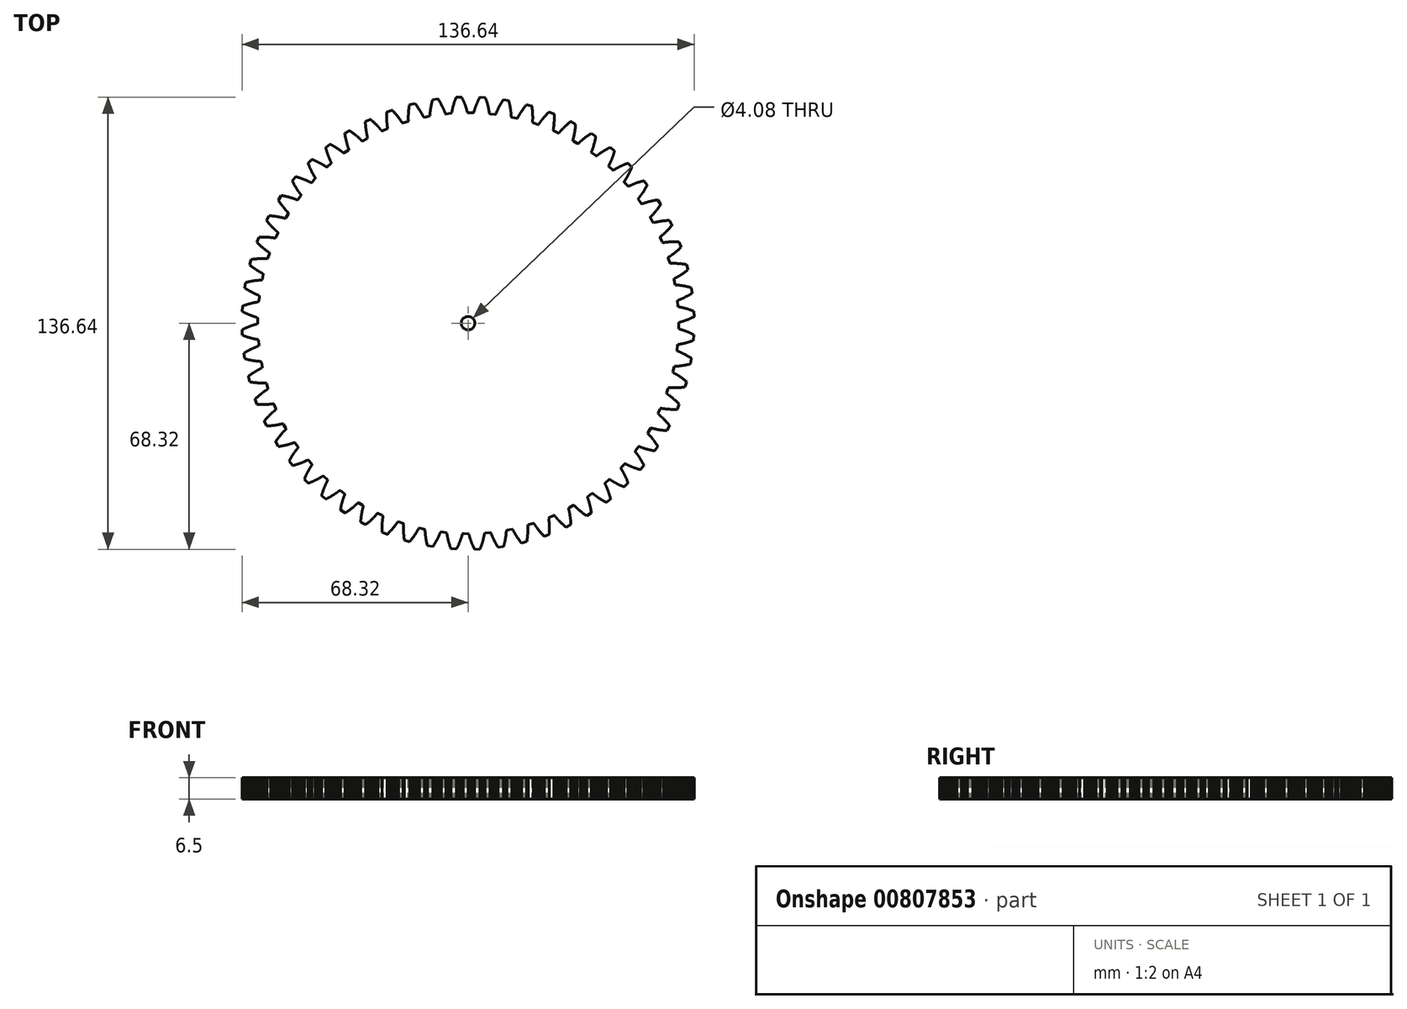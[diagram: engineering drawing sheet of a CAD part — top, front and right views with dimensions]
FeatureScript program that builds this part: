
annotation { "Feature Type Name" : "Feature", "Feature Type Description" : "" }
export const myFeature = defineFeature(function(context is Context, id is Id, definition is map)
    precondition{}
    {
        {
            var Q0;
            Q0=qCreatedBy(makeId("Top.planeOp"),FACE);
            var sketch = newSketch(context, id + "F0", { "sketchPlane" : qUnion([Q0])});
            skLineSegment(sketch, "E0", {"start": v(63.61, 0) * mm, "end": v(63.74, 0.24) * mm});
            skLineSegment(sketch, "E1", {"start": v(63.74, 0.24) * mm, "end": v(63.82, 0.26) * mm});
            skLineSegment(sketch, "E2", {"start": v(63.82, 0.26) * mm, "end": v(63.9, 0.28) * mm});
            skLineSegment(sketch, "E3", {"start": v(63.9, 0.28) * mm, "end": v(63.98, 0.3) * mm});
            skLineSegment(sketch, "E4", {"start": v(63.98, 0.3) * mm, "end": v(64.07, 0.32) * mm});
            skLineSegment(sketch, "E5", {"start": v(64.07, 0.32) * mm, "end": v(64.16, 0.35) * mm});
            skLineSegment(sketch, "E6", {"start": v(64.16, 0.35) * mm, "end": v(64.25, 0.37) * mm});
            skLineSegment(sketch, "E7", {"start": v(64.25, 0.37) * mm, "end": v(64.34, 0.4) * mm});
            skLineSegment(sketch, "E8", {"start": v(64.34, 0.4) * mm, "end": v(64.44, 0.42) * mm});
            skLineSegment(sketch, "E9", {"start": v(64.44, 0.42) * mm, "end": v(64.53, 0.45) * mm});
            skLineSegment(sketch, "E10", {"start": v(64.53, 0.45) * mm, "end": v(64.63, 0.48) * mm});
            skLineSegment(sketch, "E11", {"start": v(64.63, 0.48) * mm, "end": v(64.73, 0.5) * mm});
            skLineSegment(sketch, "E12", {"start": v(64.73, 0.5) * mm, "end": v(64.83, 0.54) * mm});
            skLineSegment(sketch, "E13", {"start": v(64.83, 0.54) * mm, "end": v(64.94, 0.57) * mm});
            skLineSegment(sketch, "E14", {"start": v(64.94, 0.57) * mm, "end": v(65.15, 0.64) * mm});
            skLineSegment(sketch, "E15", {"start": v(65.15, 0.64) * mm, "end": v(65.37, 0.7) * mm});
            skLineSegment(sketch, "E16", {"start": v(65.37, 0.7) * mm, "end": v(65.48, 0.75) * mm});
            skLineSegment(sketch, "E17", {"start": v(65.48, 0.75) * mm, "end": v(65.6, 0.79) * mm});
            skLineSegment(sketch, "E18", {"start": v(65.6, 0.79) * mm, "end": v(65.71, 0.83) * mm});
            skLineSegment(sketch, "E19", {"start": v(65.71, 0.83) * mm, "end": v(65.83, 0.87) * mm});
            skLineSegment(sketch, "E20", {"start": v(65.83, 0.87) * mm, "end": v(65.95, 0.91) * mm});
            skLineSegment(sketch, "E21", {"start": v(65.95, 0.91) * mm, "end": v(66.07, 0.96) * mm});
            skLineSegment(sketch, "E22", {"start": v(66.07, 0.96) * mm, "end": v(66.2, 1) * mm});
            skLineSegment(sketch, "E23", {"start": v(66.2, 1) * mm, "end": v(66.32, 1.05) * mm});
            skLineSegment(sketch, "E24", {"start": v(66.32, 1.05) * mm, "end": v(66.44, 1.1) * mm});
            skLineSegment(sketch, "E25", {"start": v(66.44, 1.1) * mm, "end": v(66.57, 1.16) * mm});
            skLineSegment(sketch, "E26", {"start": v(66.57, 1.16) * mm, "end": v(66.7, 1.2) * mm});
            skLineSegment(sketch, "E27", {"start": v(66.7, 1.2) * mm, "end": v(66.83, 1.26) * mm});
            skLineSegment(sketch, "E28", {"start": v(66.83, 1.26) * mm, "end": v(66.96, 1.32) * mm});
            skLineSegment(sketch, "E29", {"start": v(66.96, 1.32) * mm, "end": v(67.1, 1.38) * mm});
            skLineSegment(sketch, "E30", {"start": v(67.1, 1.38) * mm, "end": v(67.24, 1.44) * mm});
            skLineSegment(sketch, "E31", {"start": v(67.24, 1.44) * mm, "end": v(67.37, 1.5) * mm});
            skLineSegment(sketch, "E32", {"start": v(67.37, 1.5) * mm, "end": v(67.51, 1.56) * mm});
            skLineSegment(sketch, "E33", {"start": v(67.51, 1.56) * mm, "end": v(67.8, 1.69) * mm});
            skLineSegment(sketch, "E34", {"start": v(67.8, 1.69) * mm, "end": v(67.94, 1.76) * mm});
            skLineSegment(sketch, "E35", {"start": v(67.94, 1.76) * mm, "end": v(68.08, 1.83) * mm});
            skLineSegment(sketch, "E36", {"start": v(68.08, 1.83) * mm, "end": v(68.23, 1.9) * mm});
            skLineSegment(sketch, "E37", {"start": v(68.23, 1.9) * mm, "end": v(68.32, 1.97) * mm});
            skLineSegment(sketch, "E38", {"start": v(68.32, 1.97) * mm, "end": v(68.26, 3.6) * mm});
            skLineSegment(sketch, "E39", {"start": v(68.26, 3.6) * mm, "end": v(68.16, 3.66) * mm});
            skLineSegment(sketch, "E40", {"start": v(68.16, 3.66) * mm, "end": v(67.86, 3.77) * mm});
            skLineSegment(sketch, "E41", {"start": v(67.86, 3.77) * mm, "end": v(67.7, 3.83) * mm});
            skLineSegment(sketch, "E42", {"start": v(67.7, 3.83) * mm, "end": v(67.56, 3.88) * mm});
            skLineSegment(sketch, "E43", {"start": v(67.56, 3.88) * mm, "end": v(67.42, 3.94) * mm});
            skLineSegment(sketch, "E44", {"start": v(67.42, 3.94) * mm, "end": v(67.27, 3.99) * mm});
            skLineSegment(sketch, "E45", {"start": v(67.27, 3.99) * mm, "end": v(67.13, 4.04) * mm});
            skLineSegment(sketch, "E46", {"start": v(67.13, 4.04) * mm, "end": v(66.99, 4.08) * mm});
            skLineSegment(sketch, "E47", {"start": v(66.99, 4.08) * mm, "end": v(66.85, 4.13) * mm});
            skLineSegment(sketch, "E48", {"start": v(66.85, 4.13) * mm, "end": v(66.71, 4.18) * mm});
            skLineSegment(sketch, "E49", {"start": v(66.71, 4.18) * mm, "end": v(66.58, 4.22) * mm});
            skLineSegment(sketch, "E50", {"start": v(66.58, 4.22) * mm, "end": v(66.44, 4.26) * mm});
            skLineSegment(sketch, "E51", {"start": v(66.44, 4.26) * mm, "end": v(66.31, 4.3) * mm});
            skLineSegment(sketch, "E52", {"start": v(66.31, 4.3) * mm, "end": v(66.18, 4.34) * mm});
            skLineSegment(sketch, "E53", {"start": v(66.18, 4.34) * mm, "end": v(66.05, 4.38) * mm});
            skLineSegment(sketch, "E54", {"start": v(66.05, 4.38) * mm, "end": v(65.93, 4.42) * mm});
            skLineSegment(sketch, "E55", {"start": v(65.93, 4.42) * mm, "end": v(65.8, 4.45) * mm});
            skLineSegment(sketch, "E56", {"start": v(65.8, 4.45) * mm, "end": v(65.68, 4.49) * mm});
            skLineSegment(sketch, "E57", {"start": v(65.68, 4.49) * mm, "end": v(65.56, 4.52) * mm});
            skLineSegment(sketch, "E58", {"start": v(65.56, 4.52) * mm, "end": v(65.44, 4.55) * mm});
            skLineSegment(sketch, "E59", {"start": v(65.44, 4.55) * mm, "end": v(65.32, 4.58) * mm});
            skLineSegment(sketch, "E60", {"start": v(65.32, 4.58) * mm, "end": v(65.21, 4.6) * mm});
            skLineSegment(sketch, "E61", {"start": v(65.21, 4.6) * mm, "end": v(65.1, 4.64) * mm});
            skLineSegment(sketch, "E62", {"start": v(65.1, 4.64) * mm, "end": v(64.98, 4.66) * mm});
            skLineSegment(sketch, "E63", {"start": v(64.98, 4.66) * mm, "end": v(64.88, 4.69) * mm});
            skLineSegment(sketch, "E64", {"start": v(64.88, 4.69) * mm, "end": v(64.77, 4.71) * mm});
            skLineSegment(sketch, "E65", {"start": v(64.77, 4.71) * mm, "end": v(64.66, 4.74) * mm});
            skLineSegment(sketch, "E66", {"start": v(64.66, 4.74) * mm, "end": v(64.56, 4.76) * mm});
            skLineSegment(sketch, "E67", {"start": v(64.56, 4.76) * mm, "end": v(64.46, 4.78) * mm});
            skLineSegment(sketch, "E68", {"start": v(64.46, 4.78) * mm, "end": v(64.36, 4.8) * mm});
            skLineSegment(sketch, "E69", {"start": v(64.36, 4.8) * mm, "end": v(64.26, 4.82) * mm});
            skLineSegment(sketch, "E70", {"start": v(64.26, 4.82) * mm, "end": v(64.16, 4.84) * mm});
            skLineSegment(sketch, "E71", {"start": v(64.16, 4.84) * mm, "end": v(64.07, 4.86) * mm});
            skLineSegment(sketch, "E72", {"start": v(64.07, 4.86) * mm, "end": v(63.98, 4.87) * mm});
            skLineSegment(sketch, "E73", {"start": v(63.98, 4.87) * mm, "end": v(63.89, 4.89) * mm});
            skLineSegment(sketch, "E74", {"start": v(63.89, 4.89) * mm, "end": v(63.8, 4.9) * mm});
            skLineSegment(sketch, "E75", {"start": v(63.8, 4.9) * mm, "end": v(63.71, 4.92) * mm});
            skLineSegment(sketch, "E76", {"start": v(63.71, 4.92) * mm, "end": v(63.63, 4.93) * mm});
            skLineSegment(sketch, "E77", {"start": v(63.63, 4.93) * mm, "end": v(63.54, 4.94) * mm});
            skLineSegment(sketch, "E78", {"start": v(63.54, 4.94) * mm, "end": v(63.4, 5.17) * mm});
            skLineSegment(sketch, "E79", {"start": v(63.4, 5.17) * mm, "end": v(63.26, 6.65) * mm});
            skLineSegment(sketch, "E80", {"start": v(63.26, 6.65) * mm, "end": v(63.36, 6.9) * mm});
            skLineSegment(sketch, "E81", {"start": v(63.36, 6.9) * mm, "end": v(63.44, 6.93) * mm});
            skLineSegment(sketch, "E82", {"start": v(63.44, 6.93) * mm, "end": v(63.52, 6.96) * mm});
            skLineSegment(sketch, "E83", {"start": v(63.52, 6.96) * mm, "end": v(63.6, 6.99) * mm});
            skLineSegment(sketch, "E84", {"start": v(63.6, 6.99) * mm, "end": v(63.69, 7.02) * mm});
            skLineSegment(sketch, "E85", {"start": v(63.69, 7.02) * mm, "end": v(63.77, 7.05) * mm});
            skLineSegment(sketch, "E86", {"start": v(63.77, 7.05) * mm, "end": v(63.86, 7.08) * mm});
            skLineSegment(sketch, "E87", {"start": v(63.86, 7.08) * mm, "end": v(63.95, 7.12) * mm});
            skLineSegment(sketch, "E88", {"start": v(63.95, 7.12) * mm, "end": v(64.04, 7.15) * mm});
            skLineSegment(sketch, "E89", {"start": v(64.04, 7.15) * mm, "end": v(64.13, 7.2) * mm});
            skLineSegment(sketch, "E90", {"start": v(64.13, 7.2) * mm, "end": v(64.23, 7.23) * mm});
            skLineSegment(sketch, "E91", {"start": v(64.23, 7.23) * mm, "end": v(64.32, 7.27) * mm});
            skLineSegment(sketch, "E92", {"start": v(64.32, 7.27) * mm, "end": v(64.42, 7.31) * mm});
            skLineSegment(sketch, "E93", {"start": v(64.42, 7.31) * mm, "end": v(64.52, 7.35) * mm});
            skLineSegment(sketch, "E94", {"start": v(64.52, 7.35) * mm, "end": v(64.62, 7.4) * mm});
            skLineSegment(sketch, "E95", {"start": v(64.62, 7.4) * mm, "end": v(64.73, 7.44) * mm});
            skLineSegment(sketch, "E96", {"start": v(64.73, 7.44) * mm, "end": v(64.83, 7.49) * mm});
            skLineSegment(sketch, "E97", {"start": v(64.83, 7.49) * mm, "end": v(64.94, 7.54) * mm});
            skLineSegment(sketch, "E98", {"start": v(64.94, 7.54) * mm, "end": v(65.04, 7.59) * mm});
            skLineSegment(sketch, "E99", {"start": v(65.04, 7.59) * mm, "end": v(65.15, 7.64) * mm});
            skLineSegment(sketch, "E100", {"start": v(65.15, 7.64) * mm, "end": v(65.27, 7.7) * mm});
            skLineSegment(sketch, "E101", {"start": v(65.27, 7.7) * mm, "end": v(65.38, 7.75) * mm});
            skLineSegment(sketch, "E102", {"start": v(65.38, 7.75) * mm, "end": v(65.5, 7.8) * mm});
            skLineSegment(sketch, "E103", {"start": v(65.5, 7.8) * mm, "end": v(65.6, 7.86) * mm});
            skLineSegment(sketch, "E104", {"start": v(65.6, 7.86) * mm, "end": v(65.72, 7.92) * mm});
            skLineSegment(sketch, "E105", {"start": v(65.72, 7.92) * mm, "end": v(65.96, 8.04) * mm});
            skLineSegment(sketch, "E106", {"start": v(65.96, 8.04) * mm, "end": v(66.09, 8.1) * mm});
            skLineSegment(sketch, "E107", {"start": v(66.09, 8.1) * mm, "end": v(66.2, 8.17) * mm});
            skLineSegment(sketch, "E108", {"start": v(66.2, 8.17) * mm, "end": v(66.33, 8.24) * mm});
            skLineSegment(sketch, "E109", {"start": v(66.33, 8.24) * mm, "end": v(66.46, 8.31) * mm});
            skLineSegment(sketch, "E110", {"start": v(66.46, 8.31) * mm, "end": v(66.59, 8.38) * mm});
            skLineSegment(sketch, "E111", {"start": v(66.59, 8.38) * mm, "end": v(66.72, 8.46) * mm});
            skLineSegment(sketch, "E112", {"start": v(66.72, 8.46) * mm, "end": v(66.85, 8.53) * mm});
            skLineSegment(sketch, "E113", {"start": v(66.85, 8.53) * mm, "end": v(66.98, 8.6) * mm});
            skLineSegment(sketch, "E114", {"start": v(66.98, 8.6) * mm, "end": v(67.11, 8.69) * mm});
            skLineSegment(sketch, "E115", {"start": v(67.11, 8.69) * mm, "end": v(67.25, 8.77) * mm});
            skLineSegment(sketch, "E116", {"start": v(67.25, 8.77) * mm, "end": v(67.38, 8.85) * mm});
            skLineSegment(sketch, "E117", {"start": v(67.38, 8.85) * mm, "end": v(67.52, 8.93) * mm});
            skLineSegment(sketch, "E118", {"start": v(67.52, 8.93) * mm, "end": v(67.66, 9.02) * mm});
            skLineSegment(sketch, "E119", {"start": v(67.66, 9.02) * mm, "end": v(67.74, 9.1) * mm});
            skLineSegment(sketch, "E120", {"start": v(67.74, 9.1) * mm, "end": v(67.5, 10.7) * mm});
            skLineSegment(sketch, "E121", {"start": v(67.5, 10.7) * mm, "end": v(67.4, 10.76) * mm});
            skLineSegment(sketch, "E122", {"start": v(67.4, 10.76) * mm, "end": v(67.25, 10.8) * mm});
            skLineSegment(sketch, "E123", {"start": v(67.25, 10.8) * mm, "end": v(67.09, 10.85) * mm});
            skLineSegment(sketch, "E124", {"start": v(67.09, 10.85) * mm, "end": v(66.94, 10.89) * mm});
            skLineSegment(sketch, "E125", {"start": v(66.94, 10.89) * mm, "end": v(66.78, 10.93) * mm});
            skLineSegment(sketch, "E126", {"start": v(66.78, 10.93) * mm, "end": v(66.64, 10.96) * mm});
            skLineSegment(sketch, "E127", {"start": v(66.64, 10.96) * mm, "end": v(66.49, 11) * mm});
            skLineSegment(sketch, "E128", {"start": v(66.49, 11) * mm, "end": v(66.34, 11.03) * mm});
            skLineSegment(sketch, "E129", {"start": v(66.34, 11.03) * mm, "end": v(66.2, 11.06) * mm});
            skLineSegment(sketch, "E130", {"start": v(66.2, 11.06) * mm, "end": v(66.05, 11.1) * mm});
            skLineSegment(sketch, "E131", {"start": v(66.05, 11.1) * mm, "end": v(65.91, 11.13) * mm});
            skLineSegment(sketch, "E132", {"start": v(65.91, 11.13) * mm, "end": v(65.77, 11.16) * mm});
            skLineSegment(sketch, "E133", {"start": v(65.77, 11.16) * mm, "end": v(65.64, 11.18) * mm});
            skLineSegment(sketch, "E134", {"start": v(65.64, 11.18) * mm, "end": v(65.5, 11.21) * mm});
            skLineSegment(sketch, "E135", {"start": v(65.5, 11.21) * mm, "end": v(65.37, 11.24) * mm});
            skLineSegment(sketch, "E136", {"start": v(65.37, 11.24) * mm, "end": v(65.23, 11.26) * mm});
            skLineSegment(sketch, "E137", {"start": v(65.23, 11.26) * mm, "end": v(65.1, 11.28) * mm});
            skLineSegment(sketch, "E138", {"start": v(65.1, 11.28) * mm, "end": v(64.98, 11.3) * mm});
            skLineSegment(sketch, "E139", {"start": v(64.98, 11.3) * mm, "end": v(64.85, 11.33) * mm});
            skLineSegment(sketch, "E140", {"start": v(64.85, 11.33) * mm, "end": v(64.73, 11.35) * mm});
            skLineSegment(sketch, "E141", {"start": v(64.73, 11.35) * mm, "end": v(64.6, 11.37) * mm});
            skLineSegment(sketch, "E142", {"start": v(64.6, 11.37) * mm, "end": v(64.49, 11.38) * mm});
            skLineSegment(sketch, "E143", {"start": v(64.49, 11.38) * mm, "end": v(64.37, 11.4) * mm});
            skLineSegment(sketch, "E144", {"start": v(64.37, 11.4) * mm, "end": v(64.26, 11.42) * mm});
            skLineSegment(sketch, "E145", {"start": v(64.26, 11.42) * mm, "end": v(64.14, 11.43) * mm});
            skLineSegment(sketch, "E146", {"start": v(64.14, 11.43) * mm, "end": v(64.03, 11.44) * mm});
            skLineSegment(sketch, "E147", {"start": v(64.03, 11.44) * mm, "end": v(63.92, 11.46) * mm});
            skLineSegment(sketch, "E148", {"start": v(63.92, 11.46) * mm, "end": v(63.81, 11.47) * mm});
            skLineSegment(sketch, "E149", {"start": v(63.81, 11.47) * mm, "end": v(63.7, 11.48) * mm});
            skLineSegment(sketch, "E150", {"start": v(63.7, 11.48) * mm, "end": v(63.6, 11.5) * mm});
            skLineSegment(sketch, "E151", {"start": v(63.6, 11.5) * mm, "end": v(63.5, 11.5) * mm});
            skLineSegment(sketch, "E152", {"start": v(63.5, 11.5) * mm, "end": v(63.4, 11.51) * mm});
            skLineSegment(sketch, "E153", {"start": v(63.4, 11.51) * mm, "end": v(63.3, 11.52) * mm});
            skLineSegment(sketch, "E154", {"start": v(63.3, 11.52) * mm, "end": v(63.2, 11.53) * mm});
            skLineSegment(sketch, "E155", {"start": v(63.2, 11.53) * mm, "end": v(63.12, 11.53) * mm});
            skLineSegment(sketch, "E156", {"start": v(63.12, 11.53) * mm, "end": v(63.02, 11.54) * mm});
            skLineSegment(sketch, "E157", {"start": v(63.02, 11.54) * mm, "end": v(62.93, 11.55) * mm});
            skLineSegment(sketch, "E158", {"start": v(62.93, 11.55) * mm, "end": v(62.85, 11.55) * mm});
            skLineSegment(sketch, "E159", {"start": v(62.85, 11.55) * mm, "end": v(62.76, 11.55) * mm});
            skLineSegment(sketch, "E160", {"start": v(62.76, 11.55) * mm, "end": v(62.68, 11.56) * mm});
            skLineSegment(sketch, "E161", {"start": v(62.68, 11.56) * mm, "end": v(62.51, 11.77) * mm});
            skLineSegment(sketch, "E162", {"start": v(62.51, 11.77) * mm, "end": v(62.22, 13.22) * mm});
            skLineSegment(sketch, "E163", {"start": v(62.22, 13.22) * mm, "end": v(62.3, 13.49) * mm});
            skLineSegment(sketch, "E164", {"start": v(62.3, 13.49) * mm, "end": v(62.37, 13.52) * mm});
            skLineSegment(sketch, "E165", {"start": v(62.37, 13.52) * mm, "end": v(62.45, 13.56) * mm});
            skLineSegment(sketch, "E166", {"start": v(62.45, 13.56) * mm, "end": v(62.52, 13.6) * mm});
            skLineSegment(sketch, "E167", {"start": v(62.52, 13.6) * mm, "end": v(62.6, 13.64) * mm});
            skLineSegment(sketch, "E168", {"start": v(62.6, 13.64) * mm, "end": v(62.69, 13.68) * mm});
            skLineSegment(sketch, "E169", {"start": v(62.69, 13.68) * mm, "end": v(62.77, 13.72) * mm});
            skLineSegment(sketch, "E170", {"start": v(62.77, 13.72) * mm, "end": v(62.86, 13.76) * mm});
            skLineSegment(sketch, "E171", {"start": v(62.86, 13.76) * mm, "end": v(62.94, 13.8) * mm});
            skLineSegment(sketch, "E172", {"start": v(62.94, 13.8) * mm, "end": v(63.03, 13.85) * mm});
            skLineSegment(sketch, "E173", {"start": v(63.03, 13.85) * mm, "end": v(63.12, 13.9) * mm});
            skLineSegment(sketch, "E174", {"start": v(63.12, 13.9) * mm, "end": v(63.21, 13.95) * mm});
            skLineSegment(sketch, "E175", {"start": v(63.21, 13.95) * mm, "end": v(63.3, 14) * mm});
            skLineSegment(sketch, "E176", {"start": v(63.3, 14) * mm, "end": v(63.4, 14.06) * mm});
            skLineSegment(sketch, "E177", {"start": v(63.4, 14.06) * mm, "end": v(63.5, 14.11) * mm});
            skLineSegment(sketch, "E178", {"start": v(63.5, 14.11) * mm, "end": v(63.6, 14.17) * mm});
            skLineSegment(sketch, "E179", {"start": v(63.6, 14.17) * mm, "end": v(63.7, 14.23) * mm});
            skLineSegment(sketch, "E180", {"start": v(63.7, 14.23) * mm, "end": v(63.8, 14.28) * mm});
            skLineSegment(sketch, "E181", {"start": v(63.8, 14.28) * mm, "end": v(63.9, 14.35) * mm});
            skLineSegment(sketch, "E182", {"start": v(63.9, 14.35) * mm, "end": v(64, 14.4) * mm});
            skLineSegment(sketch, "E183", {"start": v(64, 14.4) * mm, "end": v(64.1, 14.47) * mm});
            skLineSegment(sketch, "E184", {"start": v(64.1, 14.47) * mm, "end": v(64.2, 14.54) * mm});
            skLineSegment(sketch, "E185", {"start": v(64.2, 14.54) * mm, "end": v(64.32, 14.6) * mm});
            skLineSegment(sketch, "E186", {"start": v(64.32, 14.6) * mm, "end": v(64.43, 14.67) * mm});
            skLineSegment(sketch, "E187", {"start": v(64.43, 14.67) * mm, "end": v(64.54, 14.75) * mm});
            skLineSegment(sketch, "E188", {"start": v(64.54, 14.75) * mm, "end": v(64.65, 14.82) * mm});
            skLineSegment(sketch, "E189", {"start": v(64.65, 14.82) * mm, "end": v(64.76, 14.9) * mm});
            skLineSegment(sketch, "E190", {"start": v(64.76, 14.9) * mm, "end": v(64.88, 14.97) * mm});
            skLineSegment(sketch, "E191", {"start": v(64.88, 14.97) * mm, "end": v(65, 15.05) * mm});
            skLineSegment(sketch, "E192", {"start": v(65, 15.05) * mm, "end": v(65.23, 15.21) * mm});
            skLineSegment(sketch, "E193", {"start": v(65.23, 15.21) * mm, "end": v(65.35, 15.3) * mm});
            skLineSegment(sketch, "E194", {"start": v(65.35, 15.3) * mm, "end": v(65.47, 15.38) * mm});
            skLineSegment(sketch, "E195", {"start": v(65.47, 15.38) * mm, "end": v(65.59, 15.47) * mm});
            skLineSegment(sketch, "E196", {"start": v(65.59, 15.47) * mm, "end": v(65.71, 15.56) * mm});
            skLineSegment(sketch, "E197", {"start": v(65.71, 15.56) * mm, "end": v(65.84, 15.65) * mm});
            skLineSegment(sketch, "E198", {"start": v(65.84, 15.65) * mm, "end": v(65.96, 15.75) * mm});
            skLineSegment(sketch, "E199", {"start": v(65.96, 15.75) * mm, "end": v(66.09, 15.84) * mm});
            skLineSegment(sketch, "E200", {"start": v(66.09, 15.84) * mm, "end": v(66.22, 15.94) * mm});
            skLineSegment(sketch, "E201", {"start": v(66.22, 15.94) * mm, "end": v(66.35, 16.04) * mm});
            skLineSegment(sketch, "E202", {"start": v(66.35, 16.04) * mm, "end": v(66.42, 16.13) * mm});
            skLineSegment(sketch, "E203", {"start": v(66.42, 16.13) * mm, "end": v(66.02, 17.7) * mm});
            skLineSegment(sketch, "E204", {"start": v(66.02, 17.7) * mm, "end": v(65.9, 17.75) * mm});
            skLineSegment(sketch, "E205", {"start": v(65.9, 17.75) * mm, "end": v(65.75, 17.78) * mm});
            skLineSegment(sketch, "E206", {"start": v(65.75, 17.78) * mm, "end": v(65.59, 17.8) * mm});
            skLineSegment(sketch, "E207", {"start": v(65.59, 17.8) * mm, "end": v(65.43, 17.82) * mm});
            skLineSegment(sketch, "E208", {"start": v(65.43, 17.82) * mm, "end": v(65.28, 17.85) * mm});
            skLineSegment(sketch, "E209", {"start": v(65.28, 17.85) * mm, "end": v(65.12, 17.87) * mm});
            skLineSegment(sketch, "E210", {"start": v(65.12, 17.87) * mm, "end": v(64.97, 17.89) * mm});
            skLineSegment(sketch, "E211", {"start": v(64.97, 17.89) * mm, "end": v(64.82, 17.9) * mm});
            skLineSegment(sketch, "E212", {"start": v(64.82, 17.9) * mm, "end": v(64.68, 17.92) * mm});
            skLineSegment(sketch, "E213", {"start": v(64.68, 17.92) * mm, "end": v(64.53, 17.94) * mm});
            skLineSegment(sketch, "E214", {"start": v(64.53, 17.94) * mm, "end": v(64.39, 17.96) * mm});
            skLineSegment(sketch, "E215", {"start": v(64.39, 17.96) * mm, "end": v(64.25, 17.97) * mm});
            skLineSegment(sketch, "E216", {"start": v(64.25, 17.97) * mm, "end": v(64.1, 17.98) * mm});
            skLineSegment(sketch, "E217", {"start": v(64.1, 17.98) * mm, "end": v(63.97, 18) * mm});
            skLineSegment(sketch, "E218", {"start": v(63.97, 18) * mm, "end": v(63.83, 18) * mm});
            skLineSegment(sketch, "E219", {"start": v(63.83, 18) * mm, "end": v(63.7, 18.02) * mm});
            skLineSegment(sketch, "E220", {"start": v(63.7, 18.02) * mm, "end": v(63.57, 18.03) * mm});
            skLineSegment(sketch, "E221", {"start": v(63.57, 18.03) * mm, "end": v(63.44, 18.04) * mm});
            skLineSegment(sketch, "E222", {"start": v(63.44, 18.04) * mm, "end": v(63.31, 18.04) * mm});
            skLineSegment(sketch, "E223", {"start": v(63.31, 18.04) * mm, "end": v(63.19, 18.05) * mm});
            skLineSegment(sketch, "E224", {"start": v(63.19, 18.05) * mm, "end": v(63.07, 18.06) * mm});
            skLineSegment(sketch, "E225", {"start": v(63.07, 18.06) * mm, "end": v(62.94, 18.06) * mm});
            skLineSegment(sketch, "E226", {"start": v(62.94, 18.06) * mm, "end": v(62.83, 18.07) * mm});
            skLineSegment(sketch, "E227", {"start": v(62.83, 18.07) * mm, "end": v(62.7, 18.07) * mm});
            skLineSegment(sketch, "E228", {"start": v(62.7, 18.07) * mm, "end": v(62.6, 18.07) * mm});
            skLineSegment(sketch, "E229", {"start": v(62.6, 18.07) * mm, "end": v(62.48, 18.08) * mm});
            skLineSegment(sketch, "E230", {"start": v(62.48, 18.08) * mm, "end": v(62.37, 18.08) * mm});
            skLineSegment(sketch, "E231", {"start": v(62.37, 18.08) * mm, "end": v(62.26, 18.08) * mm});
            skLineSegment(sketch, "E232", {"start": v(62.26, 18.08) * mm, "end": v(62.05, 18.08) * mm});
            skLineSegment(sketch, "E233", {"start": v(62.05, 18.08) * mm, "end": v(61.95, 18.08) * mm});
            skLineSegment(sketch, "E234", {"start": v(61.95, 18.08) * mm, "end": v(61.85, 18.08) * mm});
            skLineSegment(sketch, "E235", {"start": v(61.85, 18.08) * mm, "end": v(61.75, 18.07) * mm});
            skLineSegment(sketch, "E236", {"start": v(61.75, 18.07) * mm, "end": v(61.66, 18.07) * mm});
            skLineSegment(sketch, "E237", {"start": v(61.66, 18.07) * mm, "end": v(61.56, 18.07) * mm});
            skLineSegment(sketch, "E238", {"start": v(61.56, 18.07) * mm, "end": v(61.47, 18.06) * mm});
            skLineSegment(sketch, "E239", {"start": v(61.47, 18.06) * mm, "end": v(61.38, 18.06) * mm});
            skLineSegment(sketch, "E240", {"start": v(61.38, 18.06) * mm, "end": v(61.3, 18.06) * mm});
            skLineSegment(sketch, "E241", {"start": v(61.3, 18.06) * mm, "end": v(61.21, 18.05) * mm});
            skLineSegment(sketch, "E242", {"start": v(61.21, 18.05) * mm, "end": v(61.13, 18.05) * mm});
            skLineSegment(sketch, "E243", {"start": v(61.13, 18.05) * mm, "end": v(60.94, 18.24) * mm});
            skLineSegment(sketch, "E244", {"start": v(60.94, 18.24) * mm, "end": v(60.5, 19.66) * mm});
            skLineSegment(sketch, "E245", {"start": v(60.5, 19.66) * mm, "end": v(60.54, 19.92) * mm});
            skLineSegment(sketch, "E246", {"start": v(60.54, 19.92) * mm, "end": v(60.61, 19.97) * mm});
            skLineSegment(sketch, "E247", {"start": v(60.61, 19.97) * mm, "end": v(60.69, 20.01) * mm});
            skLineSegment(sketch, "E248", {"start": v(60.69, 20.01) * mm, "end": v(60.76, 20.06) * mm});
            skLineSegment(sketch, "E249", {"start": v(60.76, 20.06) * mm, "end": v(60.84, 20.1) * mm});
            skLineSegment(sketch, "E250", {"start": v(60.84, 20.1) * mm, "end": v(60.91, 20.16) * mm});
            skLineSegment(sketch, "E251", {"start": v(60.91, 20.16) * mm, "end": v(61, 20.2) * mm});
            skLineSegment(sketch, "E252", {"start": v(61, 20.2) * mm, "end": v(61.07, 20.26) * mm});
            skLineSegment(sketch, "E253", {"start": v(61.07, 20.26) * mm, "end": v(61.15, 20.31) * mm});
            skLineSegment(sketch, "E254", {"start": v(61.15, 20.31) * mm, "end": v(61.24, 20.37) * mm});
            skLineSegment(sketch, "E255", {"start": v(61.24, 20.37) * mm, "end": v(61.32, 20.43) * mm});
            skLineSegment(sketch, "E256", {"start": v(61.32, 20.43) * mm, "end": v(61.4, 20.48) * mm});
            skLineSegment(sketch, "E257", {"start": v(61.4, 20.48) * mm, "end": v(61.5, 20.55) * mm});
            skLineSegment(sketch, "E258", {"start": v(61.5, 20.55) * mm, "end": v(61.58, 20.6) * mm});
            skLineSegment(sketch, "E259", {"start": v(61.58, 20.6) * mm, "end": v(61.67, 20.67) * mm});
            skLineSegment(sketch, "E260", {"start": v(61.67, 20.67) * mm, "end": v(61.76, 20.74) * mm});
            skLineSegment(sketch, "E261", {"start": v(61.76, 20.74) * mm, "end": v(61.86, 20.8) * mm});
            skLineSegment(sketch, "E262", {"start": v(61.86, 20.8) * mm, "end": v(61.95, 20.87) * mm});
            skLineSegment(sketch, "E263", {"start": v(61.95, 20.87) * mm, "end": v(62.04, 20.94) * mm});
            skLineSegment(sketch, "E264", {"start": v(62.04, 20.94) * mm, "end": v(62.14, 21.02) * mm});
            skLineSegment(sketch, "E265", {"start": v(62.14, 21.02) * mm, "end": v(62.24, 21.1) * mm});
            skLineSegment(sketch, "E266", {"start": v(62.24, 21.1) * mm, "end": v(62.34, 21.17) * mm});
            skLineSegment(sketch, "E267", {"start": v(62.34, 21.17) * mm, "end": v(62.44, 21.25) * mm});
            skLineSegment(sketch, "E268", {"start": v(62.44, 21.25) * mm, "end": v(62.54, 21.33) * mm});
            skLineSegment(sketch, "E269", {"start": v(62.54, 21.33) * mm, "end": v(62.64, 21.41) * mm});
            skLineSegment(sketch, "E270", {"start": v(62.64, 21.41) * mm, "end": v(62.74, 21.5) * mm});
            skLineSegment(sketch, "E271", {"start": v(62.74, 21.5) * mm, "end": v(62.85, 21.58) * mm});
            skLineSegment(sketch, "E272", {"start": v(62.85, 21.58) * mm, "end": v(62.96, 21.67) * mm});
            skLineSegment(sketch, "E273", {"start": v(62.96, 21.67) * mm, "end": v(63.06, 21.76) * mm});
            skLineSegment(sketch, "E274", {"start": v(63.06, 21.76) * mm, "end": v(63.17, 21.85) * mm});
            skLineSegment(sketch, "E275", {"start": v(63.17, 21.85) * mm, "end": v(63.28, 21.95) * mm});
            skLineSegment(sketch, "E276", {"start": v(63.28, 21.95) * mm, "end": v(63.39, 22.04) * mm});
            skLineSegment(sketch, "E277", {"start": v(63.39, 22.04) * mm, "end": v(63.5, 22.14) * mm});
            skLineSegment(sketch, "E278", {"start": v(63.5, 22.14) * mm, "end": v(63.61, 22.24) * mm});
            skLineSegment(sketch, "E279", {"start": v(63.61, 22.24) * mm, "end": v(63.73, 22.34) * mm});
            skLineSegment(sketch, "E280", {"start": v(63.73, 22.34) * mm, "end": v(63.84, 22.45) * mm});
            skLineSegment(sketch, "E281", {"start": v(63.84, 22.45) * mm, "end": v(63.95, 22.56) * mm});
            skLineSegment(sketch, "E282", {"start": v(63.95, 22.56) * mm, "end": v(64.07, 22.66) * mm});
            skLineSegment(sketch, "E283", {"start": v(64.07, 22.66) * mm, "end": v(64.19, 22.77) * mm});
            skLineSegment(sketch, "E284", {"start": v(64.19, 22.77) * mm, "end": v(64.3, 22.89) * mm});
            skLineSegment(sketch, "E285", {"start": v(64.3, 22.89) * mm, "end": v(64.37, 22.98) * mm});
            skLineSegment(sketch, "E286", {"start": v(64.37, 22.98) * mm, "end": v(63.8, 24.51) * mm});
            skLineSegment(sketch, "E287", {"start": v(63.8, 24.51) * mm, "end": v(63.7, 24.54) * mm});
            skLineSegment(sketch, "E288", {"start": v(63.7, 24.54) * mm, "end": v(63.53, 24.55) * mm});
            skLineSegment(sketch, "E289", {"start": v(63.53, 24.55) * mm, "end": v(63.37, 24.56) * mm});
            skLineSegment(sketch, "E290", {"start": v(63.37, 24.56) * mm, "end": v(63.21, 24.56) * mm});
            skLineSegment(sketch, "E291", {"start": v(63.21, 24.56) * mm, "end": v(63.05, 24.57) * mm});
            skLineSegment(sketch, "E292", {"start": v(63.05, 24.57) * mm, "end": v(62.9, 24.58) * mm});
            skLineSegment(sketch, "E293", {"start": v(62.9, 24.58) * mm, "end": v(62.75, 24.58) * mm});
            skLineSegment(sketch, "E294", {"start": v(62.75, 24.58) * mm, "end": v(62.6, 24.58) * mm});
            skLineSegment(sketch, "E295", {"start": v(62.6, 24.58) * mm, "end": v(62.45, 24.59) * mm});
            skLineSegment(sketch, "E296", {"start": v(62.45, 24.59) * mm, "end": v(62.3, 24.59) * mm});
            skLineSegment(sketch, "E297", {"start": v(62.3, 24.59) * mm, "end": v(62.02, 24.59) * mm});
            skLineSegment(sketch, "E298", {"start": v(62.02, 24.59) * mm, "end": v(61.88, 24.59) * mm});
            skLineSegment(sketch, "E299", {"start": v(61.88, 24.59) * mm, "end": v(61.74, 24.58) * mm});
            skLineSegment(sketch, "E300", {"start": v(61.74, 24.58) * mm, "end": v(61.6, 24.58) * mm});
            skLineSegment(sketch, "E301", {"start": v(61.6, 24.58) * mm, "end": v(61.47, 24.58) * mm});
            skLineSegment(sketch, "E302", {"start": v(61.47, 24.58) * mm, "end": v(61.34, 24.57) * mm});
            skLineSegment(sketch, "E303", {"start": v(61.34, 24.57) * mm, "end": v(61.2, 24.57) * mm});
            skLineSegment(sketch, "E304", {"start": v(61.2, 24.57) * mm, "end": v(61.08, 24.56) * mm});
            skLineSegment(sketch, "E305", {"start": v(61.08, 24.56) * mm, "end": v(60.96, 24.56) * mm});
            skLineSegment(sketch, "E306", {"start": v(60.96, 24.56) * mm, "end": v(60.83, 24.55) * mm});
            skLineSegment(sketch, "E307", {"start": v(60.83, 24.55) * mm, "end": v(60.71, 24.54) * mm});
            skLineSegment(sketch, "E308", {"start": v(60.71, 24.54) * mm, "end": v(60.6, 24.53) * mm});
            skLineSegment(sketch, "E309", {"start": v(60.6, 24.53) * mm, "end": v(60.48, 24.53) * mm});
            skLineSegment(sketch, "E310", {"start": v(60.48, 24.53) * mm, "end": v(60.25, 24.5) * mm});
            skLineSegment(sketch, "E311", {"start": v(60.25, 24.5) * mm, "end": v(60.14, 24.5) * mm});
            skLineSegment(sketch, "E312", {"start": v(60.14, 24.5) * mm, "end": v(60.03, 24.49) * mm});
            skLineSegment(sketch, "E313", {"start": v(60.03, 24.49) * mm, "end": v(59.93, 24.48) * mm});
            skLineSegment(sketch, "E314", {"start": v(59.93, 24.48) * mm, "end": v(59.82, 24.47) * mm});
            skLineSegment(sketch, "E315", {"start": v(59.82, 24.47) * mm, "end": v(59.72, 24.45) * mm});
            skLineSegment(sketch, "E316", {"start": v(59.72, 24.45) * mm, "end": v(59.62, 24.44) * mm});
            skLineSegment(sketch, "E317", {"start": v(59.62, 24.44) * mm, "end": v(59.53, 24.43) * mm});
            skLineSegment(sketch, "E318", {"start": v(59.53, 24.43) * mm, "end": v(59.43, 24.42) * mm});
            skLineSegment(sketch, "E319", {"start": v(59.43, 24.42) * mm, "end": v(59.34, 24.4) * mm});
            skLineSegment(sketch, "E320", {"start": v(59.34, 24.4) * mm, "end": v(59.25, 24.4) * mm});
            skLineSegment(sketch, "E321", {"start": v(59.25, 24.4) * mm, "end": v(59.16, 24.38) * mm});
            skLineSegment(sketch, "E322", {"start": v(59.16, 24.38) * mm, "end": v(59.07, 24.37) * mm});
            skLineSegment(sketch, "E323", {"start": v(59.07, 24.37) * mm, "end": v(58.99, 24.35) * mm});
            skLineSegment(sketch, "E324", {"start": v(58.99, 24.35) * mm, "end": v(58.9, 24.34) * mm});
            skLineSegment(sketch, "E325", {"start": v(58.9, 24.34) * mm, "end": v(58.7, 24.51) * mm});
            skLineSegment(sketch, "E326", {"start": v(58.7, 24.51) * mm, "end": v(58.11, 25.87) * mm});
            skLineSegment(sketch, "E327", {"start": v(58.11, 25.87) * mm, "end": v(58.13, 26.14) * mm});
            skLineSegment(sketch, "E328", {"start": v(58.13, 26.14) * mm, "end": v(58.2, 26.2) * mm});
            skLineSegment(sketch, "E329", {"start": v(58.2, 26.2) * mm, "end": v(58.26, 26.25) * mm});
            skLineSegment(sketch, "E330", {"start": v(58.26, 26.25) * mm, "end": v(58.33, 26.3) * mm});
            skLineSegment(sketch, "E331", {"start": v(58.33, 26.3) * mm, "end": v(58.4, 26.35) * mm});
            skLineSegment(sketch, "E332", {"start": v(58.4, 26.35) * mm, "end": v(58.47, 26.41) * mm});
            skLineSegment(sketch, "E333", {"start": v(58.47, 26.41) * mm, "end": v(58.55, 26.47) * mm});
            skLineSegment(sketch, "E334", {"start": v(58.55, 26.47) * mm, "end": v(58.62, 26.53) * mm});
            skLineSegment(sketch, "E335", {"start": v(58.62, 26.53) * mm, "end": v(58.7, 26.6) * mm});
            skLineSegment(sketch, "E336", {"start": v(58.7, 26.6) * mm, "end": v(58.77, 26.66) * mm});
            skLineSegment(sketch, "E337", {"start": v(58.77, 26.66) * mm, "end": v(58.85, 26.72) * mm});
            skLineSegment(sketch, "E338", {"start": v(58.85, 26.72) * mm, "end": v(58.93, 26.8) * mm});
            skLineSegment(sketch, "E339", {"start": v(58.93, 26.8) * mm, "end": v(59, 26.86) * mm});
            skLineSegment(sketch, "E340", {"start": v(59, 26.86) * mm, "end": v(59.1, 26.93) * mm});
            skLineSegment(sketch, "E341", {"start": v(59.1, 26.93) * mm, "end": v(59.17, 27) * mm});
            skLineSegment(sketch, "E342", {"start": v(59.17, 27) * mm, "end": v(59.26, 27.08) * mm});
            skLineSegment(sketch, "E343", {"start": v(59.26, 27.08) * mm, "end": v(59.34, 27.16) * mm});
            skLineSegment(sketch, "E344", {"start": v(59.34, 27.16) * mm, "end": v(59.43, 27.24) * mm});
            skLineSegment(sketch, "E345", {"start": v(59.43, 27.24) * mm, "end": v(59.52, 27.32) * mm});
            skLineSegment(sketch, "E346", {"start": v(59.52, 27.32) * mm, "end": v(59.6, 27.4) * mm});
            skLineSegment(sketch, "E347", {"start": v(59.6, 27.4) * mm, "end": v(59.7, 27.48) * mm});
            skLineSegment(sketch, "E348", {"start": v(59.7, 27.48) * mm, "end": v(59.78, 27.57) * mm});
            skLineSegment(sketch, "E349", {"start": v(59.78, 27.57) * mm, "end": v(59.87, 27.66) * mm});
            skLineSegment(sketch, "E350", {"start": v(59.87, 27.66) * mm, "end": v(59.97, 27.75) * mm});
            skLineSegment(sketch, "E351", {"start": v(59.97, 27.75) * mm, "end": v(60.06, 27.84) * mm});
            skLineSegment(sketch, "E352", {"start": v(60.06, 27.84) * mm, "end": v(60.15, 27.94) * mm});
            skLineSegment(sketch, "E353", {"start": v(60.15, 27.94) * mm, "end": v(60.25, 28.03) * mm});
            skLineSegment(sketch, "E354", {"start": v(60.25, 28.03) * mm, "end": v(60.35, 28.13) * mm});
            skLineSegment(sketch, "E355", {"start": v(60.35, 28.13) * mm, "end": v(60.44, 28.23) * mm});
            skLineSegment(sketch, "E356", {"start": v(60.44, 28.23) * mm, "end": v(60.54, 28.34) * mm});
            skLineSegment(sketch, "E357", {"start": v(60.54, 28.34) * mm, "end": v(60.64, 28.44) * mm});
            skLineSegment(sketch, "E358", {"start": v(60.64, 28.44) * mm, "end": v(60.74, 28.55) * mm});
            skLineSegment(sketch, "E359", {"start": v(60.74, 28.55) * mm, "end": v(60.94, 28.77) * mm});
            skLineSegment(sketch, "E360", {"start": v(60.94, 28.77) * mm, "end": v(61.04, 28.88) * mm});
            skLineSegment(sketch, "E361", {"start": v(61.04, 28.88) * mm, "end": v(61.14, 29) * mm});
            skLineSegment(sketch, "E362", {"start": v(61.14, 29) * mm, "end": v(61.25, 29.12) * mm});
            skLineSegment(sketch, "E363", {"start": v(61.25, 29.12) * mm, "end": v(61.35, 29.24) * mm});
            skLineSegment(sketch, "E364", {"start": v(61.35, 29.24) * mm, "end": v(61.45, 29.36) * mm});
            skLineSegment(sketch, "E365", {"start": v(61.45, 29.36) * mm, "end": v(61.56, 29.48) * mm});
            skLineSegment(sketch, "E366", {"start": v(61.56, 29.48) * mm, "end": v(61.61, 29.59) * mm});
            skLineSegment(sketch, "E367", {"start": v(61.61, 29.59) * mm, "end": v(60.9, 31.05) * mm});
            skLineSegment(sketch, "E368", {"start": v(60.9, 31.05) * mm, "end": v(60.78, 31.07) * mm});
            skLineSegment(sketch, "E369", {"start": v(60.78, 31.07) * mm, "end": v(60.62, 31.06) * mm});
            skLineSegment(sketch, "E370", {"start": v(60.62, 31.06) * mm, "end": v(60.45, 31.05) * mm});
            skLineSegment(sketch, "E371", {"start": v(60.45, 31.05) * mm, "end": v(60.3, 31.04) * mm});
            skLineSegment(sketch, "E372", {"start": v(60.3, 31.04) * mm, "end": v(60.14, 31.03) * mm});
            skLineSegment(sketch, "E373", {"start": v(60.14, 31.03) * mm, "end": v(59.99, 31.02) * mm});
            skLineSegment(sketch, "E374", {"start": v(59.99, 31.02) * mm, "end": v(59.83, 31) * mm});
            skLineSegment(sketch, "E375", {"start": v(59.83, 31) * mm, "end": v(59.68, 31) * mm});
            skLineSegment(sketch, "E376", {"start": v(59.68, 31) * mm, "end": v(59.54, 30.98) * mm});
            skLineSegment(sketch, "E377", {"start": v(59.54, 30.98) * mm, "end": v(59.4, 30.96) * mm});
            skLineSegment(sketch, "E378", {"start": v(59.4, 30.96) * mm, "end": v(59.25, 30.95) * mm});
            skLineSegment(sketch, "E379", {"start": v(59.25, 30.95) * mm, "end": v(59.1, 30.93) * mm});
            skLineSegment(sketch, "E380", {"start": v(59.1, 30.93) * mm, "end": v(58.97, 30.92) * mm});
            skLineSegment(sketch, "E381", {"start": v(58.97, 30.92) * mm, "end": v(58.83, 30.9) * mm});
            skLineSegment(sketch, "E382", {"start": v(58.83, 30.9) * mm, "end": v(58.7, 30.89) * mm});
            skLineSegment(sketch, "E383", {"start": v(58.7, 30.89) * mm, "end": v(58.56, 30.87) * mm});
            skLineSegment(sketch, "E384", {"start": v(58.56, 30.87) * mm, "end": v(58.43, 30.85) * mm});
            skLineSegment(sketch, "E385", {"start": v(58.43, 30.85) * mm, "end": v(58.3, 30.83) * mm});
            skLineSegment(sketch, "E386", {"start": v(58.3, 30.83) * mm, "end": v(58.18, 30.81) * mm});
            skLineSegment(sketch, "E387", {"start": v(58.18, 30.81) * mm, "end": v(58.06, 30.8) * mm});
            skLineSegment(sketch, "E388", {"start": v(58.06, 30.8) * mm, "end": v(57.93, 30.77) * mm});
            skLineSegment(sketch, "E389", {"start": v(57.93, 30.77) * mm, "end": v(57.81, 30.75) * mm});
            skLineSegment(sketch, "E390", {"start": v(57.81, 30.75) * mm, "end": v(57.7, 30.73) * mm});
            skLineSegment(sketch, "E391", {"start": v(57.7, 30.73) * mm, "end": v(57.58, 30.71) * mm});
            skLineSegment(sketch, "E392", {"start": v(57.58, 30.71) * mm, "end": v(57.47, 30.7) * mm});
            skLineSegment(sketch, "E393", {"start": v(57.47, 30.7) * mm, "end": v(57.36, 30.67) * mm});
            skLineSegment(sketch, "E394", {"start": v(57.36, 30.67) * mm, "end": v(57.25, 30.65) * mm});
            skLineSegment(sketch, "E395", {"start": v(57.25, 30.65) * mm, "end": v(57.14, 30.63) * mm});
            skLineSegment(sketch, "E396", {"start": v(57.14, 30.63) * mm, "end": v(57.04, 30.6) * mm});
            skLineSegment(sketch, "E397", {"start": v(57.04, 30.6) * mm, "end": v(56.94, 30.58) * mm});
            skLineSegment(sketch, "E398", {"start": v(56.94, 30.58) * mm, "end": v(56.84, 30.56) * mm});
            skLineSegment(sketch, "E399", {"start": v(56.84, 30.56) * mm, "end": v(56.74, 30.54) * mm});
            skLineSegment(sketch, "E400", {"start": v(56.74, 30.54) * mm, "end": v(56.65, 30.52) * mm});
            skLineSegment(sketch, "E401", {"start": v(56.65, 30.52) * mm, "end": v(56.55, 30.5) * mm});
            skLineSegment(sketch, "E402", {"start": v(56.55, 30.5) * mm, "end": v(56.46, 30.47) * mm});
            skLineSegment(sketch, "E403", {"start": v(56.46, 30.47) * mm, "end": v(56.37, 30.45) * mm});
            skLineSegment(sketch, "E404", {"start": v(56.37, 30.45) * mm, "end": v(56.29, 30.43) * mm});
            skLineSegment(sketch, "E405", {"start": v(56.29, 30.43) * mm, "end": v(56.2, 30.4) * mm});
            skLineSegment(sketch, "E406", {"start": v(56.2, 30.4) * mm, "end": v(56.12, 30.38) * mm});
            skLineSegment(sketch, "E407", {"start": v(56.12, 30.38) * mm, "end": v(56.04, 30.36) * mm});
            skLineSegment(sketch, "E408", {"start": v(56.04, 30.36) * mm, "end": v(55.81, 30.51) * mm});
            skLineSegment(sketch, "E409", {"start": v(55.81, 30.51) * mm, "end": v(55.09, 31.8) * mm});
            skLineSegment(sketch, "E410", {"start": v(55.09, 31.8) * mm, "end": v(55.08, 32.08) * mm});
            skLineSegment(sketch, "E411", {"start": v(55.08, 32.08) * mm, "end": v(55.14, 32.13) * mm});
            skLineSegment(sketch, "E412", {"start": v(55.14, 32.13) * mm, "end": v(55.2, 32.2) * mm});
            skLineSegment(sketch, "E413", {"start": v(55.2, 32.2) * mm, "end": v(55.26, 32.25) * mm});
            skLineSegment(sketch, "E414", {"start": v(55.26, 32.25) * mm, "end": v(55.33, 32.32) * mm});
            skLineSegment(sketch, "E415", {"start": v(55.33, 32.32) * mm, "end": v(55.4, 32.38) * mm});
            skLineSegment(sketch, "E416", {"start": v(55.4, 32.38) * mm, "end": v(55.46, 32.44) * mm});
            skLineSegment(sketch, "E417", {"start": v(55.46, 32.44) * mm, "end": v(55.53, 32.51) * mm});
            skLineSegment(sketch, "E418", {"start": v(55.53, 32.51) * mm, "end": v(55.6, 32.58) * mm});
            skLineSegment(sketch, "E419", {"start": v(55.6, 32.58) * mm, "end": v(55.66, 32.65) * mm});
            skLineSegment(sketch, "E420", {"start": v(55.66, 32.65) * mm, "end": v(55.8, 32.8) * mm});
            skLineSegment(sketch, "E421", {"start": v(55.8, 32.8) * mm, "end": v(55.88, 32.88) * mm});
            skLineSegment(sketch, "E422", {"start": v(55.88, 32.88) * mm, "end": v(55.95, 32.96) * mm});
            skLineSegment(sketch, "E423", {"start": v(55.95, 32.96) * mm, "end": v(56.03, 33.04) * mm});
            skLineSegment(sketch, "E424", {"start": v(56.03, 33.04) * mm, "end": v(56.1, 33.13) * mm});
            skLineSegment(sketch, "E425", {"start": v(56.1, 33.13) * mm, "end": v(56.18, 33.21) * mm});
            skLineSegment(sketch, "E426", {"start": v(56.18, 33.21) * mm, "end": v(56.26, 33.3) * mm});
            skLineSegment(sketch, "E427", {"start": v(56.26, 33.3) * mm, "end": v(56.33, 33.39) * mm});
            skLineSegment(sketch, "E428", {"start": v(56.33, 33.39) * mm, "end": v(56.41, 33.48) * mm});
            skLineSegment(sketch, "E429", {"start": v(56.41, 33.48) * mm, "end": v(56.5, 33.57) * mm});
            skLineSegment(sketch, "E430", {"start": v(56.5, 33.57) * mm, "end": v(56.57, 33.67) * mm});
            skLineSegment(sketch, "E431", {"start": v(56.57, 33.67) * mm, "end": v(56.66, 33.77) * mm});
            skLineSegment(sketch, "E432", {"start": v(56.66, 33.77) * mm, "end": v(56.82, 33.97) * mm});
            skLineSegment(sketch, "E433", {"start": v(56.82, 33.97) * mm, "end": v(56.9, 34.07) * mm});
            skLineSegment(sketch, "E434", {"start": v(56.9, 34.07) * mm, "end": v(56.99, 34.18) * mm});
            skLineSegment(sketch, "E435", {"start": v(56.99, 34.18) * mm, "end": v(57.07, 34.29) * mm});
            skLineSegment(sketch, "E436", {"start": v(57.07, 34.29) * mm, "end": v(57.16, 34.4) * mm});
            skLineSegment(sketch, "E437", {"start": v(57.16, 34.4) * mm, "end": v(57.25, 34.51) * mm});
            skLineSegment(sketch, "E438", {"start": v(57.25, 34.51) * mm, "end": v(57.33, 34.62) * mm});
            skLineSegment(sketch, "E439", {"start": v(57.33, 34.62) * mm, "end": v(57.42, 34.74) * mm});
            skLineSegment(sketch, "E440", {"start": v(57.42, 34.74) * mm, "end": v(57.5, 34.86) * mm});
            skLineSegment(sketch, "E441", {"start": v(57.5, 34.86) * mm, "end": v(57.6, 34.98) * mm});
            skLineSegment(sketch, "E442", {"start": v(57.6, 34.98) * mm, "end": v(57.69, 35.1) * mm});
            skLineSegment(sketch, "E443", {"start": v(57.69, 35.1) * mm, "end": v(57.78, 35.23) * mm});
            skLineSegment(sketch, "E444", {"start": v(57.78, 35.23) * mm, "end": v(57.87, 35.36) * mm});
            skLineSegment(sketch, "E445", {"start": v(57.87, 35.36) * mm, "end": v(57.96, 35.5) * mm});
            skLineSegment(sketch, "E446", {"start": v(57.96, 35.5) * mm, "end": v(58.05, 35.62) * mm});
            skLineSegment(sketch, "E447", {"start": v(58.05, 35.62) * mm, "end": v(58.14, 35.76) * mm});
            skLineSegment(sketch, "E448", {"start": v(58.14, 35.76) * mm, "end": v(58.19, 35.86) * mm});
            skLineSegment(sketch, "E449", {"start": v(58.19, 35.86) * mm, "end": v(57.31, 37.24) * mm});
            skLineSegment(sketch, "E450", {"start": v(57.31, 37.24) * mm, "end": v(57.2, 37.25) * mm});
            skLineSegment(sketch, "E451", {"start": v(57.2, 37.25) * mm, "end": v(57.04, 37.22) * mm});
            skLineSegment(sketch, "E452", {"start": v(57.04, 37.22) * mm, "end": v(56.88, 37.2) * mm});
            skLineSegment(sketch, "E453", {"start": v(56.88, 37.2) * mm, "end": v(56.72, 37.17) * mm});
            skLineSegment(sketch, "E454", {"start": v(56.72, 37.17) * mm, "end": v(56.57, 37.14) * mm});
            skLineSegment(sketch, "E455", {"start": v(56.57, 37.14) * mm, "end": v(56.42, 37.12) * mm});
            skLineSegment(sketch, "E456", {"start": v(56.42, 37.12) * mm, "end": v(56.27, 37.09) * mm});
            skLineSegment(sketch, "E457", {"start": v(56.27, 37.09) * mm, "end": v(56.12, 37.06) * mm});
            skLineSegment(sketch, "E458", {"start": v(56.12, 37.06) * mm, "end": v(55.97, 37.03) * mm});
            skLineSegment(sketch, "E459", {"start": v(55.97, 37.03) * mm, "end": v(55.83, 37) * mm});
            skLineSegment(sketch, "E460", {"start": v(55.83, 37) * mm, "end": v(55.69, 36.97) * mm});
            skLineSegment(sketch, "E461", {"start": v(55.69, 36.97) * mm, "end": v(55.55, 36.94) * mm});
            skLineSegment(sketch, "E462", {"start": v(55.55, 36.94) * mm, "end": v(55.41, 36.91) * mm});
            skLineSegment(sketch, "E463", {"start": v(55.41, 36.91) * mm, "end": v(55.28, 36.88) * mm});
            skLineSegment(sketch, "E464", {"start": v(55.28, 36.88) * mm, "end": v(55.14, 36.85) * mm});
            skLineSegment(sketch, "E465", {"start": v(55.14, 36.85) * mm, "end": v(55.02, 36.82) * mm});
            skLineSegment(sketch, "E466", {"start": v(55.02, 36.82) * mm, "end": v(54.89, 36.79) * mm});
            skLineSegment(sketch, "E467", {"start": v(54.89, 36.79) * mm, "end": v(54.76, 36.76) * mm});
            skLineSegment(sketch, "E468", {"start": v(54.76, 36.76) * mm, "end": v(54.64, 36.73) * mm});
            skLineSegment(sketch, "E469", {"start": v(54.64, 36.73) * mm, "end": v(54.52, 36.7) * mm});
            skLineSegment(sketch, "E470", {"start": v(54.52, 36.7) * mm, "end": v(54.4, 36.66) * mm});
            skLineSegment(sketch, "E471", {"start": v(54.4, 36.66) * mm, "end": v(54.28, 36.63) * mm});
            skLineSegment(sketch, "E472", {"start": v(54.28, 36.63) * mm, "end": v(54.17, 36.6) * mm});
            skLineSegment(sketch, "E473", {"start": v(54.17, 36.6) * mm, "end": v(54.06, 36.56) * mm});
            skLineSegment(sketch, "E474", {"start": v(54.06, 36.56) * mm, "end": v(53.95, 36.53) * mm});
            skLineSegment(sketch, "E475", {"start": v(53.95, 36.53) * mm, "end": v(53.84, 36.5) * mm});
            skLineSegment(sketch, "E476", {"start": v(53.84, 36.5) * mm, "end": v(53.73, 36.47) * mm});
            skLineSegment(sketch, "E477", {"start": v(53.73, 36.47) * mm, "end": v(53.63, 36.43) * mm});
            skLineSegment(sketch, "E478", {"start": v(53.63, 36.43) * mm, "end": v(53.53, 36.4) * mm});
            skLineSegment(sketch, "E479", {"start": v(53.53, 36.4) * mm, "end": v(53.43, 36.37) * mm});
            skLineSegment(sketch, "E480", {"start": v(53.43, 36.37) * mm, "end": v(53.33, 36.34) * mm});
            skLineSegment(sketch, "E481", {"start": v(53.33, 36.34) * mm, "end": v(53.24, 36.3) * mm});
            skLineSegment(sketch, "E482", {"start": v(53.24, 36.3) * mm, "end": v(53.15, 36.27) * mm});
            skLineSegment(sketch, "E483", {"start": v(53.15, 36.27) * mm, "end": v(53.06, 36.24) * mm});
            skLineSegment(sketch, "E484", {"start": v(53.06, 36.24) * mm, "end": v(52.97, 36.2) * mm});
            skLineSegment(sketch, "E485", {"start": v(52.97, 36.2) * mm, "end": v(52.88, 36.18) * mm});
            skLineSegment(sketch, "E486", {"start": v(52.88, 36.18) * mm, "end": v(52.8, 36.15) * mm});
            skLineSegment(sketch, "E487", {"start": v(52.8, 36.15) * mm, "end": v(52.72, 36.11) * mm});
            skLineSegment(sketch, "E488", {"start": v(52.72, 36.11) * mm, "end": v(52.64, 36.08) * mm});
            skLineSegment(sketch, "E489", {"start": v(52.64, 36.08) * mm, "end": v(52.56, 36.05) * mm});
            skLineSegment(sketch, "E490", {"start": v(52.56, 36.05) * mm, "end": v(52.32, 36.18) * mm});
            skLineSegment(sketch, "E491", {"start": v(52.32, 36.18) * mm, "end": v(51.46, 37.39) * mm});
            skLineSegment(sketch, "E492", {"start": v(51.46, 37.39) * mm, "end": v(51.42, 37.66) * mm});
            skLineSegment(sketch, "E493", {"start": v(51.42, 37.66) * mm, "end": v(51.48, 37.72) * mm});
            skLineSegment(sketch, "E494", {"start": v(51.48, 37.72) * mm, "end": v(51.53, 37.79) * mm});
            skLineSegment(sketch, "E495", {"start": v(51.53, 37.79) * mm, "end": v(51.59, 37.85) * mm});
            skLineSegment(sketch, "E496", {"start": v(51.59, 37.85) * mm, "end": v(51.64, 37.92) * mm});
            skLineSegment(sketch, "E497", {"start": v(51.64, 37.92) * mm, "end": v(51.7, 38) * mm});
            skLineSegment(sketch, "E498", {"start": v(51.7, 38) * mm, "end": v(51.76, 38.06) * mm});
            skLineSegment(sketch, "E499", {"start": v(51.76, 38.06) * mm, "end": v(51.82, 38.14) * mm});
            skLineSegment(sketch, "E500", {"start": v(51.82, 38.14) * mm, "end": v(51.88, 38.22) * mm});
            skLineSegment(sketch, "E501", {"start": v(51.88, 38.22) * mm, "end": v(51.95, 38.3) * mm});
            skLineSegment(sketch, "E502", {"start": v(51.95, 38.3) * mm, "end": v(52, 38.37) * mm});
            skLineSegment(sketch, "E503", {"start": v(52, 38.37) * mm, "end": v(52.07, 38.46) * mm});
            skLineSegment(sketch, "E504", {"start": v(52.07, 38.46) * mm, "end": v(52.14, 38.54) * mm});
            skLineSegment(sketch, "E505", {"start": v(52.14, 38.54) * mm, "end": v(52.2, 38.63) * mm});
            skLineSegment(sketch, "E506", {"start": v(52.2, 38.63) * mm, "end": v(52.27, 38.72) * mm});
            skLineSegment(sketch, "E507", {"start": v(52.27, 38.72) * mm, "end": v(52.33, 38.8) * mm});
            skLineSegment(sketch, "E508", {"start": v(52.33, 38.8) * mm, "end": v(52.4, 38.9) * mm});
            skLineSegment(sketch, "E509", {"start": v(52.4, 38.9) * mm, "end": v(52.47, 39) * mm});
            skLineSegment(sketch, "E510", {"start": v(52.47, 39) * mm, "end": v(52.54, 39.1) * mm});
            skLineSegment(sketch, "E511", {"start": v(52.54, 39.1) * mm, "end": v(52.6, 39.2) * mm});
            skLineSegment(sketch, "E512", {"start": v(52.6, 39.2) * mm, "end": v(52.67, 39.3) * mm});
            skLineSegment(sketch, "E513", {"start": v(52.67, 39.3) * mm, "end": v(52.74, 39.4) * mm});
            skLineSegment(sketch, "E514", {"start": v(52.74, 39.4) * mm, "end": v(52.82, 39.5) * mm});
            skLineSegment(sketch, "E515", {"start": v(52.82, 39.5) * mm, "end": v(52.96, 39.72) * mm});
            skLineSegment(sketch, "E516", {"start": v(52.96, 39.72) * mm, "end": v(53.03, 39.83) * mm});
            skLineSegment(sketch, "E517", {"start": v(53.03, 39.83) * mm, "end": v(53.1, 39.95) * mm});
            skLineSegment(sketch, "E518", {"start": v(53.1, 39.95) * mm, "end": v(53.18, 40.07) * mm});
            skLineSegment(sketch, "E519", {"start": v(53.18, 40.07) * mm, "end": v(53.25, 40.18) * mm});
            skLineSegment(sketch, "E520", {"start": v(53.25, 40.18) * mm, "end": v(53.33, 40.3) * mm});
            skLineSegment(sketch, "E521", {"start": v(53.33, 40.3) * mm, "end": v(53.4, 40.43) * mm});
            skLineSegment(sketch, "E522", {"start": v(53.4, 40.43) * mm, "end": v(53.48, 40.55) * mm});
            skLineSegment(sketch, "E523", {"start": v(53.48, 40.55) * mm, "end": v(53.55, 40.68) * mm});
            skLineSegment(sketch, "E524", {"start": v(53.55, 40.68) * mm, "end": v(53.63, 40.81) * mm});
            skLineSegment(sketch, "E525", {"start": v(53.63, 40.81) * mm, "end": v(53.7, 40.94) * mm});
            skLineSegment(sketch, "E526", {"start": v(53.7, 40.94) * mm, "end": v(53.78, 41.08) * mm});
            skLineSegment(sketch, "E527", {"start": v(53.78, 41.08) * mm, "end": v(53.85, 41.21) * mm});
            skLineSegment(sketch, "E528", {"start": v(53.85, 41.21) * mm, "end": v(53.93, 41.35) * mm});
            skLineSegment(sketch, "E529", {"start": v(53.93, 41.35) * mm, "end": v(54, 41.5) * mm});
            skLineSegment(sketch, "E530", {"start": v(54, 41.5) * mm, "end": v(54.09, 41.64) * mm});
            skLineSegment(sketch, "E531", {"start": v(54.09, 41.64) * mm, "end": v(54.12, 41.75) * mm});
            skLineSegment(sketch, "E532", {"start": v(54.12, 41.75) * mm, "end": v(53.1, 43.03) * mm});
            skLineSegment(sketch, "E533", {"start": v(53.1, 43.03) * mm, "end": v(53, 43.02) * mm});
            skLineSegment(sketch, "E534", {"start": v(53, 43.02) * mm, "end": v(52.83, 42.98) * mm});
            skLineSegment(sketch, "E535", {"start": v(52.83, 42.98) * mm, "end": v(52.68, 42.94) * mm});
            skLineSegment(sketch, "E536", {"start": v(52.68, 42.94) * mm, "end": v(52.53, 42.9) * mm});
            skLineSegment(sketch, "E537", {"start": v(52.53, 42.9) * mm, "end": v(52.38, 42.85) * mm});
            skLineSegment(sketch, "E538", {"start": v(52.38, 42.85) * mm, "end": v(52.23, 42.81) * mm});
            skLineSegment(sketch, "E539", {"start": v(52.23, 42.81) * mm, "end": v(52.08, 42.77) * mm});
            skLineSegment(sketch, "E540", {"start": v(52.08, 42.77) * mm, "end": v(51.94, 42.72) * mm});
            skLineSegment(sketch, "E541", {"start": v(51.94, 42.72) * mm, "end": v(51.8, 42.68) * mm});
            skLineSegment(sketch, "E542", {"start": v(51.8, 42.68) * mm, "end": v(51.65, 42.64) * mm});
            skLineSegment(sketch, "E543", {"start": v(51.65, 42.64) * mm, "end": v(51.52, 42.6) * mm});
            skLineSegment(sketch, "E544", {"start": v(51.52, 42.6) * mm, "end": v(51.38, 42.55) * mm});
            skLineSegment(sketch, "E545", {"start": v(51.38, 42.55) * mm, "end": v(51.25, 42.5) * mm});
            skLineSegment(sketch, "E546", {"start": v(51.25, 42.5) * mm, "end": v(51.12, 42.46) * mm});
            skLineSegment(sketch, "E547", {"start": v(51.12, 42.46) * mm, "end": v(51, 42.41) * mm});
            skLineSegment(sketch, "E548", {"start": v(51, 42.41) * mm, "end": v(50.87, 42.37) * mm});
            skLineSegment(sketch, "E549", {"start": v(50.87, 42.37) * mm, "end": v(50.74, 42.33) * mm});
            skLineSegment(sketch, "E550", {"start": v(50.74, 42.33) * mm, "end": v(50.62, 42.28) * mm});
            skLineSegment(sketch, "E551", {"start": v(50.62, 42.28) * mm, "end": v(50.5, 42.24) * mm});
            skLineSegment(sketch, "E552", {"start": v(50.5, 42.24) * mm, "end": v(50.38, 42.2) * mm});
            skLineSegment(sketch, "E553", {"start": v(50.38, 42.2) * mm, "end": v(50.27, 42.15) * mm});
            skLineSegment(sketch, "E554", {"start": v(50.27, 42.15) * mm, "end": v(50.16, 42.1) * mm});
            skLineSegment(sketch, "E555", {"start": v(50.16, 42.1) * mm, "end": v(50.05, 42.06) * mm});
            skLineSegment(sketch, "E556", {"start": v(50.05, 42.06) * mm, "end": v(49.94, 42.01) * mm});
            skLineSegment(sketch, "E557", {"start": v(49.94, 42.01) * mm, "end": v(49.83, 41.97) * mm});
            skLineSegment(sketch, "E558", {"start": v(49.83, 41.97) * mm, "end": v(49.73, 41.93) * mm});
            skLineSegment(sketch, "E559", {"start": v(49.73, 41.93) * mm, "end": v(49.63, 41.88) * mm});
            skLineSegment(sketch, "E560", {"start": v(49.63, 41.88) * mm, "end": v(49.53, 41.84) * mm});
            skLineSegment(sketch, "E561", {"start": v(49.53, 41.84) * mm, "end": v(49.43, 41.8) * mm});
            skLineSegment(sketch, "E562", {"start": v(49.43, 41.8) * mm, "end": v(49.34, 41.75) * mm});
            skLineSegment(sketch, "E563", {"start": v(49.34, 41.75) * mm, "end": v(49.24, 41.71) * mm});
            skLineSegment(sketch, "E564", {"start": v(49.24, 41.71) * mm, "end": v(49.15, 41.67) * mm});
            skLineSegment(sketch, "E565", {"start": v(49.15, 41.67) * mm, "end": v(49.06, 41.63) * mm});
            skLineSegment(sketch, "E566", {"start": v(49.06, 41.63) * mm, "end": v(48.98, 41.59) * mm});
            skLineSegment(sketch, "E567", {"start": v(48.98, 41.59) * mm, "end": v(48.9, 41.55) * mm});
            skLineSegment(sketch, "E568", {"start": v(48.9, 41.55) * mm, "end": v(48.8, 41.5) * mm});
            skLineSegment(sketch, "E569", {"start": v(48.8, 41.5) * mm, "end": v(48.73, 41.47) * mm});
            skLineSegment(sketch, "E570", {"start": v(48.73, 41.47) * mm, "end": v(48.65, 41.43) * mm});
            skLineSegment(sketch, "E571", {"start": v(48.65, 41.43) * mm, "end": v(48.58, 41.39) * mm});
            skLineSegment(sketch, "E572", {"start": v(48.58, 41.39) * mm, "end": v(48.5, 41.35) * mm});
            skLineSegment(sketch, "E573", {"start": v(48.5, 41.35) * mm, "end": v(48.25, 41.45) * mm});
            skLineSegment(sketch, "E574", {"start": v(48.25, 41.45) * mm, "end": v(47.27, 42.56) * mm});
            skLineSegment(sketch, "E575", {"start": v(47.27, 42.56) * mm, "end": v(47.2, 42.83) * mm});
            skLineSegment(sketch, "E576", {"start": v(47.2, 42.83) * mm, "end": v(47.25, 42.9) * mm});
            skLineSegment(sketch, "E577", {"start": v(47.25, 42.9) * mm, "end": v(47.3, 42.96) * mm});
            skLineSegment(sketch, "E578", {"start": v(47.3, 42.96) * mm, "end": v(47.35, 43.04) * mm});
            skLineSegment(sketch, "E579", {"start": v(47.35, 43.04) * mm, "end": v(47.4, 43.11) * mm});
            skLineSegment(sketch, "E580", {"start": v(47.4, 43.11) * mm, "end": v(47.45, 43.19) * mm});
            skLineSegment(sketch, "E581", {"start": v(47.45, 43.19) * mm, "end": v(47.5, 43.27) * mm});
            skLineSegment(sketch, "E582", {"start": v(47.5, 43.27) * mm, "end": v(47.55, 43.35) * mm});
            skLineSegment(sketch, "E583", {"start": v(47.55, 43.35) * mm, "end": v(47.6, 43.43) * mm});
            skLineSegment(sketch, "E584", {"start": v(47.6, 43.43) * mm, "end": v(47.66, 43.51) * mm});
            skLineSegment(sketch, "E585", {"start": v(47.66, 43.51) * mm, "end": v(47.71, 43.6) * mm});
            skLineSegment(sketch, "E586", {"start": v(47.71, 43.6) * mm, "end": v(47.77, 43.69) * mm});
            skLineSegment(sketch, "E587", {"start": v(47.77, 43.69) * mm, "end": v(47.82, 43.78) * mm});
            skLineSegment(sketch, "E588", {"start": v(47.82, 43.78) * mm, "end": v(47.88, 43.87) * mm});
            skLineSegment(sketch, "E589", {"start": v(47.88, 43.87) * mm, "end": v(47.93, 43.97) * mm});
            skLineSegment(sketch, "E590", {"start": v(47.93, 43.97) * mm, "end": v(47.99, 44.07) * mm});
            skLineSegment(sketch, "E591", {"start": v(47.99, 44.07) * mm, "end": v(48.05, 44.16) * mm});
            skLineSegment(sketch, "E592", {"start": v(48.05, 44.16) * mm, "end": v(48.1, 44.27) * mm});
            skLineSegment(sketch, "E593", {"start": v(48.1, 44.27) * mm, "end": v(48.16, 44.37) * mm});
            skLineSegment(sketch, "E594", {"start": v(48.16, 44.37) * mm, "end": v(48.22, 44.48) * mm});
            skLineSegment(sketch, "E595", {"start": v(48.22, 44.48) * mm, "end": v(48.28, 44.59) * mm});
            skLineSegment(sketch, "E596", {"start": v(48.28, 44.59) * mm, "end": v(48.34, 44.7) * mm});
            skLineSegment(sketch, "E597", {"start": v(48.34, 44.7) * mm, "end": v(48.4, 44.8) * mm});
            skLineSegment(sketch, "E598", {"start": v(48.4, 44.8) * mm, "end": v(48.46, 44.92) * mm});
            skLineSegment(sketch, "E599", {"start": v(48.46, 44.92) * mm, "end": v(48.52, 45.04) * mm});
            skLineSegment(sketch, "E600", {"start": v(48.52, 45.04) * mm, "end": v(48.58, 45.16) * mm});
            skLineSegment(sketch, "E601", {"start": v(48.58, 45.16) * mm, "end": v(48.64, 45.28) * mm});
            skLineSegment(sketch, "E602", {"start": v(48.64, 45.28) * mm, "end": v(48.7, 45.4) * mm});
            skLineSegment(sketch, "E603", {"start": v(48.7, 45.4) * mm, "end": v(48.76, 45.53) * mm});
            skLineSegment(sketch, "E604", {"start": v(48.76, 45.53) * mm, "end": v(48.82, 45.66) * mm});
            skLineSegment(sketch, "E605", {"start": v(48.82, 45.66) * mm, "end": v(48.88, 45.79) * mm});
            skLineSegment(sketch, "E606", {"start": v(48.88, 45.79) * mm, "end": v(48.94, 45.92) * mm});
            skLineSegment(sketch, "E607", {"start": v(48.94, 45.92) * mm, "end": v(49, 46.06) * mm});
            skLineSegment(sketch, "E608", {"start": v(49, 46.06) * mm, "end": v(49.07, 46.2) * mm});
            skLineSegment(sketch, "E609", {"start": v(49.07, 46.2) * mm, "end": v(49.13, 46.33) * mm});
            skLineSegment(sketch, "E610", {"start": v(49.13, 46.33) * mm, "end": v(49.2, 46.47) * mm});
            skLineSegment(sketch, "E611", {"start": v(49.2, 46.47) * mm, "end": v(49.25, 46.62) * mm});
            skLineSegment(sketch, "E612", {"start": v(49.25, 46.62) * mm, "end": v(49.31, 46.77) * mm});
            skLineSegment(sketch, "E613", {"start": v(49.31, 46.77) * mm, "end": v(49.38, 46.91) * mm});
            skLineSegment(sketch, "E614", {"start": v(49.38, 46.91) * mm, "end": v(49.44, 47.06) * mm});
            skLineSegment(sketch, "E615", {"start": v(49.44, 47.06) * mm, "end": v(49.46, 47.18) * mm});
            skLineSegment(sketch, "E616", {"start": v(49.46, 47.18) * mm, "end": v(48.32, 48.34) * mm});
            skLineSegment(sketch, "E617", {"start": v(48.32, 48.34) * mm, "end": v(48.2, 48.33) * mm});
            skLineSegment(sketch, "E618", {"start": v(48.2, 48.33) * mm, "end": v(48.05, 48.27) * mm});
            skLineSegment(sketch, "E619", {"start": v(48.05, 48.27) * mm, "end": v(47.9, 48.2) * mm});
            skLineSegment(sketch, "E620", {"start": v(47.9, 48.2) * mm, "end": v(47.75, 48.15) * mm});
            skLineSegment(sketch, "E621", {"start": v(47.75, 48.15) * mm, "end": v(47.6, 48.1) * mm});
            skLineSegment(sketch, "E622", {"start": v(47.6, 48.1) * mm, "end": v(47.47, 48.04) * mm});
            skLineSegment(sketch, "E623", {"start": v(47.47, 48.04) * mm, "end": v(47.32, 47.98) * mm});
            skLineSegment(sketch, "E624", {"start": v(47.32, 47.98) * mm, "end": v(47.19, 47.92) * mm});
            skLineSegment(sketch, "E625", {"start": v(47.19, 47.92) * mm, "end": v(47.05, 47.86) * mm});
            skLineSegment(sketch, "E626", {"start": v(47.05, 47.86) * mm, "end": v(46.92, 47.8) * mm});
            skLineSegment(sketch, "E627", {"start": v(46.92, 47.8) * mm, "end": v(46.78, 47.74) * mm});
            skLineSegment(sketch, "E628", {"start": v(46.78, 47.74) * mm, "end": v(46.65, 47.69) * mm});
            skLineSegment(sketch, "E629", {"start": v(46.65, 47.69) * mm, "end": v(46.53, 47.63) * mm});
            skLineSegment(sketch, "E630", {"start": v(46.53, 47.63) * mm, "end": v(46.4, 47.57) * mm});
            skLineSegment(sketch, "E631", {"start": v(46.4, 47.57) * mm, "end": v(46.28, 47.51) * mm});
            skLineSegment(sketch, "E632", {"start": v(46.28, 47.51) * mm, "end": v(46.16, 47.45) * mm});
            skLineSegment(sketch, "E633", {"start": v(46.16, 47.45) * mm, "end": v(46.04, 47.4) * mm});
            skLineSegment(sketch, "E634", {"start": v(46.04, 47.4) * mm, "end": v(45.92, 47.34) * mm});
            skLineSegment(sketch, "E635", {"start": v(45.92, 47.34) * mm, "end": v(45.8, 47.28) * mm});
            skLineSegment(sketch, "E636", {"start": v(45.8, 47.28) * mm, "end": v(45.7, 47.23) * mm});
            skLineSegment(sketch, "E637", {"start": v(45.7, 47.23) * mm, "end": v(45.59, 47.17) * mm});
            skLineSegment(sketch, "E638", {"start": v(45.59, 47.17) * mm, "end": v(45.48, 47.12) * mm});
            skLineSegment(sketch, "E639", {"start": v(45.48, 47.12) * mm, "end": v(45.38, 47.06) * mm});
            skLineSegment(sketch, "E640", {"start": v(45.38, 47.06) * mm, "end": v(45.27, 47) * mm});
            skLineSegment(sketch, "E641", {"start": v(45.27, 47) * mm, "end": v(45.17, 46.95) * mm});
            skLineSegment(sketch, "E642", {"start": v(45.17, 46.95) * mm, "end": v(45.07, 46.9) * mm});
            skLineSegment(sketch, "E643", {"start": v(45.07, 46.9) * mm, "end": v(44.98, 46.84) * mm});
            skLineSegment(sketch, "E644", {"start": v(44.98, 46.84) * mm, "end": v(44.88, 46.79) * mm});
            skLineSegment(sketch, "E645", {"start": v(44.88, 46.79) * mm, "end": v(44.8, 46.73) * mm});
            skLineSegment(sketch, "E646", {"start": v(44.8, 46.73) * mm, "end": v(44.7, 46.68) * mm});
            skLineSegment(sketch, "E647", {"start": v(44.7, 46.68) * mm, "end": v(44.61, 46.63) * mm});
            skLineSegment(sketch, "E648", {"start": v(44.61, 46.63) * mm, "end": v(44.53, 46.58) * mm});
            skLineSegment(sketch, "E649", {"start": v(44.53, 46.58) * mm, "end": v(44.44, 46.53) * mm});
            skLineSegment(sketch, "E650", {"start": v(44.44, 46.53) * mm, "end": v(44.36, 46.48) * mm});
            skLineSegment(sketch, "E651", {"start": v(44.36, 46.48) * mm, "end": v(44.28, 46.43) * mm});
            skLineSegment(sketch, "E652", {"start": v(44.28, 46.43) * mm, "end": v(44.2, 46.38) * mm});
            skLineSegment(sketch, "E653", {"start": v(44.2, 46.38) * mm, "end": v(44.13, 46.33) * mm});
            skLineSegment(sketch, "E654", {"start": v(44.13, 46.33) * mm, "end": v(44.06, 46.29) * mm});
            skLineSegment(sketch, "E655", {"start": v(44.06, 46.29) * mm, "end": v(43.98, 46.24) * mm});
            skLineSegment(sketch, "E656", {"start": v(43.98, 46.24) * mm, "end": v(43.92, 46.2) * mm});
            skLineSegment(sketch, "E657", {"start": v(43.92, 46.2) * mm, "end": v(43.65, 46.27) * mm});
            skLineSegment(sketch, "E658", {"start": v(43.65, 46.27) * mm, "end": v(42.56, 47.27) * mm});
            skLineSegment(sketch, "E659", {"start": v(42.56, 47.27) * mm, "end": v(42.47, 47.53) * mm});
            skLineSegment(sketch, "E660", {"start": v(42.47, 47.53) * mm, "end": v(42.5, 47.6) * mm});
            skLineSegment(sketch, "E661", {"start": v(42.5, 47.6) * mm, "end": v(42.6, 47.75) * mm});
            skLineSegment(sketch, "E662", {"start": v(42.6, 47.75) * mm, "end": v(42.63, 47.83) * mm});
            skLineSegment(sketch, "E663", {"start": v(42.63, 47.83) * mm, "end": v(42.68, 47.91) * mm});
            skLineSegment(sketch, "E664", {"start": v(42.68, 47.91) * mm, "end": v(42.72, 48) * mm});
            skLineSegment(sketch, "E665", {"start": v(42.72, 48) * mm, "end": v(42.8, 48.17) * mm});
            skLineSegment(sketch, "E666", {"start": v(42.8, 48.17) * mm, "end": v(42.85, 48.26) * mm});
            skLineSegment(sketch, "E667", {"start": v(42.85, 48.26) * mm, "end": v(42.9, 48.35) * mm});
            skLineSegment(sketch, "E668", {"start": v(42.9, 48.35) * mm, "end": v(42.94, 48.44) * mm});
            skLineSegment(sketch, "E669", {"start": v(42.94, 48.44) * mm, "end": v(42.98, 48.54) * mm});
            skLineSegment(sketch, "E670", {"start": v(42.98, 48.54) * mm, "end": v(43.03, 48.64) * mm});
            skLineSegment(sketch, "E671", {"start": v(43.03, 48.64) * mm, "end": v(43.07, 48.74) * mm});
            skLineSegment(sketch, "E672", {"start": v(43.07, 48.74) * mm, "end": v(43.12, 48.84) * mm});
            skLineSegment(sketch, "E673", {"start": v(43.12, 48.84) * mm, "end": v(43.17, 48.95) * mm});
            skLineSegment(sketch, "E674", {"start": v(43.17, 48.95) * mm, "end": v(43.21, 49.05) * mm});
            skLineSegment(sketch, "E675", {"start": v(43.21, 49.05) * mm, "end": v(43.26, 49.16) * mm});
            skLineSegment(sketch, "E676", {"start": v(43.26, 49.16) * mm, "end": v(43.3, 49.27) * mm});
            skLineSegment(sketch, "E677", {"start": v(43.3, 49.27) * mm, "end": v(43.35, 49.39) * mm});
            skLineSegment(sketch, "E678", {"start": v(43.35, 49.39) * mm, "end": v(43.4, 49.5) * mm});
            skLineSegment(sketch, "E679", {"start": v(43.4, 49.5) * mm, "end": v(43.45, 49.62) * mm});
            skLineSegment(sketch, "E680", {"start": v(43.45, 49.62) * mm, "end": v(43.5, 49.74) * mm});
            skLineSegment(sketch, "E681", {"start": v(43.5, 49.74) * mm, "end": v(43.54, 49.86) * mm});
            skLineSegment(sketch, "E682", {"start": v(43.54, 49.86) * mm, "end": v(43.6, 49.99) * mm});
            skLineSegment(sketch, "E683", {"start": v(43.6, 49.99) * mm, "end": v(43.64, 50.12) * mm});
            skLineSegment(sketch, "E684", {"start": v(43.64, 50.12) * mm, "end": v(43.69, 50.25) * mm});
            skLineSegment(sketch, "E685", {"start": v(43.69, 50.25) * mm, "end": v(43.73, 50.38) * mm});
            skLineSegment(sketch, "E686", {"start": v(43.73, 50.38) * mm, "end": v(43.78, 50.51) * mm});
            skLineSegment(sketch, "E687", {"start": v(43.78, 50.51) * mm, "end": v(43.83, 50.65) * mm});
            skLineSegment(sketch, "E688", {"start": v(43.83, 50.65) * mm, "end": v(43.88, 50.78) * mm});
            skLineSegment(sketch, "E689", {"start": v(43.88, 50.78) * mm, "end": v(43.92, 50.93) * mm});
            skLineSegment(sketch, "E690", {"start": v(43.92, 50.93) * mm, "end": v(43.97, 51.07) * mm});
            skLineSegment(sketch, "E691", {"start": v(43.97, 51.07) * mm, "end": v(44.02, 51.21) * mm});
            skLineSegment(sketch, "E692", {"start": v(44.02, 51.21) * mm, "end": v(44.06, 51.36) * mm});
            skLineSegment(sketch, "E693", {"start": v(44.06, 51.36) * mm, "end": v(44.1, 51.51) * mm});
            skLineSegment(sketch, "E694", {"start": v(44.1, 51.51) * mm, "end": v(44.16, 51.66) * mm});
            skLineSegment(sketch, "E695", {"start": v(44.16, 51.66) * mm, "end": v(44.2, 51.82) * mm});
            skLineSegment(sketch, "E696", {"start": v(44.2, 51.82) * mm, "end": v(44.25, 51.97) * mm});
            skLineSegment(sketch, "E697", {"start": v(44.25, 51.97) * mm, "end": v(44.25, 52.09) * mm});
            skLineSegment(sketch, "E698", {"start": v(44.25, 52.09) * mm, "end": v(43, 53.13) * mm});
            skLineSegment(sketch, "E699", {"start": v(43, 53.13) * mm, "end": v(42.89, 53.1) * mm});
            skLineSegment(sketch, "E700", {"start": v(42.89, 53.1) * mm, "end": v(42.74, 53.03) * mm});
            skLineSegment(sketch, "E701", {"start": v(42.74, 53.03) * mm, "end": v(42.6, 52.95) * mm});
            skLineSegment(sketch, "E702", {"start": v(42.6, 52.95) * mm, "end": v(42.46, 52.88) * mm});
            skLineSegment(sketch, "E703", {"start": v(42.46, 52.88) * mm, "end": v(42.32, 52.8) * mm});
            skLineSegment(sketch, "E704", {"start": v(42.32, 52.8) * mm, "end": v(42.18, 52.73) * mm});
            skLineSegment(sketch, "E705", {"start": v(42.18, 52.73) * mm, "end": v(42.05, 52.66) * mm});
            skLineSegment(sketch, "E706", {"start": v(42.05, 52.66) * mm, "end": v(41.92, 52.59) * mm});
            skLineSegment(sketch, "E707", {"start": v(41.92, 52.59) * mm, "end": v(41.79, 52.52) * mm});
            skLineSegment(sketch, "E708", {"start": v(41.79, 52.52) * mm, "end": v(41.66, 52.44) * mm});
            skLineSegment(sketch, "E709", {"start": v(41.66, 52.44) * mm, "end": v(41.54, 52.37) * mm});
            skLineSegment(sketch, "E710", {"start": v(41.54, 52.37) * mm, "end": v(41.41, 52.3) * mm});
            skLineSegment(sketch, "E711", {"start": v(41.41, 52.3) * mm, "end": v(41.3, 52.23) * mm});
            skLineSegment(sketch, "E712", {"start": v(41.3, 52.23) * mm, "end": v(41.17, 52.16) * mm});
            skLineSegment(sketch, "E713", {"start": v(41.17, 52.16) * mm, "end": v(41.06, 52.09) * mm});
            skLineSegment(sketch, "E714", {"start": v(41.06, 52.09) * mm, "end": v(40.94, 52.02) * mm});
            skLineSegment(sketch, "E715", {"start": v(40.94, 52.02) * mm, "end": v(40.83, 51.95) * mm});
            skLineSegment(sketch, "E716", {"start": v(40.83, 51.95) * mm, "end": v(40.72, 51.88) * mm});
            skLineSegment(sketch, "E717", {"start": v(40.72, 51.88) * mm, "end": v(40.62, 51.81) * mm});
            skLineSegment(sketch, "E718", {"start": v(40.62, 51.81) * mm, "end": v(40.51, 51.74) * mm});
            skLineSegment(sketch, "E719", {"start": v(40.51, 51.74) * mm, "end": v(40.4, 51.68) * mm});
            skLineSegment(sketch, "E720", {"start": v(40.4, 51.68) * mm, "end": v(40.3, 51.61) * mm});
            skLineSegment(sketch, "E721", {"start": v(40.3, 51.61) * mm, "end": v(40.2, 51.54) * mm});
            skLineSegment(sketch, "E722", {"start": v(40.2, 51.54) * mm, "end": v(40.11, 51.48) * mm});
            skLineSegment(sketch, "E723", {"start": v(40.11, 51.48) * mm, "end": v(40.02, 51.41) * mm});
            skLineSegment(sketch, "E724", {"start": v(40.02, 51.41) * mm, "end": v(39.92, 51.35) * mm});
            skLineSegment(sketch, "E725", {"start": v(39.92, 51.35) * mm, "end": v(39.83, 51.29) * mm});
            skLineSegment(sketch, "E726", {"start": v(39.83, 51.29) * mm, "end": v(39.75, 51.22) * mm});
            skLineSegment(sketch, "E727", {"start": v(39.75, 51.22) * mm, "end": v(39.66, 51.16) * mm});
            skLineSegment(sketch, "E728", {"start": v(39.66, 51.16) * mm, "end": v(39.58, 51.1) * mm});
            skLineSegment(sketch, "E729", {"start": v(39.58, 51.1) * mm, "end": v(39.5, 51.04) * mm});
            skLineSegment(sketch, "E730", {"start": v(39.5, 51.04) * mm, "end": v(39.41, 50.98) * mm});
            skLineSegment(sketch, "E731", {"start": v(39.41, 50.98) * mm, "end": v(39.34, 50.92) * mm});
            skLineSegment(sketch, "E732", {"start": v(39.34, 50.92) * mm, "end": v(39.26, 50.86) * mm});
            skLineSegment(sketch, "E733", {"start": v(39.26, 50.86) * mm, "end": v(39.19, 50.8) * mm});
            skLineSegment(sketch, "E734", {"start": v(39.19, 50.8) * mm, "end": v(39.11, 50.75) * mm});
            skLineSegment(sketch, "E735", {"start": v(39.11, 50.75) * mm, "end": v(39.04, 50.7) * mm});
            skLineSegment(sketch, "E736", {"start": v(39.04, 50.7) * mm, "end": v(38.98, 50.64) * mm});
            skLineSegment(sketch, "E737", {"start": v(38.98, 50.64) * mm, "end": v(38.91, 50.58) * mm});
            skLineSegment(sketch, "E738", {"start": v(38.91, 50.58) * mm, "end": v(38.85, 50.53) * mm});
            skLineSegment(sketch, "E739", {"start": v(38.85, 50.53) * mm, "end": v(38.58, 50.58) * mm});
            skLineSegment(sketch, "E740", {"start": v(38.58, 50.58) * mm, "end": v(37.39, 51.46) * mm});
            skLineSegment(sketch, "E741", {"start": v(37.39, 51.46) * mm, "end": v(37.27, 51.7) * mm});
            skLineSegment(sketch, "E742", {"start": v(37.27, 51.7) * mm, "end": v(37.3, 51.78) * mm});
            skLineSegment(sketch, "E743", {"start": v(37.3, 51.78) * mm, "end": v(37.33, 51.86) * mm});
            skLineSegment(sketch, "E744", {"start": v(37.33, 51.86) * mm, "end": v(37.37, 51.94) * mm});
            skLineSegment(sketch, "E745", {"start": v(37.37, 51.94) * mm, "end": v(37.4, 52.02) * mm});
            skLineSegment(sketch, "E746", {"start": v(37.4, 52.02) * mm, "end": v(37.43, 52.1) * mm});
            skLineSegment(sketch, "E747", {"start": v(37.43, 52.1) * mm, "end": v(37.47, 52.2) * mm});
            skLineSegment(sketch, "E748", {"start": v(37.47, 52.2) * mm, "end": v(37.5, 52.29) * mm});
            skLineSegment(sketch, "E749", {"start": v(37.5, 52.29) * mm, "end": v(37.53, 52.38) * mm});
            skLineSegment(sketch, "E750", {"start": v(37.53, 52.38) * mm, "end": v(37.57, 52.47) * mm});
            skLineSegment(sketch, "E751", {"start": v(37.57, 52.47) * mm, "end": v(37.6, 52.57) * mm});
            skLineSegment(sketch, "E752", {"start": v(37.6, 52.57) * mm, "end": v(37.64, 52.67) * mm});
            skLineSegment(sketch, "E753", {"start": v(37.64, 52.67) * mm, "end": v(37.67, 52.77) * mm});
            skLineSegment(sketch, "E754", {"start": v(37.67, 52.77) * mm, "end": v(37.7, 52.87) * mm});
            skLineSegment(sketch, "E755", {"start": v(37.7, 52.87) * mm, "end": v(37.74, 52.97) * mm});
            skLineSegment(sketch, "E756", {"start": v(37.74, 52.97) * mm, "end": v(37.78, 53.08) * mm});
            skLineSegment(sketch, "E757", {"start": v(37.78, 53.08) * mm, "end": v(37.81, 53.19) * mm});
            skLineSegment(sketch, "E758", {"start": v(37.81, 53.19) * mm, "end": v(37.85, 53.3) * mm});
            skLineSegment(sketch, "E759", {"start": v(37.85, 53.3) * mm, "end": v(37.88, 53.41) * mm});
            skLineSegment(sketch, "E760", {"start": v(37.88, 53.41) * mm, "end": v(37.92, 53.53) * mm});
            skLineSegment(sketch, "E761", {"start": v(37.92, 53.53) * mm, "end": v(37.95, 53.65) * mm});
            skLineSegment(sketch, "E762", {"start": v(37.95, 53.65) * mm, "end": v(37.99, 53.77) * mm});
            skLineSegment(sketch, "E763", {"start": v(37.99, 53.77) * mm, "end": v(38.02, 53.9) * mm});
            skLineSegment(sketch, "E764", {"start": v(38.02, 53.9) * mm, "end": v(38.06, 54.01) * mm});
            skLineSegment(sketch, "E765", {"start": v(38.06, 54.01) * mm, "end": v(38.13, 54.27) * mm});
            skLineSegment(sketch, "E766", {"start": v(38.13, 54.27) * mm, "end": v(38.16, 54.4) * mm});
            skLineSegment(sketch, "E767", {"start": v(38.16, 54.4) * mm, "end": v(38.2, 54.54) * mm});
            skLineSegment(sketch, "E768", {"start": v(38.2, 54.54) * mm, "end": v(38.23, 54.67) * mm});
            skLineSegment(sketch, "E769", {"start": v(38.23, 54.67) * mm, "end": v(38.26, 54.8) * mm});
            skLineSegment(sketch, "E770", {"start": v(38.26, 54.8) * mm, "end": v(38.3, 54.95) * mm});
            skLineSegment(sketch, "E771", {"start": v(38.3, 54.95) * mm, "end": v(38.33, 55.1) * mm});
            skLineSegment(sketch, "E772", {"start": v(38.33, 55.1) * mm, "end": v(38.36, 55.24) * mm});
            skLineSegment(sketch, "E773", {"start": v(38.36, 55.24) * mm, "end": v(38.4, 55.38) * mm});
            skLineSegment(sketch, "E774", {"start": v(38.4, 55.38) * mm, "end": v(38.42, 55.53) * mm});
            skLineSegment(sketch, "E775", {"start": v(38.42, 55.53) * mm, "end": v(38.45, 55.69) * mm});
            skLineSegment(sketch, "E776", {"start": v(38.45, 55.69) * mm, "end": v(38.48, 55.84) * mm});
            skLineSegment(sketch, "E777", {"start": v(38.48, 55.84) * mm, "end": v(38.51, 56) * mm});
            skLineSegment(sketch, "E778", {"start": v(38.51, 56) * mm, "end": v(38.54, 56.15) * mm});
            skLineSegment(sketch, "E779", {"start": v(38.54, 56.15) * mm, "end": v(38.57, 56.31) * mm});
            skLineSegment(sketch, "E780", {"start": v(38.57, 56.31) * mm, "end": v(38.57, 56.43) * mm});
            skLineSegment(sketch, "E781", {"start": v(38.57, 56.43) * mm, "end": v(37.21, 57.33) * mm});
            skLineSegment(sketch, "E782", {"start": v(37.21, 57.33) * mm, "end": v(37.1, 57.3) * mm});
            skLineSegment(sketch, "E783", {"start": v(37.1, 57.3) * mm, "end": v(36.97, 57.2) * mm});
            skLineSegment(sketch, "E784", {"start": v(36.97, 57.2) * mm, "end": v(36.83, 57.12) * mm});
            skLineSegment(sketch, "E785", {"start": v(36.83, 57.12) * mm, "end": v(36.7, 57.03) * mm});
            skLineSegment(sketch, "E786", {"start": v(36.7, 57.03) * mm, "end": v(36.57, 56.94) * mm});
            skLineSegment(sketch, "E787", {"start": v(36.57, 56.94) * mm, "end": v(36.44, 56.85) * mm});
            skLineSegment(sketch, "E788", {"start": v(36.44, 56.85) * mm, "end": v(36.32, 56.77) * mm});
            skLineSegment(sketch, "E789", {"start": v(36.32, 56.77) * mm, "end": v(36.2, 56.68) * mm});
            skLineSegment(sketch, "E790", {"start": v(36.2, 56.68) * mm, "end": v(36.07, 56.6) * mm});
            skLineSegment(sketch, "E791", {"start": v(36.07, 56.6) * mm, "end": v(35.95, 56.51) * mm});
            skLineSegment(sketch, "E792", {"start": v(35.95, 56.51) * mm, "end": v(35.83, 56.43) * mm});
            skLineSegment(sketch, "E793", {"start": v(35.83, 56.43) * mm, "end": v(35.72, 56.34) * mm});
            skLineSegment(sketch, "E794", {"start": v(35.72, 56.34) * mm, "end": v(35.6, 56.26) * mm});
            skLineSegment(sketch, "E795", {"start": v(35.6, 56.26) * mm, "end": v(35.5, 56.18) * mm});
            skLineSegment(sketch, "E796", {"start": v(35.5, 56.18) * mm, "end": v(35.39, 56.1) * mm});
            skLineSegment(sketch, "E797", {"start": v(35.39, 56.1) * mm, "end": v(35.28, 56.01) * mm});
            skLineSegment(sketch, "E798", {"start": v(35.28, 56.01) * mm, "end": v(35.18, 55.93) * mm});
            skLineSegment(sketch, "E799", {"start": v(35.18, 55.93) * mm, "end": v(35.08, 55.85) * mm});
            skLineSegment(sketch, "E800", {"start": v(35.08, 55.85) * mm, "end": v(34.98, 55.77) * mm});
            skLineSegment(sketch, "E801", {"start": v(34.98, 55.77) * mm, "end": v(34.78, 55.62) * mm});
            skLineSegment(sketch, "E802", {"start": v(34.78, 55.62) * mm, "end": v(34.7, 55.54) * mm});
            skLineSegment(sketch, "E803", {"start": v(34.7, 55.54) * mm, "end": v(34.6, 55.46) * mm});
            skLineSegment(sketch, "E804", {"start": v(34.6, 55.46) * mm, "end": v(34.51, 55.4) * mm});
            skLineSegment(sketch, "E805", {"start": v(34.51, 55.4) * mm, "end": v(34.42, 55.31) * mm});
            skLineSegment(sketch, "E806", {"start": v(34.42, 55.31) * mm, "end": v(34.26, 55.17) * mm});
            skLineSegment(sketch, "E807", {"start": v(34.26, 55.17) * mm, "end": v(34.17, 55.1) * mm});
            skLineSegment(sketch, "E808", {"start": v(34.17, 55.1) * mm, "end": v(34.1, 55.03) * mm});
            skLineSegment(sketch, "E809", {"start": v(34.1, 55.03) * mm, "end": v(34.02, 54.96) * mm});
            skLineSegment(sketch, "E810", {"start": v(34.02, 54.96) * mm, "end": v(33.94, 54.89) * mm});
            skLineSegment(sketch, "E811", {"start": v(33.94, 54.89) * mm, "end": v(33.87, 54.82) * mm});
            skLineSegment(sketch, "E812", {"start": v(33.87, 54.82) * mm, "end": v(33.8, 54.75) * mm});
            skLineSegment(sketch, "E813", {"start": v(33.8, 54.75) * mm, "end": v(33.73, 54.69) * mm});
            skLineSegment(sketch, "E814", {"start": v(33.73, 54.69) * mm, "end": v(33.66, 54.62) * mm});
            skLineSegment(sketch, "E815", {"start": v(33.66, 54.62) * mm, "end": v(33.6, 54.56) * mm});
            skLineSegment(sketch, "E816", {"start": v(33.6, 54.56) * mm, "end": v(33.53, 54.5) * mm});
            skLineSegment(sketch, "E817", {"start": v(33.53, 54.5) * mm, "end": v(33.4, 54.37) * mm});
            skLineSegment(sketch, "E818", {"start": v(33.4, 54.37) * mm, "end": v(33.35, 54.31) * mm});
            skLineSegment(sketch, "E819", {"start": v(33.35, 54.31) * mm, "end": v(33.08, 54.33) * mm});
            skLineSegment(sketch, "E820", {"start": v(33.08, 54.33) * mm, "end": v(31.8, 55.09) * mm});
            skLineSegment(sketch, "E821", {"start": v(31.8, 55.09) * mm, "end": v(31.66, 55.32) * mm});
            skLineSegment(sketch, "E822", {"start": v(31.66, 55.32) * mm, "end": v(31.68, 55.4) * mm});
            skLineSegment(sketch, "E823", {"start": v(31.68, 55.4) * mm, "end": v(31.7, 55.48) * mm});
            skLineSegment(sketch, "E824", {"start": v(31.7, 55.48) * mm, "end": v(31.73, 55.56) * mm});
            skLineSegment(sketch, "E825", {"start": v(31.73, 55.56) * mm, "end": v(31.76, 55.65) * mm});
            skLineSegment(sketch, "E826", {"start": v(31.76, 55.65) * mm, "end": v(31.78, 55.74) * mm});
            skLineSegment(sketch, "E827", {"start": v(31.78, 55.74) * mm, "end": v(31.8, 55.83) * mm});
            skLineSegment(sketch, "E828", {"start": v(31.8, 55.83) * mm, "end": v(31.83, 55.92) * mm});
            skLineSegment(sketch, "E829", {"start": v(31.83, 55.92) * mm, "end": v(31.85, 56.01) * mm});
            skLineSegment(sketch, "E830", {"start": v(31.85, 56.01) * mm, "end": v(31.88, 56.11) * mm});
            skLineSegment(sketch, "E831", {"start": v(31.88, 56.11) * mm, "end": v(31.9, 56.21) * mm});
            skLineSegment(sketch, "E832", {"start": v(31.9, 56.21) * mm, "end": v(31.93, 56.31) * mm});
            skLineSegment(sketch, "E833", {"start": v(31.93, 56.31) * mm, "end": v(31.95, 56.42) * mm});
            skLineSegment(sketch, "E834", {"start": v(31.95, 56.42) * mm, "end": v(31.98, 56.52) * mm});
            skLineSegment(sketch, "E835", {"start": v(31.98, 56.52) * mm, "end": v(32.02, 56.74) * mm});
            skLineSegment(sketch, "E836", {"start": v(32.02, 56.74) * mm, "end": v(32.05, 56.85) * mm});
            skLineSegment(sketch, "E837", {"start": v(32.05, 56.85) * mm, "end": v(32.07, 56.97) * mm});
            skLineSegment(sketch, "E838", {"start": v(32.07, 56.97) * mm, "end": v(32.1, 57.08) * mm});
            skLineSegment(sketch, "E839", {"start": v(32.1, 57.08) * mm, "end": v(32.12, 57.2) * mm});
            skLineSegment(sketch, "E840", {"start": v(32.12, 57.2) * mm, "end": v(32.14, 57.32) * mm});
            skLineSegment(sketch, "E841", {"start": v(32.14, 57.32) * mm, "end": v(32.16, 57.44) * mm});
            skLineSegment(sketch, "E842", {"start": v(32.16, 57.44) * mm, "end": v(32.18, 57.57) * mm});
            skLineSegment(sketch, "E843", {"start": v(32.18, 57.57) * mm, "end": v(32.2, 57.7) * mm});
            skLineSegment(sketch, "E844", {"start": v(32.2, 57.7) * mm, "end": v(32.22, 57.83) * mm});
            skLineSegment(sketch, "E845", {"start": v(32.22, 57.83) * mm, "end": v(32.24, 57.96) * mm});
            skLineSegment(sketch, "E846", {"start": v(32.24, 57.96) * mm, "end": v(32.27, 58.1) * mm});
            skLineSegment(sketch, "E847", {"start": v(32.27, 58.1) * mm, "end": v(32.28, 58.23) * mm});
            skLineSegment(sketch, "E848", {"start": v(32.28, 58.23) * mm, "end": v(32.3, 58.37) * mm});
            skLineSegment(sketch, "E849", {"start": v(32.3, 58.37) * mm, "end": v(32.32, 58.5) * mm});
            skLineSegment(sketch, "E850", {"start": v(32.32, 58.5) * mm, "end": v(32.34, 58.65) * mm});
            skLineSegment(sketch, "E851", {"start": v(32.34, 58.65) * mm, "end": v(32.36, 58.8) * mm});
            skLineSegment(sketch, "E852", {"start": v(32.36, 58.8) * mm, "end": v(32.37, 58.95) * mm});
            skLineSegment(sketch, "E853", {"start": v(32.37, 58.95) * mm, "end": v(32.4, 59.1) * mm});
            skLineSegment(sketch, "E854", {"start": v(32.4, 59.1) * mm, "end": v(32.4, 59.25) * mm});
            skLineSegment(sketch, "E855", {"start": v(32.4, 59.25) * mm, "end": v(32.42, 59.4) * mm});
            skLineSegment(sketch, "E856", {"start": v(32.42, 59.4) * mm, "end": v(32.43, 59.56) * mm});
            skLineSegment(sketch, "E857", {"start": v(32.43, 59.56) * mm, "end": v(32.45, 59.71) * mm});
            skLineSegment(sketch, "E858", {"start": v(32.45, 59.71) * mm, "end": v(32.46, 59.88) * mm});
            skLineSegment(sketch, "E859", {"start": v(32.46, 59.88) * mm, "end": v(32.47, 60.04) * mm});
            skLineSegment(sketch, "E860", {"start": v(32.47, 60.04) * mm, "end": v(32.46, 60.15) * mm});
            skLineSegment(sketch, "E861", {"start": v(32.46, 60.15) * mm, "end": v(31.02, 60.9) * mm});
            skLineSegment(sketch, "E862", {"start": v(31.02, 60.9) * mm, "end": v(30.91, 60.86) * mm});
            skLineSegment(sketch, "E863", {"start": v(30.91, 60.86) * mm, "end": v(30.78, 60.76) * mm});
            skLineSegment(sketch, "E864", {"start": v(30.78, 60.76) * mm, "end": v(30.66, 60.65) * mm});
            skLineSegment(sketch, "E865", {"start": v(30.66, 60.65) * mm, "end": v(30.54, 60.55) * mm});
            skLineSegment(sketch, "E866", {"start": v(30.54, 60.55) * mm, "end": v(30.42, 60.45) * mm});
            skLineSegment(sketch, "E867", {"start": v(30.42, 60.45) * mm, "end": v(30.3, 60.35) * mm});
            skLineSegment(sketch, "E868", {"start": v(30.3, 60.35) * mm, "end": v(30.18, 60.25) * mm});
            skLineSegment(sketch, "E869", {"start": v(30.18, 60.25) * mm, "end": v(30.07, 60.15) * mm});
            skLineSegment(sketch, "E870", {"start": v(30.07, 60.15) * mm, "end": v(29.96, 60.06) * mm});
            skLineSegment(sketch, "E871", {"start": v(29.96, 60.06) * mm, "end": v(29.85, 59.96) * mm});
            skLineSegment(sketch, "E872", {"start": v(29.85, 59.96) * mm, "end": v(29.74, 59.86) * mm});
            skLineSegment(sketch, "E873", {"start": v(29.74, 59.86) * mm, "end": v(29.63, 59.77) * mm});
            skLineSegment(sketch, "E874", {"start": v(29.63, 59.77) * mm, "end": v(29.53, 59.67) * mm});
            skLineSegment(sketch, "E875", {"start": v(29.53, 59.67) * mm, "end": v(29.43, 59.58) * mm});
            skLineSegment(sketch, "E876", {"start": v(29.43, 59.58) * mm, "end": v(29.33, 59.49) * mm});
            skLineSegment(sketch, "E877", {"start": v(29.33, 59.49) * mm, "end": v(29.23, 59.4) * mm});
            skLineSegment(sketch, "E878", {"start": v(29.23, 59.4) * mm, "end": v(29.14, 59.3) * mm});
            skLineSegment(sketch, "E879", {"start": v(29.14, 59.3) * mm, "end": v(29.05, 59.21) * mm});
            skLineSegment(sketch, "E880", {"start": v(29.05, 59.21) * mm, "end": v(28.96, 59.12) * mm});
            skLineSegment(sketch, "E881", {"start": v(28.96, 59.12) * mm, "end": v(28.87, 59.04) * mm});
            skLineSegment(sketch, "E882", {"start": v(28.87, 59.04) * mm, "end": v(28.78, 58.95) * mm});
            skLineSegment(sketch, "E883", {"start": v(28.78, 58.95) * mm, "end": v(28.7, 58.86) * mm});
            skLineSegment(sketch, "E884", {"start": v(28.7, 58.86) * mm, "end": v(28.61, 58.78) * mm});
            skLineSegment(sketch, "E885", {"start": v(28.61, 58.78) * mm, "end": v(28.53, 58.7) * mm});
            skLineSegment(sketch, "E886", {"start": v(28.53, 58.7) * mm, "end": v(28.45, 58.61) * mm});
            skLineSegment(sketch, "E887", {"start": v(28.45, 58.61) * mm, "end": v(28.38, 58.53) * mm});
            skLineSegment(sketch, "E888", {"start": v(28.38, 58.53) * mm, "end": v(28.3, 58.45) * mm});
            skLineSegment(sketch, "E889", {"start": v(28.3, 58.45) * mm, "end": v(28.23, 58.37) * mm});
            skLineSegment(sketch, "E890", {"start": v(28.23, 58.37) * mm, "end": v(28.16, 58.29) * mm});
            skLineSegment(sketch, "E891", {"start": v(28.16, 58.29) * mm, "end": v(28.09, 58.21) * mm});
            skLineSegment(sketch, "E892", {"start": v(28.09, 58.21) * mm, "end": v(28.02, 58.14) * mm});
            skLineSegment(sketch, "E893", {"start": v(28.02, 58.14) * mm, "end": v(27.95, 58.06) * mm});
            skLineSegment(sketch, "E894", {"start": v(27.95, 58.06) * mm, "end": v(27.9, 57.98) * mm});
            skLineSegment(sketch, "E895", {"start": v(27.9, 57.98) * mm, "end": v(27.83, 57.91) * mm});
            skLineSegment(sketch, "E896", {"start": v(27.83, 57.91) * mm, "end": v(27.77, 57.84) * mm});
            skLineSegment(sketch, "E897", {"start": v(27.77, 57.84) * mm, "end": v(27.7, 57.77) * mm});
            skLineSegment(sketch, "E898", {"start": v(27.7, 57.77) * mm, "end": v(27.65, 57.7) * mm});
            skLineSegment(sketch, "E899", {"start": v(27.65, 57.7) * mm, "end": v(27.6, 57.63) * mm});
            skLineSegment(sketch, "E900", {"start": v(27.6, 57.63) * mm, "end": v(27.54, 57.57) * mm});
            skLineSegment(sketch, "E901", {"start": v(27.54, 57.57) * mm, "end": v(27.5, 57.5) * mm});
            skLineSegment(sketch, "E902", {"start": v(27.5, 57.5) * mm, "end": v(27.22, 57.5) * mm});
            skLineSegment(sketch, "E903", {"start": v(27.22, 57.5) * mm, "end": v(25.87, 58.11) * mm});
            skLineSegment(sketch, "E904", {"start": v(25.87, 58.11) * mm, "end": v(25.7, 58.32) * mm});
            skLineSegment(sketch, "E905", {"start": v(25.7, 58.32) * mm, "end": v(25.72, 58.4) * mm});
            skLineSegment(sketch, "E906", {"start": v(25.72, 58.4) * mm, "end": v(25.73, 58.49) * mm});
            skLineSegment(sketch, "E907", {"start": v(25.73, 58.49) * mm, "end": v(25.75, 58.57) * mm});
            skLineSegment(sketch, "E908", {"start": v(25.75, 58.57) * mm, "end": v(25.77, 58.66) * mm});
            skLineSegment(sketch, "E909", {"start": v(25.77, 58.66) * mm, "end": v(25.78, 58.75) * mm});
            skLineSegment(sketch, "E910", {"start": v(25.78, 58.75) * mm, "end": v(25.8, 58.85) * mm});
            skLineSegment(sketch, "E911", {"start": v(25.8, 58.85) * mm, "end": v(25.81, 58.94) * mm});
            skLineSegment(sketch, "E912", {"start": v(25.81, 58.94) * mm, "end": v(25.82, 59.04) * mm});
            skLineSegment(sketch, "E913", {"start": v(25.82, 59.04) * mm, "end": v(25.84, 59.14) * mm});
            skLineSegment(sketch, "E914", {"start": v(25.84, 59.14) * mm, "end": v(25.85, 59.24) * mm});
            skLineSegment(sketch, "E915", {"start": v(25.85, 59.24) * mm, "end": v(25.87, 59.34) * mm});
            skLineSegment(sketch, "E916", {"start": v(25.87, 59.34) * mm, "end": v(25.88, 59.45) * mm});
            skLineSegment(sketch, "E917", {"start": v(25.88, 59.45) * mm, "end": v(25.9, 59.55) * mm});
            skLineSegment(sketch, "E918", {"start": v(25.9, 59.55) * mm, "end": v(25.9, 59.66) * mm});
            skLineSegment(sketch, "E919", {"start": v(25.9, 59.66) * mm, "end": v(25.92, 59.77) * mm});
            skLineSegment(sketch, "E920", {"start": v(25.92, 59.77) * mm, "end": v(25.93, 59.89) * mm});
            skLineSegment(sketch, "E921", {"start": v(25.93, 59.89) * mm, "end": v(25.94, 60) * mm});
            skLineSegment(sketch, "E922", {"start": v(25.94, 60) * mm, "end": v(25.95, 60.12) * mm});
            skLineSegment(sketch, "E923", {"start": v(25.95, 60.12) * mm, "end": v(25.96, 60.24) * mm});
            skLineSegment(sketch, "E924", {"start": v(25.96, 60.24) * mm, "end": v(25.97, 60.37) * mm});
            skLineSegment(sketch, "E925", {"start": v(25.97, 60.37) * mm, "end": v(25.98, 60.5) * mm});
            skLineSegment(sketch, "E926", {"start": v(25.98, 60.5) * mm, "end": v(25.99, 60.62) * mm});
            skLineSegment(sketch, "E927", {"start": v(25.99, 60.62) * mm, "end": v(26, 60.75) * mm});
            skLineSegment(sketch, "E928", {"start": v(26, 60.75) * mm, "end": v(26, 60.88) * mm});
            skLineSegment(sketch, "E929", {"start": v(26, 60.88) * mm, "end": v(26.01, 61.01) * mm});
            skLineSegment(sketch, "E930", {"start": v(26.01, 61.01) * mm, "end": v(26.02, 61.15) * mm});
            skLineSegment(sketch, "E931", {"start": v(26.02, 61.15) * mm, "end": v(26.02, 61.29) * mm});
            skLineSegment(sketch, "E932", {"start": v(26.02, 61.29) * mm, "end": v(26.03, 61.43) * mm});
            skLineSegment(sketch, "E933", {"start": v(26.03, 61.43) * mm, "end": v(26.03, 61.57) * mm});
            skLineSegment(sketch, "E934", {"start": v(26.03, 61.57) * mm, "end": v(26.03, 61.71) * mm});
            skLineSegment(sketch, "E935", {"start": v(26.03, 61.71) * mm, "end": v(26.03, 61.86) * mm});
            skLineSegment(sketch, "E936", {"start": v(26.03, 61.86) * mm, "end": v(26.04, 62) * mm});
            skLineSegment(sketch, "E937", {"start": v(26.04, 62) * mm, "end": v(26.04, 62.16) * mm});
            skLineSegment(sketch, "E938", {"start": v(26.04, 62.16) * mm, "end": v(26.04, 62.3) * mm});
            skLineSegment(sketch, "E939", {"start": v(26.04, 62.3) * mm, "end": v(26.03, 62.46) * mm});
            skLineSegment(sketch, "E940", {"start": v(26.03, 62.46) * mm, "end": v(26.03, 62.62) * mm});
            skLineSegment(sketch, "E941", {"start": v(26.03, 62.62) * mm, "end": v(26.03, 62.78) * mm});
            skLineSegment(sketch, "E942", {"start": v(26.03, 62.78) * mm, "end": v(26.02, 62.94) * mm});
            skLineSegment(sketch, "E943", {"start": v(26.02, 62.94) * mm, "end": v(26.02, 63.1) * mm});
            skLineSegment(sketch, "E944", {"start": v(26.02, 63.1) * mm, "end": v(26, 63.22) * mm});
            skLineSegment(sketch, "E945", {"start": v(26, 63.22) * mm, "end": v(24.48, 63.82) * mm});
            skLineSegment(sketch, "E946", {"start": v(24.48, 63.82) * mm, "end": v(24.38, 63.76) * mm});
            skLineSegment(sketch, "E947", {"start": v(24.38, 63.76) * mm, "end": v(24.26, 63.64) * mm});
            skLineSegment(sketch, "E948", {"start": v(24.26, 63.64) * mm, "end": v(24.15, 63.52) * mm});
            skLineSegment(sketch, "E949", {"start": v(24.15, 63.52) * mm, "end": v(24.04, 63.41) * mm});
            skLineSegment(sketch, "E950", {"start": v(24.04, 63.41) * mm, "end": v(23.93, 63.3) * mm});
            skLineSegment(sketch, "E951", {"start": v(23.93, 63.3) * mm, "end": v(23.82, 63.19) * mm});
            skLineSegment(sketch, "E952", {"start": v(23.82, 63.19) * mm, "end": v(23.72, 63.08) * mm});
            skLineSegment(sketch, "E953", {"start": v(23.72, 63.08) * mm, "end": v(23.62, 62.97) * mm});
            skLineSegment(sketch, "E954", {"start": v(23.62, 62.97) * mm, "end": v(23.51, 62.86) * mm});
            skLineSegment(sketch, "E955", {"start": v(23.51, 62.86) * mm, "end": v(23.32, 62.64) * mm});
            skLineSegment(sketch, "E956", {"start": v(23.32, 62.64) * mm, "end": v(23.23, 62.54) * mm});
            skLineSegment(sketch, "E957", {"start": v(23.23, 62.54) * mm, "end": v(23.13, 62.43) * mm});
            skLineSegment(sketch, "E958", {"start": v(23.13, 62.43) * mm, "end": v(22.95, 62.23) * mm});
            skLineSegment(sketch, "E959", {"start": v(22.95, 62.23) * mm, "end": v(22.87, 62.13) * mm});
            skLineSegment(sketch, "E960", {"start": v(22.87, 62.13) * mm, "end": v(22.78, 62.03) * mm});
            skLineSegment(sketch, "E961", {"start": v(22.78, 62.03) * mm, "end": v(22.7, 61.93) * mm});
            skLineSegment(sketch, "E962", {"start": v(22.7, 61.93) * mm, "end": v(22.62, 61.83) * mm});
            skLineSegment(sketch, "E963", {"start": v(22.62, 61.83) * mm, "end": v(22.54, 61.73) * mm});
            skLineSegment(sketch, "E964", {"start": v(22.54, 61.73) * mm, "end": v(22.46, 61.63) * mm});
            skLineSegment(sketch, "E965", {"start": v(22.46, 61.63) * mm, "end": v(22.31, 61.45) * mm});
            skLineSegment(sketch, "E966", {"start": v(22.31, 61.45) * mm, "end": v(22.24, 61.35) * mm});
            skLineSegment(sketch, "E967", {"start": v(22.24, 61.35) * mm, "end": v(22.17, 61.26) * mm});
            skLineSegment(sketch, "E968", {"start": v(22.17, 61.26) * mm, "end": v(22.1, 61.17) * mm});
            skLineSegment(sketch, "E969", {"start": v(22.1, 61.17) * mm, "end": v(22.04, 61.09) * mm});
            skLineSegment(sketch, "E970", {"start": v(22.04, 61.09) * mm, "end": v(21.9, 60.91) * mm});
            skLineSegment(sketch, "E971", {"start": v(21.9, 60.91) * mm, "end": v(21.85, 60.83) * mm});
            skLineSegment(sketch, "E972", {"start": v(21.85, 60.83) * mm, "end": v(21.79, 60.75) * mm});
            skLineSegment(sketch, "E973", {"start": v(21.79, 60.75) * mm, "end": v(21.73, 60.66) * mm});
            skLineSegment(sketch, "E974", {"start": v(21.73, 60.66) * mm, "end": v(21.68, 60.58) * mm});
            skLineSegment(sketch, "E975", {"start": v(21.68, 60.58) * mm, "end": v(21.62, 60.5) * mm});
            skLineSegment(sketch, "E976", {"start": v(21.62, 60.5) * mm, "end": v(21.57, 60.43) * mm});
            skLineSegment(sketch, "E977", {"start": v(21.57, 60.43) * mm, "end": v(21.52, 60.35) * mm});
            skLineSegment(sketch, "E978", {"start": v(21.52, 60.35) * mm, "end": v(21.47, 60.28) * mm});
            skLineSegment(sketch, "E979", {"start": v(21.47, 60.28) * mm, "end": v(21.42, 60.2) * mm});
            skLineSegment(sketch, "E980", {"start": v(21.42, 60.2) * mm, "end": v(21.37, 60.13) * mm});
            skLineSegment(sketch, "E981", {"start": v(21.37, 60.13) * mm, "end": v(21.33, 60.06) * mm});
            skLineSegment(sketch, "E982", {"start": v(21.33, 60.06) * mm, "end": v(21.06, 60.02) * mm});
            skLineSegment(sketch, "E983", {"start": v(21.06, 60.02) * mm, "end": v(19.66, 60.5) * mm});
            skLineSegment(sketch, "E984", {"start": v(19.66, 60.5) * mm, "end": v(19.47, 60.7) * mm});
            skLineSegment(sketch, "E985", {"start": v(19.47, 60.7) * mm, "end": v(19.47, 60.77) * mm});
            skLineSegment(sketch, "E986", {"start": v(19.47, 60.77) * mm, "end": v(19.48, 60.86) * mm});
            skLineSegment(sketch, "E987", {"start": v(19.48, 60.86) * mm, "end": v(19.49, 60.95) * mm});
            skLineSegment(sketch, "E988", {"start": v(19.49, 60.95) * mm, "end": v(19.5, 61.03) * mm});
            skLineSegment(sketch, "E989", {"start": v(19.5, 61.03) * mm, "end": v(19.5, 61.22) * mm});
            skLineSegment(sketch, "E990", {"start": v(19.5, 61.22) * mm, "end": v(19.5, 61.32) * mm});
            skLineSegment(sketch, "E991", {"start": v(19.5, 61.32) * mm, "end": v(19.51, 61.41) * mm});
            skLineSegment(sketch, "E992", {"start": v(19.51, 61.41) * mm, "end": v(19.52, 61.51) * mm});
            skLineSegment(sketch, "E993", {"start": v(19.52, 61.51) * mm, "end": v(19.52, 61.61) * mm});
            skLineSegment(sketch, "E994", {"start": v(19.52, 61.61) * mm, "end": v(19.52, 61.72) * mm});
            skLineSegment(sketch, "E995", {"start": v(19.52, 61.72) * mm, "end": v(19.52, 61.83) * mm});
            skLineSegment(sketch, "E996", {"start": v(19.52, 61.83) * mm, "end": v(19.53, 61.93) * mm});
            skLineSegment(sketch, "E997", {"start": v(19.53, 61.93) * mm, "end": v(19.53, 62.04) * mm});
            skLineSegment(sketch, "E998", {"start": v(19.53, 62.04) * mm, "end": v(19.53, 62.27) * mm});
            skLineSegment(sketch, "E999", {"start": v(19.53, 62.27) * mm, "end": v(19.53, 62.39) * mm});
            skLineSegment(sketch, "E1000", {"start": v(19.53, 62.39) * mm, "end": v(19.52, 62.5) * mm});
            skLineSegment(sketch, "E1001", {"start": v(19.52, 62.5) * mm, "end": v(19.52, 62.63) * mm});
            skLineSegment(sketch, "E1002", {"start": v(19.52, 62.63) * mm, "end": v(19.52, 62.75) * mm});
            skLineSegment(sketch, "E1003", {"start": v(19.52, 62.75) * mm, "end": v(19.51, 62.88) * mm});
            skLineSegment(sketch, "E1004", {"start": v(19.51, 62.88) * mm, "end": v(19.5, 63.13) * mm});
            skLineSegment(sketch, "E1005", {"start": v(19.5, 63.13) * mm, "end": v(19.5, 63.26) * mm});
            skLineSegment(sketch, "E1006", {"start": v(19.5, 63.26) * mm, "end": v(19.49, 63.4) * mm});
            skLineSegment(sketch, "E1007", {"start": v(19.49, 63.4) * mm, "end": v(19.47, 63.67) * mm});
            skLineSegment(sketch, "E1008", {"start": v(19.47, 63.67) * mm, "end": v(19.45, 63.95) * mm});
            skLineSegment(sketch, "E1009", {"start": v(19.45, 63.95) * mm, "end": v(19.43, 64.24) * mm});
            skLineSegment(sketch, "E1010", {"start": v(19.43, 64.24) * mm, "end": v(19.41, 64.39) * mm});
            skLineSegment(sketch, "E1011", {"start": v(19.41, 64.39) * mm, "end": v(19.4, 64.54) * mm});
            skLineSegment(sketch, "E1012", {"start": v(19.4, 64.54) * mm, "end": v(19.38, 64.69) * mm});
            skLineSegment(sketch, "E1013", {"start": v(19.38, 64.69) * mm, "end": v(19.36, 64.84) * mm});
            skLineSegment(sketch, "E1014", {"start": v(19.36, 64.84) * mm, "end": v(19.34, 65) * mm});
            skLineSegment(sketch, "E1015", {"start": v(19.34, 65) * mm, "end": v(19.32, 65.16) * mm});
            skLineSegment(sketch, "E1016", {"start": v(19.32, 65.16) * mm, "end": v(19.3, 65.32) * mm});
            skLineSegment(sketch, "E1017", {"start": v(19.3, 65.32) * mm, "end": v(19.28, 65.48) * mm});
            skLineSegment(sketch, "E1018", {"start": v(19.28, 65.48) * mm, "end": v(19.24, 65.59) * mm});
            skLineSegment(sketch, "E1019", {"start": v(19.24, 65.59) * mm, "end": v(17.67, 66.03) * mm});
            skLineSegment(sketch, "E1020", {"start": v(17.67, 66.03) * mm, "end": v(17.58, 65.95) * mm});
            skLineSegment(sketch, "E1021", {"start": v(17.58, 65.95) * mm, "end": v(17.38, 65.7) * mm});
            skLineSegment(sketch, "E1022", {"start": v(17.38, 65.7) * mm, "end": v(17.18, 65.45) * mm});
            skLineSegment(sketch, "E1023", {"start": v(17.18, 65.45) * mm, "end": v(17, 65.21) * mm});
            skLineSegment(sketch, "E1024", {"start": v(17, 65.21) * mm, "end": v(16.9, 65.1) * mm});
            skLineSegment(sketch, "E1025", {"start": v(16.9, 65.1) * mm, "end": v(16.82, 64.97) * mm});
            skLineSegment(sketch, "E1026", {"start": v(16.82, 64.97) * mm, "end": v(16.73, 64.85) * mm});
            skLineSegment(sketch, "E1027", {"start": v(16.73, 64.85) * mm, "end": v(16.64, 64.74) * mm});
            skLineSegment(sketch, "E1028", {"start": v(16.64, 64.74) * mm, "end": v(16.56, 64.62) * mm});
            skLineSegment(sketch, "E1029", {"start": v(16.56, 64.62) * mm, "end": v(16.48, 64.5) * mm});
            skLineSegment(sketch, "E1030", {"start": v(16.48, 64.5) * mm, "end": v(16.4, 64.4) * mm});
            skLineSegment(sketch, "E1031", {"start": v(16.4, 64.4) * mm, "end": v(16.32, 64.29) * mm});
            skLineSegment(sketch, "E1032", {"start": v(16.32, 64.29) * mm, "end": v(16.25, 64.18) * mm});
            skLineSegment(sketch, "E1033", {"start": v(16.25, 64.18) * mm, "end": v(16.17, 64.07) * mm});
            skLineSegment(sketch, "E1034", {"start": v(16.17, 64.07) * mm, "end": v(16.1, 63.96) * mm});
            skLineSegment(sketch, "E1035", {"start": v(16.1, 63.96) * mm, "end": v(16.03, 63.85) * mm});
            skLineSegment(sketch, "E1036", {"start": v(16.03, 63.85) * mm, "end": v(15.96, 63.75) * mm});
            skLineSegment(sketch, "E1037", {"start": v(15.96, 63.75) * mm, "end": v(15.9, 63.64) * mm});
            skLineSegment(sketch, "E1038", {"start": v(15.9, 63.64) * mm, "end": v(15.83, 63.54) * mm});
            skLineSegment(sketch, "E1039", {"start": v(15.83, 63.54) * mm, "end": v(15.77, 63.44) * mm});
            skLineSegment(sketch, "E1040", {"start": v(15.77, 63.44) * mm, "end": v(15.7, 63.34) * mm});
            skLineSegment(sketch, "E1041", {"start": v(15.7, 63.34) * mm, "end": v(15.65, 63.25) * mm});
            skLineSegment(sketch, "E1042", {"start": v(15.65, 63.25) * mm, "end": v(15.59, 63.15) * mm});
            skLineSegment(sketch, "E1043", {"start": v(15.59, 63.15) * mm, "end": v(15.53, 63.05) * mm});
            skLineSegment(sketch, "E1044", {"start": v(15.53, 63.05) * mm, "end": v(15.48, 62.96) * mm});
            skLineSegment(sketch, "E1045", {"start": v(15.48, 62.96) * mm, "end": v(15.42, 62.87) * mm});
            skLineSegment(sketch, "E1046", {"start": v(15.42, 62.87) * mm, "end": v(15.37, 62.78) * mm});
            skLineSegment(sketch, "E1047", {"start": v(15.37, 62.78) * mm, "end": v(15.32, 62.69) * mm});
            skLineSegment(sketch, "E1048", {"start": v(15.32, 62.69) * mm, "end": v(15.27, 62.6) * mm});
            skLineSegment(sketch, "E1049", {"start": v(15.27, 62.6) * mm, "end": v(15.22, 62.52) * mm});
            skLineSegment(sketch, "E1050", {"start": v(15.22, 62.52) * mm, "end": v(15.18, 62.43) * mm});
            skLineSegment(sketch, "E1051", {"start": v(15.18, 62.43) * mm, "end": v(15.13, 62.35) * mm});
            skLineSegment(sketch, "E1052", {"start": v(15.13, 62.35) * mm, "end": v(15.1, 62.27) * mm});
            skLineSegment(sketch, "E1053", {"start": v(15.1, 62.27) * mm, "end": v(15.05, 62.19) * mm});
            skLineSegment(sketch, "E1054", {"start": v(15.05, 62.19) * mm, "end": v(15.01, 62.11) * mm});
            skLineSegment(sketch, "E1055", {"start": v(15.01, 62.11) * mm, "end": v(14.97, 62.04) * mm});
            skLineSegment(sketch, "E1056", {"start": v(14.97, 62.04) * mm, "end": v(14.94, 61.96) * mm});
            skLineSegment(sketch, "E1057", {"start": v(14.94, 61.96) * mm, "end": v(14.67, 61.9) * mm});
            skLineSegment(sketch, "E1058", {"start": v(14.67, 61.9) * mm, "end": v(13.22, 62.22) * mm});
            skLineSegment(sketch, "E1059", {"start": v(13.22, 62.22) * mm, "end": v(13.02, 62.4) * mm});
            skLineSegment(sketch, "E1060", {"start": v(13.02, 62.4) * mm, "end": v(13.01, 62.48) * mm});
            skLineSegment(sketch, "E1061", {"start": v(13.01, 62.48) * mm, "end": v(13.01, 62.56) * mm});
            skLineSegment(sketch, "E1062", {"start": v(13.01, 62.56) * mm, "end": v(13, 62.65) * mm});
            skLineSegment(sketch, "E1063", {"start": v(13, 62.65) * mm, "end": v(13, 62.74) * mm});
            skLineSegment(sketch, "E1064", {"start": v(13, 62.74) * mm, "end": v(13, 62.92) * mm});
            skLineSegment(sketch, "E1065", {"start": v(13, 62.92) * mm, "end": v(13, 63.02) * mm});
            skLineSegment(sketch, "E1066", {"start": v(13, 63.02) * mm, "end": v(12.99, 63.12) * mm});
            skLineSegment(sketch, "E1067", {"start": v(12.99, 63.12) * mm, "end": v(12.98, 63.22) * mm});
            skLineSegment(sketch, "E1068", {"start": v(12.98, 63.22) * mm, "end": v(12.97, 63.32) * mm});
            skLineSegment(sketch, "E1069", {"start": v(12.97, 63.32) * mm, "end": v(12.96, 63.42) * mm});
            skLineSegment(sketch, "E1070", {"start": v(12.96, 63.42) * mm, "end": v(12.96, 63.53) * mm});
            skLineSegment(sketch, "E1071", {"start": v(12.96, 63.53) * mm, "end": v(12.95, 63.64) * mm});
            skLineSegment(sketch, "E1072", {"start": v(12.95, 63.64) * mm, "end": v(12.93, 63.75) * mm});
            skLineSegment(sketch, "E1073", {"start": v(12.93, 63.75) * mm, "end": v(12.92, 63.86) * mm});
            skLineSegment(sketch, "E1074", {"start": v(12.92, 63.86) * mm, "end": v(12.91, 63.97) * mm});
            skLineSegment(sketch, "E1075", {"start": v(12.91, 63.97) * mm, "end": v(12.9, 64.09) * mm});
            skLineSegment(sketch, "E1076", {"start": v(12.9, 64.09) * mm, "end": v(12.88, 64.2) * mm});
            skLineSegment(sketch, "E1077", {"start": v(12.88, 64.2) * mm, "end": v(12.87, 64.33) * mm});
            skLineSegment(sketch, "E1078", {"start": v(12.87, 64.33) * mm, "end": v(12.85, 64.45) * mm});
            skLineSegment(sketch, "E1079", {"start": v(12.85, 64.45) * mm, "end": v(12.84, 64.57) * mm});
            skLineSegment(sketch, "E1080", {"start": v(12.84, 64.57) * mm, "end": v(12.82, 64.7) * mm});
            skLineSegment(sketch, "E1081", {"start": v(12.82, 64.7) * mm, "end": v(12.8, 64.83) * mm});
            skLineSegment(sketch, "E1082", {"start": v(12.8, 64.83) * mm, "end": v(12.78, 64.96) * mm});
            skLineSegment(sketch, "E1083", {"start": v(12.78, 64.96) * mm, "end": v(12.76, 65.09) * mm});
            skLineSegment(sketch, "E1084", {"start": v(12.76, 65.09) * mm, "end": v(12.73, 65.22) * mm});
            skLineSegment(sketch, "E1085", {"start": v(12.73, 65.22) * mm, "end": v(12.71, 65.36) * mm});
            skLineSegment(sketch, "E1086", {"start": v(12.71, 65.36) * mm, "end": v(12.69, 65.5) * mm});
            skLineSegment(sketch, "E1087", {"start": v(12.69, 65.5) * mm, "end": v(12.66, 65.63) * mm});
            skLineSegment(sketch, "E1088", {"start": v(12.66, 65.63) * mm, "end": v(12.63, 65.78) * mm});
            skLineSegment(sketch, "E1089", {"start": v(12.63, 65.78) * mm, "end": v(12.6, 65.92) * mm});
            skLineSegment(sketch, "E1090", {"start": v(12.6, 65.92) * mm, "end": v(12.57, 66.06) * mm});
            skLineSegment(sketch, "E1091", {"start": v(12.57, 66.06) * mm, "end": v(12.54, 66.21) * mm});
            skLineSegment(sketch, "E1092", {"start": v(12.54, 66.21) * mm, "end": v(12.51, 66.36) * mm});
            skLineSegment(sketch, "E1093", {"start": v(12.51, 66.36) * mm, "end": v(12.44, 66.66) * mm});
            skLineSegment(sketch, "E1094", {"start": v(12.44, 66.66) * mm, "end": v(12.4, 66.82) * mm});
            skLineSegment(sketch, "E1095", {"start": v(12.4, 66.82) * mm, "end": v(12.37, 66.98) * mm});
            skLineSegment(sketch, "E1096", {"start": v(12.37, 66.98) * mm, "end": v(12.33, 67.13) * mm});
            skLineSegment(sketch, "E1097", {"start": v(12.33, 67.13) * mm, "end": v(12.28, 67.24) * mm});
            skLineSegment(sketch, "E1098", {"start": v(12.28, 67.24) * mm, "end": v(10.68, 67.51) * mm});
            skLineSegment(sketch, "E1099", {"start": v(10.68, 67.51) * mm, "end": v(10.6, 67.43) * mm});
            skLineSegment(sketch, "E1100", {"start": v(10.6, 67.43) * mm, "end": v(10.5, 67.3) * mm});
            skLineSegment(sketch, "E1101", {"start": v(10.5, 67.3) * mm, "end": v(10.42, 67.16) * mm});
            skLineSegment(sketch, "E1102", {"start": v(10.42, 67.16) * mm, "end": v(10.33, 67.02) * mm});
            skLineSegment(sketch, "E1103", {"start": v(10.33, 67.02) * mm, "end": v(10.25, 66.9) * mm});
            skLineSegment(sketch, "E1104", {"start": v(10.25, 66.9) * mm, "end": v(10.17, 66.76) * mm});
            skLineSegment(sketch, "E1105", {"start": v(10.17, 66.76) * mm, "end": v(10.09, 66.63) * mm});
            skLineSegment(sketch, "E1106", {"start": v(10.09, 66.63) * mm, "end": v(10, 66.5) * mm});
            skLineSegment(sketch, "E1107", {"start": v(10, 66.5) * mm, "end": v(9.93, 66.37) * mm});
            skLineSegment(sketch, "E1108", {"start": v(9.93, 66.37) * mm, "end": v(9.86, 66.25) * mm});
            skLineSegment(sketch, "E1109", {"start": v(9.86, 66.25) * mm, "end": v(9.79, 66.12) * mm});
            skLineSegment(sketch, "E1110", {"start": v(9.79, 66.12) * mm, "end": v(9.72, 66) * mm});
            skLineSegment(sketch, "E1111", {"start": v(9.72, 66) * mm, "end": v(9.65, 65.88) * mm});
            skLineSegment(sketch, "E1112", {"start": v(9.65, 65.88) * mm, "end": v(9.58, 65.76) * mm});
            skLineSegment(sketch, "E1113", {"start": v(9.58, 65.76) * mm, "end": v(9.45, 65.52) * mm});
            skLineSegment(sketch, "E1114", {"start": v(9.45, 65.52) * mm, "end": v(9.39, 65.4) * mm});
            skLineSegment(sketch, "E1115", {"start": v(9.39, 65.4) * mm, "end": v(9.33, 65.3) * mm});
            skLineSegment(sketch, "E1116", {"start": v(9.33, 65.3) * mm, "end": v(9.27, 65.18) * mm});
            skLineSegment(sketch, "E1117", {"start": v(9.27, 65.18) * mm, "end": v(9.21, 65.07) * mm});
            skLineSegment(sketch, "E1118", {"start": v(9.21, 65.07) * mm, "end": v(9.16, 64.96) * mm});
            skLineSegment(sketch, "E1119", {"start": v(9.16, 64.96) * mm, "end": v(9.1, 64.85) * mm});
            skLineSegment(sketch, "E1120", {"start": v(9.1, 64.85) * mm, "end": v(9.05, 64.74) * mm});
            skLineSegment(sketch, "E1121", {"start": v(9.05, 64.74) * mm, "end": v(9, 64.64) * mm});
            skLineSegment(sketch, "E1122", {"start": v(9, 64.64) * mm, "end": v(8.95, 64.54) * mm});
            skLineSegment(sketch, "E1123", {"start": v(8.95, 64.54) * mm, "end": v(8.9, 64.43) * mm});
            skLineSegment(sketch, "E1124", {"start": v(8.9, 64.43) * mm, "end": v(8.86, 64.33) * mm});
            skLineSegment(sketch, "E1125", {"start": v(8.86, 64.33) * mm, "end": v(8.8, 64.23) * mm});
            skLineSegment(sketch, "E1126", {"start": v(8.8, 64.23) * mm, "end": v(8.77, 64.14) * mm});
            skLineSegment(sketch, "E1127", {"start": v(8.77, 64.14) * mm, "end": v(8.72, 64.04) * mm});
            skLineSegment(sketch, "E1128", {"start": v(8.72, 64.04) * mm, "end": v(8.68, 63.95) * mm});
            skLineSegment(sketch, "E1129", {"start": v(8.68, 63.95) * mm, "end": v(8.64, 63.86) * mm});
            skLineSegment(sketch, "E1130", {"start": v(8.64, 63.86) * mm, "end": v(8.6, 63.77) * mm});
            skLineSegment(sketch, "E1131", {"start": v(8.6, 63.77) * mm, "end": v(8.57, 63.68) * mm});
            skLineSegment(sketch, "E1132", {"start": v(8.57, 63.68) * mm, "end": v(8.53, 63.6) * mm});
            skLineSegment(sketch, "E1133", {"start": v(8.53, 63.6) * mm, "end": v(8.5, 63.5) * mm});
            skLineSegment(sketch, "E1134", {"start": v(8.5, 63.5) * mm, "end": v(8.47, 63.42) * mm});
            skLineSegment(sketch, "E1135", {"start": v(8.47, 63.42) * mm, "end": v(8.44, 63.34) * mm});
            skLineSegment(sketch, "E1136", {"start": v(8.44, 63.34) * mm, "end": v(8.4, 63.26) * mm});
            skLineSegment(sketch, "E1137", {"start": v(8.4, 63.26) * mm, "end": v(8.38, 63.18) * mm});
            skLineSegment(sketch, "E1138", {"start": v(8.38, 63.18) * mm, "end": v(8.12, 63.09) * mm});
            skLineSegment(sketch, "E1139", {"start": v(8.12, 63.09) * mm, "end": v(6.65, 63.26) * mm});
            skLineSegment(sketch, "E1140", {"start": v(6.65, 63.26) * mm, "end": v(6.42, 63.41) * mm});
            skLineSegment(sketch, "E1141", {"start": v(6.42, 63.41) * mm, "end": v(6.41, 63.5) * mm});
            skLineSegment(sketch, "E1142", {"start": v(6.41, 63.5) * mm, "end": v(6.4, 63.58) * mm});
            skLineSegment(sketch, "E1143", {"start": v(6.4, 63.58) * mm, "end": v(6.39, 63.67) * mm});
            skLineSegment(sketch, "E1144", {"start": v(6.39, 63.67) * mm, "end": v(6.38, 63.75) * mm});
            skLineSegment(sketch, "E1145", {"start": v(6.38, 63.75) * mm, "end": v(6.36, 63.84) * mm});
            skLineSegment(sketch, "E1146", {"start": v(6.36, 63.84) * mm, "end": v(6.35, 63.94) * mm});
            skLineSegment(sketch, "E1147", {"start": v(6.35, 63.94) * mm, "end": v(6.33, 64.03) * mm});
            skLineSegment(sketch, "E1148", {"start": v(6.33, 64.03) * mm, "end": v(6.32, 64.13) * mm});
            skLineSegment(sketch, "E1149", {"start": v(6.32, 64.13) * mm, "end": v(6.3, 64.23) * mm});
            skLineSegment(sketch, "E1150", {"start": v(6.3, 64.23) * mm, "end": v(6.28, 64.33) * mm});
            skLineSegment(sketch, "E1151", {"start": v(6.28, 64.33) * mm, "end": v(6.26, 64.43) * mm});
            skLineSegment(sketch, "E1152", {"start": v(6.26, 64.43) * mm, "end": v(6.24, 64.53) * mm});
            skLineSegment(sketch, "E1153", {"start": v(6.24, 64.53) * mm, "end": v(6.22, 64.64) * mm});
            skLineSegment(sketch, "E1154", {"start": v(6.22, 64.64) * mm, "end": v(6.2, 64.75) * mm});
            skLineSegment(sketch, "E1155", {"start": v(6.2, 64.75) * mm, "end": v(6.18, 64.86) * mm});
            skLineSegment(sketch, "E1156", {"start": v(6.18, 64.86) * mm, "end": v(6.15, 64.97) * mm});
            skLineSegment(sketch, "E1157", {"start": v(6.15, 64.97) * mm, "end": v(6.13, 65.08) * mm});
            skLineSegment(sketch, "E1158", {"start": v(6.13, 65.08) * mm, "end": v(6.1, 65.2) * mm});
            skLineSegment(sketch, "E1159", {"start": v(6.1, 65.2) * mm, "end": v(6.07, 65.32) * mm});
            skLineSegment(sketch, "E1160", {"start": v(6.07, 65.32) * mm, "end": v(6.05, 65.44) * mm});
            skLineSegment(sketch, "E1161", {"start": v(6.05, 65.44) * mm, "end": v(6.02, 65.56) * mm});
            skLineSegment(sketch, "E1162", {"start": v(6.02, 65.56) * mm, "end": v(5.98, 65.68) * mm});
            skLineSegment(sketch, "E1163", {"start": v(5.98, 65.68) * mm, "end": v(5.95, 65.8) * mm});
            skLineSegment(sketch, "E1164", {"start": v(5.95, 65.8) * mm, "end": v(5.92, 65.93) * mm});
            skLineSegment(sketch, "E1165", {"start": v(5.92, 65.93) * mm, "end": v(5.88, 66.06) * mm});
            skLineSegment(sketch, "E1166", {"start": v(5.88, 66.06) * mm, "end": v(5.85, 66.2) * mm});
            skLineSegment(sketch, "E1167", {"start": v(5.85, 66.2) * mm, "end": v(5.8, 66.33) * mm});
            skLineSegment(sketch, "E1168", {"start": v(5.8, 66.33) * mm, "end": v(5.77, 66.46) * mm});
            skLineSegment(sketch, "E1169", {"start": v(5.77, 66.46) * mm, "end": v(5.73, 66.6) * mm});
            skLineSegment(sketch, "E1170", {"start": v(5.73, 66.6) * mm, "end": v(5.69, 66.74) * mm});
            skLineSegment(sketch, "E1171", {"start": v(5.69, 66.74) * mm, "end": v(5.6, 67.02) * mm});
            skLineSegment(sketch, "E1172", {"start": v(5.6, 67.02) * mm, "end": v(5.55, 67.16) * mm});
            skLineSegment(sketch, "E1173", {"start": v(5.55, 67.16) * mm, "end": v(5.5, 67.3) * mm});
            skLineSegment(sketch, "E1174", {"start": v(5.5, 67.3) * mm, "end": v(5.46, 67.45) * mm});
            skLineSegment(sketch, "E1175", {"start": v(5.46, 67.45) * mm, "end": v(5.4, 67.6) * mm});
            skLineSegment(sketch, "E1176", {"start": v(5.4, 67.6) * mm, "end": v(5.36, 67.75) * mm});
            skLineSegment(sketch, "E1177", {"start": v(5.36, 67.75) * mm, "end": v(5.3, 67.9) * mm});
            skLineSegment(sketch, "E1178", {"start": v(5.3, 67.9) * mm, "end": v(5.25, 68.06) * mm});
            skLineSegment(sketch, "E1179", {"start": v(5.25, 68.06) * mm, "end": v(5.18, 68.15) * mm});
            skLineSegment(sketch, "E1180", {"start": v(5.18, 68.15) * mm, "end": v(3.56, 68.26) * mm});
            skLineSegment(sketch, "E1181", {"start": v(3.56, 68.26) * mm, "end": v(3.49, 68.17) * mm});
            skLineSegment(sketch, "E1182", {"start": v(3.49, 68.17) * mm, "end": v(3.41, 68.02) * mm});
            skLineSegment(sketch, "E1183", {"start": v(3.41, 68.02) * mm, "end": v(3.34, 67.88) * mm});
            skLineSegment(sketch, "E1184", {"start": v(3.34, 67.88) * mm, "end": v(3.27, 67.74) * mm});
            skLineSegment(sketch, "E1185", {"start": v(3.27, 67.74) * mm, "end": v(3.2, 67.6) * mm});
            skLineSegment(sketch, "E1186", {"start": v(3.2, 67.6) * mm, "end": v(3.13, 67.46) * mm});
            skLineSegment(sketch, "E1187", {"start": v(3.13, 67.46) * mm, "end": v(3.07, 67.32) * mm});
            skLineSegment(sketch, "E1188", {"start": v(3.07, 67.32) * mm, "end": v(3, 67.18) * mm});
            skLineSegment(sketch, "E1189", {"start": v(3, 67.18) * mm, "end": v(2.94, 67.05) * mm});
            skLineSegment(sketch, "E1190", {"start": v(2.94, 67.05) * mm, "end": v(2.88, 66.92) * mm});
            skLineSegment(sketch, "E1191", {"start": v(2.88, 66.92) * mm, "end": v(2.82, 66.78) * mm});
            skLineSegment(sketch, "E1192", {"start": v(2.82, 66.78) * mm, "end": v(2.76, 66.65) * mm});
            skLineSegment(sketch, "E1193", {"start": v(2.76, 66.65) * mm, "end": v(2.7, 66.53) * mm});
            skLineSegment(sketch, "E1194", {"start": v(2.7, 66.53) * mm, "end": v(2.65, 66.4) * mm});
            skLineSegment(sketch, "E1195", {"start": v(2.65, 66.4) * mm, "end": v(2.6, 66.27) * mm});
            skLineSegment(sketch, "E1196", {"start": v(2.6, 66.27) * mm, "end": v(2.55, 66.15) * mm});
            skLineSegment(sketch, "E1197", {"start": v(2.55, 66.15) * mm, "end": v(2.5, 66.03) * mm});
            skLineSegment(sketch, "E1198", {"start": v(2.5, 66.03) * mm, "end": v(2.45, 65.9) * mm});
            skLineSegment(sketch, "E1199", {"start": v(2.45, 65.9) * mm, "end": v(2.4, 65.8) * mm});
            skLineSegment(sketch, "E1200", {"start": v(2.4, 65.8) * mm, "end": v(2.36, 65.67) * mm});
            skLineSegment(sketch, "E1201", {"start": v(2.36, 65.67) * mm, "end": v(2.32, 65.56) * mm});
            skLineSegment(sketch, "E1202", {"start": v(2.32, 65.56) * mm, "end": v(2.27, 65.45) * mm});
            skLineSegment(sketch, "E1203", {"start": v(2.27, 65.45) * mm, "end": v(2.23, 65.33) * mm});
            skLineSegment(sketch, "E1204", {"start": v(2.23, 65.33) * mm, "end": v(2.2, 65.22) * mm});
            skLineSegment(sketch, "E1205", {"start": v(2.2, 65.22) * mm, "end": v(2.15, 65.12) * mm});
            skLineSegment(sketch, "E1206", {"start": v(2.15, 65.12) * mm, "end": v(2.12, 65.01) * mm});
            skLineSegment(sketch, "E1207", {"start": v(2.12, 65.01) * mm, "end": v(2.08, 64.9) * mm});
            skLineSegment(sketch, "E1208", {"start": v(2.08, 64.9) * mm, "end": v(2.05, 64.8) * mm});
            skLineSegment(sketch, "E1209", {"start": v(2.05, 64.8) * mm, "end": v(2.01, 64.7) * mm});
            skLineSegment(sketch, "E1210", {"start": v(2.01, 64.7) * mm, "end": v(1.98, 64.6) * mm});
            skLineSegment(sketch, "E1211", {"start": v(1.98, 64.6) * mm, "end": v(1.95, 64.5) * mm});
            skLineSegment(sketch, "E1212", {"start": v(1.95, 64.5) * mm, "end": v(1.92, 64.4) * mm});
            skLineSegment(sketch, "E1213", {"start": v(1.92, 64.4) * mm, "end": v(1.9, 64.32) * mm});
            skLineSegment(sketch, "E1214", {"start": v(1.9, 64.32) * mm, "end": v(1.84, 64.13) * mm});
            skLineSegment(sketch, "E1215", {"start": v(1.84, 64.13) * mm, "end": v(1.8, 63.96) * mm});
            skLineSegment(sketch, "E1216", {"start": v(1.8, 63.96) * mm, "end": v(1.77, 63.88) * mm});
            skLineSegment(sketch, "E1217", {"start": v(1.77, 63.88) * mm, "end": v(1.75, 63.8) * mm});
            skLineSegment(sketch, "E1218", {"start": v(1.75, 63.8) * mm, "end": v(1.73, 63.71) * mm});
            skLineSegment(sketch, "E1219", {"start": v(1.73, 63.71) * mm, "end": v(1.48, 63.6) * mm});
            skLineSegment(sketch, "E1220", {"start": v(1.48, 63.6) * mm, "end": v(0, 63.61) * mm});
            skLineSegment(sketch, "E1221", {"start": v(0, 63.61) * mm, "end": v(-0.24, 63.74) * mm});
            skLineSegment(sketch, "E1222", {"start": v(-0.24, 63.74) * mm, "end": v(-0.26, 63.82) * mm});
            skLineSegment(sketch, "E1223", {"start": v(-0.26, 63.82) * mm, "end": v(-0.28, 63.9) * mm});
            skLineSegment(sketch, "E1224", {"start": v(-0.28, 63.9) * mm, "end": v(-0.3, 63.98) * mm});
            skLineSegment(sketch, "E1225", {"start": v(-0.3, 63.98) * mm, "end": v(-0.32, 64.07) * mm});
            skLineSegment(sketch, "E1226", {"start": v(-0.32, 64.07) * mm, "end": v(-0.35, 64.16) * mm});
            skLineSegment(sketch, "E1227", {"start": v(-0.35, 64.16) * mm, "end": v(-0.37, 64.25) * mm});
            skLineSegment(sketch, "E1228", {"start": v(-0.37, 64.25) * mm, "end": v(-0.4, 64.34) * mm});
            skLineSegment(sketch, "E1229", {"start": v(-0.4, 64.34) * mm, "end": v(-0.42, 64.44) * mm});
            skLineSegment(sketch, "E1230", {"start": v(-0.42, 64.44) * mm, "end": v(-0.45, 64.53) * mm});
            skLineSegment(sketch, "E1231", {"start": v(-0.45, 64.53) * mm, "end": v(-0.48, 64.63) * mm});
            skLineSegment(sketch, "E1232", {"start": v(-0.48, 64.63) * mm, "end": v(-0.5, 64.73) * mm});
            skLineSegment(sketch, "E1233", {"start": v(-0.5, 64.73) * mm, "end": v(-0.54, 64.83) * mm});
            skLineSegment(sketch, "E1234", {"start": v(-0.54, 64.83) * mm, "end": v(-0.57, 64.94) * mm});
            skLineSegment(sketch, "E1235", {"start": v(-0.57, 64.94) * mm, "end": v(-0.64, 65.15) * mm});
            skLineSegment(sketch, "E1236", {"start": v(-0.64, 65.15) * mm, "end": v(-0.7, 65.37) * mm});
            skLineSegment(sketch, "E1237", {"start": v(-0.7, 65.37) * mm, "end": v(-0.75, 65.48) * mm});
            skLineSegment(sketch, "E1238", {"start": v(-0.75, 65.48) * mm, "end": v(-0.79, 65.6) * mm});
            skLineSegment(sketch, "E1239", {"start": v(-0.79, 65.6) * mm, "end": v(-0.83, 65.71) * mm});
            skLineSegment(sketch, "E1240", {"start": v(-0.83, 65.71) * mm, "end": v(-0.87, 65.83) * mm});
            skLineSegment(sketch, "E1241", {"start": v(-0.87, 65.83) * mm, "end": v(-0.92, 65.95) * mm});
            skLineSegment(sketch, "E1242", {"start": v(-0.92, 65.95) * mm, "end": v(-0.96, 66.07) * mm});
            skLineSegment(sketch, "E1243", {"start": v(-0.96, 66.07) * mm, "end": v(-1, 66.2) * mm});
            skLineSegment(sketch, "E1244", {"start": v(-1, 66.2) * mm, "end": v(-1.05, 66.32) * mm});
            skLineSegment(sketch, "E1245", {"start": v(-1.05, 66.32) * mm, "end": v(-1.1, 66.44) * mm});
            skLineSegment(sketch, "E1246", {"start": v(-1.1, 66.44) * mm, "end": v(-1.16, 66.57) * mm});
            skLineSegment(sketch, "E1247", {"start": v(-1.16, 66.57) * mm, "end": v(-1.2, 66.7) * mm});
            skLineSegment(sketch, "E1248", {"start": v(-1.2, 66.7) * mm, "end": v(-1.26, 66.83) * mm});
            skLineSegment(sketch, "E1249", {"start": v(-1.26, 66.83) * mm, "end": v(-1.32, 66.96) * mm});
            skLineSegment(sketch, "E1250", {"start": v(-1.32, 66.96) * mm, "end": v(-1.38, 67.1) * mm});
            skLineSegment(sketch, "E1251", {"start": v(-1.38, 67.1) * mm, "end": v(-1.44, 67.24) * mm});
            skLineSegment(sketch, "E1252", {"start": v(-1.44, 67.24) * mm, "end": v(-1.5, 67.37) * mm});
            skLineSegment(sketch, "E1253", {"start": v(-1.5, 67.37) * mm, "end": v(-1.56, 67.51) * mm});
            skLineSegment(sketch, "E1254", {"start": v(-1.56, 67.51) * mm, "end": v(-1.69, 67.8) * mm});
            skLineSegment(sketch, "E1255", {"start": v(-1.69, 67.8) * mm, "end": v(-1.76, 67.94) * mm});
            skLineSegment(sketch, "E1256", {"start": v(-1.76, 67.94) * mm, "end": v(-1.83, 68.08) * mm});
            skLineSegment(sketch, "E1257", {"start": v(-1.83, 68.08) * mm, "end": v(-1.9, 68.23) * mm});
            skLineSegment(sketch, "E1258", {"start": v(-1.9, 68.23) * mm, "end": v(-1.97, 68.32) * mm});
            skLineSegment(sketch, "E1259", {"start": v(-1.97, 68.32) * mm, "end": v(-3.6, 68.26) * mm});
            skLineSegment(sketch, "E1260", {"start": v(-3.6, 68.26) * mm, "end": v(-3.66, 68.16) * mm});
            skLineSegment(sketch, "E1261", {"start": v(-3.66, 68.16) * mm, "end": v(-3.77, 67.86) * mm});
            skLineSegment(sketch, "E1262", {"start": v(-3.77, 67.86) * mm, "end": v(-3.83, 67.7) * mm});
            skLineSegment(sketch, "E1263", {"start": v(-3.83, 67.7) * mm, "end": v(-3.88, 67.56) * mm});
            skLineSegment(sketch, "E1264", {"start": v(-3.88, 67.56) * mm, "end": v(-3.94, 67.42) * mm});
            skLineSegment(sketch, "E1265", {"start": v(-3.94, 67.42) * mm, "end": v(-3.99, 67.27) * mm});
            skLineSegment(sketch, "E1266", {"start": v(-3.99, 67.27) * mm, "end": v(-4.04, 67.13) * mm});
            skLineSegment(sketch, "E1267", {"start": v(-4.04, 67.13) * mm, "end": v(-4.08, 66.99) * mm});
            skLineSegment(sketch, "E1268", {"start": v(-4.08, 66.99) * mm, "end": v(-4.13, 66.85) * mm});
            skLineSegment(sketch, "E1269", {"start": v(-4.13, 66.85) * mm, "end": v(-4.18, 66.71) * mm});
            skLineSegment(sketch, "E1270", {"start": v(-4.18, 66.71) * mm, "end": v(-4.22, 66.58) * mm});
            skLineSegment(sketch, "E1271", {"start": v(-4.22, 66.58) * mm, "end": v(-4.26, 66.44) * mm});
            skLineSegment(sketch, "E1272", {"start": v(-4.26, 66.44) * mm, "end": v(-4.3, 66.31) * mm});
            skLineSegment(sketch, "E1273", {"start": v(-4.3, 66.31) * mm, "end": v(-4.34, 66.18) * mm});
            skLineSegment(sketch, "E1274", {"start": v(-4.34, 66.18) * mm, "end": v(-4.38, 66.05) * mm});
            skLineSegment(sketch, "E1275", {"start": v(-4.38, 66.05) * mm, "end": v(-4.42, 65.93) * mm});
            skLineSegment(sketch, "E1276", {"start": v(-4.42, 65.93) * mm, "end": v(-4.45, 65.8) * mm});
            skLineSegment(sketch, "E1277", {"start": v(-4.45, 65.8) * mm, "end": v(-4.49, 65.68) * mm});
            skLineSegment(sketch, "E1278", {"start": v(-4.49, 65.68) * mm, "end": v(-4.52, 65.56) * mm});
            skLineSegment(sketch, "E1279", {"start": v(-4.52, 65.56) * mm, "end": v(-4.55, 65.44) * mm});
            skLineSegment(sketch, "E1280", {"start": v(-4.55, 65.44) * mm, "end": v(-4.58, 65.32) * mm});
            skLineSegment(sketch, "E1281", {"start": v(-4.58, 65.32) * mm, "end": v(-4.6, 65.21) * mm});
            skLineSegment(sketch, "E1282", {"start": v(-4.6, 65.21) * mm, "end": v(-4.64, 65.1) * mm});
            skLineSegment(sketch, "E1283", {"start": v(-4.64, 65.1) * mm, "end": v(-4.66, 64.98) * mm});
            skLineSegment(sketch, "E1284", {"start": v(-4.66, 64.98) * mm, "end": v(-4.69, 64.88) * mm});
            skLineSegment(sketch, "E1285", {"start": v(-4.69, 64.88) * mm, "end": v(-4.71, 64.77) * mm});
            skLineSegment(sketch, "E1286", {"start": v(-4.71, 64.77) * mm, "end": v(-4.74, 64.66) * mm});
            skLineSegment(sketch, "E1287", {"start": v(-4.74, 64.66) * mm, "end": v(-4.76, 64.56) * mm});
            skLineSegment(sketch, "E1288", {"start": v(-4.76, 64.56) * mm, "end": v(-4.78, 64.46) * mm});
            skLineSegment(sketch, "E1289", {"start": v(-4.78, 64.46) * mm, "end": v(-4.8, 64.36) * mm});
            skLineSegment(sketch, "E1290", {"start": v(-4.8, 64.36) * mm, "end": v(-4.82, 64.26) * mm});
            skLineSegment(sketch, "E1291", {"start": v(-4.82, 64.26) * mm, "end": v(-4.84, 64.16) * mm});
            skLineSegment(sketch, "E1292", {"start": v(-4.84, 64.16) * mm, "end": v(-4.86, 64.07) * mm});
            skLineSegment(sketch, "E1293", {"start": v(-4.86, 64.07) * mm, "end": v(-4.87, 63.98) * mm});
            skLineSegment(sketch, "E1294", {"start": v(-4.87, 63.98) * mm, "end": v(-4.89, 63.89) * mm});
            skLineSegment(sketch, "E1295", {"start": v(-4.89, 63.89) * mm, "end": v(-4.9, 63.8) * mm});
            skLineSegment(sketch, "E1296", {"start": v(-4.9, 63.8) * mm, "end": v(-4.92, 63.71) * mm});
            skLineSegment(sketch, "E1297", {"start": v(-4.92, 63.71) * mm, "end": v(-4.93, 63.63) * mm});
            skLineSegment(sketch, "E1298", {"start": v(-4.93, 63.63) * mm, "end": v(-4.94, 63.54) * mm});
            skLineSegment(sketch, "E1299", {"start": v(-4.94, 63.54) * mm, "end": v(-5.17, 63.4) * mm});
            skLineSegment(sketch, "E1300", {"start": v(-5.17, 63.4) * mm, "end": v(-6.65, 63.26) * mm});
            skLineSegment(sketch, "E1301", {"start": v(-6.65, 63.26) * mm, "end": v(-6.9, 63.36) * mm});
            skLineSegment(sketch, "E1302", {"start": v(-6.9, 63.36) * mm, "end": v(-6.93, 63.44) * mm});
            skLineSegment(sketch, "E1303", {"start": v(-6.93, 63.44) * mm, "end": v(-6.96, 63.52) * mm});
            skLineSegment(sketch, "E1304", {"start": v(-6.96, 63.52) * mm, "end": v(-6.99, 63.6) * mm});
            skLineSegment(sketch, "E1305", {"start": v(-6.99, 63.6) * mm, "end": v(-7.02, 63.69) * mm});
            skLineSegment(sketch, "E1306", {"start": v(-7.02, 63.69) * mm, "end": v(-7.05, 63.77) * mm});
            skLineSegment(sketch, "E1307", {"start": v(-7.05, 63.77) * mm, "end": v(-7.08, 63.86) * mm});
            skLineSegment(sketch, "E1308", {"start": v(-7.08, 63.86) * mm, "end": v(-7.12, 63.95) * mm});
            skLineSegment(sketch, "E1309", {"start": v(-7.12, 63.95) * mm, "end": v(-7.15, 64.04) * mm});
            skLineSegment(sketch, "E1310", {"start": v(-7.15, 64.04) * mm, "end": v(-7.2, 64.13) * mm});
            skLineSegment(sketch, "E1311", {"start": v(-7.2, 64.13) * mm, "end": v(-7.23, 64.23) * mm});
            skLineSegment(sketch, "E1312", {"start": v(-7.23, 64.23) * mm, "end": v(-7.27, 64.32) * mm});
            skLineSegment(sketch, "E1313", {"start": v(-7.27, 64.32) * mm, "end": v(-7.31, 64.42) * mm});
            skLineSegment(sketch, "E1314", {"start": v(-7.31, 64.42) * mm, "end": v(-7.35, 64.52) * mm});
            skLineSegment(sketch, "E1315", {"start": v(-7.35, 64.52) * mm, "end": v(-7.4, 64.62) * mm});
            skLineSegment(sketch, "E1316", {"start": v(-7.4, 64.62) * mm, "end": v(-7.44, 64.73) * mm});
            skLineSegment(sketch, "E1317", {"start": v(-7.44, 64.73) * mm, "end": v(-7.49, 64.83) * mm});
            skLineSegment(sketch, "E1318", {"start": v(-7.49, 64.83) * mm, "end": v(-7.54, 64.94) * mm});
            skLineSegment(sketch, "E1319", {"start": v(-7.54, 64.94) * mm, "end": v(-7.59, 65.04) * mm});
            skLineSegment(sketch, "E1320", {"start": v(-7.59, 65.04) * mm, "end": v(-7.64, 65.15) * mm});
            skLineSegment(sketch, "E1321", {"start": v(-7.64, 65.15) * mm, "end": v(-7.7, 65.27) * mm});
            skLineSegment(sketch, "E1322", {"start": v(-7.7, 65.27) * mm, "end": v(-7.75, 65.38) * mm});
            skLineSegment(sketch, "E1323", {"start": v(-7.75, 65.38) * mm, "end": v(-7.8, 65.5) * mm});
            skLineSegment(sketch, "E1324", {"start": v(-7.8, 65.5) * mm, "end": v(-7.86, 65.6) * mm});
            skLineSegment(sketch, "E1325", {"start": v(-7.86, 65.6) * mm, "end": v(-7.92, 65.72) * mm});
            skLineSegment(sketch, "E1326", {"start": v(-7.92, 65.72) * mm, "end": v(-8.04, 65.96) * mm});
            skLineSegment(sketch, "E1327", {"start": v(-8.04, 65.96) * mm, "end": v(-8.1, 66.09) * mm});
            skLineSegment(sketch, "E1328", {"start": v(-8.1, 66.09) * mm, "end": v(-8.17, 66.2) * mm});
            skLineSegment(sketch, "E1329", {"start": v(-8.17, 66.2) * mm, "end": v(-8.24, 66.33) * mm});
            skLineSegment(sketch, "E1330", {"start": v(-8.24, 66.33) * mm, "end": v(-8.31, 66.46) * mm});
            skLineSegment(sketch, "E1331", {"start": v(-8.31, 66.46) * mm, "end": v(-8.38, 66.59) * mm});
            skLineSegment(sketch, "E1332", {"start": v(-8.38, 66.59) * mm, "end": v(-8.46, 66.72) * mm});
            skLineSegment(sketch, "E1333", {"start": v(-8.46, 66.72) * mm, "end": v(-8.53, 66.85) * mm});
            skLineSegment(sketch, "E1334", {"start": v(-8.53, 66.85) * mm, "end": v(-8.6, 66.98) * mm});
            skLineSegment(sketch, "E1335", {"start": v(-8.6, 66.98) * mm, "end": v(-8.69, 67.11) * mm});
            skLineSegment(sketch, "E1336", {"start": v(-8.69, 67.11) * mm, "end": v(-8.77, 67.25) * mm});
            skLineSegment(sketch, "E1337", {"start": v(-8.77, 67.25) * mm, "end": v(-8.85, 67.38) * mm});
            skLineSegment(sketch, "E1338", {"start": v(-8.85, 67.38) * mm, "end": v(-8.93, 67.52) * mm});
            skLineSegment(sketch, "E1339", {"start": v(-8.93, 67.52) * mm, "end": v(-9.02, 67.66) * mm});
            skLineSegment(sketch, "E1340", {"start": v(-9.02, 67.66) * mm, "end": v(-9.1, 67.74) * mm});
            skLineSegment(sketch, "E1341", {"start": v(-9.1, 67.74) * mm, "end": v(-10.71, 67.5) * mm});
            skLineSegment(sketch, "E1342", {"start": v(-10.71, 67.5) * mm, "end": v(-10.76, 67.4) * mm});
            skLineSegment(sketch, "E1343", {"start": v(-10.76, 67.4) * mm, "end": v(-10.8, 67.25) * mm});
            skLineSegment(sketch, "E1344", {"start": v(-10.8, 67.25) * mm, "end": v(-10.85, 67.09) * mm});
            skLineSegment(sketch, "E1345", {"start": v(-10.85, 67.09) * mm, "end": v(-10.89, 66.94) * mm});
            skLineSegment(sketch, "E1346", {"start": v(-10.89, 66.94) * mm, "end": v(-10.93, 66.78) * mm});
            skLineSegment(sketch, "E1347", {"start": v(-10.93, 66.78) * mm, "end": v(-10.96, 66.64) * mm});
            skLineSegment(sketch, "E1348", {"start": v(-10.96, 66.64) * mm, "end": v(-11, 66.49) * mm});
            skLineSegment(sketch, "E1349", {"start": v(-11, 66.49) * mm, "end": v(-11.03, 66.34) * mm});
            skLineSegment(sketch, "E1350", {"start": v(-11.03, 66.34) * mm, "end": v(-11.06, 66.2) * mm});
            skLineSegment(sketch, "E1351", {"start": v(-11.06, 66.2) * mm, "end": v(-11.1, 66.05) * mm});
            skLineSegment(sketch, "E1352", {"start": v(-11.1, 66.05) * mm, "end": v(-11.13, 65.91) * mm});
            skLineSegment(sketch, "E1353", {"start": v(-11.13, 65.91) * mm, "end": v(-11.16, 65.77) * mm});
            skLineSegment(sketch, "E1354", {"start": v(-11.16, 65.77) * mm, "end": v(-11.18, 65.64) * mm});
            skLineSegment(sketch, "E1355", {"start": v(-11.18, 65.64) * mm, "end": v(-11.21, 65.5) * mm});
            skLineSegment(sketch, "E1356", {"start": v(-11.21, 65.5) * mm, "end": v(-11.24, 65.37) * mm});
            skLineSegment(sketch, "E1357", {"start": v(-11.24, 65.37) * mm, "end": v(-11.26, 65.23) * mm});
            skLineSegment(sketch, "E1358", {"start": v(-11.26, 65.23) * mm, "end": v(-11.28, 65.1) * mm});
            skLineSegment(sketch, "E1359", {"start": v(-11.28, 65.1) * mm, "end": v(-11.3, 64.98) * mm});
            skLineSegment(sketch, "E1360", {"start": v(-11.3, 64.98) * mm, "end": v(-11.33, 64.85) * mm});
            skLineSegment(sketch, "E1361", {"start": v(-11.33, 64.85) * mm, "end": v(-11.35, 64.73) * mm});
            skLineSegment(sketch, "E1362", {"start": v(-11.35, 64.73) * mm, "end": v(-11.37, 64.6) * mm});
            skLineSegment(sketch, "E1363", {"start": v(-11.37, 64.6) * mm, "end": v(-11.38, 64.49) * mm});
            skLineSegment(sketch, "E1364", {"start": v(-11.38, 64.49) * mm, "end": v(-11.4, 64.37) * mm});
            skLineSegment(sketch, "E1365", {"start": v(-11.4, 64.37) * mm, "end": v(-11.42, 64.26) * mm});
            skLineSegment(sketch, "E1366", {"start": v(-11.42, 64.26) * mm, "end": v(-11.43, 64.14) * mm});
            skLineSegment(sketch, "E1367", {"start": v(-11.43, 64.14) * mm, "end": v(-11.44, 64.03) * mm});
            skLineSegment(sketch, "E1368", {"start": v(-11.44, 64.03) * mm, "end": v(-11.46, 63.92) * mm});
            skLineSegment(sketch, "E1369", {"start": v(-11.46, 63.92) * mm, "end": v(-11.47, 63.81) * mm});
            skLineSegment(sketch, "E1370", {"start": v(-11.47, 63.81) * mm, "end": v(-11.48, 63.7) * mm});
            skLineSegment(sketch, "E1371", {"start": v(-11.48, 63.7) * mm, "end": v(-11.5, 63.6) * mm});
            skLineSegment(sketch, "E1372", {"start": v(-11.5, 63.6) * mm, "end": v(-11.5, 63.5) * mm});
            skLineSegment(sketch, "E1373", {"start": v(-11.5, 63.5) * mm, "end": v(-11.51, 63.4) * mm});
            skLineSegment(sketch, "E1374", {"start": v(-11.51, 63.4) * mm, "end": v(-11.52, 63.3) * mm});
            skLineSegment(sketch, "E1375", {"start": v(-11.52, 63.3) * mm, "end": v(-11.53, 63.2) * mm});
            skLineSegment(sketch, "E1376", {"start": v(-11.53, 63.2) * mm, "end": v(-11.53, 63.12) * mm});
            skLineSegment(sketch, "E1377", {"start": v(-11.53, 63.12) * mm, "end": v(-11.54, 63.02) * mm});
            skLineSegment(sketch, "E1378", {"start": v(-11.54, 63.02) * mm, "end": v(-11.55, 62.93) * mm});
            skLineSegment(sketch, "E1379", {"start": v(-11.55, 62.93) * mm, "end": v(-11.55, 62.85) * mm});
            skLineSegment(sketch, "E1380", {"start": v(-11.55, 62.85) * mm, "end": v(-11.55, 62.76) * mm});
            skLineSegment(sketch, "E1381", {"start": v(-11.55, 62.76) * mm, "end": v(-11.56, 62.68) * mm});
            skLineSegment(sketch, "E1382", {"start": v(-11.56, 62.68) * mm, "end": v(-11.77, 62.51) * mm});
            skLineSegment(sketch, "E1383", {"start": v(-11.77, 62.51) * mm, "end": v(-13.22, 62.22) * mm});
            skLineSegment(sketch, "E1384", {"start": v(-13.22, 62.22) * mm, "end": v(-13.49, 62.3) * mm});
            skLineSegment(sketch, "E1385", {"start": v(-13.49, 62.3) * mm, "end": v(-13.52, 62.37) * mm});
            skLineSegment(sketch, "E1386", {"start": v(-13.52, 62.37) * mm, "end": v(-13.56, 62.45) * mm});
            skLineSegment(sketch, "E1387", {"start": v(-13.56, 62.45) * mm, "end": v(-13.6, 62.52) * mm});
            skLineSegment(sketch, "E1388", {"start": v(-13.6, 62.52) * mm, "end": v(-13.64, 62.6) * mm});
            skLineSegment(sketch, "E1389", {"start": v(-13.64, 62.6) * mm, "end": v(-13.68, 62.69) * mm});
            skLineSegment(sketch, "E1390", {"start": v(-13.68, 62.69) * mm, "end": v(-13.72, 62.77) * mm});
            skLineSegment(sketch, "E1391", {"start": v(-13.72, 62.77) * mm, "end": v(-13.76, 62.86) * mm});
            skLineSegment(sketch, "E1392", {"start": v(-13.76, 62.86) * mm, "end": v(-13.8, 62.94) * mm});
            skLineSegment(sketch, "E1393", {"start": v(-13.8, 62.94) * mm, "end": v(-13.85, 63.03) * mm});
            skLineSegment(sketch, "E1394", {"start": v(-13.85, 63.03) * mm, "end": v(-13.9, 63.12) * mm});
            skLineSegment(sketch, "E1395", {"start": v(-13.9, 63.12) * mm, "end": v(-13.95, 63.21) * mm});
            skLineSegment(sketch, "E1396", {"start": v(-13.95, 63.21) * mm, "end": v(-14, 63.3) * mm});
            skLineSegment(sketch, "E1397", {"start": v(-14, 63.3) * mm, "end": v(-14.06, 63.4) * mm});
            skLineSegment(sketch, "E1398", {"start": v(-14.06, 63.4) * mm, "end": v(-14.11, 63.5) * mm});
            skLineSegment(sketch, "E1399", {"start": v(-14.11, 63.5) * mm, "end": v(-14.17, 63.6) * mm});
            skLineSegment(sketch, "E1400", {"start": v(-14.17, 63.6) * mm, "end": v(-14.23, 63.7) * mm});
            skLineSegment(sketch, "E1401", {"start": v(-14.23, 63.7) * mm, "end": v(-14.28, 63.8) * mm});
            skLineSegment(sketch, "E1402", {"start": v(-14.28, 63.8) * mm, "end": v(-14.35, 63.9) * mm});
            skLineSegment(sketch, "E1403", {"start": v(-14.35, 63.9) * mm, "end": v(-14.4, 64) * mm});
            skLineSegment(sketch, "E1404", {"start": v(-14.4, 64) * mm, "end": v(-14.47, 64.1) * mm});
            skLineSegment(sketch, "E1405", {"start": v(-14.47, 64.1) * mm, "end": v(-14.54, 64.2) * mm});
            skLineSegment(sketch, "E1406", {"start": v(-14.54, 64.2) * mm, "end": v(-14.6, 64.32) * mm});
            skLineSegment(sketch, "E1407", {"start": v(-14.6, 64.32) * mm, "end": v(-14.67, 64.43) * mm});
            skLineSegment(sketch, "E1408", {"start": v(-14.67, 64.43) * mm, "end": v(-14.75, 64.54) * mm});
            skLineSegment(sketch, "E1409", {"start": v(-14.75, 64.54) * mm, "end": v(-14.82, 64.65) * mm});
            skLineSegment(sketch, "E1410", {"start": v(-14.82, 64.65) * mm, "end": v(-14.9, 64.76) * mm});
            skLineSegment(sketch, "E1411", {"start": v(-14.9, 64.76) * mm, "end": v(-14.97, 64.88) * mm});
            skLineSegment(sketch, "E1412", {"start": v(-14.97, 64.88) * mm, "end": v(-15.05, 65) * mm});
            skLineSegment(sketch, "E1413", {"start": v(-15.05, 65) * mm, "end": v(-15.21, 65.23) * mm});
            skLineSegment(sketch, "E1414", {"start": v(-15.21, 65.23) * mm, "end": v(-15.3, 65.35) * mm});
            skLineSegment(sketch, "E1415", {"start": v(-15.3, 65.35) * mm, "end": v(-15.38, 65.47) * mm});
            skLineSegment(sketch, "E1416", {"start": v(-15.38, 65.47) * mm, "end": v(-15.47, 65.59) * mm});
            skLineSegment(sketch, "E1417", {"start": v(-15.47, 65.59) * mm, "end": v(-15.56, 65.71) * mm});
            skLineSegment(sketch, "E1418", {"start": v(-15.56, 65.71) * mm, "end": v(-15.65, 65.84) * mm});
            skLineSegment(sketch, "E1419", {"start": v(-15.65, 65.84) * mm, "end": v(-15.75, 65.96) * mm});
            skLineSegment(sketch, "E1420", {"start": v(-15.75, 65.96) * mm, "end": v(-15.84, 66.09) * mm});
            skLineSegment(sketch, "E1421", {"start": v(-15.84, 66.09) * mm, "end": v(-15.94, 66.22) * mm});
            skLineSegment(sketch, "E1422", {"start": v(-15.94, 66.22) * mm, "end": v(-16.04, 66.35) * mm});
            skLineSegment(sketch, "E1423", {"start": v(-16.04, 66.35) * mm, "end": v(-16.13, 66.42) * mm});
            skLineSegment(sketch, "E1424", {"start": v(-16.13, 66.42) * mm, "end": v(-17.7, 66.02) * mm});
            skLineSegment(sketch, "E1425", {"start": v(-17.7, 66.02) * mm, "end": v(-17.75, 65.9) * mm});
            skLineSegment(sketch, "E1426", {"start": v(-17.75, 65.9) * mm, "end": v(-17.78, 65.75) * mm});
            skLineSegment(sketch, "E1427", {"start": v(-17.78, 65.75) * mm, "end": v(-17.8, 65.59) * mm});
            skLineSegment(sketch, "E1428", {"start": v(-17.8, 65.59) * mm, "end": v(-17.82, 65.43) * mm});
            skLineSegment(sketch, "E1429", {"start": v(-17.82, 65.43) * mm, "end": v(-17.85, 65.28) * mm});
            skLineSegment(sketch, "E1430", {"start": v(-17.85, 65.28) * mm, "end": v(-17.87, 65.12) * mm});
            skLineSegment(sketch, "E1431", {"start": v(-17.87, 65.12) * mm, "end": v(-17.89, 64.97) * mm});
            skLineSegment(sketch, "E1432", {"start": v(-17.89, 64.97) * mm, "end": v(-17.9, 64.82) * mm});
            skLineSegment(sketch, "E1433", {"start": v(-17.9, 64.82) * mm, "end": v(-17.92, 64.68) * mm});
            skLineSegment(sketch, "E1434", {"start": v(-17.92, 64.68) * mm, "end": v(-17.94, 64.53) * mm});
            skLineSegment(sketch, "E1435", {"start": v(-17.94, 64.53) * mm, "end": v(-17.96, 64.39) * mm});
            skLineSegment(sketch, "E1436", {"start": v(-17.96, 64.39) * mm, "end": v(-17.97, 64.25) * mm});
            skLineSegment(sketch, "E1437", {"start": v(-17.97, 64.25) * mm, "end": v(-17.98, 64.1) * mm});
            skLineSegment(sketch, "E1438", {"start": v(-17.98, 64.1) * mm, "end": v(-18, 63.97) * mm});
            skLineSegment(sketch, "E1439", {"start": v(-18, 63.97) * mm, "end": v(-18, 63.83) * mm});
            skLineSegment(sketch, "E1440", {"start": v(-18, 63.83) * mm, "end": v(-18.02, 63.7) * mm});
            skLineSegment(sketch, "E1441", {"start": v(-18.02, 63.7) * mm, "end": v(-18.03, 63.57) * mm});
            skLineSegment(sketch, "E1442", {"start": v(-18.03, 63.57) * mm, "end": v(-18.04, 63.44) * mm});
            skLineSegment(sketch, "E1443", {"start": v(-18.04, 63.44) * mm, "end": v(-18.04, 63.31) * mm});
            skLineSegment(sketch, "E1444", {"start": v(-18.04, 63.31) * mm, "end": v(-18.05, 63.19) * mm});
            skLineSegment(sketch, "E1445", {"start": v(-18.05, 63.19) * mm, "end": v(-18.06, 63.07) * mm});
            skLineSegment(sketch, "E1446", {"start": v(-18.06, 63.07) * mm, "end": v(-18.06, 62.94) * mm});
            skLineSegment(sketch, "E1447", {"start": v(-18.06, 62.94) * mm, "end": v(-18.07, 62.83) * mm});
            skLineSegment(sketch, "E1448", {"start": v(-18.07, 62.83) * mm, "end": v(-18.07, 62.7) * mm});
            skLineSegment(sketch, "E1449", {"start": v(-18.07, 62.7) * mm, "end": v(-18.07, 62.6) * mm});
            skLineSegment(sketch, "E1450", {"start": v(-18.07, 62.6) * mm, "end": v(-18.08, 62.48) * mm});
            skLineSegment(sketch, "E1451", {"start": v(-18.08, 62.48) * mm, "end": v(-18.08, 62.37) * mm});
            skLineSegment(sketch, "E1452", {"start": v(-18.08, 62.37) * mm, "end": v(-18.08, 62.26) * mm});
            skLineSegment(sketch, "E1453", {"start": v(-18.08, 62.26) * mm, "end": v(-18.08, 62.05) * mm});
            skLineSegment(sketch, "E1454", {"start": v(-18.08, 62.05) * mm, "end": v(-18.08, 61.95) * mm});
            skLineSegment(sketch, "E1455", {"start": v(-18.08, 61.95) * mm, "end": v(-18.08, 61.85) * mm});
            skLineSegment(sketch, "E1456", {"start": v(-18.08, 61.85) * mm, "end": v(-18.07, 61.75) * mm});
            skLineSegment(sketch, "E1457", {"start": v(-18.07, 61.75) * mm, "end": v(-18.07, 61.66) * mm});
            skLineSegment(sketch, "E1458", {"start": v(-18.07, 61.66) * mm, "end": v(-18.07, 61.56) * mm});
            skLineSegment(sketch, "E1459", {"start": v(-18.07, 61.56) * mm, "end": v(-18.06, 61.47) * mm});
            skLineSegment(sketch, "E1460", {"start": v(-18.06, 61.47) * mm, "end": v(-18.06, 61.38) * mm});
            skLineSegment(sketch, "E1461", {"start": v(-18.06, 61.38) * mm, "end": v(-18.06, 61.3) * mm});
            skLineSegment(sketch, "E1462", {"start": v(-18.06, 61.3) * mm, "end": v(-18.05, 61.21) * mm});
            skLineSegment(sketch, "E1463", {"start": v(-18.05, 61.21) * mm, "end": v(-18.05, 61.13) * mm});
            skLineSegment(sketch, "E1464", {"start": v(-18.05, 61.13) * mm, "end": v(-18.24, 60.94) * mm});
            skLineSegment(sketch, "E1465", {"start": v(-18.24, 60.94) * mm, "end": v(-19.66, 60.5) * mm});
            skLineSegment(sketch, "E1466", {"start": v(-19.66, 60.5) * mm, "end": v(-19.92, 60.54) * mm});
            skLineSegment(sketch, "E1467", {"start": v(-19.92, 60.54) * mm, "end": v(-19.97, 60.61) * mm});
            skLineSegment(sketch, "E1468", {"start": v(-19.97, 60.61) * mm, "end": v(-20.01, 60.69) * mm});
            skLineSegment(sketch, "E1469", {"start": v(-20.01, 60.69) * mm, "end": v(-20.06, 60.76) * mm});
            skLineSegment(sketch, "E1470", {"start": v(-20.06, 60.76) * mm, "end": v(-20.1, 60.84) * mm});
            skLineSegment(sketch, "E1471", {"start": v(-20.1, 60.84) * mm, "end": v(-20.16, 60.91) * mm});
            skLineSegment(sketch, "E1472", {"start": v(-20.16, 60.91) * mm, "end": v(-20.2, 61) * mm});
            skLineSegment(sketch, "E1473", {"start": v(-20.2, 61) * mm, "end": v(-20.26, 61.07) * mm});
            skLineSegment(sketch, "E1474", {"start": v(-20.26, 61.07) * mm, "end": v(-20.31, 61.15) * mm});
            skLineSegment(sketch, "E1475", {"start": v(-20.31, 61.15) * mm, "end": v(-20.37, 61.24) * mm});
            skLineSegment(sketch, "E1476", {"start": v(-20.37, 61.24) * mm, "end": v(-20.43, 61.32) * mm});
            skLineSegment(sketch, "E1477", {"start": v(-20.43, 61.32) * mm, "end": v(-20.48, 61.4) * mm});
            skLineSegment(sketch, "E1478", {"start": v(-20.48, 61.4) * mm, "end": v(-20.54, 61.5) * mm});
            skLineSegment(sketch, "E1479", {"start": v(-20.54, 61.5) * mm, "end": v(-20.6, 61.58) * mm});
            skLineSegment(sketch, "E1480", {"start": v(-20.6, 61.58) * mm, "end": v(-20.67, 61.67) * mm});
            skLineSegment(sketch, "E1481", {"start": v(-20.67, 61.67) * mm, "end": v(-20.74, 61.76) * mm});
            skLineSegment(sketch, "E1482", {"start": v(-20.74, 61.76) * mm, "end": v(-20.8, 61.86) * mm});
            skLineSegment(sketch, "E1483", {"start": v(-20.8, 61.86) * mm, "end": v(-20.87, 61.95) * mm});
            skLineSegment(sketch, "E1484", {"start": v(-20.87, 61.95) * mm, "end": v(-20.94, 62.04) * mm});
            skLineSegment(sketch, "E1485", {"start": v(-20.94, 62.04) * mm, "end": v(-21.02, 62.14) * mm});
            skLineSegment(sketch, "E1486", {"start": v(-21.02, 62.14) * mm, "end": v(-21.1, 62.24) * mm});
            skLineSegment(sketch, "E1487", {"start": v(-21.1, 62.24) * mm, "end": v(-21.17, 62.34) * mm});
            skLineSegment(sketch, "E1488", {"start": v(-21.17, 62.34) * mm, "end": v(-21.25, 62.44) * mm});
            skLineSegment(sketch, "E1489", {"start": v(-21.25, 62.44) * mm, "end": v(-21.33, 62.54) * mm});
            skLineSegment(sketch, "E1490", {"start": v(-21.33, 62.54) * mm, "end": v(-21.41, 62.64) * mm});
            skLineSegment(sketch, "E1491", {"start": v(-21.41, 62.64) * mm, "end": v(-21.5, 62.74) * mm});
            skLineSegment(sketch, "E1492", {"start": v(-21.5, 62.74) * mm, "end": v(-21.58, 62.85) * mm});
            skLineSegment(sketch, "E1493", {"start": v(-21.58, 62.85) * mm, "end": v(-21.67, 62.96) * mm});
            skLineSegment(sketch, "E1494", {"start": v(-21.67, 62.96) * mm, "end": v(-21.76, 63.06) * mm});
            skLineSegment(sketch, "E1495", {"start": v(-21.76, 63.06) * mm, "end": v(-21.85, 63.17) * mm});
            skLineSegment(sketch, "E1496", {"start": v(-21.85, 63.17) * mm, "end": v(-21.95, 63.28) * mm});
            skLineSegment(sketch, "E1497", {"start": v(-21.95, 63.28) * mm, "end": v(-22.04, 63.39) * mm});
            skLineSegment(sketch, "E1498", {"start": v(-22.04, 63.39) * mm, "end": v(-22.14, 63.5) * mm});
            skLineSegment(sketch, "E1499", {"start": v(-22.14, 63.5) * mm, "end": v(-22.24, 63.61) * mm});
            skLineSegment(sketch, "E1500", {"start": v(-22.24, 63.61) * mm, "end": v(-22.35, 63.73) * mm});
            skLineSegment(sketch, "E1501", {"start": v(-22.35, 63.73) * mm, "end": v(-22.45, 63.84) * mm});
            skLineSegment(sketch, "E1502", {"start": v(-22.45, 63.84) * mm, "end": v(-22.56, 63.95) * mm});
            skLineSegment(sketch, "E1503", {"start": v(-22.56, 63.95) * mm, "end": v(-22.66, 64.07) * mm});
            skLineSegment(sketch, "E1504", {"start": v(-22.66, 64.07) * mm, "end": v(-22.78, 64.19) * mm});
            skLineSegment(sketch, "E1505", {"start": v(-22.78, 64.19) * mm, "end": v(-22.89, 64.3) * mm});
            skLineSegment(sketch, "E1506", {"start": v(-22.89, 64.3) * mm, "end": v(-22.98, 64.37) * mm});
            skLineSegment(sketch, "E1507", {"start": v(-22.98, 64.37) * mm, "end": v(-24.51, 63.8) * mm});
            skLineSegment(sketch, "E1508", {"start": v(-24.51, 63.8) * mm, "end": v(-24.54, 63.7) * mm});
            skLineSegment(sketch, "E1509", {"start": v(-24.54, 63.7) * mm, "end": v(-24.55, 63.53) * mm});
            skLineSegment(sketch, "E1510", {"start": v(-24.55, 63.53) * mm, "end": v(-24.56, 63.37) * mm});
            skLineSegment(sketch, "E1511", {"start": v(-24.56, 63.37) * mm, "end": v(-24.57, 63.21) * mm});
            skLineSegment(sketch, "E1512", {"start": v(-24.57, 63.21) * mm, "end": v(-24.57, 63.05) * mm});
            skLineSegment(sketch, "E1513", {"start": v(-24.57, 63.05) * mm, "end": v(-24.58, 62.9) * mm});
            skLineSegment(sketch, "E1514", {"start": v(-24.58, 62.9) * mm, "end": v(-24.58, 62.75) * mm});
            skLineSegment(sketch, "E1515", {"start": v(-24.58, 62.75) * mm, "end": v(-24.58, 62.6) * mm});
            skLineSegment(sketch, "E1516", {"start": v(-24.58, 62.6) * mm, "end": v(-24.59, 62.45) * mm});
            skLineSegment(sketch, "E1517", {"start": v(-24.59, 62.45) * mm, "end": v(-24.59, 62.3) * mm});
            skLineSegment(sketch, "E1518", {"start": v(-24.59, 62.3) * mm, "end": v(-24.59, 62.02) * mm});
            skLineSegment(sketch, "E1519", {"start": v(-24.59, 62.02) * mm, "end": v(-24.59, 61.88) * mm});
            skLineSegment(sketch, "E1520", {"start": v(-24.59, 61.88) * mm, "end": v(-24.58, 61.74) * mm});
            skLineSegment(sketch, "E1521", {"start": v(-24.58, 61.74) * mm, "end": v(-24.58, 61.6) * mm});
            skLineSegment(sketch, "E1522", {"start": v(-24.58, 61.6) * mm, "end": v(-24.58, 61.47) * mm});
            skLineSegment(sketch, "E1523", {"start": v(-24.58, 61.47) * mm, "end": v(-24.57, 61.34) * mm});
            skLineSegment(sketch, "E1524", {"start": v(-24.57, 61.34) * mm, "end": v(-24.57, 61.2) * mm});
            skLineSegment(sketch, "E1525", {"start": v(-24.57, 61.2) * mm, "end": v(-24.56, 61.08) * mm});
            skLineSegment(sketch, "E1526", {"start": v(-24.56, 61.08) * mm, "end": v(-24.56, 60.96) * mm});
            skLineSegment(sketch, "E1527", {"start": v(-24.56, 60.96) * mm, "end": v(-24.55, 60.83) * mm});
            skLineSegment(sketch, "E1528", {"start": v(-24.55, 60.83) * mm, "end": v(-24.54, 60.71) * mm});
            skLineSegment(sketch, "E1529", {"start": v(-24.54, 60.71) * mm, "end": v(-24.53, 60.6) * mm});
            skLineSegment(sketch, "E1530", {"start": v(-24.53, 60.6) * mm, "end": v(-24.53, 60.48) * mm});
            skLineSegment(sketch, "E1531", {"start": v(-24.53, 60.48) * mm, "end": v(-24.5, 60.25) * mm});
            skLineSegment(sketch, "E1532", {"start": v(-24.5, 60.25) * mm, "end": v(-24.5, 60.14) * mm});
            skLineSegment(sketch, "E1533", {"start": v(-24.5, 60.14) * mm, "end": v(-24.49, 60.03) * mm});
            skLineSegment(sketch, "E1534", {"start": v(-24.49, 60.03) * mm, "end": v(-24.48, 59.93) * mm});
            skLineSegment(sketch, "E1535", {"start": v(-24.48, 59.93) * mm, "end": v(-24.47, 59.82) * mm});
            skLineSegment(sketch, "E1536", {"start": v(-24.47, 59.82) * mm, "end": v(-24.45, 59.72) * mm});
            skLineSegment(sketch, "E1537", {"start": v(-24.45, 59.72) * mm, "end": v(-24.44, 59.62) * mm});
            skLineSegment(sketch, "E1538", {"start": v(-24.44, 59.62) * mm, "end": v(-24.43, 59.53) * mm});
            skLineSegment(sketch, "E1539", {"start": v(-24.43, 59.53) * mm, "end": v(-24.42, 59.43) * mm});
            skLineSegment(sketch, "E1540", {"start": v(-24.42, 59.43) * mm, "end": v(-24.4, 59.34) * mm});
            skLineSegment(sketch, "E1541", {"start": v(-24.4, 59.34) * mm, "end": v(-24.4, 59.25) * mm});
            skLineSegment(sketch, "E1542", {"start": v(-24.4, 59.25) * mm, "end": v(-24.38, 59.16) * mm});
            skLineSegment(sketch, "E1543", {"start": v(-24.38, 59.16) * mm, "end": v(-24.36, 59.07) * mm});
            skLineSegment(sketch, "E1544", {"start": v(-24.36, 59.07) * mm, "end": v(-24.35, 58.99) * mm});
            skLineSegment(sketch, "E1545", {"start": v(-24.35, 58.99) * mm, "end": v(-24.34, 58.9) * mm});
            skLineSegment(sketch, "E1546", {"start": v(-24.34, 58.9) * mm, "end": v(-24.51, 58.7) * mm});
            skLineSegment(sketch, "E1547", {"start": v(-24.51, 58.7) * mm, "end": v(-25.87, 58.11) * mm});
            skLineSegment(sketch, "E1548", {"start": v(-25.87, 58.11) * mm, "end": v(-26.14, 58.13) * mm});
            skLineSegment(sketch, "E1549", {"start": v(-26.14, 58.13) * mm, "end": v(-26.2, 58.2) * mm});
            skLineSegment(sketch, "E1550", {"start": v(-26.2, 58.2) * mm, "end": v(-26.25, 58.26) * mm});
            skLineSegment(sketch, "E1551", {"start": v(-26.25, 58.26) * mm, "end": v(-26.3, 58.33) * mm});
            skLineSegment(sketch, "E1552", {"start": v(-26.3, 58.33) * mm, "end": v(-26.35, 58.4) * mm});
            skLineSegment(sketch, "E1553", {"start": v(-26.35, 58.4) * mm, "end": v(-26.41, 58.47) * mm});
            skLineSegment(sketch, "E1554", {"start": v(-26.41, 58.47) * mm, "end": v(-26.47, 58.55) * mm});
            skLineSegment(sketch, "E1555", {"start": v(-26.47, 58.55) * mm, "end": v(-26.53, 58.62) * mm});
            skLineSegment(sketch, "E1556", {"start": v(-26.53, 58.62) * mm, "end": v(-26.6, 58.7) * mm});
            skLineSegment(sketch, "E1557", {"start": v(-26.6, 58.7) * mm, "end": v(-26.66, 58.77) * mm});
            skLineSegment(sketch, "E1558", {"start": v(-26.66, 58.77) * mm, "end": v(-26.72, 58.85) * mm});
            skLineSegment(sketch, "E1559", {"start": v(-26.72, 58.85) * mm, "end": v(-26.8, 58.93) * mm});
            skLineSegment(sketch, "E1560", {"start": v(-26.8, 58.93) * mm, "end": v(-26.86, 59) * mm});
            skLineSegment(sketch, "E1561", {"start": v(-26.86, 59) * mm, "end": v(-26.93, 59.1) * mm});
            skLineSegment(sketch, "E1562", {"start": v(-26.93, 59.1) * mm, "end": v(-27, 59.17) * mm});
            skLineSegment(sketch, "E1563", {"start": v(-27, 59.17) * mm, "end": v(-27.08, 59.26) * mm});
            skLineSegment(sketch, "E1564", {"start": v(-27.08, 59.26) * mm, "end": v(-27.16, 59.34) * mm});
            skLineSegment(sketch, "E1565", {"start": v(-27.16, 59.34) * mm, "end": v(-27.24, 59.43) * mm});
            skLineSegment(sketch, "E1566", {"start": v(-27.24, 59.43) * mm, "end": v(-27.32, 59.52) * mm});
            skLineSegment(sketch, "E1567", {"start": v(-27.32, 59.52) * mm, "end": v(-27.4, 59.6) * mm});
            skLineSegment(sketch, "E1568", {"start": v(-27.4, 59.6) * mm, "end": v(-27.48, 59.7) * mm});
            skLineSegment(sketch, "E1569", {"start": v(-27.48, 59.7) * mm, "end": v(-27.57, 59.78) * mm});
            skLineSegment(sketch, "E1570", {"start": v(-27.57, 59.78) * mm, "end": v(-27.66, 59.87) * mm});
            skLineSegment(sketch, "E1571", {"start": v(-27.66, 59.87) * mm, "end": v(-27.75, 59.97) * mm});
            skLineSegment(sketch, "E1572", {"start": v(-27.75, 59.97) * mm, "end": v(-27.84, 60.06) * mm});
            skLineSegment(sketch, "E1573", {"start": v(-27.84, 60.06) * mm, "end": v(-27.94, 60.15) * mm});
            skLineSegment(sketch, "E1574", {"start": v(-27.94, 60.15) * mm, "end": v(-28.03, 60.25) * mm});
            skLineSegment(sketch, "E1575", {"start": v(-28.03, 60.25) * mm, "end": v(-28.13, 60.35) * mm});
            skLineSegment(sketch, "E1576", {"start": v(-28.13, 60.35) * mm, "end": v(-28.23, 60.44) * mm});
            skLineSegment(sketch, "E1577", {"start": v(-28.23, 60.44) * mm, "end": v(-28.34, 60.54) * mm});
            skLineSegment(sketch, "E1578", {"start": v(-28.34, 60.54) * mm, "end": v(-28.44, 60.64) * mm});
            skLineSegment(sketch, "E1579", {"start": v(-28.44, 60.64) * mm, "end": v(-28.55, 60.74) * mm});
            skLineSegment(sketch, "E1580", {"start": v(-28.55, 60.74) * mm, "end": v(-28.77, 60.94) * mm});
            skLineSegment(sketch, "E1581", {"start": v(-28.77, 60.94) * mm, "end": v(-28.88, 61.04) * mm});
            skLineSegment(sketch, "E1582", {"start": v(-28.88, 61.04) * mm, "end": v(-29, 61.14) * mm});
            skLineSegment(sketch, "E1583", {"start": v(-29, 61.14) * mm, "end": v(-29.12, 61.25) * mm});
            skLineSegment(sketch, "E1584", {"start": v(-29.12, 61.25) * mm, "end": v(-29.24, 61.35) * mm});
            skLineSegment(sketch, "E1585", {"start": v(-29.24, 61.35) * mm, "end": v(-29.36, 61.45) * mm});
            skLineSegment(sketch, "E1586", {"start": v(-29.36, 61.45) * mm, "end": v(-29.48, 61.56) * mm});
            skLineSegment(sketch, "E1587", {"start": v(-29.48, 61.56) * mm, "end": v(-29.59, 61.61) * mm});
            skLineSegment(sketch, "E1588", {"start": v(-29.59, 61.61) * mm, "end": v(-31.05, 60.9) * mm});
            skLineSegment(sketch, "E1589", {"start": v(-31.05, 60.9) * mm, "end": v(-31.07, 60.78) * mm});
            skLineSegment(sketch, "E1590", {"start": v(-31.07, 60.78) * mm, "end": v(-31.06, 60.62) * mm});
            skLineSegment(sketch, "E1591", {"start": v(-31.06, 60.62) * mm, "end": v(-31.05, 60.45) * mm});
            skLineSegment(sketch, "E1592", {"start": v(-31.05, 60.45) * mm, "end": v(-31.04, 60.3) * mm});
            skLineSegment(sketch, "E1593", {"start": v(-31.04, 60.3) * mm, "end": v(-31.03, 60.14) * mm});
            skLineSegment(sketch, "E1594", {"start": v(-31.03, 60.14) * mm, "end": v(-31.02, 59.99) * mm});
            skLineSegment(sketch, "E1595", {"start": v(-31.02, 59.99) * mm, "end": v(-31, 59.83) * mm});
            skLineSegment(sketch, "E1596", {"start": v(-31, 59.83) * mm, "end": v(-31, 59.68) * mm});
            skLineSegment(sketch, "E1597", {"start": v(-31, 59.68) * mm, "end": v(-30.98, 59.54) * mm});
            skLineSegment(sketch, "E1598", {"start": v(-30.98, 59.54) * mm, "end": v(-30.96, 59.4) * mm});
            skLineSegment(sketch, "E1599", {"start": v(-30.96, 59.4) * mm, "end": v(-30.95, 59.25) * mm});
            skLineSegment(sketch, "E1600", {"start": v(-30.95, 59.25) * mm, "end": v(-30.93, 59.1) * mm});
            skLineSegment(sketch, "E1601", {"start": v(-30.93, 59.1) * mm, "end": v(-30.92, 58.97) * mm});
            skLineSegment(sketch, "E1602", {"start": v(-30.92, 58.97) * mm, "end": v(-30.9, 58.83) * mm});
            skLineSegment(sketch, "E1603", {"start": v(-30.9, 58.83) * mm, "end": v(-30.89, 58.7) * mm});
            skLineSegment(sketch, "E1604", {"start": v(-30.89, 58.7) * mm, "end": v(-30.87, 58.56) * mm});
            skLineSegment(sketch, "E1605", {"start": v(-30.87, 58.56) * mm, "end": v(-30.85, 58.43) * mm});
            skLineSegment(sketch, "E1606", {"start": v(-30.85, 58.43) * mm, "end": v(-30.83, 58.3) * mm});
            skLineSegment(sketch, "E1607", {"start": v(-30.83, 58.3) * mm, "end": v(-30.81, 58.18) * mm});
            skLineSegment(sketch, "E1608", {"start": v(-30.81, 58.18) * mm, "end": v(-30.8, 58.06) * mm});
            skLineSegment(sketch, "E1609", {"start": v(-30.8, 58.06) * mm, "end": v(-30.77, 57.93) * mm});
            skLineSegment(sketch, "E1610", {"start": v(-30.77, 57.93) * mm, "end": v(-30.75, 57.81) * mm});
            skLineSegment(sketch, "E1611", {"start": v(-30.75, 57.81) * mm, "end": v(-30.73, 57.7) * mm});
            skLineSegment(sketch, "E1612", {"start": v(-30.73, 57.7) * mm, "end": v(-30.71, 57.58) * mm});
            skLineSegment(sketch, "E1613", {"start": v(-30.71, 57.58) * mm, "end": v(-30.7, 57.47) * mm});
            skLineSegment(sketch, "E1614", {"start": v(-30.7, 57.47) * mm, "end": v(-30.67, 57.36) * mm});
            skLineSegment(sketch, "E1615", {"start": v(-30.67, 57.36) * mm, "end": v(-30.65, 57.25) * mm});
            skLineSegment(sketch, "E1616", {"start": v(-30.65, 57.25) * mm, "end": v(-30.63, 57.14) * mm});
            skLineSegment(sketch, "E1617", {"start": v(-30.63, 57.14) * mm, "end": v(-30.6, 57.04) * mm});
            skLineSegment(sketch, "E1618", {"start": v(-30.6, 57.04) * mm, "end": v(-30.58, 56.94) * mm});
            skLineSegment(sketch, "E1619", {"start": v(-30.58, 56.94) * mm, "end": v(-30.56, 56.84) * mm});
            skLineSegment(sketch, "E1620", {"start": v(-30.56, 56.84) * mm, "end": v(-30.54, 56.74) * mm});
            skLineSegment(sketch, "E1621", {"start": v(-30.54, 56.74) * mm, "end": v(-30.52, 56.65) * mm});
            skLineSegment(sketch, "E1622", {"start": v(-30.52, 56.65) * mm, "end": v(-30.5, 56.55) * mm});
            skLineSegment(sketch, "E1623", {"start": v(-30.5, 56.55) * mm, "end": v(-30.47, 56.46) * mm});
            skLineSegment(sketch, "E1624", {"start": v(-30.47, 56.46) * mm, "end": v(-30.45, 56.37) * mm});
            skLineSegment(sketch, "E1625", {"start": v(-30.45, 56.37) * mm, "end": v(-30.43, 56.29) * mm});
            skLineSegment(sketch, "E1626", {"start": v(-30.43, 56.29) * mm, "end": v(-30.4, 56.2) * mm});
            skLineSegment(sketch, "E1627", {"start": v(-30.4, 56.2) * mm, "end": v(-30.38, 56.12) * mm});
            skLineSegment(sketch, "E1628", {"start": v(-30.38, 56.12) * mm, "end": v(-30.36, 56.04) * mm});
            skLineSegment(sketch, "E1629", {"start": v(-30.36, 56.04) * mm, "end": v(-30.51, 55.81) * mm});
            skLineSegment(sketch, "E1630", {"start": v(-30.51, 55.81) * mm, "end": v(-31.8, 55.09) * mm});
            skLineSegment(sketch, "E1631", {"start": v(-31.8, 55.09) * mm, "end": v(-32.08, 55.08) * mm});
            skLineSegment(sketch, "E1632", {"start": v(-32.08, 55.08) * mm, "end": v(-32.13, 55.14) * mm});
            skLineSegment(sketch, "E1633", {"start": v(-32.13, 55.14) * mm, "end": v(-32.2, 55.2) * mm});
            skLineSegment(sketch, "E1634", {"start": v(-32.2, 55.2) * mm, "end": v(-32.25, 55.26) * mm});
            skLineSegment(sketch, "E1635", {"start": v(-32.25, 55.26) * mm, "end": v(-32.32, 55.33) * mm});
            skLineSegment(sketch, "E1636", {"start": v(-32.32, 55.33) * mm, "end": v(-32.38, 55.4) * mm});
            skLineSegment(sketch, "E1637", {"start": v(-32.38, 55.4) * mm, "end": v(-32.44, 55.46) * mm});
            skLineSegment(sketch, "E1638", {"start": v(-32.44, 55.46) * mm, "end": v(-32.51, 55.53) * mm});
            skLineSegment(sketch, "E1639", {"start": v(-32.51, 55.53) * mm, "end": v(-32.58, 55.6) * mm});
            skLineSegment(sketch, "E1640", {"start": v(-32.58, 55.6) * mm, "end": v(-32.65, 55.66) * mm});
            skLineSegment(sketch, "E1641", {"start": v(-32.65, 55.66) * mm, "end": v(-32.8, 55.8) * mm});
            skLineSegment(sketch, "E1642", {"start": v(-32.8, 55.8) * mm, "end": v(-32.88, 55.88) * mm});
            skLineSegment(sketch, "E1643", {"start": v(-32.88, 55.88) * mm, "end": v(-32.96, 55.95) * mm});
            skLineSegment(sketch, "E1644", {"start": v(-32.96, 55.95) * mm, "end": v(-33.04, 56.03) * mm});
            skLineSegment(sketch, "E1645", {"start": v(-33.04, 56.03) * mm, "end": v(-33.13, 56.1) * mm});
            skLineSegment(sketch, "E1646", {"start": v(-33.13, 56.1) * mm, "end": v(-33.21, 56.18) * mm});
            skLineSegment(sketch, "E1647", {"start": v(-33.21, 56.18) * mm, "end": v(-33.3, 56.26) * mm});
            skLineSegment(sketch, "E1648", {"start": v(-33.3, 56.26) * mm, "end": v(-33.39, 56.33) * mm});
            skLineSegment(sketch, "E1649", {"start": v(-33.39, 56.33) * mm, "end": v(-33.48, 56.41) * mm});
            skLineSegment(sketch, "E1650", {"start": v(-33.48, 56.41) * mm, "end": v(-33.57, 56.5) * mm});
            skLineSegment(sketch, "E1651", {"start": v(-33.57, 56.5) * mm, "end": v(-33.67, 56.57) * mm});
            skLineSegment(sketch, "E1652", {"start": v(-33.67, 56.57) * mm, "end": v(-33.77, 56.66) * mm});
            skLineSegment(sketch, "E1653", {"start": v(-33.77, 56.66) * mm, "end": v(-33.97, 56.82) * mm});
            skLineSegment(sketch, "E1654", {"start": v(-33.97, 56.82) * mm, "end": v(-34.07, 56.9) * mm});
            skLineSegment(sketch, "E1655", {"start": v(-34.07, 56.9) * mm, "end": v(-34.18, 56.99) * mm});
            skLineSegment(sketch, "E1656", {"start": v(-34.18, 56.99) * mm, "end": v(-34.29, 57.07) * mm});
            skLineSegment(sketch, "E1657", {"start": v(-34.29, 57.07) * mm, "end": v(-34.4, 57.16) * mm});
            skLineSegment(sketch, "E1658", {"start": v(-34.4, 57.16) * mm, "end": v(-34.51, 57.25) * mm});
            skLineSegment(sketch, "E1659", {"start": v(-34.51, 57.25) * mm, "end": v(-34.62, 57.33) * mm});
            skLineSegment(sketch, "E1660", {"start": v(-34.62, 57.33) * mm, "end": v(-34.74, 57.42) * mm});
            skLineSegment(sketch, "E1661", {"start": v(-34.74, 57.42) * mm, "end": v(-34.86, 57.5) * mm});
            skLineSegment(sketch, "E1662", {"start": v(-34.86, 57.5) * mm, "end": v(-34.98, 57.6) * mm});
            skLineSegment(sketch, "E1663", {"start": v(-34.98, 57.6) * mm, "end": v(-35.1, 57.69) * mm});
            skLineSegment(sketch, "E1664", {"start": v(-35.1, 57.69) * mm, "end": v(-35.23, 57.78) * mm});
            skLineSegment(sketch, "E1665", {"start": v(-35.23, 57.78) * mm, "end": v(-35.36, 57.87) * mm});
            skLineSegment(sketch, "E1666", {"start": v(-35.36, 57.87) * mm, "end": v(-35.5, 57.96) * mm});
            skLineSegment(sketch, "E1667", {"start": v(-35.5, 57.96) * mm, "end": v(-35.62, 58.05) * mm});
            skLineSegment(sketch, "E1668", {"start": v(-35.62, 58.05) * mm, "end": v(-35.76, 58.14) * mm});
            skLineSegment(sketch, "E1669", {"start": v(-35.76, 58.14) * mm, "end": v(-35.86, 58.19) * mm});
            skLineSegment(sketch, "E1670", {"start": v(-35.86, 58.19) * mm, "end": v(-37.24, 57.31) * mm});
            skLineSegment(sketch, "E1671", {"start": v(-37.24, 57.31) * mm, "end": v(-37.25, 57.2) * mm});
            skLineSegment(sketch, "E1672", {"start": v(-37.25, 57.2) * mm, "end": v(-37.22, 57.04) * mm});
            skLineSegment(sketch, "E1673", {"start": v(-37.22, 57.04) * mm, "end": v(-37.2, 56.88) * mm});
            skLineSegment(sketch, "E1674", {"start": v(-37.2, 56.88) * mm, "end": v(-37.17, 56.72) * mm});
            skLineSegment(sketch, "E1675", {"start": v(-37.17, 56.72) * mm, "end": v(-37.14, 56.57) * mm});
            skLineSegment(sketch, "E1676", {"start": v(-37.14, 56.57) * mm, "end": v(-37.12, 56.42) * mm});
            skLineSegment(sketch, "E1677", {"start": v(-37.12, 56.42) * mm, "end": v(-37.09, 56.27) * mm});
            skLineSegment(sketch, "E1678", {"start": v(-37.09, 56.27) * mm, "end": v(-37.06, 56.12) * mm});
            skLineSegment(sketch, "E1679", {"start": v(-37.06, 56.12) * mm, "end": v(-37.03, 55.97) * mm});
            skLineSegment(sketch, "E1680", {"start": v(-37.03, 55.97) * mm, "end": v(-37, 55.83) * mm});
            skLineSegment(sketch, "E1681", {"start": v(-37, 55.83) * mm, "end": v(-36.97, 55.69) * mm});
            skLineSegment(sketch, "E1682", {"start": v(-36.97, 55.69) * mm, "end": v(-36.94, 55.55) * mm});
            skLineSegment(sketch, "E1683", {"start": v(-36.94, 55.55) * mm, "end": v(-36.91, 55.41) * mm});
            skLineSegment(sketch, "E1684", {"start": v(-36.91, 55.41) * mm, "end": v(-36.88, 55.28) * mm});
            skLineSegment(sketch, "E1685", {"start": v(-36.88, 55.28) * mm, "end": v(-36.85, 55.14) * mm});
            skLineSegment(sketch, "E1686", {"start": v(-36.85, 55.14) * mm, "end": v(-36.82, 55.02) * mm});
            skLineSegment(sketch, "E1687", {"start": v(-36.82, 55.02) * mm, "end": v(-36.79, 54.89) * mm});
            skLineSegment(sketch, "E1688", {"start": v(-36.79, 54.89) * mm, "end": v(-36.76, 54.76) * mm});
            skLineSegment(sketch, "E1689", {"start": v(-36.76, 54.76) * mm, "end": v(-36.73, 54.64) * mm});
            skLineSegment(sketch, "E1690", {"start": v(-36.73, 54.64) * mm, "end": v(-36.7, 54.52) * mm});
            skLineSegment(sketch, "E1691", {"start": v(-36.7, 54.52) * mm, "end": v(-36.66, 54.4) * mm});
            skLineSegment(sketch, "E1692", {"start": v(-36.66, 54.4) * mm, "end": v(-36.63, 54.28) * mm});
            skLineSegment(sketch, "E1693", {"start": v(-36.63, 54.28) * mm, "end": v(-36.6, 54.17) * mm});
            skLineSegment(sketch, "E1694", {"start": v(-36.6, 54.17) * mm, "end": v(-36.56, 54.06) * mm});
            skLineSegment(sketch, "E1695", {"start": v(-36.56, 54.06) * mm, "end": v(-36.53, 53.95) * mm});
            skLineSegment(sketch, "E1696", {"start": v(-36.53, 53.95) * mm, "end": v(-36.5, 53.84) * mm});
            skLineSegment(sketch, "E1697", {"start": v(-36.5, 53.84) * mm, "end": v(-36.47, 53.73) * mm});
            skLineSegment(sketch, "E1698", {"start": v(-36.47, 53.73) * mm, "end": v(-36.43, 53.63) * mm});
            skLineSegment(sketch, "E1699", {"start": v(-36.43, 53.63) * mm, "end": v(-36.4, 53.53) * mm});
            skLineSegment(sketch, "E1700", {"start": v(-36.4, 53.53) * mm, "end": v(-36.37, 53.43) * mm});
            skLineSegment(sketch, "E1701", {"start": v(-36.37, 53.43) * mm, "end": v(-36.34, 53.33) * mm});
            skLineSegment(sketch, "E1702", {"start": v(-36.34, 53.33) * mm, "end": v(-36.3, 53.24) * mm});
            skLineSegment(sketch, "E1703", {"start": v(-36.3, 53.24) * mm, "end": v(-36.27, 53.15) * mm});
            skLineSegment(sketch, "E1704", {"start": v(-36.27, 53.15) * mm, "end": v(-36.24, 53.06) * mm});
            skLineSegment(sketch, "E1705", {"start": v(-36.24, 53.06) * mm, "end": v(-36.2, 52.97) * mm});
            skLineSegment(sketch, "E1706", {"start": v(-36.2, 52.97) * mm, "end": v(-36.18, 52.88) * mm});
            skLineSegment(sketch, "E1707", {"start": v(-36.18, 52.88) * mm, "end": v(-36.15, 52.8) * mm});
            skLineSegment(sketch, "E1708", {"start": v(-36.15, 52.8) * mm, "end": v(-36.11, 52.72) * mm});
            skLineSegment(sketch, "E1709", {"start": v(-36.11, 52.72) * mm, "end": v(-36.08, 52.64) * mm});
            skLineSegment(sketch, "E1710", {"start": v(-36.08, 52.64) * mm, "end": v(-36.05, 52.56) * mm});
            skLineSegment(sketch, "E1711", {"start": v(-36.05, 52.56) * mm, "end": v(-36.18, 52.32) * mm});
            skLineSegment(sketch, "E1712", {"start": v(-36.18, 52.32) * mm, "end": v(-37.39, 51.46) * mm});
            skLineSegment(sketch, "E1713", {"start": v(-37.39, 51.46) * mm, "end": v(-37.66, 51.42) * mm});
            skLineSegment(sketch, "E1714", {"start": v(-37.66, 51.42) * mm, "end": v(-37.72, 51.48) * mm});
            skLineSegment(sketch, "E1715", {"start": v(-37.72, 51.48) * mm, "end": v(-37.79, 51.53) * mm});
            skLineSegment(sketch, "E1716", {"start": v(-37.79, 51.53) * mm, "end": v(-37.85, 51.59) * mm});
            skLineSegment(sketch, "E1717", {"start": v(-37.85, 51.59) * mm, "end": v(-37.92, 51.64) * mm});
            skLineSegment(sketch, "E1718", {"start": v(-37.92, 51.64) * mm, "end": v(-38, 51.7) * mm});
            skLineSegment(sketch, "E1719", {"start": v(-38, 51.7) * mm, "end": v(-38.06, 51.76) * mm});
            skLineSegment(sketch, "E1720", {"start": v(-38.06, 51.76) * mm, "end": v(-38.14, 51.82) * mm});
            skLineSegment(sketch, "E1721", {"start": v(-38.14, 51.82) * mm, "end": v(-38.22, 51.88) * mm});
            skLineSegment(sketch, "E1722", {"start": v(-38.22, 51.88) * mm, "end": v(-38.3, 51.95) * mm});
            skLineSegment(sketch, "E1723", {"start": v(-38.3, 51.95) * mm, "end": v(-38.37, 52) * mm});
            skLineSegment(sketch, "E1724", {"start": v(-38.37, 52) * mm, "end": v(-38.46, 52.07) * mm});
            skLineSegment(sketch, "E1725", {"start": v(-38.46, 52.07) * mm, "end": v(-38.54, 52.14) * mm});
            skLineSegment(sketch, "E1726", {"start": v(-38.54, 52.14) * mm, "end": v(-38.63, 52.2) * mm});
            skLineSegment(sketch, "E1727", {"start": v(-38.63, 52.2) * mm, "end": v(-38.72, 52.27) * mm});
            skLineSegment(sketch, "E1728", {"start": v(-38.72, 52.27) * mm, "end": v(-38.8, 52.33) * mm});
            skLineSegment(sketch, "E1729", {"start": v(-38.8, 52.33) * mm, "end": v(-38.9, 52.4) * mm});
            skLineSegment(sketch, "E1730", {"start": v(-38.9, 52.4) * mm, "end": v(-39, 52.47) * mm});
            skLineSegment(sketch, "E1731", {"start": v(-39, 52.47) * mm, "end": v(-39.1, 52.54) * mm});
            skLineSegment(sketch, "E1732", {"start": v(-39.1, 52.54) * mm, "end": v(-39.2, 52.6) * mm});
            skLineSegment(sketch, "E1733", {"start": v(-39.2, 52.6) * mm, "end": v(-39.3, 52.67) * mm});
            skLineSegment(sketch, "E1734", {"start": v(-39.3, 52.67) * mm, "end": v(-39.4, 52.74) * mm});
            skLineSegment(sketch, "E1735", {"start": v(-39.4, 52.74) * mm, "end": v(-39.5, 52.82) * mm});
            skLineSegment(sketch, "E1736", {"start": v(-39.5, 52.82) * mm, "end": v(-39.72, 52.96) * mm});
            skLineSegment(sketch, "E1737", {"start": v(-39.72, 52.96) * mm, "end": v(-39.83, 53.03) * mm});
            skLineSegment(sketch, "E1738", {"start": v(-39.83, 53.03) * mm, "end": v(-39.95, 53.1) * mm});
            skLineSegment(sketch, "E1739", {"start": v(-39.95, 53.1) * mm, "end": v(-40.07, 53.18) * mm});
            skLineSegment(sketch, "E1740", {"start": v(-40.07, 53.18) * mm, "end": v(-40.18, 53.25) * mm});
            skLineSegment(sketch, "E1741", {"start": v(-40.18, 53.25) * mm, "end": v(-40.3, 53.33) * mm});
            skLineSegment(sketch, "E1742", {"start": v(-40.3, 53.33) * mm, "end": v(-40.43, 53.4) * mm});
            skLineSegment(sketch, "E1743", {"start": v(-40.43, 53.4) * mm, "end": v(-40.55, 53.48) * mm});
            skLineSegment(sketch, "E1744", {"start": v(-40.55, 53.48) * mm, "end": v(-40.68, 53.55) * mm});
            skLineSegment(sketch, "E1745", {"start": v(-40.68, 53.55) * mm, "end": v(-40.81, 53.63) * mm});
            skLineSegment(sketch, "E1746", {"start": v(-40.81, 53.63) * mm, "end": v(-40.94, 53.7) * mm});
            skLineSegment(sketch, "E1747", {"start": v(-40.94, 53.7) * mm, "end": v(-41.08, 53.78) * mm});
            skLineSegment(sketch, "E1748", {"start": v(-41.08, 53.78) * mm, "end": v(-41.21, 53.85) * mm});
            skLineSegment(sketch, "E1749", {"start": v(-41.21, 53.85) * mm, "end": v(-41.35, 53.93) * mm});
            skLineSegment(sketch, "E1750", {"start": v(-41.35, 53.93) * mm, "end": v(-41.5, 54) * mm});
            skLineSegment(sketch, "E1751", {"start": v(-41.5, 54) * mm, "end": v(-41.64, 54.09) * mm});
            skLineSegment(sketch, "E1752", {"start": v(-41.64, 54.09) * mm, "end": v(-41.75, 54.12) * mm});
            skLineSegment(sketch, "E1753", {"start": v(-41.75, 54.12) * mm, "end": v(-43.03, 53.1) * mm});
            skLineSegment(sketch, "E1754", {"start": v(-43.03, 53.1) * mm, "end": v(-43.02, 53) * mm});
            skLineSegment(sketch, "E1755", {"start": v(-43.02, 53) * mm, "end": v(-42.98, 52.83) * mm});
            skLineSegment(sketch, "E1756", {"start": v(-42.98, 52.83) * mm, "end": v(-42.94, 52.68) * mm});
            skLineSegment(sketch, "E1757", {"start": v(-42.94, 52.68) * mm, "end": v(-42.9, 52.53) * mm});
            skLineSegment(sketch, "E1758", {"start": v(-42.9, 52.53) * mm, "end": v(-42.85, 52.38) * mm});
            skLineSegment(sketch, "E1759", {"start": v(-42.85, 52.38) * mm, "end": v(-42.81, 52.23) * mm});
            skLineSegment(sketch, "E1760", {"start": v(-42.81, 52.23) * mm, "end": v(-42.77, 52.08) * mm});
            skLineSegment(sketch, "E1761", {"start": v(-42.77, 52.08) * mm, "end": v(-42.72, 51.94) * mm});
            skLineSegment(sketch, "E1762", {"start": v(-42.72, 51.94) * mm, "end": v(-42.68, 51.8) * mm});
            skLineSegment(sketch, "E1763", {"start": v(-42.68, 51.8) * mm, "end": v(-42.64, 51.65) * mm});
            skLineSegment(sketch, "E1764", {"start": v(-42.64, 51.65) * mm, "end": v(-42.6, 51.52) * mm});
            skLineSegment(sketch, "E1765", {"start": v(-42.6, 51.52) * mm, "end": v(-42.55, 51.38) * mm});
            skLineSegment(sketch, "E1766", {"start": v(-42.55, 51.38) * mm, "end": v(-42.5, 51.25) * mm});
            skLineSegment(sketch, "E1767", {"start": v(-42.5, 51.25) * mm, "end": v(-42.46, 51.12) * mm});
            skLineSegment(sketch, "E1768", {"start": v(-42.46, 51.12) * mm, "end": v(-42.41, 51) * mm});
            skLineSegment(sketch, "E1769", {"start": v(-42.41, 51) * mm, "end": v(-42.37, 50.87) * mm});
            skLineSegment(sketch, "E1770", {"start": v(-42.37, 50.87) * mm, "end": v(-42.33, 50.74) * mm});
            skLineSegment(sketch, "E1771", {"start": v(-42.33, 50.74) * mm, "end": v(-42.28, 50.62) * mm});
            skLineSegment(sketch, "E1772", {"start": v(-42.28, 50.62) * mm, "end": v(-42.24, 50.5) * mm});
            skLineSegment(sketch, "E1773", {"start": v(-42.24, 50.5) * mm, "end": v(-42.2, 50.38) * mm});
            skLineSegment(sketch, "E1774", {"start": v(-42.2, 50.38) * mm, "end": v(-42.15, 50.27) * mm});
            skLineSegment(sketch, "E1775", {"start": v(-42.15, 50.27) * mm, "end": v(-42.1, 50.16) * mm});
            skLineSegment(sketch, "E1776", {"start": v(-42.1, 50.16) * mm, "end": v(-42.06, 50.05) * mm});
            skLineSegment(sketch, "E1777", {"start": v(-42.06, 50.05) * mm, "end": v(-42.01, 49.94) * mm});
            skLineSegment(sketch, "E1778", {"start": v(-42.01, 49.94) * mm, "end": v(-41.97, 49.83) * mm});
            skLineSegment(sketch, "E1779", {"start": v(-41.97, 49.83) * mm, "end": v(-41.93, 49.73) * mm});
            skLineSegment(sketch, "E1780", {"start": v(-41.93, 49.73) * mm, "end": v(-41.88, 49.63) * mm});
            skLineSegment(sketch, "E1781", {"start": v(-41.88, 49.63) * mm, "end": v(-41.84, 49.53) * mm});
            skLineSegment(sketch, "E1782", {"start": v(-41.84, 49.53) * mm, "end": v(-41.8, 49.43) * mm});
            skLineSegment(sketch, "E1783", {"start": v(-41.8, 49.43) * mm, "end": v(-41.75, 49.34) * mm});
            skLineSegment(sketch, "E1784", {"start": v(-41.75, 49.34) * mm, "end": v(-41.71, 49.24) * mm});
            skLineSegment(sketch, "E1785", {"start": v(-41.71, 49.24) * mm, "end": v(-41.67, 49.15) * mm});
            skLineSegment(sketch, "E1786", {"start": v(-41.67, 49.15) * mm, "end": v(-41.63, 49.06) * mm});
            skLineSegment(sketch, "E1787", {"start": v(-41.63, 49.06) * mm, "end": v(-41.59, 48.98) * mm});
            skLineSegment(sketch, "E1788", {"start": v(-41.59, 48.98) * mm, "end": v(-41.55, 48.9) * mm});
            skLineSegment(sketch, "E1789", {"start": v(-41.55, 48.9) * mm, "end": v(-41.5, 48.8) * mm});
            skLineSegment(sketch, "E1790", {"start": v(-41.5, 48.8) * mm, "end": v(-41.47, 48.73) * mm});
            skLineSegment(sketch, "E1791", {"start": v(-41.47, 48.73) * mm, "end": v(-41.43, 48.65) * mm});
            skLineSegment(sketch, "E1792", {"start": v(-41.43, 48.65) * mm, "end": v(-41.39, 48.58) * mm});
            skLineSegment(sketch, "E1793", {"start": v(-41.39, 48.58) * mm, "end": v(-41.35, 48.5) * mm});
            skLineSegment(sketch, "E1794", {"start": v(-41.35, 48.5) * mm, "end": v(-41.45, 48.25) * mm});
            skLineSegment(sketch, "E1795", {"start": v(-41.45, 48.25) * mm, "end": v(-42.56, 47.27) * mm});
            skLineSegment(sketch, "E1796", {"start": v(-42.56, 47.27) * mm, "end": v(-42.83, 47.2) * mm});
            skLineSegment(sketch, "E1797", {"start": v(-42.83, 47.2) * mm, "end": v(-42.9, 47.25) * mm});
            skLineSegment(sketch, "E1798", {"start": v(-42.9, 47.25) * mm, "end": v(-42.96, 47.3) * mm});
            skLineSegment(sketch, "E1799", {"start": v(-42.96, 47.3) * mm, "end": v(-43.04, 47.35) * mm});
            skLineSegment(sketch, "E1800", {"start": v(-43.04, 47.35) * mm, "end": v(-43.11, 47.4) * mm});
            skLineSegment(sketch, "E1801", {"start": v(-43.11, 47.4) * mm, "end": v(-43.19, 47.45) * mm});
            skLineSegment(sketch, "E1802", {"start": v(-43.19, 47.45) * mm, "end": v(-43.27, 47.5) * mm});
            skLineSegment(sketch, "E1803", {"start": v(-43.27, 47.5) * mm, "end": v(-43.35, 47.55) * mm});
            skLineSegment(sketch, "E1804", {"start": v(-43.35, 47.55) * mm, "end": v(-43.43, 47.6) * mm});
            skLineSegment(sketch, "E1805", {"start": v(-43.43, 47.6) * mm, "end": v(-43.51, 47.66) * mm});
            skLineSegment(sketch, "E1806", {"start": v(-43.51, 47.66) * mm, "end": v(-43.6, 47.71) * mm});
            skLineSegment(sketch, "E1807", {"start": v(-43.6, 47.71) * mm, "end": v(-43.69, 47.77) * mm});
            skLineSegment(sketch, "E1808", {"start": v(-43.69, 47.77) * mm, "end": v(-43.78, 47.82) * mm});
            skLineSegment(sketch, "E1809", {"start": v(-43.78, 47.82) * mm, "end": v(-43.87, 47.88) * mm});
            skLineSegment(sketch, "E1810", {"start": v(-43.87, 47.88) * mm, "end": v(-43.97, 47.93) * mm});
            skLineSegment(sketch, "E1811", {"start": v(-43.97, 47.93) * mm, "end": v(-44.07, 47.99) * mm});
            skLineSegment(sketch, "E1812", {"start": v(-44.07, 47.99) * mm, "end": v(-44.16, 48.05) * mm});
            skLineSegment(sketch, "E1813", {"start": v(-44.16, 48.05) * mm, "end": v(-44.27, 48.1) * mm});
            skLineSegment(sketch, "E1814", {"start": v(-44.27, 48.1) * mm, "end": v(-44.37, 48.16) * mm});
            skLineSegment(sketch, "E1815", {"start": v(-44.37, 48.16) * mm, "end": v(-44.48, 48.22) * mm});
            skLineSegment(sketch, "E1816", {"start": v(-44.48, 48.22) * mm, "end": v(-44.59, 48.28) * mm});
            skLineSegment(sketch, "E1817", {"start": v(-44.59, 48.28) * mm, "end": v(-44.7, 48.34) * mm});
            skLineSegment(sketch, "E1818", {"start": v(-44.7, 48.34) * mm, "end": v(-44.8, 48.4) * mm});
            skLineSegment(sketch, "E1819", {"start": v(-44.8, 48.4) * mm, "end": v(-44.92, 48.46) * mm});
            skLineSegment(sketch, "E1820", {"start": v(-44.92, 48.46) * mm, "end": v(-45.04, 48.52) * mm});
            skLineSegment(sketch, "E1821", {"start": v(-45.04, 48.52) * mm, "end": v(-45.16, 48.58) * mm});
            skLineSegment(sketch, "E1822", {"start": v(-45.16, 48.58) * mm, "end": v(-45.28, 48.64) * mm});
            skLineSegment(sketch, "E1823", {"start": v(-45.28, 48.64) * mm, "end": v(-45.4, 48.7) * mm});
            skLineSegment(sketch, "E1824", {"start": v(-45.4, 48.7) * mm, "end": v(-45.53, 48.76) * mm});
            skLineSegment(sketch, "E1825", {"start": v(-45.53, 48.76) * mm, "end": v(-45.66, 48.82) * mm});
            skLineSegment(sketch, "E1826", {"start": v(-45.66, 48.82) * mm, "end": v(-45.79, 48.88) * mm});
            skLineSegment(sketch, "E1827", {"start": v(-45.79, 48.88) * mm, "end": v(-45.92, 48.94) * mm});
            skLineSegment(sketch, "E1828", {"start": v(-45.92, 48.94) * mm, "end": v(-46.06, 49) * mm});
            skLineSegment(sketch, "E1829", {"start": v(-46.06, 49) * mm, "end": v(-46.2, 49.07) * mm});
            skLineSegment(sketch, "E1830", {"start": v(-46.2, 49.07) * mm, "end": v(-46.33, 49.13) * mm});
            skLineSegment(sketch, "E1831", {"start": v(-46.33, 49.13) * mm, "end": v(-46.47, 49.2) * mm});
            skLineSegment(sketch, "E1832", {"start": v(-46.47, 49.2) * mm, "end": v(-46.62, 49.25) * mm});
            skLineSegment(sketch, "E1833", {"start": v(-46.62, 49.25) * mm, "end": v(-46.77, 49.31) * mm});
            skLineSegment(sketch, "E1834", {"start": v(-46.77, 49.31) * mm, "end": v(-46.91, 49.38) * mm});
            skLineSegment(sketch, "E1835", {"start": v(-46.91, 49.38) * mm, "end": v(-47.06, 49.44) * mm});
            skLineSegment(sketch, "E1836", {"start": v(-47.06, 49.44) * mm, "end": v(-47.18, 49.46) * mm});
            skLineSegment(sketch, "E1837", {"start": v(-47.18, 49.46) * mm, "end": v(-48.34, 48.32) * mm});
            skLineSegment(sketch, "E1838", {"start": v(-48.34, 48.32) * mm, "end": v(-48.33, 48.2) * mm});
            skLineSegment(sketch, "E1839", {"start": v(-48.33, 48.2) * mm, "end": v(-48.27, 48.05) * mm});
            skLineSegment(sketch, "E1840", {"start": v(-48.27, 48.05) * mm, "end": v(-48.2, 47.9) * mm});
            skLineSegment(sketch, "E1841", {"start": v(-48.2, 47.9) * mm, "end": v(-48.15, 47.75) * mm});
            skLineSegment(sketch, "E1842", {"start": v(-48.15, 47.75) * mm, "end": v(-48.1, 47.6) * mm});
            skLineSegment(sketch, "E1843", {"start": v(-48.1, 47.6) * mm, "end": v(-48.04, 47.47) * mm});
            skLineSegment(sketch, "E1844", {"start": v(-48.04, 47.47) * mm, "end": v(-47.98, 47.32) * mm});
            skLineSegment(sketch, "E1845", {"start": v(-47.98, 47.32) * mm, "end": v(-47.92, 47.19) * mm});
            skLineSegment(sketch, "E1846", {"start": v(-47.92, 47.19) * mm, "end": v(-47.86, 47.05) * mm});
            skLineSegment(sketch, "E1847", {"start": v(-47.86, 47.05) * mm, "end": v(-47.8, 46.92) * mm});
            skLineSegment(sketch, "E1848", {"start": v(-47.8, 46.92) * mm, "end": v(-47.74, 46.78) * mm});
            skLineSegment(sketch, "E1849", {"start": v(-47.74, 46.78) * mm, "end": v(-47.69, 46.65) * mm});
            skLineSegment(sketch, "E1850", {"start": v(-47.69, 46.65) * mm, "end": v(-47.63, 46.53) * mm});
            skLineSegment(sketch, "E1851", {"start": v(-47.63, 46.53) * mm, "end": v(-47.57, 46.4) * mm});
            skLineSegment(sketch, "E1852", {"start": v(-47.57, 46.4) * mm, "end": v(-47.51, 46.28) * mm});
            skLineSegment(sketch, "E1853", {"start": v(-47.51, 46.28) * mm, "end": v(-47.45, 46.16) * mm});
            skLineSegment(sketch, "E1854", {"start": v(-47.45, 46.16) * mm, "end": v(-47.4, 46.04) * mm});
            skLineSegment(sketch, "E1855", {"start": v(-47.4, 46.04) * mm, "end": v(-47.34, 45.92) * mm});
            skLineSegment(sketch, "E1856", {"start": v(-47.34, 45.92) * mm, "end": v(-47.28, 45.8) * mm});
            skLineSegment(sketch, "E1857", {"start": v(-47.28, 45.8) * mm, "end": v(-47.23, 45.7) * mm});
            skLineSegment(sketch, "E1858", {"start": v(-47.23, 45.7) * mm, "end": v(-47.17, 45.59) * mm});
            skLineSegment(sketch, "E1859", {"start": v(-47.17, 45.59) * mm, "end": v(-47.12, 45.48) * mm});
            skLineSegment(sketch, "E1860", {"start": v(-47.12, 45.48) * mm, "end": v(-47.06, 45.38) * mm});
            skLineSegment(sketch, "E1861", {"start": v(-47.06, 45.38) * mm, "end": v(-47, 45.27) * mm});
            skLineSegment(sketch, "E1862", {"start": v(-47, 45.27) * mm, "end": v(-46.95, 45.17) * mm});
            skLineSegment(sketch, "E1863", {"start": v(-46.95, 45.17) * mm, "end": v(-46.9, 45.07) * mm});
            skLineSegment(sketch, "E1864", {"start": v(-46.9, 45.07) * mm, "end": v(-46.84, 44.98) * mm});
            skLineSegment(sketch, "E1865", {"start": v(-46.84, 44.98) * mm, "end": v(-46.79, 44.88) * mm});
            skLineSegment(sketch, "E1866", {"start": v(-46.79, 44.88) * mm, "end": v(-46.73, 44.8) * mm});
            skLineSegment(sketch, "E1867", {"start": v(-46.73, 44.8) * mm, "end": v(-46.68, 44.7) * mm});
            skLineSegment(sketch, "E1868", {"start": v(-46.68, 44.7) * mm, "end": v(-46.63, 44.61) * mm});
            skLineSegment(sketch, "E1869", {"start": v(-46.63, 44.61) * mm, "end": v(-46.58, 44.53) * mm});
            skLineSegment(sketch, "E1870", {"start": v(-46.58, 44.53) * mm, "end": v(-46.53, 44.44) * mm});
            skLineSegment(sketch, "E1871", {"start": v(-46.53, 44.44) * mm, "end": v(-46.48, 44.36) * mm});
            skLineSegment(sketch, "E1872", {"start": v(-46.48, 44.36) * mm, "end": v(-46.43, 44.28) * mm});
            skLineSegment(sketch, "E1873", {"start": v(-46.43, 44.28) * mm, "end": v(-46.38, 44.2) * mm});
            skLineSegment(sketch, "E1874", {"start": v(-46.38, 44.2) * mm, "end": v(-46.33, 44.13) * mm});
            skLineSegment(sketch, "E1875", {"start": v(-46.33, 44.13) * mm, "end": v(-46.29, 44.06) * mm});
            skLineSegment(sketch, "E1876", {"start": v(-46.29, 44.06) * mm, "end": v(-46.24, 43.98) * mm});
            skLineSegment(sketch, "E1877", {"start": v(-46.24, 43.98) * mm, "end": v(-46.2, 43.92) * mm});
            skLineSegment(sketch, "E1878", {"start": v(-46.2, 43.92) * mm, "end": v(-46.27, 43.65) * mm});
            skLineSegment(sketch, "E1879", {"start": v(-46.27, 43.65) * mm, "end": v(-47.27, 42.56) * mm});
            skLineSegment(sketch, "E1880", {"start": v(-47.27, 42.56) * mm, "end": v(-47.53, 42.47) * mm});
            skLineSegment(sketch, "E1881", {"start": v(-47.53, 42.47) * mm, "end": v(-47.6, 42.5) * mm});
            skLineSegment(sketch, "E1882", {"start": v(-47.6, 42.5) * mm, "end": v(-47.75, 42.6) * mm});
            skLineSegment(sketch, "E1883", {"start": v(-47.75, 42.6) * mm, "end": v(-47.83, 42.63) * mm});
            skLineSegment(sketch, "E1884", {"start": v(-47.83, 42.63) * mm, "end": v(-47.91, 42.68) * mm});
            skLineSegment(sketch, "E1885", {"start": v(-47.91, 42.68) * mm, "end": v(-48, 42.72) * mm});
            skLineSegment(sketch, "E1886", {"start": v(-48, 42.72) * mm, "end": v(-48.17, 42.8) * mm});
            skLineSegment(sketch, "E1887", {"start": v(-48.17, 42.8) * mm, "end": v(-48.26, 42.85) * mm});
            skLineSegment(sketch, "E1888", {"start": v(-48.26, 42.85) * mm, "end": v(-48.35, 42.9) * mm});
            skLineSegment(sketch, "E1889", {"start": v(-48.35, 42.9) * mm, "end": v(-48.44, 42.94) * mm});
            skLineSegment(sketch, "E1890", {"start": v(-48.44, 42.94) * mm, "end": v(-48.54, 42.98) * mm});
            skLineSegment(sketch, "E1891", {"start": v(-48.54, 42.98) * mm, "end": v(-48.64, 43.03) * mm});
            skLineSegment(sketch, "E1892", {"start": v(-48.64, 43.03) * mm, "end": v(-48.74, 43.07) * mm});
            skLineSegment(sketch, "E1893", {"start": v(-48.74, 43.07) * mm, "end": v(-48.84, 43.12) * mm});
            skLineSegment(sketch, "E1894", {"start": v(-48.84, 43.12) * mm, "end": v(-48.95, 43.17) * mm});
            skLineSegment(sketch, "E1895", {"start": v(-48.95, 43.17) * mm, "end": v(-49.05, 43.21) * mm});
            skLineSegment(sketch, "E1896", {"start": v(-49.05, 43.21) * mm, "end": v(-49.16, 43.26) * mm});
            skLineSegment(sketch, "E1897", {"start": v(-49.16, 43.26) * mm, "end": v(-49.27, 43.3) * mm});
            skLineSegment(sketch, "E1898", {"start": v(-49.27, 43.3) * mm, "end": v(-49.39, 43.35) * mm});
            skLineSegment(sketch, "E1899", {"start": v(-49.39, 43.35) * mm, "end": v(-49.5, 43.4) * mm});
            skLineSegment(sketch, "E1900", {"start": v(-49.5, 43.4) * mm, "end": v(-49.62, 43.45) * mm});
            skLineSegment(sketch, "E1901", {"start": v(-49.62, 43.45) * mm, "end": v(-49.74, 43.5) * mm});
            skLineSegment(sketch, "E1902", {"start": v(-49.74, 43.5) * mm, "end": v(-49.86, 43.54) * mm});
            skLineSegment(sketch, "E1903", {"start": v(-49.86, 43.54) * mm, "end": v(-49.99, 43.6) * mm});
            skLineSegment(sketch, "E1904", {"start": v(-49.99, 43.6) * mm, "end": v(-50.12, 43.64) * mm});
            skLineSegment(sketch, "E1905", {"start": v(-50.12, 43.64) * mm, "end": v(-50.25, 43.69) * mm});
            skLineSegment(sketch, "E1906", {"start": v(-50.25, 43.69) * mm, "end": v(-50.38, 43.73) * mm});
            skLineSegment(sketch, "E1907", {"start": v(-50.38, 43.73) * mm, "end": v(-50.51, 43.78) * mm});
            skLineSegment(sketch, "E1908", {"start": v(-50.51, 43.78) * mm, "end": v(-50.65, 43.83) * mm});
            skLineSegment(sketch, "E1909", {"start": v(-50.65, 43.83) * mm, "end": v(-50.78, 43.88) * mm});
            skLineSegment(sketch, "E1910", {"start": v(-50.78, 43.88) * mm, "end": v(-50.93, 43.92) * mm});
            skLineSegment(sketch, "E1911", {"start": v(-50.93, 43.92) * mm, "end": v(-51.07, 43.97) * mm});
            skLineSegment(sketch, "E1912", {"start": v(-51.07, 43.97) * mm, "end": v(-51.21, 44.02) * mm});
            skLineSegment(sketch, "E1913", {"start": v(-51.21, 44.02) * mm, "end": v(-51.36, 44.06) * mm});
            skLineSegment(sketch, "E1914", {"start": v(-51.36, 44.06) * mm, "end": v(-51.51, 44.1) * mm});
            skLineSegment(sketch, "E1915", {"start": v(-51.51, 44.1) * mm, "end": v(-51.66, 44.16) * mm});
            skLineSegment(sketch, "E1916", {"start": v(-51.66, 44.16) * mm, "end": v(-51.82, 44.2) * mm});
            skLineSegment(sketch, "E1917", {"start": v(-51.82, 44.2) * mm, "end": v(-51.97, 44.25) * mm});
            skLineSegment(sketch, "E1918", {"start": v(-51.97, 44.25) * mm, "end": v(-52.09, 44.25) * mm});
            skLineSegment(sketch, "E1919", {"start": v(-52.09, 44.25) * mm, "end": v(-53.13, 43) * mm});
            skLineSegment(sketch, "E1920", {"start": v(-53.13, 43) * mm, "end": v(-53.1, 42.89) * mm});
            skLineSegment(sketch, "E1921", {"start": v(-53.1, 42.89) * mm, "end": v(-53.03, 42.74) * mm});
            skLineSegment(sketch, "E1922", {"start": v(-53.03, 42.74) * mm, "end": v(-52.95, 42.6) * mm});
            skLineSegment(sketch, "E1923", {"start": v(-52.95, 42.6) * mm, "end": v(-52.88, 42.46) * mm});
            skLineSegment(sketch, "E1924", {"start": v(-52.88, 42.46) * mm, "end": v(-52.8, 42.32) * mm});
            skLineSegment(sketch, "E1925", {"start": v(-52.8, 42.32) * mm, "end": v(-52.73, 42.18) * mm});
            skLineSegment(sketch, "E1926", {"start": v(-52.73, 42.18) * mm, "end": v(-52.66, 42.05) * mm});
            skLineSegment(sketch, "E1927", {"start": v(-52.66, 42.05) * mm, "end": v(-52.59, 41.92) * mm});
            skLineSegment(sketch, "E1928", {"start": v(-52.59, 41.92) * mm, "end": v(-52.52, 41.79) * mm});
            skLineSegment(sketch, "E1929", {"start": v(-52.52, 41.79) * mm, "end": v(-52.44, 41.66) * mm});
            skLineSegment(sketch, "E1930", {"start": v(-52.44, 41.66) * mm, "end": v(-52.37, 41.54) * mm});
            skLineSegment(sketch, "E1931", {"start": v(-52.37, 41.54) * mm, "end": v(-52.3, 41.41) * mm});
            skLineSegment(sketch, "E1932", {"start": v(-52.3, 41.41) * mm, "end": v(-52.23, 41.3) * mm});
            skLineSegment(sketch, "E1933", {"start": v(-52.23, 41.3) * mm, "end": v(-52.16, 41.17) * mm});
            skLineSegment(sketch, "E1934", {"start": v(-52.16, 41.17) * mm, "end": v(-52.09, 41.06) * mm});
            skLineSegment(sketch, "E1935", {"start": v(-52.09, 41.06) * mm, "end": v(-52.02, 40.94) * mm});
            skLineSegment(sketch, "E1936", {"start": v(-52.02, 40.94) * mm, "end": v(-51.95, 40.83) * mm});
            skLineSegment(sketch, "E1937", {"start": v(-51.95, 40.83) * mm, "end": v(-51.88, 40.72) * mm});
            skLineSegment(sketch, "E1938", {"start": v(-51.88, 40.72) * mm, "end": v(-51.81, 40.62) * mm});
            skLineSegment(sketch, "E1939", {"start": v(-51.81, 40.62) * mm, "end": v(-51.74, 40.51) * mm});
            skLineSegment(sketch, "E1940", {"start": v(-51.74, 40.51) * mm, "end": v(-51.68, 40.4) * mm});
            skLineSegment(sketch, "E1941", {"start": v(-51.68, 40.4) * mm, "end": v(-51.61, 40.3) * mm});
            skLineSegment(sketch, "E1942", {"start": v(-51.61, 40.3) * mm, "end": v(-51.54, 40.2) * mm});
            skLineSegment(sketch, "E1943", {"start": v(-51.54, 40.2) * mm, "end": v(-51.48, 40.11) * mm});
            skLineSegment(sketch, "E1944", {"start": v(-51.48, 40.11) * mm, "end": v(-51.41, 40.02) * mm});
            skLineSegment(sketch, "E1945", {"start": v(-51.41, 40.02) * mm, "end": v(-51.35, 39.92) * mm});
            skLineSegment(sketch, "E1946", {"start": v(-51.35, 39.92) * mm, "end": v(-51.29, 39.83) * mm});
            skLineSegment(sketch, "E1947", {"start": v(-51.29, 39.83) * mm, "end": v(-51.22, 39.75) * mm});
            skLineSegment(sketch, "E1948", {"start": v(-51.22, 39.75) * mm, "end": v(-51.16, 39.66) * mm});
            skLineSegment(sketch, "E1949", {"start": v(-51.16, 39.66) * mm, "end": v(-51.1, 39.58) * mm});
            skLineSegment(sketch, "E1950", {"start": v(-51.1, 39.58) * mm, "end": v(-51.04, 39.5) * mm});
            skLineSegment(sketch, "E1951", {"start": v(-51.04, 39.5) * mm, "end": v(-50.98, 39.41) * mm});
            skLineSegment(sketch, "E1952", {"start": v(-50.98, 39.41) * mm, "end": v(-50.92, 39.34) * mm});
            skLineSegment(sketch, "E1953", {"start": v(-50.92, 39.34) * mm, "end": v(-50.86, 39.26) * mm});
            skLineSegment(sketch, "E1954", {"start": v(-50.86, 39.26) * mm, "end": v(-50.8, 39.19) * mm});
            skLineSegment(sketch, "E1955", {"start": v(-50.8, 39.19) * mm, "end": v(-50.75, 39.11) * mm});
            skLineSegment(sketch, "E1956", {"start": v(-50.75, 39.11) * mm, "end": v(-50.7, 39.04) * mm});
            skLineSegment(sketch, "E1957", {"start": v(-50.7, 39.04) * mm, "end": v(-50.64, 38.98) * mm});
            skLineSegment(sketch, "E1958", {"start": v(-50.64, 38.98) * mm, "end": v(-50.58, 38.91) * mm});
            skLineSegment(sketch, "E1959", {"start": v(-50.58, 38.91) * mm, "end": v(-50.53, 38.85) * mm});
            skLineSegment(sketch, "E1960", {"start": v(-50.53, 38.85) * mm, "end": v(-50.58, 38.58) * mm});
            skLineSegment(sketch, "E1961", {"start": v(-50.58, 38.58) * mm, "end": v(-51.46, 37.39) * mm});
            skLineSegment(sketch, "E1962", {"start": v(-51.46, 37.39) * mm, "end": v(-51.7, 37.27) * mm});
            skLineSegment(sketch, "E1963", {"start": v(-51.7, 37.27) * mm, "end": v(-51.78, 37.3) * mm});
            skLineSegment(sketch, "E1964", {"start": v(-51.78, 37.3) * mm, "end": v(-51.86, 37.33) * mm});
            skLineSegment(sketch, "E1965", {"start": v(-51.86, 37.33) * mm, "end": v(-51.94, 37.37) * mm});
            skLineSegment(sketch, "E1966", {"start": v(-51.94, 37.37) * mm, "end": v(-52.02, 37.4) * mm});
            skLineSegment(sketch, "E1967", {"start": v(-52.02, 37.4) * mm, "end": v(-52.1, 37.43) * mm});
            skLineSegment(sketch, "E1968", {"start": v(-52.1, 37.43) * mm, "end": v(-52.2, 37.47) * mm});
            skLineSegment(sketch, "E1969", {"start": v(-52.2, 37.47) * mm, "end": v(-52.29, 37.5) * mm});
            skLineSegment(sketch, "E1970", {"start": v(-52.29, 37.5) * mm, "end": v(-52.38, 37.53) * mm});
            skLineSegment(sketch, "E1971", {"start": v(-52.38, 37.53) * mm, "end": v(-52.47, 37.57) * mm});
            skLineSegment(sketch, "E1972", {"start": v(-52.47, 37.57) * mm, "end": v(-52.57, 37.6) * mm});
            skLineSegment(sketch, "E1973", {"start": v(-52.57, 37.6) * mm, "end": v(-52.67, 37.64) * mm});
            skLineSegment(sketch, "E1974", {"start": v(-52.67, 37.64) * mm, "end": v(-52.77, 37.67) * mm});
            skLineSegment(sketch, "E1975", {"start": v(-52.77, 37.67) * mm, "end": v(-52.87, 37.7) * mm});
            skLineSegment(sketch, "E1976", {"start": v(-52.87, 37.7) * mm, "end": v(-52.97, 37.74) * mm});
            skLineSegment(sketch, "E1977", {"start": v(-52.97, 37.74) * mm, "end": v(-53.08, 37.78) * mm});
            skLineSegment(sketch, "E1978", {"start": v(-53.08, 37.78) * mm, "end": v(-53.19, 37.81) * mm});
            skLineSegment(sketch, "E1979", {"start": v(-53.19, 37.81) * mm, "end": v(-53.3, 37.85) * mm});
            skLineSegment(sketch, "E1980", {"start": v(-53.3, 37.85) * mm, "end": v(-53.41, 37.88) * mm});
            skLineSegment(sketch, "E1981", {"start": v(-53.41, 37.88) * mm, "end": v(-53.53, 37.92) * mm});
            skLineSegment(sketch, "E1982", {"start": v(-53.53, 37.92) * mm, "end": v(-53.65, 37.95) * mm});
            skLineSegment(sketch, "E1983", {"start": v(-53.65, 37.95) * mm, "end": v(-53.77, 37.99) * mm});
            skLineSegment(sketch, "E1984", {"start": v(-53.77, 37.99) * mm, "end": v(-53.9, 38.02) * mm});
            skLineSegment(sketch, "E1985", {"start": v(-53.9, 38.02) * mm, "end": v(-54.01, 38.06) * mm});
            skLineSegment(sketch, "E1986", {"start": v(-54.01, 38.06) * mm, "end": v(-54.27, 38.13) * mm});
            skLineSegment(sketch, "E1987", {"start": v(-54.27, 38.13) * mm, "end": v(-54.4, 38.16) * mm});
            skLineSegment(sketch, "E1988", {"start": v(-54.4, 38.16) * mm, "end": v(-54.54, 38.2) * mm});
            skLineSegment(sketch, "E1989", {"start": v(-54.54, 38.2) * mm, "end": v(-54.67, 38.23) * mm});
            skLineSegment(sketch, "E1990", {"start": v(-54.67, 38.23) * mm, "end": v(-54.81, 38.26) * mm});
            skLineSegment(sketch, "E1991", {"start": v(-54.81, 38.26) * mm, "end": v(-54.95, 38.3) * mm});
            skLineSegment(sketch, "E1992", {"start": v(-54.95, 38.3) * mm, "end": v(-55.1, 38.33) * mm});
            skLineSegment(sketch, "E1993", {"start": v(-55.1, 38.33) * mm, "end": v(-55.24, 38.36) * mm});
            skLineSegment(sketch, "E1994", {"start": v(-55.24, 38.36) * mm, "end": v(-55.38, 38.4) * mm});
            skLineSegment(sketch, "E1995", {"start": v(-55.38, 38.4) * mm, "end": v(-55.53, 38.42) * mm});
            skLineSegment(sketch, "E1996", {"start": v(-55.53, 38.42) * mm, "end": v(-55.69, 38.45) * mm});
            skLineSegment(sketch, "E1997", {"start": v(-55.69, 38.45) * mm, "end": v(-55.84, 38.48) * mm});
            skLineSegment(sketch, "E1998", {"start": v(-55.84, 38.48) * mm, "end": v(-56, 38.51) * mm});
            skLineSegment(sketch, "E1999", {"start": v(-56, 38.51) * mm, "end": v(-56.15, 38.54) * mm});
            skLineSegment(sketch, "E2000", {"start": v(-56.15, 38.54) * mm, "end": v(-56.31, 38.57) * mm});
            skLineSegment(sketch, "E2001", {"start": v(-56.31, 38.57) * mm, "end": v(-56.43, 38.57) * mm});
            skLineSegment(sketch, "E2002", {"start": v(-56.43, 38.57) * mm, "end": v(-57.33, 37.21) * mm});
            skLineSegment(sketch, "E2003", {"start": v(-57.33, 37.21) * mm, "end": v(-57.3, 37.1) * mm});
            skLineSegment(sketch, "E2004", {"start": v(-57.3, 37.1) * mm, "end": v(-57.2, 36.97) * mm});
            skLineSegment(sketch, "E2005", {"start": v(-57.2, 36.97) * mm, "end": v(-57.12, 36.83) * mm});
            skLineSegment(sketch, "E2006", {"start": v(-57.12, 36.83) * mm, "end": v(-57.03, 36.7) * mm});
            skLineSegment(sketch, "E2007", {"start": v(-57.03, 36.7) * mm, "end": v(-56.94, 36.57) * mm});
            skLineSegment(sketch, "E2008", {"start": v(-56.94, 36.57) * mm, "end": v(-56.85, 36.44) * mm});
            skLineSegment(sketch, "E2009", {"start": v(-56.85, 36.44) * mm, "end": v(-56.77, 36.32) * mm});
            skLineSegment(sketch, "E2010", {"start": v(-56.77, 36.32) * mm, "end": v(-56.68, 36.2) * mm});
            skLineSegment(sketch, "E2011", {"start": v(-56.68, 36.2) * mm, "end": v(-56.6, 36.07) * mm});
            skLineSegment(sketch, "E2012", {"start": v(-56.6, 36.07) * mm, "end": v(-56.51, 35.95) * mm});
            skLineSegment(sketch, "E2013", {"start": v(-56.51, 35.95) * mm, "end": v(-56.43, 35.83) * mm});
            skLineSegment(sketch, "E2014", {"start": v(-56.43, 35.83) * mm, "end": v(-56.34, 35.72) * mm});
            skLineSegment(sketch, "E2015", {"start": v(-56.34, 35.72) * mm, "end": v(-56.26, 35.6) * mm});
            skLineSegment(sketch, "E2016", {"start": v(-56.26, 35.6) * mm, "end": v(-56.18, 35.5) * mm});
            skLineSegment(sketch, "E2017", {"start": v(-56.18, 35.5) * mm, "end": v(-56.1, 35.39) * mm});
            skLineSegment(sketch, "E2018", {"start": v(-56.1, 35.39) * mm, "end": v(-56.01, 35.28) * mm});
            skLineSegment(sketch, "E2019", {"start": v(-56.01, 35.28) * mm, "end": v(-55.93, 35.18) * mm});
            skLineSegment(sketch, "E2020", {"start": v(-55.93, 35.18) * mm, "end": v(-55.85, 35.08) * mm});
            skLineSegment(sketch, "E2021", {"start": v(-55.85, 35.08) * mm, "end": v(-55.77, 34.98) * mm});
            skLineSegment(sketch, "E2022", {"start": v(-55.77, 34.98) * mm, "end": v(-55.62, 34.78) * mm});
            skLineSegment(sketch, "E2023", {"start": v(-55.62, 34.78) * mm, "end": v(-55.54, 34.7) * mm});
            skLineSegment(sketch, "E2024", {"start": v(-55.54, 34.7) * mm, "end": v(-55.46, 34.6) * mm});
            skLineSegment(sketch, "E2025", {"start": v(-55.46, 34.6) * mm, "end": v(-55.4, 34.51) * mm});
            skLineSegment(sketch, "E2026", {"start": v(-55.4, 34.51) * mm, "end": v(-55.31, 34.42) * mm});
            skLineSegment(sketch, "E2027", {"start": v(-55.31, 34.42) * mm, "end": v(-55.17, 34.26) * mm});
            skLineSegment(sketch, "E2028", {"start": v(-55.17, 34.26) * mm, "end": v(-55.1, 34.17) * mm});
            skLineSegment(sketch, "E2029", {"start": v(-55.1, 34.17) * mm, "end": v(-55.03, 34.1) * mm});
            skLineSegment(sketch, "E2030", {"start": v(-55.03, 34.1) * mm, "end": v(-54.96, 34.02) * mm});
            skLineSegment(sketch, "E2031", {"start": v(-54.96, 34.02) * mm, "end": v(-54.89, 33.94) * mm});
            skLineSegment(sketch, "E2032", {"start": v(-54.89, 33.94) * mm, "end": v(-54.82, 33.87) * mm});
            skLineSegment(sketch, "E2033", {"start": v(-54.82, 33.87) * mm, "end": v(-54.75, 33.8) * mm});
            skLineSegment(sketch, "E2034", {"start": v(-54.75, 33.8) * mm, "end": v(-54.69, 33.73) * mm});
            skLineSegment(sketch, "E2035", {"start": v(-54.69, 33.73) * mm, "end": v(-54.62, 33.66) * mm});
            skLineSegment(sketch, "E2036", {"start": v(-54.62, 33.66) * mm, "end": v(-54.56, 33.6) * mm});
            skLineSegment(sketch, "E2037", {"start": v(-54.56, 33.6) * mm, "end": v(-54.5, 33.53) * mm});
            skLineSegment(sketch, "E2038", {"start": v(-54.5, 33.53) * mm, "end": v(-54.37, 33.4) * mm});
            skLineSegment(sketch, "E2039", {"start": v(-54.37, 33.4) * mm, "end": v(-54.31, 33.35) * mm});
            skLineSegment(sketch, "E2040", {"start": v(-54.31, 33.35) * mm, "end": v(-54.33, 33.08) * mm});
            skLineSegment(sketch, "E2041", {"start": v(-54.33, 33.08) * mm, "end": v(-55.09, 31.8) * mm});
            skLineSegment(sketch, "E2042", {"start": v(-55.09, 31.8) * mm, "end": v(-55.32, 31.66) * mm});
            skLineSegment(sketch, "E2043", {"start": v(-55.32, 31.66) * mm, "end": v(-55.4, 31.68) * mm});
            skLineSegment(sketch, "E2044", {"start": v(-55.4, 31.68) * mm, "end": v(-55.48, 31.7) * mm});
            skLineSegment(sketch, "E2045", {"start": v(-55.48, 31.7) * mm, "end": v(-55.56, 31.73) * mm});
            skLineSegment(sketch, "E2046", {"start": v(-55.56, 31.73) * mm, "end": v(-55.65, 31.76) * mm});
            skLineSegment(sketch, "E2047", {"start": v(-55.65, 31.76) * mm, "end": v(-55.74, 31.78) * mm});
            skLineSegment(sketch, "E2048", {"start": v(-55.74, 31.78) * mm, "end": v(-55.83, 31.8) * mm});
            skLineSegment(sketch, "E2049", {"start": v(-55.83, 31.8) * mm, "end": v(-55.92, 31.83) * mm});
            skLineSegment(sketch, "E2050", {"start": v(-55.92, 31.83) * mm, "end": v(-56.01, 31.85) * mm});
            skLineSegment(sketch, "E2051", {"start": v(-56.01, 31.85) * mm, "end": v(-56.11, 31.88) * mm});
            skLineSegment(sketch, "E2052", {"start": v(-56.11, 31.88) * mm, "end": v(-56.21, 31.9) * mm});
            skLineSegment(sketch, "E2053", {"start": v(-56.21, 31.9) * mm, "end": v(-56.31, 31.93) * mm});
            skLineSegment(sketch, "E2054", {"start": v(-56.31, 31.93) * mm, "end": v(-56.42, 31.95) * mm});
            skLineSegment(sketch, "E2055", {"start": v(-56.42, 31.95) * mm, "end": v(-56.52, 31.98) * mm});
            skLineSegment(sketch, "E2056", {"start": v(-56.52, 31.98) * mm, "end": v(-56.74, 32.02) * mm});
            skLineSegment(sketch, "E2057", {"start": v(-56.74, 32.02) * mm, "end": v(-56.85, 32.05) * mm});
            skLineSegment(sketch, "E2058", {"start": v(-56.85, 32.05) * mm, "end": v(-56.97, 32.07) * mm});
            skLineSegment(sketch, "E2059", {"start": v(-56.97, 32.07) * mm, "end": v(-57.08, 32.1) * mm});
            skLineSegment(sketch, "E2060", {"start": v(-57.08, 32.1) * mm, "end": v(-57.2, 32.12) * mm});
            skLineSegment(sketch, "E2061", {"start": v(-57.2, 32.12) * mm, "end": v(-57.32, 32.14) * mm});
            skLineSegment(sketch, "E2062", {"start": v(-57.32, 32.14) * mm, "end": v(-57.44, 32.16) * mm});
            skLineSegment(sketch, "E2063", {"start": v(-57.44, 32.16) * mm, "end": v(-57.57, 32.18) * mm});
            skLineSegment(sketch, "E2064", {"start": v(-57.57, 32.18) * mm, "end": v(-57.7, 32.2) * mm});
            skLineSegment(sketch, "E2065", {"start": v(-57.7, 32.2) * mm, "end": v(-57.83, 32.22) * mm});
            skLineSegment(sketch, "E2066", {"start": v(-57.83, 32.22) * mm, "end": v(-57.96, 32.24) * mm});
            skLineSegment(sketch, "E2067", {"start": v(-57.96, 32.24) * mm, "end": v(-58.1, 32.27) * mm});
            skLineSegment(sketch, "E2068", {"start": v(-58.1, 32.27) * mm, "end": v(-58.23, 32.28) * mm});
            skLineSegment(sketch, "E2069", {"start": v(-58.23, 32.28) * mm, "end": v(-58.37, 32.3) * mm});
            skLineSegment(sketch, "E2070", {"start": v(-58.37, 32.3) * mm, "end": v(-58.51, 32.32) * mm});
            skLineSegment(sketch, "E2071", {"start": v(-58.51, 32.32) * mm, "end": v(-58.65, 32.34) * mm});
            skLineSegment(sketch, "E2072", {"start": v(-58.65, 32.34) * mm, "end": v(-58.8, 32.36) * mm});
            skLineSegment(sketch, "E2073", {"start": v(-58.8, 32.36) * mm, "end": v(-58.95, 32.37) * mm});
            skLineSegment(sketch, "E2074", {"start": v(-58.95, 32.37) * mm, "end": v(-59.1, 32.4) * mm});
            skLineSegment(sketch, "E2075", {"start": v(-59.1, 32.4) * mm, "end": v(-59.25, 32.4) * mm});
            skLineSegment(sketch, "E2076", {"start": v(-59.25, 32.4) * mm, "end": v(-59.4, 32.42) * mm});
            skLineSegment(sketch, "E2077", {"start": v(-59.4, 32.42) * mm, "end": v(-59.56, 32.43) * mm});
            skLineSegment(sketch, "E2078", {"start": v(-59.56, 32.43) * mm, "end": v(-59.71, 32.45) * mm});
            skLineSegment(sketch, "E2079", {"start": v(-59.71, 32.45) * mm, "end": v(-59.88, 32.46) * mm});
            skLineSegment(sketch, "E2080", {"start": v(-59.88, 32.46) * mm, "end": v(-60.04, 32.47) * mm});
            skLineSegment(sketch, "E2081", {"start": v(-60.04, 32.47) * mm, "end": v(-60.15, 32.46) * mm});
            skLineSegment(sketch, "E2082", {"start": v(-60.15, 32.46) * mm, "end": v(-60.9, 31.02) * mm});
            skLineSegment(sketch, "E2083", {"start": v(-60.9, 31.02) * mm, "end": v(-60.86, 30.91) * mm});
            skLineSegment(sketch, "E2084", {"start": v(-60.86, 30.91) * mm, "end": v(-60.75, 30.78) * mm});
            skLineSegment(sketch, "E2085", {"start": v(-60.75, 30.78) * mm, "end": v(-60.65, 30.66) * mm});
            skLineSegment(sketch, "E2086", {"start": v(-60.65, 30.66) * mm, "end": v(-60.55, 30.54) * mm});
            skLineSegment(sketch, "E2087", {"start": v(-60.55, 30.54) * mm, "end": v(-60.45, 30.42) * mm});
            skLineSegment(sketch, "E2088", {"start": v(-60.45, 30.42) * mm, "end": v(-60.35, 30.3) * mm});
            skLineSegment(sketch, "E2089", {"start": v(-60.35, 30.3) * mm, "end": v(-60.25, 30.18) * mm});
            skLineSegment(sketch, "E2090", {"start": v(-60.25, 30.18) * mm, "end": v(-60.15, 30.07) * mm});
            skLineSegment(sketch, "E2091", {"start": v(-60.15, 30.07) * mm, "end": v(-60.06, 29.96) * mm});
            skLineSegment(sketch, "E2092", {"start": v(-60.06, 29.96) * mm, "end": v(-59.96, 29.85) * mm});
            skLineSegment(sketch, "E2093", {"start": v(-59.96, 29.85) * mm, "end": v(-59.86, 29.74) * mm});
            skLineSegment(sketch, "E2094", {"start": v(-59.86, 29.74) * mm, "end": v(-59.77, 29.63) * mm});
            skLineSegment(sketch, "E2095", {"start": v(-59.77, 29.63) * mm, "end": v(-59.67, 29.53) * mm});
            skLineSegment(sketch, "E2096", {"start": v(-59.67, 29.53) * mm, "end": v(-59.58, 29.43) * mm});
            skLineSegment(sketch, "E2097", {"start": v(-59.58, 29.43) * mm, "end": v(-59.49, 29.33) * mm});
            skLineSegment(sketch, "E2098", {"start": v(-59.49, 29.33) * mm, "end": v(-59.4, 29.23) * mm});
            skLineSegment(sketch, "E2099", {"start": v(-59.4, 29.23) * mm, "end": v(-59.3, 29.14) * mm});
            skLineSegment(sketch, "E2100", {"start": v(-59.3, 29.14) * mm, "end": v(-59.21, 29.05) * mm});
            skLineSegment(sketch, "E2101", {"start": v(-59.21, 29.05) * mm, "end": v(-59.12, 28.96) * mm});
            skLineSegment(sketch, "E2102", {"start": v(-59.12, 28.96) * mm, "end": v(-59.04, 28.87) * mm});
            skLineSegment(sketch, "E2103", {"start": v(-59.04, 28.87) * mm, "end": v(-58.95, 28.78) * mm});
            skLineSegment(sketch, "E2104", {"start": v(-58.95, 28.78) * mm, "end": v(-58.86, 28.7) * mm});
            skLineSegment(sketch, "E2105", {"start": v(-58.86, 28.7) * mm, "end": v(-58.78, 28.61) * mm});
            skLineSegment(sketch, "E2106", {"start": v(-58.78, 28.61) * mm, "end": v(-58.7, 28.53) * mm});
            skLineSegment(sketch, "E2107", {"start": v(-58.7, 28.53) * mm, "end": v(-58.61, 28.45) * mm});
            skLineSegment(sketch, "E2108", {"start": v(-58.61, 28.45) * mm, "end": v(-58.53, 28.38) * mm});
            skLineSegment(sketch, "E2109", {"start": v(-58.53, 28.38) * mm, "end": v(-58.45, 28.3) * mm});
            skLineSegment(sketch, "E2110", {"start": v(-58.45, 28.3) * mm, "end": v(-58.37, 28.23) * mm});
            skLineSegment(sketch, "E2111", {"start": v(-58.37, 28.23) * mm, "end": v(-58.29, 28.16) * mm});
            skLineSegment(sketch, "E2112", {"start": v(-58.29, 28.16) * mm, "end": v(-58.21, 28.09) * mm});
            skLineSegment(sketch, "E2113", {"start": v(-58.21, 28.09) * mm, "end": v(-58.14, 28.02) * mm});
            skLineSegment(sketch, "E2114", {"start": v(-58.14, 28.02) * mm, "end": v(-58.06, 27.95) * mm});
            skLineSegment(sketch, "E2115", {"start": v(-58.06, 27.95) * mm, "end": v(-57.99, 27.9) * mm});
            skLineSegment(sketch, "E2116", {"start": v(-57.99, 27.9) * mm, "end": v(-57.91, 27.83) * mm});
            skLineSegment(sketch, "E2117", {"start": v(-57.91, 27.83) * mm, "end": v(-57.84, 27.77) * mm});
            skLineSegment(sketch, "E2118", {"start": v(-57.84, 27.77) * mm, "end": v(-57.77, 27.7) * mm});
            skLineSegment(sketch, "E2119", {"start": v(-57.77, 27.7) * mm, "end": v(-57.7, 27.65) * mm});
            skLineSegment(sketch, "E2120", {"start": v(-57.7, 27.65) * mm, "end": v(-57.63, 27.6) * mm});
            skLineSegment(sketch, "E2121", {"start": v(-57.63, 27.6) * mm, "end": v(-57.57, 27.54) * mm});
            skLineSegment(sketch, "E2122", {"start": v(-57.57, 27.54) * mm, "end": v(-57.5, 27.5) * mm});
            skLineSegment(sketch, "E2123", {"start": v(-57.5, 27.5) * mm, "end": v(-57.5, 27.22) * mm});
            skLineSegment(sketch, "E2124", {"start": v(-57.5, 27.22) * mm, "end": v(-58.11, 25.87) * mm});
            skLineSegment(sketch, "E2125", {"start": v(-58.11, 25.87) * mm, "end": v(-58.32, 25.7) * mm});
            skLineSegment(sketch, "E2126", {"start": v(-58.32, 25.7) * mm, "end": v(-58.4, 25.72) * mm});
            skLineSegment(sketch, "E2127", {"start": v(-58.4, 25.72) * mm, "end": v(-58.49, 25.73) * mm});
            skLineSegment(sketch, "E2128", {"start": v(-58.49, 25.73) * mm, "end": v(-58.57, 25.75) * mm});
            skLineSegment(sketch, "E2129", {"start": v(-58.57, 25.75) * mm, "end": v(-58.66, 25.77) * mm});
            skLineSegment(sketch, "E2130", {"start": v(-58.66, 25.77) * mm, "end": v(-58.75, 25.78) * mm});
            skLineSegment(sketch, "E2131", {"start": v(-58.75, 25.78) * mm, "end": v(-58.85, 25.8) * mm});
            skLineSegment(sketch, "E2132", {"start": v(-58.85, 25.8) * mm, "end": v(-58.94, 25.81) * mm});
            skLineSegment(sketch, "E2133", {"start": v(-58.94, 25.81) * mm, "end": v(-59.04, 25.82) * mm});
            skLineSegment(sketch, "E2134", {"start": v(-59.04, 25.82) * mm, "end": v(-59.14, 25.84) * mm});
            skLineSegment(sketch, "E2135", {"start": v(-59.14, 25.84) * mm, "end": v(-59.24, 25.85) * mm});
            skLineSegment(sketch, "E2136", {"start": v(-59.24, 25.85) * mm, "end": v(-59.34, 25.87) * mm});
            skLineSegment(sketch, "E2137", {"start": v(-59.34, 25.87) * mm, "end": v(-59.45, 25.88) * mm});
            skLineSegment(sketch, "E2138", {"start": v(-59.45, 25.88) * mm, "end": v(-59.55, 25.9) * mm});
            skLineSegment(sketch, "E2139", {"start": v(-59.55, 25.9) * mm, "end": v(-59.66, 25.9) * mm});
            skLineSegment(sketch, "E2140", {"start": v(-59.66, 25.9) * mm, "end": v(-59.78, 25.92) * mm});
            skLineSegment(sketch, "E2141", {"start": v(-59.78, 25.92) * mm, "end": v(-59.89, 25.93) * mm});
            skLineSegment(sketch, "E2142", {"start": v(-59.89, 25.93) * mm, "end": v(-60, 25.94) * mm});
            skLineSegment(sketch, "E2143", {"start": v(-60, 25.94) * mm, "end": v(-60.12, 25.95) * mm});
            skLineSegment(sketch, "E2144", {"start": v(-60.12, 25.95) * mm, "end": v(-60.24, 25.96) * mm});
            skLineSegment(sketch, "E2145", {"start": v(-60.24, 25.96) * mm, "end": v(-60.37, 25.97) * mm});
            skLineSegment(sketch, "E2146", {"start": v(-60.37, 25.97) * mm, "end": v(-60.5, 25.98) * mm});
            skLineSegment(sketch, "E2147", {"start": v(-60.5, 25.98) * mm, "end": v(-60.62, 25.99) * mm});
            skLineSegment(sketch, "E2148", {"start": v(-60.62, 25.99) * mm, "end": v(-60.75, 26) * mm});
            skLineSegment(sketch, "E2149", {"start": v(-60.75, 26) * mm, "end": v(-60.88, 26) * mm});
            skLineSegment(sketch, "E2150", {"start": v(-60.88, 26) * mm, "end": v(-61.01, 26.01) * mm});
            skLineSegment(sketch, "E2151", {"start": v(-61.01, 26.01) * mm, "end": v(-61.15, 26.02) * mm});
            skLineSegment(sketch, "E2152", {"start": v(-61.15, 26.02) * mm, "end": v(-61.29, 26.02) * mm});
            skLineSegment(sketch, "E2153", {"start": v(-61.29, 26.02) * mm, "end": v(-61.43, 26.03) * mm});
            skLineSegment(sketch, "E2154", {"start": v(-61.43, 26.03) * mm, "end": v(-61.57, 26.03) * mm});
            skLineSegment(sketch, "E2155", {"start": v(-61.57, 26.03) * mm, "end": v(-61.71, 26.03) * mm});
            skLineSegment(sketch, "E2156", {"start": v(-61.71, 26.03) * mm, "end": v(-61.86, 26.03) * mm});
            skLineSegment(sketch, "E2157", {"start": v(-61.86, 26.03) * mm, "end": v(-62, 26.04) * mm});
            skLineSegment(sketch, "E2158", {"start": v(-62, 26.04) * mm, "end": v(-62.16, 26.04) * mm});
            skLineSegment(sketch, "E2159", {"start": v(-62.16, 26.04) * mm, "end": v(-62.3, 26.04) * mm});
            skLineSegment(sketch, "E2160", {"start": v(-62.3, 26.04) * mm, "end": v(-62.46, 26.03) * mm});
            skLineSegment(sketch, "E2161", {"start": v(-62.46, 26.03) * mm, "end": v(-62.62, 26.03) * mm});
            skLineSegment(sketch, "E2162", {"start": v(-62.62, 26.03) * mm, "end": v(-62.78, 26.03) * mm});
            skLineSegment(sketch, "E2163", {"start": v(-62.78, 26.03) * mm, "end": v(-62.94, 26.02) * mm});
            skLineSegment(sketch, "E2164", {"start": v(-62.94, 26.02) * mm, "end": v(-63.1, 26.02) * mm});
            skLineSegment(sketch, "E2165", {"start": v(-63.1, 26.02) * mm, "end": v(-63.22, 26) * mm});
            skLineSegment(sketch, "E2166", {"start": v(-63.22, 26) * mm, "end": v(-63.82, 24.48) * mm});
            skLineSegment(sketch, "E2167", {"start": v(-63.82, 24.48) * mm, "end": v(-63.75, 24.38) * mm});
            skLineSegment(sketch, "E2168", {"start": v(-63.75, 24.38) * mm, "end": v(-63.64, 24.26) * mm});
            skLineSegment(sketch, "E2169", {"start": v(-63.64, 24.26) * mm, "end": v(-63.52, 24.15) * mm});
            skLineSegment(sketch, "E2170", {"start": v(-63.52, 24.15) * mm, "end": v(-63.41, 24.04) * mm});
            skLineSegment(sketch, "E2171", {"start": v(-63.41, 24.04) * mm, "end": v(-63.3, 23.93) * mm});
            skLineSegment(sketch, "E2172", {"start": v(-63.3, 23.93) * mm, "end": v(-63.19, 23.82) * mm});
            skLineSegment(sketch, "E2173", {"start": v(-63.19, 23.82) * mm, "end": v(-63.08, 23.72) * mm});
            skLineSegment(sketch, "E2174", {"start": v(-63.08, 23.72) * mm, "end": v(-62.97, 23.62) * mm});
            skLineSegment(sketch, "E2175", {"start": v(-62.97, 23.62) * mm, "end": v(-62.86, 23.51) * mm});
            skLineSegment(sketch, "E2176", {"start": v(-62.86, 23.51) * mm, "end": v(-62.64, 23.32) * mm});
            skLineSegment(sketch, "E2177", {"start": v(-62.64, 23.32) * mm, "end": v(-62.54, 23.23) * mm});
            skLineSegment(sketch, "E2178", {"start": v(-62.54, 23.23) * mm, "end": v(-62.43, 23.13) * mm});
            skLineSegment(sketch, "E2179", {"start": v(-62.43, 23.13) * mm, "end": v(-62.23, 22.95) * mm});
            skLineSegment(sketch, "E2180", {"start": v(-62.23, 22.95) * mm, "end": v(-62.13, 22.87) * mm});
            skLineSegment(sketch, "E2181", {"start": v(-62.13, 22.87) * mm, "end": v(-62.03, 22.78) * mm});
            skLineSegment(sketch, "E2182", {"start": v(-62.03, 22.78) * mm, "end": v(-61.93, 22.7) * mm});
            skLineSegment(sketch, "E2183", {"start": v(-61.93, 22.7) * mm, "end": v(-61.83, 22.62) * mm});
            skLineSegment(sketch, "E2184", {"start": v(-61.83, 22.62) * mm, "end": v(-61.73, 22.54) * mm});
            skLineSegment(sketch, "E2185", {"start": v(-61.73, 22.54) * mm, "end": v(-61.63, 22.46) * mm});
            skLineSegment(sketch, "E2186", {"start": v(-61.63, 22.46) * mm, "end": v(-61.45, 22.31) * mm});
            skLineSegment(sketch, "E2187", {"start": v(-61.45, 22.31) * mm, "end": v(-61.35, 22.24) * mm});
            skLineSegment(sketch, "E2188", {"start": v(-61.35, 22.24) * mm, "end": v(-61.26, 22.17) * mm});
            skLineSegment(sketch, "E2189", {"start": v(-61.26, 22.17) * mm, "end": v(-61.17, 22.1) * mm});
            skLineSegment(sketch, "E2190", {"start": v(-61.17, 22.1) * mm, "end": v(-61.09, 22.04) * mm});
            skLineSegment(sketch, "E2191", {"start": v(-61.09, 22.04) * mm, "end": v(-60.91, 21.9) * mm});
            skLineSegment(sketch, "E2192", {"start": v(-60.91, 21.9) * mm, "end": v(-60.83, 21.85) * mm});
            skLineSegment(sketch, "E2193", {"start": v(-60.83, 21.85) * mm, "end": v(-60.75, 21.79) * mm});
            skLineSegment(sketch, "E2194", {"start": v(-60.75, 21.79) * mm, "end": v(-60.66, 21.73) * mm});
            skLineSegment(sketch, "E2195", {"start": v(-60.66, 21.73) * mm, "end": v(-60.58, 21.68) * mm});
            skLineSegment(sketch, "E2196", {"start": v(-60.58, 21.68) * mm, "end": v(-60.5, 21.62) * mm});
            skLineSegment(sketch, "E2197", {"start": v(-60.5, 21.62) * mm, "end": v(-60.43, 21.57) * mm});
            skLineSegment(sketch, "E2198", {"start": v(-60.43, 21.57) * mm, "end": v(-60.35, 21.52) * mm});
            skLineSegment(sketch, "E2199", {"start": v(-60.35, 21.52) * mm, "end": v(-60.28, 21.47) * mm});
            skLineSegment(sketch, "E2200", {"start": v(-60.28, 21.47) * mm, "end": v(-60.2, 21.42) * mm});
            skLineSegment(sketch, "E2201", {"start": v(-60.2, 21.42) * mm, "end": v(-60.13, 21.37) * mm});
            skLineSegment(sketch, "E2202", {"start": v(-60.13, 21.37) * mm, "end": v(-60.06, 21.33) * mm});
            skLineSegment(sketch, "E2203", {"start": v(-60.06, 21.33) * mm, "end": v(-60.02, 21.06) * mm});
            skLineSegment(sketch, "E2204", {"start": v(-60.02, 21.06) * mm, "end": v(-60.5, 19.66) * mm});
            skLineSegment(sketch, "E2205", {"start": v(-60.5, 19.66) * mm, "end": v(-60.7, 19.47) * mm});
            skLineSegment(sketch, "E2206", {"start": v(-60.7, 19.47) * mm, "end": v(-60.77, 19.47) * mm});
            skLineSegment(sketch, "E2207", {"start": v(-60.77, 19.47) * mm, "end": v(-60.86, 19.48) * mm});
            skLineSegment(sketch, "E2208", {"start": v(-60.86, 19.48) * mm, "end": v(-60.95, 19.49) * mm});
            skLineSegment(sketch, "E2209", {"start": v(-60.95, 19.49) * mm, "end": v(-61.03, 19.5) * mm});
            skLineSegment(sketch, "E2210", {"start": v(-61.03, 19.5) * mm, "end": v(-61.22, 19.5) * mm});
            skLineSegment(sketch, "E2211", {"start": v(-61.22, 19.5) * mm, "end": v(-61.32, 19.5) * mm});
            skLineSegment(sketch, "E2212", {"start": v(-61.32, 19.5) * mm, "end": v(-61.41, 19.51) * mm});
            skLineSegment(sketch, "E2213", {"start": v(-61.41, 19.51) * mm, "end": v(-61.51, 19.52) * mm});
            skLineSegment(sketch, "E2214", {"start": v(-61.51, 19.52) * mm, "end": v(-61.61, 19.52) * mm});
            skLineSegment(sketch, "E2215", {"start": v(-61.61, 19.52) * mm, "end": v(-61.72, 19.52) * mm});
            skLineSegment(sketch, "E2216", {"start": v(-61.72, 19.52) * mm, "end": v(-61.83, 19.52) * mm});
            skLineSegment(sketch, "E2217", {"start": v(-61.83, 19.52) * mm, "end": v(-61.93, 19.53) * mm});
            skLineSegment(sketch, "E2218", {"start": v(-61.93, 19.53) * mm, "end": v(-62.04, 19.53) * mm});
            skLineSegment(sketch, "E2219", {"start": v(-62.04, 19.53) * mm, "end": v(-62.27, 19.53) * mm});
            skLineSegment(sketch, "E2220", {"start": v(-62.27, 19.53) * mm, "end": v(-62.39, 19.53) * mm});
            skLineSegment(sketch, "E2221", {"start": v(-62.39, 19.53) * mm, "end": v(-62.5, 19.52) * mm});
            skLineSegment(sketch, "E2222", {"start": v(-62.5, 19.52) * mm, "end": v(-62.63, 19.52) * mm});
            skLineSegment(sketch, "E2223", {"start": v(-62.63, 19.52) * mm, "end": v(-62.75, 19.52) * mm});
            skLineSegment(sketch, "E2224", {"start": v(-62.75, 19.52) * mm, "end": v(-62.88, 19.51) * mm});
            skLineSegment(sketch, "E2225", {"start": v(-62.88, 19.51) * mm, "end": v(-63.13, 19.5) * mm});
            skLineSegment(sketch, "E2226", {"start": v(-63.13, 19.5) * mm, "end": v(-63.26, 19.5) * mm});
            skLineSegment(sketch, "E2227", {"start": v(-63.26, 19.5) * mm, "end": v(-63.4, 19.49) * mm});
            skLineSegment(sketch, "E2228", {"start": v(-63.4, 19.49) * mm, "end": v(-63.67, 19.47) * mm});
            skLineSegment(sketch, "E2229", {"start": v(-63.67, 19.47) * mm, "end": v(-63.95, 19.45) * mm});
            skLineSegment(sketch, "E2230", {"start": v(-63.95, 19.45) * mm, "end": v(-64.24, 19.43) * mm});
            skLineSegment(sketch, "E2231", {"start": v(-64.24, 19.43) * mm, "end": v(-64.39, 19.41) * mm});
            skLineSegment(sketch, "E2232", {"start": v(-64.39, 19.41) * mm, "end": v(-64.54, 19.4) * mm});
            skLineSegment(sketch, "E2233", {"start": v(-64.54, 19.4) * mm, "end": v(-64.69, 19.38) * mm});
            skLineSegment(sketch, "E2234", {"start": v(-64.69, 19.38) * mm, "end": v(-64.84, 19.36) * mm});
            skLineSegment(sketch, "E2235", {"start": v(-64.84, 19.36) * mm, "end": v(-65, 19.34) * mm});
            skLineSegment(sketch, "E2236", {"start": v(-65, 19.34) * mm, "end": v(-65.16, 19.32) * mm});
            skLineSegment(sketch, "E2237", {"start": v(-65.16, 19.32) * mm, "end": v(-65.32, 19.3) * mm});
            skLineSegment(sketch, "E2238", {"start": v(-65.32, 19.3) * mm, "end": v(-65.48, 19.28) * mm});
            skLineSegment(sketch, "E2239", {"start": v(-65.48, 19.28) * mm, "end": v(-65.59, 19.24) * mm});
            skLineSegment(sketch, "E2240", {"start": v(-65.59, 19.24) * mm, "end": v(-66.03, 17.67) * mm});
            skLineSegment(sketch, "E2241", {"start": v(-66.03, 17.67) * mm, "end": v(-65.95, 17.58) * mm});
            skLineSegment(sketch, "E2242", {"start": v(-65.95, 17.58) * mm, "end": v(-65.7, 17.38) * mm});
            skLineSegment(sketch, "E2243", {"start": v(-65.7, 17.38) * mm, "end": v(-65.45, 17.18) * mm});
            skLineSegment(sketch, "E2244", {"start": v(-65.45, 17.18) * mm, "end": v(-65.21, 17) * mm});
            skLineSegment(sketch, "E2245", {"start": v(-65.21, 17) * mm, "end": v(-65.1, 16.9) * mm});
            skLineSegment(sketch, "E2246", {"start": v(-65.1, 16.9) * mm, "end": v(-64.97, 16.82) * mm});
            skLineSegment(sketch, "E2247", {"start": v(-64.97, 16.82) * mm, "end": v(-64.85, 16.73) * mm});
            skLineSegment(sketch, "E2248", {"start": v(-64.85, 16.73) * mm, "end": v(-64.74, 16.64) * mm});
            skLineSegment(sketch, "E2249", {"start": v(-64.74, 16.64) * mm, "end": v(-64.62, 16.56) * mm});
            skLineSegment(sketch, "E2250", {"start": v(-64.62, 16.56) * mm, "end": v(-64.51, 16.48) * mm});
            skLineSegment(sketch, "E2251", {"start": v(-64.51, 16.48) * mm, "end": v(-64.4, 16.4) * mm});
            skLineSegment(sketch, "E2252", {"start": v(-64.4, 16.4) * mm, "end": v(-64.29, 16.32) * mm});
            skLineSegment(sketch, "E2253", {"start": v(-64.29, 16.32) * mm, "end": v(-64.18, 16.25) * mm});
            skLineSegment(sketch, "E2254", {"start": v(-64.18, 16.25) * mm, "end": v(-64.07, 16.17) * mm});
            skLineSegment(sketch, "E2255", {"start": v(-64.07, 16.17) * mm, "end": v(-63.96, 16.1) * mm});
            skLineSegment(sketch, "E2256", {"start": v(-63.96, 16.1) * mm, "end": v(-63.85, 16.03) * mm});
            skLineSegment(sketch, "E2257", {"start": v(-63.85, 16.03) * mm, "end": v(-63.75, 15.96) * mm});
            skLineSegment(sketch, "E2258", {"start": v(-63.75, 15.96) * mm, "end": v(-63.64, 15.9) * mm});
            skLineSegment(sketch, "E2259", {"start": v(-63.64, 15.9) * mm, "end": v(-63.54, 15.83) * mm});
            skLineSegment(sketch, "E2260", {"start": v(-63.54, 15.83) * mm, "end": v(-63.44, 15.77) * mm});
            skLineSegment(sketch, "E2261", {"start": v(-63.44, 15.77) * mm, "end": v(-63.34, 15.7) * mm});
            skLineSegment(sketch, "E2262", {"start": v(-63.34, 15.7) * mm, "end": v(-63.25, 15.65) * mm});
            skLineSegment(sketch, "E2263", {"start": v(-63.25, 15.65) * mm, "end": v(-63.15, 15.59) * mm});
            skLineSegment(sketch, "E2264", {"start": v(-63.15, 15.59) * mm, "end": v(-63.05, 15.53) * mm});
            skLineSegment(sketch, "E2265", {"start": v(-63.05, 15.53) * mm, "end": v(-62.96, 15.48) * mm});
            skLineSegment(sketch, "E2266", {"start": v(-62.96, 15.48) * mm, "end": v(-62.87, 15.42) * mm});
            skLineSegment(sketch, "E2267", {"start": v(-62.87, 15.42) * mm, "end": v(-62.78, 15.37) * mm});
            skLineSegment(sketch, "E2268", {"start": v(-62.78, 15.37) * mm, "end": v(-62.69, 15.32) * mm});
            skLineSegment(sketch, "E2269", {"start": v(-62.69, 15.32) * mm, "end": v(-62.6, 15.27) * mm});
            skLineSegment(sketch, "E2270", {"start": v(-62.6, 15.27) * mm, "end": v(-62.52, 15.22) * mm});
            skLineSegment(sketch, "E2271", {"start": v(-62.52, 15.22) * mm, "end": v(-62.43, 15.18) * mm});
            skLineSegment(sketch, "E2272", {"start": v(-62.43, 15.18) * mm, "end": v(-62.35, 15.13) * mm});
            skLineSegment(sketch, "E2273", {"start": v(-62.35, 15.13) * mm, "end": v(-62.27, 15.1) * mm});
            skLineSegment(sketch, "E2274", {"start": v(-62.27, 15.1) * mm, "end": v(-62.19, 15.05) * mm});
            skLineSegment(sketch, "E2275", {"start": v(-62.19, 15.05) * mm, "end": v(-62.11, 15.01) * mm});
            skLineSegment(sketch, "E2276", {"start": v(-62.11, 15.01) * mm, "end": v(-62.04, 14.97) * mm});
            skLineSegment(sketch, "E2277", {"start": v(-62.04, 14.97) * mm, "end": v(-61.96, 14.94) * mm});
            skLineSegment(sketch, "E2278", {"start": v(-61.96, 14.94) * mm, "end": v(-61.9, 14.67) * mm});
            skLineSegment(sketch, "E2279", {"start": v(-61.9, 14.67) * mm, "end": v(-62.22, 13.22) * mm});
            skLineSegment(sketch, "E2280", {"start": v(-62.22, 13.22) * mm, "end": v(-62.4, 13.02) * mm});
            skLineSegment(sketch, "E2281", {"start": v(-62.4, 13.02) * mm, "end": v(-62.48, 13.01) * mm});
            skLineSegment(sketch, "E2282", {"start": v(-62.48, 13.01) * mm, "end": v(-62.56, 13.01) * mm});
            skLineSegment(sketch, "E2283", {"start": v(-62.56, 13.01) * mm, "end": v(-62.65, 13) * mm});
            skLineSegment(sketch, "E2284", {"start": v(-62.65, 13) * mm, "end": v(-62.74, 13) * mm});
            skLineSegment(sketch, "E2285", {"start": v(-62.74, 13) * mm, "end": v(-62.92, 13) * mm});
            skLineSegment(sketch, "E2286", {"start": v(-62.92, 13) * mm, "end": v(-63.02, 13) * mm});
            skLineSegment(sketch, "E2287", {"start": v(-63.02, 13) * mm, "end": v(-63.12, 12.99) * mm});
            skLineSegment(sketch, "E2288", {"start": v(-63.12, 12.99) * mm, "end": v(-63.22, 12.98) * mm});
            skLineSegment(sketch, "E2289", {"start": v(-63.22, 12.98) * mm, "end": v(-63.32, 12.97) * mm});
            skLineSegment(sketch, "E2290", {"start": v(-63.32, 12.97) * mm, "end": v(-63.42, 12.96) * mm});
            skLineSegment(sketch, "E2291", {"start": v(-63.42, 12.96) * mm, "end": v(-63.53, 12.96) * mm});
            skLineSegment(sketch, "E2292", {"start": v(-63.53, 12.96) * mm, "end": v(-63.64, 12.95) * mm});
            skLineSegment(sketch, "E2293", {"start": v(-63.64, 12.95) * mm, "end": v(-63.75, 12.93) * mm});
            skLineSegment(sketch, "E2294", {"start": v(-63.75, 12.93) * mm, "end": v(-63.86, 12.92) * mm});
            skLineSegment(sketch, "E2295", {"start": v(-63.86, 12.92) * mm, "end": v(-63.97, 12.91) * mm});
            skLineSegment(sketch, "E2296", {"start": v(-63.97, 12.91) * mm, "end": v(-64.09, 12.9) * mm});
            skLineSegment(sketch, "E2297", {"start": v(-64.09, 12.9) * mm, "end": v(-64.2, 12.88) * mm});
            skLineSegment(sketch, "E2298", {"start": v(-64.2, 12.88) * mm, "end": v(-64.33, 12.87) * mm});
            skLineSegment(sketch, "E2299", {"start": v(-64.33, 12.87) * mm, "end": v(-64.45, 12.85) * mm});
            skLineSegment(sketch, "E2300", {"start": v(-64.45, 12.85) * mm, "end": v(-64.57, 12.84) * mm});
            skLineSegment(sketch, "E2301", {"start": v(-64.57, 12.84) * mm, "end": v(-64.7, 12.82) * mm});
            skLineSegment(sketch, "E2302", {"start": v(-64.7, 12.82) * mm, "end": v(-64.83, 12.8) * mm});
            skLineSegment(sketch, "E2303", {"start": v(-64.83, 12.8) * mm, "end": v(-64.96, 12.78) * mm});
            skLineSegment(sketch, "E2304", {"start": v(-64.96, 12.78) * mm, "end": v(-65.09, 12.76) * mm});
            skLineSegment(sketch, "E2305", {"start": v(-65.09, 12.76) * mm, "end": v(-65.22, 12.73) * mm});
            skLineSegment(sketch, "E2306", {"start": v(-65.22, 12.73) * mm, "end": v(-65.36, 12.71) * mm});
            skLineSegment(sketch, "E2307", {"start": v(-65.36, 12.71) * mm, "end": v(-65.5, 12.69) * mm});
            skLineSegment(sketch, "E2308", {"start": v(-65.5, 12.69) * mm, "end": v(-65.63, 12.66) * mm});
            skLineSegment(sketch, "E2309", {"start": v(-65.63, 12.66) * mm, "end": v(-65.78, 12.63) * mm});
            skLineSegment(sketch, "E2310", {"start": v(-65.78, 12.63) * mm, "end": v(-65.92, 12.6) * mm});
            skLineSegment(sketch, "E2311", {"start": v(-65.92, 12.6) * mm, "end": v(-66.06, 12.57) * mm});
            skLineSegment(sketch, "E2312", {"start": v(-66.06, 12.57) * mm, "end": v(-66.21, 12.54) * mm});
            skLineSegment(sketch, "E2313", {"start": v(-66.21, 12.54) * mm, "end": v(-66.36, 12.51) * mm});
            skLineSegment(sketch, "E2314", {"start": v(-66.36, 12.51) * mm, "end": v(-66.66, 12.44) * mm});
            skLineSegment(sketch, "E2315", {"start": v(-66.66, 12.44) * mm, "end": v(-66.82, 12.4) * mm});
            skLineSegment(sketch, "E2316", {"start": v(-66.82, 12.4) * mm, "end": v(-66.98, 12.37) * mm});
            skLineSegment(sketch, "E2317", {"start": v(-66.98, 12.37) * mm, "end": v(-67.13, 12.33) * mm});
            skLineSegment(sketch, "E2318", {"start": v(-67.13, 12.33) * mm, "end": v(-67.24, 12.28) * mm});
            skLineSegment(sketch, "E2319", {"start": v(-67.24, 12.28) * mm, "end": v(-67.51, 10.68) * mm});
            skLineSegment(sketch, "E2320", {"start": v(-67.51, 10.68) * mm, "end": v(-67.43, 10.6) * mm});
            skLineSegment(sketch, "E2321", {"start": v(-67.43, 10.6) * mm, "end": v(-67.3, 10.5) * mm});
            skLineSegment(sketch, "E2322", {"start": v(-67.3, 10.5) * mm, "end": v(-67.16, 10.42) * mm});
            skLineSegment(sketch, "E2323", {"start": v(-67.16, 10.42) * mm, "end": v(-67.03, 10.33) * mm});
            skLineSegment(sketch, "E2324", {"start": v(-67.03, 10.33) * mm, "end": v(-66.9, 10.25) * mm});
            skLineSegment(sketch, "E2325", {"start": v(-66.9, 10.25) * mm, "end": v(-66.76, 10.17) * mm});
            skLineSegment(sketch, "E2326", {"start": v(-66.76, 10.17) * mm, "end": v(-66.63, 10.09) * mm});
            skLineSegment(sketch, "E2327", {"start": v(-66.63, 10.09) * mm, "end": v(-66.5, 10) * mm});
            skLineSegment(sketch, "E2328", {"start": v(-66.5, 10) * mm, "end": v(-66.37, 9.93) * mm});
            skLineSegment(sketch, "E2329", {"start": v(-66.37, 9.93) * mm, "end": v(-66.25, 9.86) * mm});
            skLineSegment(sketch, "E2330", {"start": v(-66.25, 9.86) * mm, "end": v(-66.12, 9.79) * mm});
            skLineSegment(sketch, "E2331", {"start": v(-66.12, 9.79) * mm, "end": v(-66, 9.72) * mm});
            skLineSegment(sketch, "E2332", {"start": v(-66, 9.72) * mm, "end": v(-65.88, 9.65) * mm});
            skLineSegment(sketch, "E2333", {"start": v(-65.88, 9.65) * mm, "end": v(-65.76, 9.58) * mm});
            skLineSegment(sketch, "E2334", {"start": v(-65.76, 9.58) * mm, "end": v(-65.52, 9.45) * mm});
            skLineSegment(sketch, "E2335", {"start": v(-65.52, 9.45) * mm, "end": v(-65.4, 9.39) * mm});
            skLineSegment(sketch, "E2336", {"start": v(-65.4, 9.39) * mm, "end": v(-65.3, 9.33) * mm});
            skLineSegment(sketch, "E2337", {"start": v(-65.3, 9.33) * mm, "end": v(-65.18, 9.27) * mm});
            skLineSegment(sketch, "E2338", {"start": v(-65.18, 9.27) * mm, "end": v(-65.07, 9.21) * mm});
            skLineSegment(sketch, "E2339", {"start": v(-65.07, 9.21) * mm, "end": v(-64.96, 9.16) * mm});
            skLineSegment(sketch, "E2340", {"start": v(-64.96, 9.16) * mm, "end": v(-64.85, 9.1) * mm});
            skLineSegment(sketch, "E2341", {"start": v(-64.85, 9.1) * mm, "end": v(-64.74, 9.05) * mm});
            skLineSegment(sketch, "E2342", {"start": v(-64.74, 9.05) * mm, "end": v(-64.64, 9) * mm});
            skLineSegment(sketch, "E2343", {"start": v(-64.64, 9) * mm, "end": v(-64.53, 8.95) * mm});
            skLineSegment(sketch, "E2344", {"start": v(-64.53, 8.95) * mm, "end": v(-64.43, 8.9) * mm});
            skLineSegment(sketch, "E2345", {"start": v(-64.43, 8.9) * mm, "end": v(-64.33, 8.86) * mm});
            skLineSegment(sketch, "E2346", {"start": v(-64.33, 8.86) * mm, "end": v(-64.23, 8.8) * mm});
            skLineSegment(sketch, "E2347", {"start": v(-64.23, 8.8) * mm, "end": v(-64.14, 8.77) * mm});
            skLineSegment(sketch, "E2348", {"start": v(-64.14, 8.77) * mm, "end": v(-64.04, 8.72) * mm});
            skLineSegment(sketch, "E2349", {"start": v(-64.04, 8.72) * mm, "end": v(-63.95, 8.68) * mm});
            skLineSegment(sketch, "E2350", {"start": v(-63.95, 8.68) * mm, "end": v(-63.86, 8.64) * mm});
            skLineSegment(sketch, "E2351", {"start": v(-63.86, 8.64) * mm, "end": v(-63.77, 8.6) * mm});
            skLineSegment(sketch, "E2352", {"start": v(-63.77, 8.6) * mm, "end": v(-63.68, 8.57) * mm});
            skLineSegment(sketch, "E2353", {"start": v(-63.68, 8.57) * mm, "end": v(-63.6, 8.53) * mm});
            skLineSegment(sketch, "E2354", {"start": v(-63.6, 8.53) * mm, "end": v(-63.5, 8.5) * mm});
            skLineSegment(sketch, "E2355", {"start": v(-63.5, 8.5) * mm, "end": v(-63.42, 8.47) * mm});
            skLineSegment(sketch, "E2356", {"start": v(-63.42, 8.47) * mm, "end": v(-63.34, 8.44) * mm});
            skLineSegment(sketch, "E2357", {"start": v(-63.34, 8.44) * mm, "end": v(-63.26, 8.4) * mm});
            skLineSegment(sketch, "E2358", {"start": v(-63.26, 8.4) * mm, "end": v(-63.18, 8.38) * mm});
            skLineSegment(sketch, "E2359", {"start": v(-63.18, 8.38) * mm, "end": v(-63.09, 8.12) * mm});
            skLineSegment(sketch, "E2360", {"start": v(-63.09, 8.12) * mm, "end": v(-63.26, 6.65) * mm});
            skLineSegment(sketch, "E2361", {"start": v(-63.26, 6.65) * mm, "end": v(-63.41, 6.42) * mm});
            skLineSegment(sketch, "E2362", {"start": v(-63.41, 6.42) * mm, "end": v(-63.5, 6.41) * mm});
            skLineSegment(sketch, "E2363", {"start": v(-63.5, 6.41) * mm, "end": v(-63.58, 6.4) * mm});
            skLineSegment(sketch, "E2364", {"start": v(-63.58, 6.4) * mm, "end": v(-63.67, 6.39) * mm});
            skLineSegment(sketch, "E2365", {"start": v(-63.67, 6.39) * mm, "end": v(-63.75, 6.38) * mm});
            skLineSegment(sketch, "E2366", {"start": v(-63.75, 6.38) * mm, "end": v(-63.84, 6.36) * mm});
            skLineSegment(sketch, "E2367", {"start": v(-63.84, 6.36) * mm, "end": v(-63.94, 6.35) * mm});
            skLineSegment(sketch, "E2368", {"start": v(-63.94, 6.35) * mm, "end": v(-64.03, 6.33) * mm});
            skLineSegment(sketch, "E2369", {"start": v(-64.03, 6.33) * mm, "end": v(-64.13, 6.32) * mm});
            skLineSegment(sketch, "E2370", {"start": v(-64.13, 6.32) * mm, "end": v(-64.23, 6.3) * mm});
            skLineSegment(sketch, "E2371", {"start": v(-64.23, 6.3) * mm, "end": v(-64.33, 6.28) * mm});
            skLineSegment(sketch, "E2372", {"start": v(-64.33, 6.28) * mm, "end": v(-64.43, 6.26) * mm});
            skLineSegment(sketch, "E2373", {"start": v(-64.43, 6.26) * mm, "end": v(-64.53, 6.24) * mm});
            skLineSegment(sketch, "E2374", {"start": v(-64.53, 6.24) * mm, "end": v(-64.64, 6.22) * mm});
            skLineSegment(sketch, "E2375", {"start": v(-64.64, 6.22) * mm, "end": v(-64.75, 6.2) * mm});
            skLineSegment(sketch, "E2376", {"start": v(-64.75, 6.2) * mm, "end": v(-64.86, 6.18) * mm});
            skLineSegment(sketch, "E2377", {"start": v(-64.86, 6.18) * mm, "end": v(-64.97, 6.15) * mm});
            skLineSegment(sketch, "E2378", {"start": v(-64.97, 6.15) * mm, "end": v(-65.08, 6.13) * mm});
            skLineSegment(sketch, "E2379", {"start": v(-65.08, 6.13) * mm, "end": v(-65.2, 6.1) * mm});
            skLineSegment(sketch, "E2380", {"start": v(-65.2, 6.1) * mm, "end": v(-65.32, 6.07) * mm});
            skLineSegment(sketch, "E2381", {"start": v(-65.32, 6.07) * mm, "end": v(-65.44, 6.05) * mm});
            skLineSegment(sketch, "E2382", {"start": v(-65.44, 6.05) * mm, "end": v(-65.56, 6.02) * mm});
            skLineSegment(sketch, "E2383", {"start": v(-65.56, 6.02) * mm, "end": v(-65.68, 5.98) * mm});
            skLineSegment(sketch, "E2384", {"start": v(-65.68, 5.98) * mm, "end": v(-65.8, 5.95) * mm});
            skLineSegment(sketch, "E2385", {"start": v(-65.8, 5.95) * mm, "end": v(-65.93, 5.92) * mm});
            skLineSegment(sketch, "E2386", {"start": v(-65.93, 5.92) * mm, "end": v(-66.06, 5.88) * mm});
            skLineSegment(sketch, "E2387", {"start": v(-66.06, 5.88) * mm, "end": v(-66.2, 5.85) * mm});
            skLineSegment(sketch, "E2388", {"start": v(-66.2, 5.85) * mm, "end": v(-66.33, 5.8) * mm});
            skLineSegment(sketch, "E2389", {"start": v(-66.33, 5.8) * mm, "end": v(-66.46, 5.77) * mm});
            skLineSegment(sketch, "E2390", {"start": v(-66.46, 5.77) * mm, "end": v(-66.6, 5.73) * mm});
            skLineSegment(sketch, "E2391", {"start": v(-66.6, 5.73) * mm, "end": v(-66.74, 5.69) * mm});
            skLineSegment(sketch, "E2392", {"start": v(-66.74, 5.69) * mm, "end": v(-67.02, 5.6) * mm});
            skLineSegment(sketch, "E2393", {"start": v(-67.02, 5.6) * mm, "end": v(-67.16, 5.55) * mm});
            skLineSegment(sketch, "E2394", {"start": v(-67.16, 5.55) * mm, "end": v(-67.3, 5.5) * mm});
            skLineSegment(sketch, "E2395", {"start": v(-67.3, 5.5) * mm, "end": v(-67.45, 5.46) * mm});
            skLineSegment(sketch, "E2396", {"start": v(-67.45, 5.46) * mm, "end": v(-67.6, 5.4) * mm});
            skLineSegment(sketch, "E2397", {"start": v(-67.6, 5.4) * mm, "end": v(-67.75, 5.36) * mm});
            skLineSegment(sketch, "E2398", {"start": v(-67.75, 5.36) * mm, "end": v(-67.9, 5.3) * mm});
            skLineSegment(sketch, "E2399", {"start": v(-67.9, 5.3) * mm, "end": v(-68.06, 5.25) * mm});
            skLineSegment(sketch, "E2400", {"start": v(-68.06, 5.25) * mm, "end": v(-68.15, 5.18) * mm});
            skLineSegment(sketch, "E2401", {"start": v(-68.15, 5.18) * mm, "end": v(-68.26, 3.56) * mm});
            skLineSegment(sketch, "E2402", {"start": v(-68.26, 3.56) * mm, "end": v(-68.17, 3.49) * mm});
            skLineSegment(sketch, "E2403", {"start": v(-68.17, 3.49) * mm, "end": v(-68.02, 3.41) * mm});
            skLineSegment(sketch, "E2404", {"start": v(-68.02, 3.41) * mm, "end": v(-67.88, 3.34) * mm});
            skLineSegment(sketch, "E2405", {"start": v(-67.88, 3.34) * mm, "end": v(-67.74, 3.27) * mm});
            skLineSegment(sketch, "E2406", {"start": v(-67.74, 3.27) * mm, "end": v(-67.6, 3.2) * mm});
            skLineSegment(sketch, "E2407", {"start": v(-67.6, 3.2) * mm, "end": v(-67.46, 3.13) * mm});
            skLineSegment(sketch, "E2408", {"start": v(-67.46, 3.13) * mm, "end": v(-67.32, 3.07) * mm});
            skLineSegment(sketch, "E2409", {"start": v(-67.32, 3.07) * mm, "end": v(-67.18, 3) * mm});
            skLineSegment(sketch, "E2410", {"start": v(-67.18, 3) * mm, "end": v(-67.05, 2.94) * mm});
            skLineSegment(sketch, "E2411", {"start": v(-67.05, 2.94) * mm, "end": v(-66.92, 2.88) * mm});
            skLineSegment(sketch, "E2412", {"start": v(-66.92, 2.88) * mm, "end": v(-66.78, 2.82) * mm});
            skLineSegment(sketch, "E2413", {"start": v(-66.78, 2.82) * mm, "end": v(-66.65, 2.76) * mm});
            skLineSegment(sketch, "E2414", {"start": v(-66.65, 2.76) * mm, "end": v(-66.53, 2.7) * mm});
            skLineSegment(sketch, "E2415", {"start": v(-66.53, 2.7) * mm, "end": v(-66.4, 2.65) * mm});
            skLineSegment(sketch, "E2416", {"start": v(-66.4, 2.65) * mm, "end": v(-66.27, 2.6) * mm});
            skLineSegment(sketch, "E2417", {"start": v(-66.27, 2.6) * mm, "end": v(-66.15, 2.55) * mm});
            skLineSegment(sketch, "E2418", {"start": v(-66.15, 2.55) * mm, "end": v(-66.03, 2.5) * mm});
            skLineSegment(sketch, "E2419", {"start": v(-66.03, 2.5) * mm, "end": v(-65.9, 2.45) * mm});
            skLineSegment(sketch, "E2420", {"start": v(-65.9, 2.45) * mm, "end": v(-65.8, 2.4) * mm});
            skLineSegment(sketch, "E2421", {"start": v(-65.8, 2.4) * mm, "end": v(-65.67, 2.36) * mm});
            skLineSegment(sketch, "E2422", {"start": v(-65.67, 2.36) * mm, "end": v(-65.56, 2.32) * mm});
            skLineSegment(sketch, "E2423", {"start": v(-65.56, 2.32) * mm, "end": v(-65.45, 2.27) * mm});
            skLineSegment(sketch, "E2424", {"start": v(-65.45, 2.27) * mm, "end": v(-65.33, 2.23) * mm});
            skLineSegment(sketch, "E2425", {"start": v(-65.33, 2.23) * mm, "end": v(-65.22, 2.2) * mm});
            skLineSegment(sketch, "E2426", {"start": v(-65.22, 2.2) * mm, "end": v(-65.12, 2.15) * mm});
            skLineSegment(sketch, "E2427", {"start": v(-65.12, 2.15) * mm, "end": v(-65.01, 2.12) * mm});
            skLineSegment(sketch, "E2428", {"start": v(-65.01, 2.12) * mm, "end": v(-64.9, 2.08) * mm});
            skLineSegment(sketch, "E2429", {"start": v(-64.9, 2.08) * mm, "end": v(-64.8, 2.05) * mm});
            skLineSegment(sketch, "E2430", {"start": v(-64.8, 2.05) * mm, "end": v(-64.7, 2.01) * mm});
            skLineSegment(sketch, "E2431", {"start": v(-64.7, 2.01) * mm, "end": v(-64.6, 1.98) * mm});
            skLineSegment(sketch, "E2432", {"start": v(-64.6, 1.98) * mm, "end": v(-64.5, 1.95) * mm});
            skLineSegment(sketch, "E2433", {"start": v(-64.5, 1.95) * mm, "end": v(-64.4, 1.92) * mm});
            skLineSegment(sketch, "E2434", {"start": v(-64.4, 1.92) * mm, "end": v(-64.32, 1.9) * mm});
            skLineSegment(sketch, "E2435", {"start": v(-64.32, 1.9) * mm, "end": v(-64.13, 1.84) * mm});
            skLineSegment(sketch, "E2436", {"start": v(-64.13, 1.84) * mm, "end": v(-63.96, 1.8) * mm});
            skLineSegment(sketch, "E2437", {"start": v(-63.96, 1.8) * mm, "end": v(-63.88, 1.77) * mm});
            skLineSegment(sketch, "E2438", {"start": v(-63.88, 1.77) * mm, "end": v(-63.8, 1.75) * mm});
            skLineSegment(sketch, "E2439", {"start": v(-63.8, 1.75) * mm, "end": v(-63.71, 1.73) * mm});
            skLineSegment(sketch, "E2440", {"start": v(-63.71, 1.73) * mm, "end": v(-63.6, 1.48) * mm});
            skLineSegment(sketch, "E2441", {"start": v(-63.6, 1.48) * mm, "end": v(-63.61, 0) * mm});
            skLineSegment(sketch, "E2442", {"start": v(-63.61, 0) * mm, "end": v(-63.74, -0.24) * mm});
            skLineSegment(sketch, "E2443", {"start": v(-63.74, -0.24) * mm, "end": v(-63.82, -0.26) * mm});
            skLineSegment(sketch, "E2444", {"start": v(-63.82, -0.26) * mm, "end": v(-63.9, -0.28) * mm});
            skLineSegment(sketch, "E2445", {"start": v(-63.9, -0.28) * mm, "end": v(-63.99, -0.3) * mm});
            skLineSegment(sketch, "E2446", {"start": v(-63.99, -0.3) * mm, "end": v(-64.07, -0.32) * mm});
            skLineSegment(sketch, "E2447", {"start": v(-64.07, -0.32) * mm, "end": v(-64.16, -0.35) * mm});
            skLineSegment(sketch, "E2448", {"start": v(-64.16, -0.35) * mm, "end": v(-64.25, -0.37) * mm});
            skLineSegment(sketch, "E2449", {"start": v(-64.25, -0.37) * mm, "end": v(-64.34, -0.4) * mm});
            skLineSegment(sketch, "E2450", {"start": v(-64.34, -0.4) * mm, "end": v(-64.44, -0.42) * mm});
            skLineSegment(sketch, "E2451", {"start": v(-64.44, -0.42) * mm, "end": v(-64.53, -0.45) * mm});
            skLineSegment(sketch, "E2452", {"start": v(-64.53, -0.45) * mm, "end": v(-64.63, -0.48) * mm});
            skLineSegment(sketch, "E2453", {"start": v(-64.63, -0.48) * mm, "end": v(-64.73, -0.5) * mm});
            skLineSegment(sketch, "E2454", {"start": v(-64.73, -0.5) * mm, "end": v(-64.83, -0.54) * mm});
            skLineSegment(sketch, "E2455", {"start": v(-64.83, -0.54) * mm, "end": v(-64.94, -0.57) * mm});
            skLineSegment(sketch, "E2456", {"start": v(-64.94, -0.57) * mm, "end": v(-65.15, -0.64) * mm});
            skLineSegment(sketch, "E2457", {"start": v(-65.15, -0.64) * mm, "end": v(-65.37, -0.7) * mm});
            skLineSegment(sketch, "E2458", {"start": v(-65.37, -0.7) * mm, "end": v(-65.48, -0.75) * mm});
            skLineSegment(sketch, "E2459", {"start": v(-65.48, -0.75) * mm, "end": v(-65.6, -0.79) * mm});
            skLineSegment(sketch, "E2460", {"start": v(-65.6, -0.79) * mm, "end": v(-65.71, -0.83) * mm});
            skLineSegment(sketch, "E2461", {"start": v(-65.71, -0.83) * mm, "end": v(-65.83, -0.87) * mm});
            skLineSegment(sketch, "E2462", {"start": v(-65.83, -0.87) * mm, "end": v(-65.95, -0.92) * mm});
            skLineSegment(sketch, "E2463", {"start": v(-65.95, -0.92) * mm, "end": v(-66.07, -0.96) * mm});
            skLineSegment(sketch, "E2464", {"start": v(-66.07, -0.96) * mm, "end": v(-66.2, -1) * mm});
            skLineSegment(sketch, "E2465", {"start": v(-66.2, -1) * mm, "end": v(-66.32, -1.05) * mm});
            skLineSegment(sketch, "E2466", {"start": v(-66.32, -1.05) * mm, "end": v(-66.44, -1.1) * mm});
            skLineSegment(sketch, "E2467", {"start": v(-66.44, -1.1) * mm, "end": v(-66.57, -1.16) * mm});
            skLineSegment(sketch, "E2468", {"start": v(-66.57, -1.16) * mm, "end": v(-66.7, -1.2) * mm});
            skLineSegment(sketch, "E2469", {"start": v(-66.7, -1.2) * mm, "end": v(-66.83, -1.26) * mm});
            skLineSegment(sketch, "E2470", {"start": v(-66.83, -1.26) * mm, "end": v(-66.96, -1.32) * mm});
            skLineSegment(sketch, "E2471", {"start": v(-66.96, -1.32) * mm, "end": v(-67.1, -1.38) * mm});
            skLineSegment(sketch, "E2472", {"start": v(-67.1, -1.38) * mm, "end": v(-67.24, -1.44) * mm});
            skLineSegment(sketch, "E2473", {"start": v(-67.24, -1.44) * mm, "end": v(-67.37, -1.5) * mm});
            skLineSegment(sketch, "E2474", {"start": v(-67.37, -1.5) * mm, "end": v(-67.51, -1.56) * mm});
            skLineSegment(sketch, "E2475", {"start": v(-67.51, -1.56) * mm, "end": v(-67.8, -1.69) * mm});
            skLineSegment(sketch, "E2476", {"start": v(-67.8, -1.69) * mm, "end": v(-67.94, -1.76) * mm});
            skLineSegment(sketch, "E2477", {"start": v(-67.94, -1.76) * mm, "end": v(-68.08, -1.83) * mm});
            skLineSegment(sketch, "E2478", {"start": v(-68.08, -1.83) * mm, "end": v(-68.23, -1.9) * mm});
            skLineSegment(sketch, "E2479", {"start": v(-68.23, -1.9) * mm, "end": v(-68.32, -1.97) * mm});
            skLineSegment(sketch, "E2480", {"start": v(-68.32, -1.97) * mm, "end": v(-68.26, -3.6) * mm});
            skLineSegment(sketch, "E2481", {"start": v(-68.26, -3.6) * mm, "end": v(-68.16, -3.66) * mm});
            skLineSegment(sketch, "E2482", {"start": v(-68.16, -3.66) * mm, "end": v(-67.86, -3.77) * mm});
            skLineSegment(sketch, "E2483", {"start": v(-67.86, -3.77) * mm, "end": v(-67.7, -3.83) * mm});
            skLineSegment(sketch, "E2484", {"start": v(-67.7, -3.83) * mm, "end": v(-67.56, -3.88) * mm});
            skLineSegment(sketch, "E2485", {"start": v(-67.56, -3.88) * mm, "end": v(-67.42, -3.94) * mm});
            skLineSegment(sketch, "E2486", {"start": v(-67.42, -3.94) * mm, "end": v(-67.27, -3.99) * mm});
            skLineSegment(sketch, "E2487", {"start": v(-67.27, -3.99) * mm, "end": v(-67.13, -4.04) * mm});
            skLineSegment(sketch, "E2488", {"start": v(-67.13, -4.04) * mm, "end": v(-66.99, -4.08) * mm});
            skLineSegment(sketch, "E2489", {"start": v(-66.99, -4.08) * mm, "end": v(-66.85, -4.13) * mm});
            skLineSegment(sketch, "E2490", {"start": v(-66.85, -4.13) * mm, "end": v(-66.71, -4.18) * mm});
            skLineSegment(sketch, "E2491", {"start": v(-66.71, -4.18) * mm, "end": v(-66.58, -4.22) * mm});
            skLineSegment(sketch, "E2492", {"start": v(-66.58, -4.22) * mm, "end": v(-66.44, -4.26) * mm});
            skLineSegment(sketch, "E2493", {"start": v(-66.44, -4.26) * mm, "end": v(-66.31, -4.3) * mm});
            skLineSegment(sketch, "E2494", {"start": v(-66.31, -4.3) * mm, "end": v(-66.18, -4.34) * mm});
            skLineSegment(sketch, "E2495", {"start": v(-66.18, -4.34) * mm, "end": v(-66.05, -4.38) * mm});
            skLineSegment(sketch, "E2496", {"start": v(-66.05, -4.38) * mm, "end": v(-65.93, -4.42) * mm});
            skLineSegment(sketch, "E2497", {"start": v(-65.93, -4.42) * mm, "end": v(-65.8, -4.45) * mm});
            skLineSegment(sketch, "E2498", {"start": v(-65.8, -4.45) * mm, "end": v(-65.68, -4.49) * mm});
            skLineSegment(sketch, "E2499", {"start": v(-65.68, -4.49) * mm, "end": v(-65.56, -4.52) * mm});
            skLineSegment(sketch, "E2500", {"start": v(-65.56, -4.52) * mm, "end": v(-65.44, -4.55) * mm});
            skLineSegment(sketch, "E2501", {"start": v(-65.44, -4.55) * mm, "end": v(-65.32, -4.58) * mm});
            skLineSegment(sketch, "E2502", {"start": v(-65.32, -4.58) * mm, "end": v(-65.21, -4.6) * mm});
            skLineSegment(sketch, "E2503", {"start": v(-65.21, -4.6) * mm, "end": v(-65.1, -4.64) * mm});
            skLineSegment(sketch, "E2504", {"start": v(-65.1, -4.64) * mm, "end": v(-64.98, -4.66) * mm});
            skLineSegment(sketch, "E2505", {"start": v(-64.98, -4.66) * mm, "end": v(-64.88, -4.69) * mm});
            skLineSegment(sketch, "E2506", {"start": v(-64.88, -4.69) * mm, "end": v(-64.77, -4.71) * mm});
            skLineSegment(sketch, "E2507", {"start": v(-64.77, -4.71) * mm, "end": v(-64.66, -4.74) * mm});
            skLineSegment(sketch, "E2508", {"start": v(-64.66, -4.74) * mm, "end": v(-64.56, -4.76) * mm});
            skLineSegment(sketch, "E2509", {"start": v(-64.56, -4.76) * mm, "end": v(-64.46, -4.78) * mm});
            skLineSegment(sketch, "E2510", {"start": v(-64.46, -4.78) * mm, "end": v(-64.36, -4.8) * mm});
            skLineSegment(sketch, "E2511", {"start": v(-64.36, -4.8) * mm, "end": v(-64.26, -4.82) * mm});
            skLineSegment(sketch, "E2512", {"start": v(-64.26, -4.82) * mm, "end": v(-64.16, -4.84) * mm});
            skLineSegment(sketch, "E2513", {"start": v(-64.16, -4.84) * mm, "end": v(-64.07, -4.86) * mm});
            skLineSegment(sketch, "E2514", {"start": v(-64.07, -4.86) * mm, "end": v(-63.98, -4.87) * mm});
            skLineSegment(sketch, "E2515", {"start": v(-63.98, -4.87) * mm, "end": v(-63.89, -4.89) * mm});
            skLineSegment(sketch, "E2516", {"start": v(-63.89, -4.89) * mm, "end": v(-63.8, -4.9) * mm});
            skLineSegment(sketch, "E2517", {"start": v(-63.8, -4.9) * mm, "end": v(-63.71, -4.92) * mm});
            skLineSegment(sketch, "E2518", {"start": v(-63.71, -4.92) * mm, "end": v(-63.63, -4.93) * mm});
            skLineSegment(sketch, "E2519", {"start": v(-63.63, -4.93) * mm, "end": v(-63.54, -4.94) * mm});
            skLineSegment(sketch, "E2520", {"start": v(-63.54, -4.94) * mm, "end": v(-63.4, -5.17) * mm});
            skLineSegment(sketch, "E2521", {"start": v(-63.4, -5.17) * mm, "end": v(-63.26, -6.65) * mm});
            skLineSegment(sketch, "E2522", {"start": v(-63.26, -6.65) * mm, "end": v(-63.36, -6.9) * mm});
            skLineSegment(sketch, "E2523", {"start": v(-63.36, -6.9) * mm, "end": v(-63.44, -6.93) * mm});
            skLineSegment(sketch, "E2524", {"start": v(-63.44, -6.93) * mm, "end": v(-63.52, -6.96) * mm});
            skLineSegment(sketch, "E2525", {"start": v(-63.52, -6.96) * mm, "end": v(-63.6, -6.99) * mm});
            skLineSegment(sketch, "E2526", {"start": v(-63.6, -6.99) * mm, "end": v(-63.69, -7.02) * mm});
            skLineSegment(sketch, "E2527", {"start": v(-63.69, -7.02) * mm, "end": v(-63.77, -7.05) * mm});
            skLineSegment(sketch, "E2528", {"start": v(-63.77, -7.05) * mm, "end": v(-63.86, -7.08) * mm});
            skLineSegment(sketch, "E2529", {"start": v(-63.86, -7.08) * mm, "end": v(-63.95, -7.12) * mm});
            skLineSegment(sketch, "E2530", {"start": v(-63.95, -7.12) * mm, "end": v(-64.04, -7.15) * mm});
            skLineSegment(sketch, "E2531", {"start": v(-64.04, -7.15) * mm, "end": v(-64.13, -7.2) * mm});
            skLineSegment(sketch, "E2532", {"start": v(-64.13, -7.2) * mm, "end": v(-64.23, -7.23) * mm});
            skLineSegment(sketch, "E2533", {"start": v(-64.23, -7.23) * mm, "end": v(-64.32, -7.27) * mm});
            skLineSegment(sketch, "E2534", {"start": v(-64.32, -7.27) * mm, "end": v(-64.42, -7.31) * mm});
            skLineSegment(sketch, "E2535", {"start": v(-64.42, -7.31) * mm, "end": v(-64.52, -7.35) * mm});
            skLineSegment(sketch, "E2536", {"start": v(-64.52, -7.35) * mm, "end": v(-64.62, -7.4) * mm});
            skLineSegment(sketch, "E2537", {"start": v(-64.62, -7.4) * mm, "end": v(-64.73, -7.44) * mm});
            skLineSegment(sketch, "E2538", {"start": v(-64.73, -7.44) * mm, "end": v(-64.83, -7.49) * mm});
            skLineSegment(sketch, "E2539", {"start": v(-64.83, -7.49) * mm, "end": v(-64.94, -7.54) * mm});
            skLineSegment(sketch, "E2540", {"start": v(-64.94, -7.54) * mm, "end": v(-65.04, -7.59) * mm});
            skLineSegment(sketch, "E2541", {"start": v(-65.04, -7.59) * mm, "end": v(-65.15, -7.64) * mm});
            skLineSegment(sketch, "E2542", {"start": v(-65.15, -7.64) * mm, "end": v(-65.27, -7.7) * mm});
            skLineSegment(sketch, "E2543", {"start": v(-65.27, -7.7) * mm, "end": v(-65.38, -7.75) * mm});
            skLineSegment(sketch, "E2544", {"start": v(-65.38, -7.75) * mm, "end": v(-65.5, -7.8) * mm});
            skLineSegment(sketch, "E2545", {"start": v(-65.5, -7.8) * mm, "end": v(-65.6, -7.86) * mm});
            skLineSegment(sketch, "E2546", {"start": v(-65.6, -7.86) * mm, "end": v(-65.72, -7.92) * mm});
            skLineSegment(sketch, "E2547", {"start": v(-65.72, -7.92) * mm, "end": v(-65.96, -8.04) * mm});
            skLineSegment(sketch, "E2548", {"start": v(-65.96, -8.04) * mm, "end": v(-66.09, -8.1) * mm});
            skLineSegment(sketch, "E2549", {"start": v(-66.09, -8.1) * mm, "end": v(-66.2, -8.17) * mm});
            skLineSegment(sketch, "E2550", {"start": v(-66.2, -8.17) * mm, "end": v(-66.33, -8.24) * mm});
            skLineSegment(sketch, "E2551", {"start": v(-66.33, -8.24) * mm, "end": v(-66.46, -8.31) * mm});
            skLineSegment(sketch, "E2552", {"start": v(-66.46, -8.31) * mm, "end": v(-66.59, -8.38) * mm});
            skLineSegment(sketch, "E2553", {"start": v(-66.59, -8.38) * mm, "end": v(-66.72, -8.46) * mm});
            skLineSegment(sketch, "E2554", {"start": v(-66.72, -8.46) * mm, "end": v(-66.85, -8.53) * mm});
            skLineSegment(sketch, "E2555", {"start": v(-66.85, -8.53) * mm, "end": v(-66.98, -8.6) * mm});
            skLineSegment(sketch, "E2556", {"start": v(-66.98, -8.6) * mm, "end": v(-67.11, -8.69) * mm});
            skLineSegment(sketch, "E2557", {"start": v(-67.11, -8.69) * mm, "end": v(-67.25, -8.77) * mm});
            skLineSegment(sketch, "E2558", {"start": v(-67.25, -8.77) * mm, "end": v(-67.38, -8.85) * mm});
            skLineSegment(sketch, "E2559", {"start": v(-67.38, -8.85) * mm, "end": v(-67.52, -8.93) * mm});
            skLineSegment(sketch, "E2560", {"start": v(-67.52, -8.93) * mm, "end": v(-67.66, -9.02) * mm});
            skLineSegment(sketch, "E2561", {"start": v(-67.66, -9.02) * mm, "end": v(-67.74, -9.1) * mm});
            skLineSegment(sketch, "E2562", {"start": v(-67.74, -9.1) * mm, "end": v(-67.5, -10.71) * mm});
            skLineSegment(sketch, "E2563", {"start": v(-67.5, -10.71) * mm, "end": v(-67.4, -10.76) * mm});
            skLineSegment(sketch, "E2564", {"start": v(-67.4, -10.76) * mm, "end": v(-67.25, -10.8) * mm});
            skLineSegment(sketch, "E2565", {"start": v(-67.25, -10.8) * mm, "end": v(-67.09, -10.85) * mm});
            skLineSegment(sketch, "E2566", {"start": v(-67.09, -10.85) * mm, "end": v(-66.94, -10.89) * mm});
            skLineSegment(sketch, "E2567", {"start": v(-66.94, -10.89) * mm, "end": v(-66.78, -10.93) * mm});
            skLineSegment(sketch, "E2568", {"start": v(-66.78, -10.93) * mm, "end": v(-66.64, -10.96) * mm});
            skLineSegment(sketch, "E2569", {"start": v(-66.64, -10.96) * mm, "end": v(-66.49, -11) * mm});
            skLineSegment(sketch, "E2570", {"start": v(-66.49, -11) * mm, "end": v(-66.34, -11.03) * mm});
            skLineSegment(sketch, "E2571", {"start": v(-66.34, -11.03) * mm, "end": v(-66.2, -11.06) * mm});
            skLineSegment(sketch, "E2572", {"start": v(-66.2, -11.06) * mm, "end": v(-66.05, -11.1) * mm});
            skLineSegment(sketch, "E2573", {"start": v(-66.05, -11.1) * mm, "end": v(-65.91, -11.13) * mm});
            skLineSegment(sketch, "E2574", {"start": v(-65.91, -11.13) * mm, "end": v(-65.77, -11.16) * mm});
            skLineSegment(sketch, "E2575", {"start": v(-65.77, -11.16) * mm, "end": v(-65.64, -11.18) * mm});
            skLineSegment(sketch, "E2576", {"start": v(-65.64, -11.18) * mm, "end": v(-65.5, -11.21) * mm});
            skLineSegment(sketch, "E2577", {"start": v(-65.5, -11.21) * mm, "end": v(-65.37, -11.24) * mm});
            skLineSegment(sketch, "E2578", {"start": v(-65.37, -11.24) * mm, "end": v(-65.23, -11.26) * mm});
            skLineSegment(sketch, "E2579", {"start": v(-65.23, -11.26) * mm, "end": v(-65.1, -11.28) * mm});
            skLineSegment(sketch, "E2580", {"start": v(-65.1, -11.28) * mm, "end": v(-64.98, -11.3) * mm});
            skLineSegment(sketch, "E2581", {"start": v(-64.98, -11.3) * mm, "end": v(-64.85, -11.33) * mm});
            skLineSegment(sketch, "E2582", {"start": v(-64.85, -11.33) * mm, "end": v(-64.73, -11.35) * mm});
            skLineSegment(sketch, "E2583", {"start": v(-64.73, -11.35) * mm, "end": v(-64.6, -11.37) * mm});
            skLineSegment(sketch, "E2584", {"start": v(-64.6, -11.37) * mm, "end": v(-64.49, -11.38) * mm});
            skLineSegment(sketch, "E2585", {"start": v(-64.49, -11.38) * mm, "end": v(-64.37, -11.4) * mm});
            skLineSegment(sketch, "E2586", {"start": v(-64.37, -11.4) * mm, "end": v(-64.26, -11.42) * mm});
            skLineSegment(sketch, "E2587", {"start": v(-64.26, -11.42) * mm, "end": v(-64.14, -11.43) * mm});
            skLineSegment(sketch, "E2588", {"start": v(-64.14, -11.43) * mm, "end": v(-64.03, -11.44) * mm});
            skLineSegment(sketch, "E2589", {"start": v(-64.03, -11.44) * mm, "end": v(-63.92, -11.46) * mm});
            skLineSegment(sketch, "E2590", {"start": v(-63.92, -11.46) * mm, "end": v(-63.81, -11.47) * mm});
            skLineSegment(sketch, "E2591", {"start": v(-63.81, -11.47) * mm, "end": v(-63.7, -11.48) * mm});
            skLineSegment(sketch, "E2592", {"start": v(-63.7, -11.48) * mm, "end": v(-63.6, -11.5) * mm});
            skLineSegment(sketch, "E2593", {"start": v(-63.6, -11.5) * mm, "end": v(-63.5, -11.5) * mm});
            skLineSegment(sketch, "E2594", {"start": v(-63.5, -11.5) * mm, "end": v(-63.4, -11.51) * mm});
            skLineSegment(sketch, "E2595", {"start": v(-63.4, -11.51) * mm, "end": v(-63.3, -11.52) * mm});
            skLineSegment(sketch, "E2596", {"start": v(-63.3, -11.52) * mm, "end": v(-63.2, -11.53) * mm});
            skLineSegment(sketch, "E2597", {"start": v(-63.2, -11.53) * mm, "end": v(-63.12, -11.53) * mm});
            skLineSegment(sketch, "E2598", {"start": v(-63.12, -11.53) * mm, "end": v(-63.02, -11.54) * mm});
            skLineSegment(sketch, "E2599", {"start": v(-63.02, -11.54) * mm, "end": v(-62.94, -11.55) * mm});
            skLineSegment(sketch, "E2600", {"start": v(-62.94, -11.55) * mm, "end": v(-62.85, -11.55) * mm});
            skLineSegment(sketch, "E2601", {"start": v(-62.85, -11.55) * mm, "end": v(-62.76, -11.55) * mm});
            skLineSegment(sketch, "E2602", {"start": v(-62.76, -11.55) * mm, "end": v(-62.68, -11.56) * mm});
            skLineSegment(sketch, "E2603", {"start": v(-62.68, -11.56) * mm, "end": v(-62.51, -11.77) * mm});
            skLineSegment(sketch, "E2604", {"start": v(-62.51, -11.77) * mm, "end": v(-62.22, -13.22) * mm});
            skLineSegment(sketch, "E2605", {"start": v(-62.22, -13.22) * mm, "end": v(-62.3, -13.49) * mm});
            skLineSegment(sketch, "E2606", {"start": v(-62.3, -13.49) * mm, "end": v(-62.37, -13.52) * mm});
            skLineSegment(sketch, "E2607", {"start": v(-62.37, -13.52) * mm, "end": v(-62.45, -13.56) * mm});
            skLineSegment(sketch, "E2608", {"start": v(-62.45, -13.56) * mm, "end": v(-62.52, -13.6) * mm});
            skLineSegment(sketch, "E2609", {"start": v(-62.52, -13.6) * mm, "end": v(-62.6, -13.64) * mm});
            skLineSegment(sketch, "E2610", {"start": v(-62.6, -13.64) * mm, "end": v(-62.69, -13.68) * mm});
            skLineSegment(sketch, "E2611", {"start": v(-62.69, -13.68) * mm, "end": v(-62.77, -13.72) * mm});
            skLineSegment(sketch, "E2612", {"start": v(-62.77, -13.72) * mm, "end": v(-62.86, -13.76) * mm});
            skLineSegment(sketch, "E2613", {"start": v(-62.86, -13.76) * mm, "end": v(-62.94, -13.8) * mm});
            skLineSegment(sketch, "E2614", {"start": v(-62.94, -13.8) * mm, "end": v(-63.03, -13.85) * mm});
            skLineSegment(sketch, "E2615", {"start": v(-63.03, -13.85) * mm, "end": v(-63.12, -13.9) * mm});
            skLineSegment(sketch, "E2616", {"start": v(-63.12, -13.9) * mm, "end": v(-63.21, -13.95) * mm});
            skLineSegment(sketch, "E2617", {"start": v(-63.21, -13.95) * mm, "end": v(-63.3, -14) * mm});
            skLineSegment(sketch, "E2618", {"start": v(-63.3, -14) * mm, "end": v(-63.4, -14.06) * mm});
            skLineSegment(sketch, "E2619", {"start": v(-63.4, -14.06) * mm, "end": v(-63.5, -14.11) * mm});
            skLineSegment(sketch, "E2620", {"start": v(-63.5, -14.11) * mm, "end": v(-63.6, -14.17) * mm});
            skLineSegment(sketch, "E2621", {"start": v(-63.6, -14.17) * mm, "end": v(-63.7, -14.23) * mm});
            skLineSegment(sketch, "E2622", {"start": v(-63.7, -14.23) * mm, "end": v(-63.8, -14.28) * mm});
            skLineSegment(sketch, "E2623", {"start": v(-63.8, -14.28) * mm, "end": v(-63.9, -14.35) * mm});
            skLineSegment(sketch, "E2624", {"start": v(-63.9, -14.35) * mm, "end": v(-64, -14.4) * mm});
            skLineSegment(sketch, "E2625", {"start": v(-64, -14.4) * mm, "end": v(-64.1, -14.47) * mm});
            skLineSegment(sketch, "E2626", {"start": v(-64.1, -14.47) * mm, "end": v(-64.2, -14.54) * mm});
            skLineSegment(sketch, "E2627", {"start": v(-64.2, -14.54) * mm, "end": v(-64.32, -14.6) * mm});
            skLineSegment(sketch, "E2628", {"start": v(-64.32, -14.6) * mm, "end": v(-64.43, -14.67) * mm});
            skLineSegment(sketch, "E2629", {"start": v(-64.43, -14.67) * mm, "end": v(-64.54, -14.75) * mm});
            skLineSegment(sketch, "E2630", {"start": v(-64.54, -14.75) * mm, "end": v(-64.65, -14.82) * mm});
            skLineSegment(sketch, "E2631", {"start": v(-64.65, -14.82) * mm, "end": v(-64.76, -14.9) * mm});
            skLineSegment(sketch, "E2632", {"start": v(-64.76, -14.9) * mm, "end": v(-64.88, -14.97) * mm});
            skLineSegment(sketch, "E2633", {"start": v(-64.88, -14.97) * mm, "end": v(-65, -15.05) * mm});
            skLineSegment(sketch, "E2634", {"start": v(-65, -15.05) * mm, "end": v(-65.23, -15.21) * mm});
            skLineSegment(sketch, "E2635", {"start": v(-65.23, -15.21) * mm, "end": v(-65.35, -15.3) * mm});
            skLineSegment(sketch, "E2636", {"start": v(-65.35, -15.3) * mm, "end": v(-65.47, -15.38) * mm});
            skLineSegment(sketch, "E2637", {"start": v(-65.47, -15.38) * mm, "end": v(-65.59, -15.47) * mm});
            skLineSegment(sketch, "E2638", {"start": v(-65.59, -15.47) * mm, "end": v(-65.71, -15.56) * mm});
            skLineSegment(sketch, "E2639", {"start": v(-65.71, -15.56) * mm, "end": v(-65.84, -15.65) * mm});
            skLineSegment(sketch, "E2640", {"start": v(-65.84, -15.65) * mm, "end": v(-65.96, -15.75) * mm});
            skLineSegment(sketch, "E2641", {"start": v(-65.96, -15.75) * mm, "end": v(-66.09, -15.84) * mm});
            skLineSegment(sketch, "E2642", {"start": v(-66.09, -15.84) * mm, "end": v(-66.22, -15.94) * mm});
            skLineSegment(sketch, "E2643", {"start": v(-66.22, -15.94) * mm, "end": v(-66.35, -16.04) * mm});
            skLineSegment(sketch, "E2644", {"start": v(-66.35, -16.04) * mm, "end": v(-66.42, -16.13) * mm});
            skLineSegment(sketch, "E2645", {"start": v(-66.42, -16.13) * mm, "end": v(-66.02, -17.7) * mm});
            skLineSegment(sketch, "E2646", {"start": v(-66.02, -17.7) * mm, "end": v(-65.9, -17.75) * mm});
            skLineSegment(sketch, "E2647", {"start": v(-65.9, -17.75) * mm, "end": v(-65.75, -17.78) * mm});
            skLineSegment(sketch, "E2648", {"start": v(-65.75, -17.78) * mm, "end": v(-65.59, -17.8) * mm});
            skLineSegment(sketch, "E2649", {"start": v(-65.59, -17.8) * mm, "end": v(-65.43, -17.82) * mm});
            skLineSegment(sketch, "E2650", {"start": v(-65.43, -17.82) * mm, "end": v(-65.28, -17.85) * mm});
            skLineSegment(sketch, "E2651", {"start": v(-65.28, -17.85) * mm, "end": v(-65.12, -17.87) * mm});
            skLineSegment(sketch, "E2652", {"start": v(-65.12, -17.87) * mm, "end": v(-64.97, -17.89) * mm});
            skLineSegment(sketch, "E2653", {"start": v(-64.97, -17.89) * mm, "end": v(-64.82, -17.9) * mm});
            skLineSegment(sketch, "E2654", {"start": v(-64.82, -17.9) * mm, "end": v(-64.68, -17.92) * mm});
            skLineSegment(sketch, "E2655", {"start": v(-64.68, -17.92) * mm, "end": v(-64.53, -17.94) * mm});
            skLineSegment(sketch, "E2656", {"start": v(-64.53, -17.94) * mm, "end": v(-64.39, -17.96) * mm});
            skLineSegment(sketch, "E2657", {"start": v(-64.39, -17.96) * mm, "end": v(-64.25, -17.97) * mm});
            skLineSegment(sketch, "E2658", {"start": v(-64.25, -17.97) * mm, "end": v(-64.1, -17.98) * mm});
            skLineSegment(sketch, "E2659", {"start": v(-64.1, -17.98) * mm, "end": v(-63.97, -18) * mm});
            skLineSegment(sketch, "E2660", {"start": v(-63.97, -18) * mm, "end": v(-63.83, -18) * mm});
            skLineSegment(sketch, "E2661", {"start": v(-63.83, -18) * mm, "end": v(-63.7, -18.02) * mm});
            skLineSegment(sketch, "E2662", {"start": v(-63.7, -18.02) * mm, "end": v(-63.57, -18.03) * mm});
            skLineSegment(sketch, "E2663", {"start": v(-63.57, -18.03) * mm, "end": v(-63.44, -18.04) * mm});
            skLineSegment(sketch, "E2664", {"start": v(-63.44, -18.04) * mm, "end": v(-63.31, -18.04) * mm});
            skLineSegment(sketch, "E2665", {"start": v(-63.31, -18.04) * mm, "end": v(-63.19, -18.05) * mm});
            skLineSegment(sketch, "E2666", {"start": v(-63.19, -18.05) * mm, "end": v(-63.07, -18.06) * mm});
            skLineSegment(sketch, "E2667", {"start": v(-63.07, -18.06) * mm, "end": v(-62.94, -18.06) * mm});
            skLineSegment(sketch, "E2668", {"start": v(-62.94, -18.06) * mm, "end": v(-62.83, -18.07) * mm});
            skLineSegment(sketch, "E2669", {"start": v(-62.83, -18.07) * mm, "end": v(-62.7, -18.07) * mm});
            skLineSegment(sketch, "E2670", {"start": v(-62.7, -18.07) * mm, "end": v(-62.6, -18.07) * mm});
            skLineSegment(sketch, "E2671", {"start": v(-62.6, -18.07) * mm, "end": v(-62.48, -18.08) * mm});
            skLineSegment(sketch, "E2672", {"start": v(-62.48, -18.08) * mm, "end": v(-62.37, -18.08) * mm});
            skLineSegment(sketch, "E2673", {"start": v(-62.37, -18.08) * mm, "end": v(-62.26, -18.08) * mm});
            skLineSegment(sketch, "E2674", {"start": v(-62.26, -18.08) * mm, "end": v(-62.05, -18.08) * mm});
            skLineSegment(sketch, "E2675", {"start": v(-62.05, -18.08) * mm, "end": v(-61.95, -18.08) * mm});
            skLineSegment(sketch, "E2676", {"start": v(-61.95, -18.08) * mm, "end": v(-61.85, -18.08) * mm});
            skLineSegment(sketch, "E2677", {"start": v(-61.85, -18.08) * mm, "end": v(-61.75, -18.07) * mm});
            skLineSegment(sketch, "E2678", {"start": v(-61.75, -18.07) * mm, "end": v(-61.66, -18.07) * mm});
            skLineSegment(sketch, "E2679", {"start": v(-61.66, -18.07) * mm, "end": v(-61.56, -18.07) * mm});
            skLineSegment(sketch, "E2680", {"start": v(-61.56, -18.07) * mm, "end": v(-61.47, -18.06) * mm});
            skLineSegment(sketch, "E2681", {"start": v(-61.47, -18.06) * mm, "end": v(-61.38, -18.06) * mm});
            skLineSegment(sketch, "E2682", {"start": v(-61.38, -18.06) * mm, "end": v(-61.3, -18.06) * mm});
            skLineSegment(sketch, "E2683", {"start": v(-61.3, -18.06) * mm, "end": v(-61.21, -18.05) * mm});
            skLineSegment(sketch, "E2684", {"start": v(-61.21, -18.05) * mm, "end": v(-61.13, -18.05) * mm});
            skLineSegment(sketch, "E2685", {"start": v(-61.13, -18.05) * mm, "end": v(-60.94, -18.24) * mm});
            skLineSegment(sketch, "E2686", {"start": v(-60.94, -18.24) * mm, "end": v(-60.5, -19.66) * mm});
            skLineSegment(sketch, "E2687", {"start": v(-60.5, -19.66) * mm, "end": v(-60.54, -19.92) * mm});
            skLineSegment(sketch, "E2688", {"start": v(-60.54, -19.92) * mm, "end": v(-60.61, -19.97) * mm});
            skLineSegment(sketch, "E2689", {"start": v(-60.61, -19.97) * mm, "end": v(-60.69, -20.01) * mm});
            skLineSegment(sketch, "E2690", {"start": v(-60.69, -20.01) * mm, "end": v(-60.76, -20.06) * mm});
            skLineSegment(sketch, "E2691", {"start": v(-60.76, -20.06) * mm, "end": v(-60.84, -20.1) * mm});
            skLineSegment(sketch, "E2692", {"start": v(-60.84, -20.1) * mm, "end": v(-60.91, -20.16) * mm});
            skLineSegment(sketch, "E2693", {"start": v(-60.91, -20.16) * mm, "end": v(-61, -20.2) * mm});
            skLineSegment(sketch, "E2694", {"start": v(-61, -20.2) * mm, "end": v(-61.07, -20.26) * mm});
            skLineSegment(sketch, "E2695", {"start": v(-61.07, -20.26) * mm, "end": v(-61.15, -20.31) * mm});
            skLineSegment(sketch, "E2696", {"start": v(-61.15, -20.31) * mm, "end": v(-61.24, -20.37) * mm});
            skLineSegment(sketch, "E2697", {"start": v(-61.24, -20.37) * mm, "end": v(-61.32, -20.43) * mm});
            skLineSegment(sketch, "E2698", {"start": v(-61.32, -20.43) * mm, "end": v(-61.4, -20.48) * mm});
            skLineSegment(sketch, "E2699", {"start": v(-61.4, -20.48) * mm, "end": v(-61.5, -20.54) * mm});
            skLineSegment(sketch, "E2700", {"start": v(-61.5, -20.54) * mm, "end": v(-61.58, -20.6) * mm});
            skLineSegment(sketch, "E2701", {"start": v(-61.58, -20.6) * mm, "end": v(-61.67, -20.67) * mm});
            skLineSegment(sketch, "E2702", {"start": v(-61.67, -20.67) * mm, "end": v(-61.76, -20.74) * mm});
            skLineSegment(sketch, "E2703", {"start": v(-61.76, -20.74) * mm, "end": v(-61.86, -20.8) * mm});
            skLineSegment(sketch, "E2704", {"start": v(-61.86, -20.8) * mm, "end": v(-61.95, -20.87) * mm});
            skLineSegment(sketch, "E2705", {"start": v(-61.95, -20.87) * mm, "end": v(-62.04, -20.94) * mm});
            skLineSegment(sketch, "E2706", {"start": v(-62.04, -20.94) * mm, "end": v(-62.14, -21.02) * mm});
            skLineSegment(sketch, "E2707", {"start": v(-62.14, -21.02) * mm, "end": v(-62.24, -21.1) * mm});
            skLineSegment(sketch, "E2708", {"start": v(-62.24, -21.1) * mm, "end": v(-62.34, -21.17) * mm});
            skLineSegment(sketch, "E2709", {"start": v(-62.34, -21.17) * mm, "end": v(-62.44, -21.25) * mm});
            skLineSegment(sketch, "E2710", {"start": v(-62.44, -21.25) * mm, "end": v(-62.54, -21.33) * mm});
            skLineSegment(sketch, "E2711", {"start": v(-62.54, -21.33) * mm, "end": v(-62.64, -21.41) * mm});
            skLineSegment(sketch, "E2712", {"start": v(-62.64, -21.41) * mm, "end": v(-62.74, -21.5) * mm});
            skLineSegment(sketch, "E2713", {"start": v(-62.74, -21.5) * mm, "end": v(-62.85, -21.58) * mm});
            skLineSegment(sketch, "E2714", {"start": v(-62.85, -21.58) * mm, "end": v(-62.96, -21.67) * mm});
            skLineSegment(sketch, "E2715", {"start": v(-62.96, -21.67) * mm, "end": v(-63.06, -21.76) * mm});
            skLineSegment(sketch, "E2716", {"start": v(-63.06, -21.76) * mm, "end": v(-63.17, -21.85) * mm});
            skLineSegment(sketch, "E2717", {"start": v(-63.17, -21.85) * mm, "end": v(-63.28, -21.95) * mm});
            skLineSegment(sketch, "E2718", {"start": v(-63.28, -21.95) * mm, "end": v(-63.39, -22.04) * mm});
            skLineSegment(sketch, "E2719", {"start": v(-63.39, -22.04) * mm, "end": v(-63.5, -22.14) * mm});
            skLineSegment(sketch, "E2720", {"start": v(-63.5, -22.14) * mm, "end": v(-63.61, -22.24) * mm});
            skLineSegment(sketch, "E2721", {"start": v(-63.61, -22.24) * mm, "end": v(-63.73, -22.35) * mm});
            skLineSegment(sketch, "E2722", {"start": v(-63.73, -22.35) * mm, "end": v(-63.84, -22.45) * mm});
            skLineSegment(sketch, "E2723", {"start": v(-63.84, -22.45) * mm, "end": v(-63.95, -22.56) * mm});
            skLineSegment(sketch, "E2724", {"start": v(-63.95, -22.56) * mm, "end": v(-64.07, -22.66) * mm});
            skLineSegment(sketch, "E2725", {"start": v(-64.07, -22.66) * mm, "end": v(-64.19, -22.78) * mm});
            skLineSegment(sketch, "E2726", {"start": v(-64.19, -22.78) * mm, "end": v(-64.3, -22.89) * mm});
            skLineSegment(sketch, "E2727", {"start": v(-64.3, -22.89) * mm, "end": v(-64.37, -22.98) * mm});
            skLineSegment(sketch, "E2728", {"start": v(-64.37, -22.98) * mm, "end": v(-63.8, -24.51) * mm});
            skLineSegment(sketch, "E2729", {"start": v(-63.8, -24.51) * mm, "end": v(-63.7, -24.54) * mm});
            skLineSegment(sketch, "E2730", {"start": v(-63.7, -24.54) * mm, "end": v(-63.53, -24.55) * mm});
            skLineSegment(sketch, "E2731", {"start": v(-63.53, -24.55) * mm, "end": v(-63.37, -24.56) * mm});
            skLineSegment(sketch, "E2732", {"start": v(-63.37, -24.56) * mm, "end": v(-63.21, -24.57) * mm});
            skLineSegment(sketch, "E2733", {"start": v(-63.21, -24.57) * mm, "end": v(-63.05, -24.57) * mm});
            skLineSegment(sketch, "E2734", {"start": v(-63.05, -24.57) * mm, "end": v(-62.9, -24.58) * mm});
            skLineSegment(sketch, "E2735", {"start": v(-62.9, -24.58) * mm, "end": v(-62.75, -24.58) * mm});
            skLineSegment(sketch, "E2736", {"start": v(-62.75, -24.58) * mm, "end": v(-62.6, -24.58) * mm});
            skLineSegment(sketch, "E2737", {"start": v(-62.6, -24.58) * mm, "end": v(-62.45, -24.59) * mm});
            skLineSegment(sketch, "E2738", {"start": v(-62.45, -24.59) * mm, "end": v(-62.3, -24.59) * mm});
            skLineSegment(sketch, "E2739", {"start": v(-62.3, -24.59) * mm, "end": v(-62.02, -24.59) * mm});
            skLineSegment(sketch, "E2740", {"start": v(-62.02, -24.59) * mm, "end": v(-61.88, -24.59) * mm});
            skLineSegment(sketch, "E2741", {"start": v(-61.88, -24.59) * mm, "end": v(-61.74, -24.58) * mm});
            skLineSegment(sketch, "E2742", {"start": v(-61.74, -24.58) * mm, "end": v(-61.6, -24.58) * mm});
            skLineSegment(sketch, "E2743", {"start": v(-61.6, -24.58) * mm, "end": v(-61.47, -24.58) * mm});
            skLineSegment(sketch, "E2744", {"start": v(-61.47, -24.58) * mm, "end": v(-61.34, -24.57) * mm});
            skLineSegment(sketch, "E2745", {"start": v(-61.34, -24.57) * mm, "end": v(-61.2, -24.57) * mm});
            skLineSegment(sketch, "E2746", {"start": v(-61.2, -24.57) * mm, "end": v(-61.08, -24.56) * mm});
            skLineSegment(sketch, "E2747", {"start": v(-61.08, -24.56) * mm, "end": v(-60.96, -24.56) * mm});
            skLineSegment(sketch, "E2748", {"start": v(-60.96, -24.56) * mm, "end": v(-60.83, -24.55) * mm});
            skLineSegment(sketch, "E2749", {"start": v(-60.83, -24.55) * mm, "end": v(-60.71, -24.54) * mm});
            skLineSegment(sketch, "E2750", {"start": v(-60.71, -24.54) * mm, "end": v(-60.6, -24.53) * mm});
            skLineSegment(sketch, "E2751", {"start": v(-60.6, -24.53) * mm, "end": v(-60.48, -24.53) * mm});
            skLineSegment(sketch, "E2752", {"start": v(-60.48, -24.53) * mm, "end": v(-60.25, -24.5) * mm});
            skLineSegment(sketch, "E2753", {"start": v(-60.25, -24.5) * mm, "end": v(-60.14, -24.5) * mm});
            skLineSegment(sketch, "E2754", {"start": v(-60.14, -24.5) * mm, "end": v(-60.03, -24.49) * mm});
            skLineSegment(sketch, "E2755", {"start": v(-60.03, -24.49) * mm, "end": v(-59.93, -24.48) * mm});
            skLineSegment(sketch, "E2756", {"start": v(-59.93, -24.48) * mm, "end": v(-59.82, -24.47) * mm});
            skLineSegment(sketch, "E2757", {"start": v(-59.82, -24.47) * mm, "end": v(-59.72, -24.45) * mm});
            skLineSegment(sketch, "E2758", {"start": v(-59.72, -24.45) * mm, "end": v(-59.62, -24.44) * mm});
            skLineSegment(sketch, "E2759", {"start": v(-59.62, -24.44) * mm, "end": v(-59.53, -24.43) * mm});
            skLineSegment(sketch, "E2760", {"start": v(-59.53, -24.43) * mm, "end": v(-59.43, -24.42) * mm});
            skLineSegment(sketch, "E2761", {"start": v(-59.43, -24.42) * mm, "end": v(-59.34, -24.4) * mm});
            skLineSegment(sketch, "E2762", {"start": v(-59.34, -24.4) * mm, "end": v(-59.25, -24.4) * mm});
            skLineSegment(sketch, "E2763", {"start": v(-59.25, -24.4) * mm, "end": v(-59.16, -24.38) * mm});
            skLineSegment(sketch, "E2764", {"start": v(-59.16, -24.38) * mm, "end": v(-59.07, -24.36) * mm});
            skLineSegment(sketch, "E2765", {"start": v(-59.07, -24.36) * mm, "end": v(-58.99, -24.35) * mm});
            skLineSegment(sketch, "E2766", {"start": v(-58.99, -24.35) * mm, "end": v(-58.9, -24.34) * mm});
            skLineSegment(sketch, "E2767", {"start": v(-58.9, -24.34) * mm, "end": v(-58.7, -24.51) * mm});
            skLineSegment(sketch, "E2768", {"start": v(-58.7, -24.51) * mm, "end": v(-58.11, -25.87) * mm});
            skLineSegment(sketch, "E2769", {"start": v(-58.11, -25.87) * mm, "end": v(-58.13, -26.14) * mm});
            skLineSegment(sketch, "E2770", {"start": v(-58.13, -26.14) * mm, "end": v(-58.2, -26.2) * mm});
            skLineSegment(sketch, "E2771", {"start": v(-58.2, -26.2) * mm, "end": v(-58.26, -26.25) * mm});
            skLineSegment(sketch, "E2772", {"start": v(-58.26, -26.25) * mm, "end": v(-58.33, -26.3) * mm});
            skLineSegment(sketch, "E2773", {"start": v(-58.33, -26.3) * mm, "end": v(-58.4, -26.35) * mm});
            skLineSegment(sketch, "E2774", {"start": v(-58.4, -26.35) * mm, "end": v(-58.47, -26.41) * mm});
            skLineSegment(sketch, "E2775", {"start": v(-58.47, -26.41) * mm, "end": v(-58.55, -26.47) * mm});
            skLineSegment(sketch, "E2776", {"start": v(-58.55, -26.47) * mm, "end": v(-58.62, -26.53) * mm});
            skLineSegment(sketch, "E2777", {"start": v(-58.62, -26.53) * mm, "end": v(-58.7, -26.6) * mm});
            skLineSegment(sketch, "E2778", {"start": v(-58.7, -26.6) * mm, "end": v(-58.77, -26.66) * mm});
            skLineSegment(sketch, "E2779", {"start": v(-58.77, -26.66) * mm, "end": v(-58.85, -26.72) * mm});
            skLineSegment(sketch, "E2780", {"start": v(-58.85, -26.72) * mm, "end": v(-58.93, -26.8) * mm});
            skLineSegment(sketch, "E2781", {"start": v(-58.93, -26.8) * mm, "end": v(-59, -26.86) * mm});
            skLineSegment(sketch, "E2782", {"start": v(-59, -26.86) * mm, "end": v(-59.1, -26.93) * mm});
            skLineSegment(sketch, "E2783", {"start": v(-59.1, -26.93) * mm, "end": v(-59.17, -27) * mm});
            skLineSegment(sketch, "E2784", {"start": v(-59.17, -27) * mm, "end": v(-59.26, -27.08) * mm});
            skLineSegment(sketch, "E2785", {"start": v(-59.26, -27.08) * mm, "end": v(-59.34, -27.16) * mm});
            skLineSegment(sketch, "E2786", {"start": v(-59.34, -27.16) * mm, "end": v(-59.43, -27.24) * mm});
            skLineSegment(sketch, "E2787", {"start": v(-59.43, -27.24) * mm, "end": v(-59.52, -27.32) * mm});
            skLineSegment(sketch, "E2788", {"start": v(-59.52, -27.32) * mm, "end": v(-59.6, -27.4) * mm});
            skLineSegment(sketch, "E2789", {"start": v(-59.6, -27.4) * mm, "end": v(-59.7, -27.48) * mm});
            skLineSegment(sketch, "E2790", {"start": v(-59.7, -27.48) * mm, "end": v(-59.78, -27.57) * mm});
            skLineSegment(sketch, "E2791", {"start": v(-59.78, -27.57) * mm, "end": v(-59.87, -27.66) * mm});
            skLineSegment(sketch, "E2792", {"start": v(-59.87, -27.66) * mm, "end": v(-59.97, -27.75) * mm});
            skLineSegment(sketch, "E2793", {"start": v(-59.97, -27.75) * mm, "end": v(-60.06, -27.84) * mm});
            skLineSegment(sketch, "E2794", {"start": v(-60.06, -27.84) * mm, "end": v(-60.15, -27.94) * mm});
            skLineSegment(sketch, "E2795", {"start": v(-60.15, -27.94) * mm, "end": v(-60.25, -28.03) * mm});
            skLineSegment(sketch, "E2796", {"start": v(-60.25, -28.03) * mm, "end": v(-60.35, -28.13) * mm});
            skLineSegment(sketch, "E2797", {"start": v(-60.35, -28.13) * mm, "end": v(-60.44, -28.23) * mm});
            skLineSegment(sketch, "E2798", {"start": v(-60.44, -28.23) * mm, "end": v(-60.54, -28.34) * mm});
            skLineSegment(sketch, "E2799", {"start": v(-60.54, -28.34) * mm, "end": v(-60.64, -28.44) * mm});
            skLineSegment(sketch, "E2800", {"start": v(-60.64, -28.44) * mm, "end": v(-60.74, -28.55) * mm});
            skLineSegment(sketch, "E2801", {"start": v(-60.74, -28.55) * mm, "end": v(-60.94, -28.77) * mm});
            skLineSegment(sketch, "E2802", {"start": v(-60.94, -28.77) * mm, "end": v(-61.04, -28.88) * mm});
            skLineSegment(sketch, "E2803", {"start": v(-61.04, -28.88) * mm, "end": v(-61.14, -29) * mm});
            skLineSegment(sketch, "E2804", {"start": v(-61.14, -29) * mm, "end": v(-61.25, -29.12) * mm});
            skLineSegment(sketch, "E2805", {"start": v(-61.25, -29.12) * mm, "end": v(-61.35, -29.24) * mm});
            skLineSegment(sketch, "E2806", {"start": v(-61.35, -29.24) * mm, "end": v(-61.45, -29.36) * mm});
            skLineSegment(sketch, "E2807", {"start": v(-61.45, -29.36) * mm, "end": v(-61.56, -29.48) * mm});
            skLineSegment(sketch, "E2808", {"start": v(-61.56, -29.48) * mm, "end": v(-61.61, -29.59) * mm});
            skLineSegment(sketch, "E2809", {"start": v(-61.61, -29.59) * mm, "end": v(-60.9, -31.05) * mm});
            skLineSegment(sketch, "E2810", {"start": v(-60.9, -31.05) * mm, "end": v(-60.78, -31.07) * mm});
            skLineSegment(sketch, "E2811", {"start": v(-60.78, -31.07) * mm, "end": v(-60.62, -31.06) * mm});
            skLineSegment(sketch, "E2812", {"start": v(-60.62, -31.06) * mm, "end": v(-60.45, -31.05) * mm});
            skLineSegment(sketch, "E2813", {"start": v(-60.45, -31.05) * mm, "end": v(-60.3, -31.04) * mm});
            skLineSegment(sketch, "E2814", {"start": v(-60.3, -31.04) * mm, "end": v(-60.14, -31.03) * mm});
            skLineSegment(sketch, "E2815", {"start": v(-60.14, -31.03) * mm, "end": v(-59.99, -31.02) * mm});
            skLineSegment(sketch, "E2816", {"start": v(-59.99, -31.02) * mm, "end": v(-59.83, -31) * mm});
            skLineSegment(sketch, "E2817", {"start": v(-59.83, -31) * mm, "end": v(-59.68, -31) * mm});
            skLineSegment(sketch, "E2818", {"start": v(-59.68, -31) * mm, "end": v(-59.54, -30.98) * mm});
            skLineSegment(sketch, "E2819", {"start": v(-59.54, -30.98) * mm, "end": v(-59.4, -30.96) * mm});
            skLineSegment(sketch, "E2820", {"start": v(-59.4, -30.96) * mm, "end": v(-59.25, -30.95) * mm});
            skLineSegment(sketch, "E2821", {"start": v(-59.25, -30.95) * mm, "end": v(-59.1, -30.93) * mm});
            skLineSegment(sketch, "E2822", {"start": v(-59.1, -30.93) * mm, "end": v(-58.97, -30.92) * mm});
            skLineSegment(sketch, "E2823", {"start": v(-58.97, -30.92) * mm, "end": v(-58.83, -30.9) * mm});
            skLineSegment(sketch, "E2824", {"start": v(-58.83, -30.9) * mm, "end": v(-58.7, -30.89) * mm});
            skLineSegment(sketch, "E2825", {"start": v(-58.7, -30.89) * mm, "end": v(-58.56, -30.87) * mm});
            skLineSegment(sketch, "E2826", {"start": v(-58.56, -30.87) * mm, "end": v(-58.43, -30.85) * mm});
            skLineSegment(sketch, "E2827", {"start": v(-58.43, -30.85) * mm, "end": v(-58.3, -30.83) * mm});
            skLineSegment(sketch, "E2828", {"start": v(-58.3, -30.83) * mm, "end": v(-58.18, -30.81) * mm});
            skLineSegment(sketch, "E2829", {"start": v(-58.18, -30.81) * mm, "end": v(-58.06, -30.8) * mm});
            skLineSegment(sketch, "E2830", {"start": v(-58.06, -30.8) * mm, "end": v(-57.93, -30.77) * mm});
            skLineSegment(sketch, "E2831", {"start": v(-57.93, -30.77) * mm, "end": v(-57.81, -30.75) * mm});
            skLineSegment(sketch, "E2832", {"start": v(-57.81, -30.75) * mm, "end": v(-57.7, -30.73) * mm});
            skLineSegment(sketch, "E2833", {"start": v(-57.7, -30.73) * mm, "end": v(-57.58, -30.71) * mm});
            skLineSegment(sketch, "E2834", {"start": v(-57.58, -30.71) * mm, "end": v(-57.47, -30.7) * mm});
            skLineSegment(sketch, "E2835", {"start": v(-57.47, -30.7) * mm, "end": v(-57.36, -30.67) * mm});
            skLineSegment(sketch, "E2836", {"start": v(-57.36, -30.67) * mm, "end": v(-57.25, -30.65) * mm});
            skLineSegment(sketch, "E2837", {"start": v(-57.25, -30.65) * mm, "end": v(-57.14, -30.63) * mm});
            skLineSegment(sketch, "E2838", {"start": v(-57.14, -30.63) * mm, "end": v(-57.04, -30.6) * mm});
            skLineSegment(sketch, "E2839", {"start": v(-57.04, -30.6) * mm, "end": v(-56.94, -30.58) * mm});
            skLineSegment(sketch, "E2840", {"start": v(-56.94, -30.58) * mm, "end": v(-56.84, -30.56) * mm});
            skLineSegment(sketch, "E2841", {"start": v(-56.84, -30.56) * mm, "end": v(-56.74, -30.54) * mm});
            skLineSegment(sketch, "E2842", {"start": v(-56.74, -30.54) * mm, "end": v(-56.65, -30.52) * mm});
            skLineSegment(sketch, "E2843", {"start": v(-56.65, -30.52) * mm, "end": v(-56.55, -30.5) * mm});
            skLineSegment(sketch, "E2844", {"start": v(-56.55, -30.5) * mm, "end": v(-56.46, -30.47) * mm});
            skLineSegment(sketch, "E2845", {"start": v(-56.46, -30.47) * mm, "end": v(-56.37, -30.45) * mm});
            skLineSegment(sketch, "E2846", {"start": v(-56.37, -30.45) * mm, "end": v(-56.29, -30.43) * mm});
            skLineSegment(sketch, "E2847", {"start": v(-56.29, -30.43) * mm, "end": v(-56.2, -30.4) * mm});
            skLineSegment(sketch, "E2848", {"start": v(-56.2, -30.4) * mm, "end": v(-56.12, -30.38) * mm});
            skLineSegment(sketch, "E2849", {"start": v(-56.12, -30.38) * mm, "end": v(-56.04, -30.36) * mm});
            skLineSegment(sketch, "E2850", {"start": v(-56.04, -30.36) * mm, "end": v(-55.81, -30.51) * mm});
            skLineSegment(sketch, "E2851", {"start": v(-55.81, -30.51) * mm, "end": v(-55.09, -31.8) * mm});
            skLineSegment(sketch, "E2852", {"start": v(-55.09, -31.8) * mm, "end": v(-55.08, -32.08) * mm});
            skLineSegment(sketch, "E2853", {"start": v(-55.08, -32.08) * mm, "end": v(-55.14, -32.13) * mm});
            skLineSegment(sketch, "E2854", {"start": v(-55.14, -32.13) * mm, "end": v(-55.2, -32.2) * mm});
            skLineSegment(sketch, "E2855", {"start": v(-55.2, -32.2) * mm, "end": v(-55.26, -32.25) * mm});
            skLineSegment(sketch, "E2856", {"start": v(-55.26, -32.25) * mm, "end": v(-55.33, -32.32) * mm});
            skLineSegment(sketch, "E2857", {"start": v(-55.33, -32.32) * mm, "end": v(-55.4, -32.38) * mm});
            skLineSegment(sketch, "E2858", {"start": v(-55.4, -32.38) * mm, "end": v(-55.46, -32.44) * mm});
            skLineSegment(sketch, "E2859", {"start": v(-55.46, -32.44) * mm, "end": v(-55.53, -32.51) * mm});
            skLineSegment(sketch, "E2860", {"start": v(-55.53, -32.51) * mm, "end": v(-55.6, -32.58) * mm});
            skLineSegment(sketch, "E2861", {"start": v(-55.6, -32.58) * mm, "end": v(-55.66, -32.65) * mm});
            skLineSegment(sketch, "E2862", {"start": v(-55.66, -32.65) * mm, "end": v(-55.8, -32.8) * mm});
            skLineSegment(sketch, "E2863", {"start": v(-55.8, -32.8) * mm, "end": v(-55.88, -32.88) * mm});
            skLineSegment(sketch, "E2864", {"start": v(-55.88, -32.88) * mm, "end": v(-55.95, -32.96) * mm});
            skLineSegment(sketch, "E2865", {"start": v(-55.95, -32.96) * mm, "end": v(-56.03, -33.04) * mm});
            skLineSegment(sketch, "E2866", {"start": v(-56.03, -33.04) * mm, "end": v(-56.1, -33.13) * mm});
            skLineSegment(sketch, "E2867", {"start": v(-56.1, -33.13) * mm, "end": v(-56.18, -33.21) * mm});
            skLineSegment(sketch, "E2868", {"start": v(-56.18, -33.21) * mm, "end": v(-56.26, -33.3) * mm});
            skLineSegment(sketch, "E2869", {"start": v(-56.26, -33.3) * mm, "end": v(-56.33, -33.39) * mm});
            skLineSegment(sketch, "E2870", {"start": v(-56.33, -33.39) * mm, "end": v(-56.41, -33.48) * mm});
            skLineSegment(sketch, "E2871", {"start": v(-56.41, -33.48) * mm, "end": v(-56.5, -33.57) * mm});
            skLineSegment(sketch, "E2872", {"start": v(-56.5, -33.57) * mm, "end": v(-56.57, -33.67) * mm});
            skLineSegment(sketch, "E2873", {"start": v(-56.57, -33.67) * mm, "end": v(-56.66, -33.77) * mm});
            skLineSegment(sketch, "E2874", {"start": v(-56.66, -33.77) * mm, "end": v(-56.82, -33.97) * mm});
            skLineSegment(sketch, "E2875", {"start": v(-56.82, -33.97) * mm, "end": v(-56.9, -34.07) * mm});
            skLineSegment(sketch, "E2876", {"start": v(-56.9, -34.07) * mm, "end": v(-56.99, -34.18) * mm});
            skLineSegment(sketch, "E2877", {"start": v(-56.99, -34.18) * mm, "end": v(-57.07, -34.29) * mm});
            skLineSegment(sketch, "E2878", {"start": v(-57.07, -34.29) * mm, "end": v(-57.16, -34.4) * mm});
            skLineSegment(sketch, "E2879", {"start": v(-57.16, -34.4) * mm, "end": v(-57.25, -34.51) * mm});
            skLineSegment(sketch, "E2880", {"start": v(-57.25, -34.51) * mm, "end": v(-57.33, -34.62) * mm});
            skLineSegment(sketch, "E2881", {"start": v(-57.33, -34.62) * mm, "end": v(-57.42, -34.74) * mm});
            skLineSegment(sketch, "E2882", {"start": v(-57.42, -34.74) * mm, "end": v(-57.5, -34.86) * mm});
            skLineSegment(sketch, "E2883", {"start": v(-57.5, -34.86) * mm, "end": v(-57.6, -34.98) * mm});
            skLineSegment(sketch, "E2884", {"start": v(-57.6, -34.98) * mm, "end": v(-57.69, -35.1) * mm});
            skLineSegment(sketch, "E2885", {"start": v(-57.69, -35.1) * mm, "end": v(-57.78, -35.23) * mm});
            skLineSegment(sketch, "E2886", {"start": v(-57.78, -35.23) * mm, "end": v(-57.87, -35.36) * mm});
            skLineSegment(sketch, "E2887", {"start": v(-57.87, -35.36) * mm, "end": v(-57.96, -35.5) * mm});
            skLineSegment(sketch, "E2888", {"start": v(-57.96, -35.5) * mm, "end": v(-58.05, -35.62) * mm});
            skLineSegment(sketch, "E2889", {"start": v(-58.05, -35.62) * mm, "end": v(-58.14, -35.76) * mm});
            skLineSegment(sketch, "E2890", {"start": v(-58.14, -35.76) * mm, "end": v(-58.18, -35.86) * mm});
            skLineSegment(sketch, "E2891", {"start": v(-58.18, -35.86) * mm, "end": v(-57.31, -37.24) * mm});
            skLineSegment(sketch, "E2892", {"start": v(-57.31, -37.24) * mm, "end": v(-57.2, -37.25) * mm});
            skLineSegment(sketch, "E2893", {"start": v(-57.2, -37.25) * mm, "end": v(-57.04, -37.22) * mm});
            skLineSegment(sketch, "E2894", {"start": v(-57.04, -37.22) * mm, "end": v(-56.88, -37.2) * mm});
            skLineSegment(sketch, "E2895", {"start": v(-56.88, -37.2) * mm, "end": v(-56.72, -37.17) * mm});
            skLineSegment(sketch, "E2896", {"start": v(-56.72, -37.17) * mm, "end": v(-56.57, -37.14) * mm});
            skLineSegment(sketch, "E2897", {"start": v(-56.57, -37.14) * mm, "end": v(-56.42, -37.12) * mm});
            skLineSegment(sketch, "E2898", {"start": v(-56.42, -37.12) * mm, "end": v(-56.27, -37.09) * mm});
            skLineSegment(sketch, "E2899", {"start": v(-56.27, -37.09) * mm, "end": v(-56.12, -37.06) * mm});
            skLineSegment(sketch, "E2900", {"start": v(-56.12, -37.06) * mm, "end": v(-55.97, -37.03) * mm});
            skLineSegment(sketch, "E2901", {"start": v(-55.97, -37.03) * mm, "end": v(-55.83, -37) * mm});
            skLineSegment(sketch, "E2902", {"start": v(-55.83, -37) * mm, "end": v(-55.69, -36.97) * mm});
            skLineSegment(sketch, "E2903", {"start": v(-55.69, -36.97) * mm, "end": v(-55.55, -36.94) * mm});
            skLineSegment(sketch, "E2904", {"start": v(-55.55, -36.94) * mm, "end": v(-55.41, -36.91) * mm});
            skLineSegment(sketch, "E2905", {"start": v(-55.41, -36.91) * mm, "end": v(-55.28, -36.88) * mm});
            skLineSegment(sketch, "E2906", {"start": v(-55.28, -36.88) * mm, "end": v(-55.14, -36.85) * mm});
            skLineSegment(sketch, "E2907", {"start": v(-55.14, -36.85) * mm, "end": v(-55.02, -36.82) * mm});
            skLineSegment(sketch, "E2908", {"start": v(-55.02, -36.82) * mm, "end": v(-54.89, -36.79) * mm});
            skLineSegment(sketch, "E2909", {"start": v(-54.89, -36.79) * mm, "end": v(-54.76, -36.76) * mm});
            skLineSegment(sketch, "E2910", {"start": v(-54.76, -36.76) * mm, "end": v(-54.64, -36.73) * mm});
            skLineSegment(sketch, "E2911", {"start": v(-54.64, -36.73) * mm, "end": v(-54.52, -36.7) * mm});
            skLineSegment(sketch, "E2912", {"start": v(-54.52, -36.7) * mm, "end": v(-54.4, -36.66) * mm});
            skLineSegment(sketch, "E2913", {"start": v(-54.4, -36.66) * mm, "end": v(-54.28, -36.63) * mm});
            skLineSegment(sketch, "E2914", {"start": v(-54.28, -36.63) * mm, "end": v(-54.17, -36.6) * mm});
            skLineSegment(sketch, "E2915", {"start": v(-54.17, -36.6) * mm, "end": v(-54.06, -36.56) * mm});
            skLineSegment(sketch, "E2916", {"start": v(-54.06, -36.56) * mm, "end": v(-53.95, -36.53) * mm});
            skLineSegment(sketch, "E2917", {"start": v(-53.95, -36.53) * mm, "end": v(-53.84, -36.5) * mm});
            skLineSegment(sketch, "E2918", {"start": v(-53.84, -36.5) * mm, "end": v(-53.73, -36.47) * mm});
            skLineSegment(sketch, "E2919", {"start": v(-53.73, -36.47) * mm, "end": v(-53.63, -36.43) * mm});
            skLineSegment(sketch, "E2920", {"start": v(-53.63, -36.43) * mm, "end": v(-53.53, -36.4) * mm});
            skLineSegment(sketch, "E2921", {"start": v(-53.53, -36.4) * mm, "end": v(-53.43, -36.37) * mm});
            skLineSegment(sketch, "E2922", {"start": v(-53.43, -36.37) * mm, "end": v(-53.33, -36.34) * mm});
            skLineSegment(sketch, "E2923", {"start": v(-53.33, -36.34) * mm, "end": v(-53.24, -36.3) * mm});
            skLineSegment(sketch, "E2924", {"start": v(-53.24, -36.3) * mm, "end": v(-53.15, -36.27) * mm});
            skLineSegment(sketch, "E2925", {"start": v(-53.15, -36.27) * mm, "end": v(-53.06, -36.24) * mm});
            skLineSegment(sketch, "E2926", {"start": v(-53.06, -36.24) * mm, "end": v(-52.97, -36.2) * mm});
            skLineSegment(sketch, "E2927", {"start": v(-52.97, -36.2) * mm, "end": v(-52.88, -36.18) * mm});
            skLineSegment(sketch, "E2928", {"start": v(-52.88, -36.18) * mm, "end": v(-52.8, -36.15) * mm});
            skLineSegment(sketch, "E2929", {"start": v(-52.8, -36.15) * mm, "end": v(-52.72, -36.11) * mm});
            skLineSegment(sketch, "E2930", {"start": v(-52.72, -36.11) * mm, "end": v(-52.64, -36.08) * mm});
            skLineSegment(sketch, "E2931", {"start": v(-52.64, -36.08) * mm, "end": v(-52.56, -36.05) * mm});
            skLineSegment(sketch, "E2932", {"start": v(-52.56, -36.05) * mm, "end": v(-52.32, -36.18) * mm});
            skLineSegment(sketch, "E2933", {"start": v(-52.32, -36.18) * mm, "end": v(-51.46, -37.39) * mm});
            skLineSegment(sketch, "E2934", {"start": v(-51.46, -37.39) * mm, "end": v(-51.42, -37.66) * mm});
            skLineSegment(sketch, "E2935", {"start": v(-51.42, -37.66) * mm, "end": v(-51.48, -37.72) * mm});
            skLineSegment(sketch, "E2936", {"start": v(-51.48, -37.72) * mm, "end": v(-51.53, -37.79) * mm});
            skLineSegment(sketch, "E2937", {"start": v(-51.53, -37.79) * mm, "end": v(-51.59, -37.85) * mm});
            skLineSegment(sketch, "E2938", {"start": v(-51.59, -37.85) * mm, "end": v(-51.64, -37.92) * mm});
            skLineSegment(sketch, "E2939", {"start": v(-51.64, -37.92) * mm, "end": v(-51.7, -38) * mm});
            skLineSegment(sketch, "E2940", {"start": v(-51.7, -38) * mm, "end": v(-51.76, -38.06) * mm});
            skLineSegment(sketch, "E2941", {"start": v(-51.76, -38.06) * mm, "end": v(-51.82, -38.14) * mm});
            skLineSegment(sketch, "E2942", {"start": v(-51.82, -38.14) * mm, "end": v(-51.88, -38.22) * mm});
            skLineSegment(sketch, "E2943", {"start": v(-51.88, -38.22) * mm, "end": v(-51.95, -38.3) * mm});
            skLineSegment(sketch, "E2944", {"start": v(-51.95, -38.3) * mm, "end": v(-52, -38.37) * mm});
            skLineSegment(sketch, "E2945", {"start": v(-52, -38.37) * mm, "end": v(-52.07, -38.46) * mm});
            skLineSegment(sketch, "E2946", {"start": v(-52.07, -38.46) * mm, "end": v(-52.14, -38.54) * mm});
            skLineSegment(sketch, "E2947", {"start": v(-52.14, -38.54) * mm, "end": v(-52.2, -38.63) * mm});
            skLineSegment(sketch, "E2948", {"start": v(-52.2, -38.63) * mm, "end": v(-52.27, -38.72) * mm});
            skLineSegment(sketch, "E2949", {"start": v(-52.27, -38.72) * mm, "end": v(-52.33, -38.8) * mm});
            skLineSegment(sketch, "E2950", {"start": v(-52.33, -38.8) * mm, "end": v(-52.4, -38.9) * mm});
            skLineSegment(sketch, "E2951", {"start": v(-52.4, -38.9) * mm, "end": v(-52.47, -39) * mm});
            skLineSegment(sketch, "E2952", {"start": v(-52.47, -39) * mm, "end": v(-52.54, -39.1) * mm});
            skLineSegment(sketch, "E2953", {"start": v(-52.54, -39.1) * mm, "end": v(-52.6, -39.2) * mm});
            skLineSegment(sketch, "E2954", {"start": v(-52.6, -39.2) * mm, "end": v(-52.67, -39.3) * mm});
            skLineSegment(sketch, "E2955", {"start": v(-52.67, -39.3) * mm, "end": v(-52.74, -39.4) * mm});
            skLineSegment(sketch, "E2956", {"start": v(-52.74, -39.4) * mm, "end": v(-52.82, -39.5) * mm});
            skLineSegment(sketch, "E2957", {"start": v(-52.82, -39.5) * mm, "end": v(-52.96, -39.72) * mm});
            skLineSegment(sketch, "E2958", {"start": v(-52.96, -39.72) * mm, "end": v(-53.03, -39.83) * mm});
            skLineSegment(sketch, "E2959", {"start": v(-53.03, -39.83) * mm, "end": v(-53.1, -39.95) * mm});
            skLineSegment(sketch, "E2960", {"start": v(-53.1, -39.95) * mm, "end": v(-53.18, -40.07) * mm});
            skLineSegment(sketch, "E2961", {"start": v(-53.18, -40.07) * mm, "end": v(-53.25, -40.18) * mm});
            skLineSegment(sketch, "E2962", {"start": v(-53.25, -40.18) * mm, "end": v(-53.33, -40.3) * mm});
            skLineSegment(sketch, "E2963", {"start": v(-53.33, -40.3) * mm, "end": v(-53.4, -40.43) * mm});
            skLineSegment(sketch, "E2964", {"start": v(-53.4, -40.43) * mm, "end": v(-53.48, -40.55) * mm});
            skLineSegment(sketch, "E2965", {"start": v(-53.48, -40.55) * mm, "end": v(-53.55, -40.68) * mm});
            skLineSegment(sketch, "E2966", {"start": v(-53.55, -40.68) * mm, "end": v(-53.63, -40.81) * mm});
            skLineSegment(sketch, "E2967", {"start": v(-53.63, -40.81) * mm, "end": v(-53.7, -40.94) * mm});
            skLineSegment(sketch, "E2968", {"start": v(-53.7, -40.94) * mm, "end": v(-53.78, -41.08) * mm});
            skLineSegment(sketch, "E2969", {"start": v(-53.78, -41.08) * mm, "end": v(-53.86, -41.21) * mm});
            skLineSegment(sketch, "E2970", {"start": v(-53.86, -41.21) * mm, "end": v(-53.93, -41.35) * mm});
            skLineSegment(sketch, "E2971", {"start": v(-53.93, -41.35) * mm, "end": v(-54, -41.5) * mm});
            skLineSegment(sketch, "E2972", {"start": v(-54, -41.5) * mm, "end": v(-54.09, -41.64) * mm});
            skLineSegment(sketch, "E2973", {"start": v(-54.09, -41.64) * mm, "end": v(-54.12, -41.75) * mm});
            skLineSegment(sketch, "E2974", {"start": v(-54.12, -41.75) * mm, "end": v(-53.1, -43.03) * mm});
            skLineSegment(sketch, "E2975", {"start": v(-53.1, -43.03) * mm, "end": v(-53, -43.02) * mm});
            skLineSegment(sketch, "E2976", {"start": v(-53, -43.02) * mm, "end": v(-52.83, -42.98) * mm});
            skLineSegment(sketch, "E2977", {"start": v(-52.83, -42.98) * mm, "end": v(-52.68, -42.94) * mm});
            skLineSegment(sketch, "E2978", {"start": v(-52.68, -42.94) * mm, "end": v(-52.53, -42.9) * mm});
            skLineSegment(sketch, "E2979", {"start": v(-52.53, -42.9) * mm, "end": v(-52.38, -42.85) * mm});
            skLineSegment(sketch, "E2980", {"start": v(-52.38, -42.85) * mm, "end": v(-52.23, -42.81) * mm});
            skLineSegment(sketch, "E2981", {"start": v(-52.23, -42.81) * mm, "end": v(-52.08, -42.77) * mm});
            skLineSegment(sketch, "E2982", {"start": v(-52.08, -42.77) * mm, "end": v(-51.94, -42.72) * mm});
            skLineSegment(sketch, "E2983", {"start": v(-51.94, -42.72) * mm, "end": v(-51.8, -42.68) * mm});
            skLineSegment(sketch, "E2984", {"start": v(-51.8, -42.68) * mm, "end": v(-51.65, -42.64) * mm});
            skLineSegment(sketch, "E2985", {"start": v(-51.65, -42.64) * mm, "end": v(-51.52, -42.6) * mm});
            skLineSegment(sketch, "E2986", {"start": v(-51.52, -42.6) * mm, "end": v(-51.38, -42.55) * mm});
            skLineSegment(sketch, "E2987", {"start": v(-51.38, -42.55) * mm, "end": v(-51.25, -42.5) * mm});
            skLineSegment(sketch, "E2988", {"start": v(-51.25, -42.5) * mm, "end": v(-51.12, -42.46) * mm});
            skLineSegment(sketch, "E2989", {"start": v(-51.12, -42.46) * mm, "end": v(-51, -42.41) * mm});
            skLineSegment(sketch, "E2990", {"start": v(-51, -42.41) * mm, "end": v(-50.87, -42.37) * mm});
            skLineSegment(sketch, "E2991", {"start": v(-50.87, -42.37) * mm, "end": v(-50.74, -42.33) * mm});
            skLineSegment(sketch, "E2992", {"start": v(-50.74, -42.33) * mm, "end": v(-50.62, -42.28) * mm});
            skLineSegment(sketch, "E2993", {"start": v(-50.62, -42.28) * mm, "end": v(-50.5, -42.24) * mm});
            skLineSegment(sketch, "E2994", {"start": v(-50.5, -42.24) * mm, "end": v(-50.38, -42.2) * mm});
            skLineSegment(sketch, "E2995", {"start": v(-50.38, -42.2) * mm, "end": v(-50.27, -42.15) * mm});
            skLineSegment(sketch, "E2996", {"start": v(-50.27, -42.15) * mm, "end": v(-50.16, -42.1) * mm});
            skLineSegment(sketch, "E2997", {"start": v(-50.16, -42.1) * mm, "end": v(-50.05, -42.06) * mm});
            skLineSegment(sketch, "E2998", {"start": v(-50.05, -42.06) * mm, "end": v(-49.94, -42.01) * mm});
            skLineSegment(sketch, "E2999", {"start": v(-49.94, -42.01) * mm, "end": v(-49.83, -41.97) * mm});
            skLineSegment(sketch, "E3000", {"start": v(-49.83, -41.97) * mm, "end": v(-49.73, -41.93) * mm});
            skLineSegment(sketch, "E3001", {"start": v(-49.73, -41.93) * mm, "end": v(-49.63, -41.88) * mm});
            skLineSegment(sketch, "E3002", {"start": v(-49.63, -41.88) * mm, "end": v(-49.53, -41.84) * mm});
            skLineSegment(sketch, "E3003", {"start": v(-49.53, -41.84) * mm, "end": v(-49.43, -41.8) * mm});
            skLineSegment(sketch, "E3004", {"start": v(-49.43, -41.8) * mm, "end": v(-49.34, -41.75) * mm});
            skLineSegment(sketch, "E3005", {"start": v(-49.34, -41.75) * mm, "end": v(-49.24, -41.71) * mm});
            skLineSegment(sketch, "E3006", {"start": v(-49.24, -41.71) * mm, "end": v(-49.15, -41.67) * mm});
            skLineSegment(sketch, "E3007", {"start": v(-49.15, -41.67) * mm, "end": v(-49.06, -41.63) * mm});
            skLineSegment(sketch, "E3008", {"start": v(-49.06, -41.63) * mm, "end": v(-48.98, -41.59) * mm});
            skLineSegment(sketch, "E3009", {"start": v(-48.98, -41.59) * mm, "end": v(-48.9, -41.55) * mm});
            skLineSegment(sketch, "E3010", {"start": v(-48.9, -41.55) * mm, "end": v(-48.81, -41.5) * mm});
            skLineSegment(sketch, "E3011", {"start": v(-48.81, -41.5) * mm, "end": v(-48.73, -41.47) * mm});
            skLineSegment(sketch, "E3012", {"start": v(-48.73, -41.47) * mm, "end": v(-48.65, -41.43) * mm});
            skLineSegment(sketch, "E3013", {"start": v(-48.65, -41.43) * mm, "end": v(-48.58, -41.39) * mm});
            skLineSegment(sketch, "E3014", {"start": v(-48.58, -41.39) * mm, "end": v(-48.5, -41.35) * mm});
            skLineSegment(sketch, "E3015", {"start": v(-48.5, -41.35) * mm, "end": v(-48.25, -41.45) * mm});
            skLineSegment(sketch, "E3016", {"start": v(-48.25, -41.45) * mm, "end": v(-47.27, -42.56) * mm});
            skLineSegment(sketch, "E3017", {"start": v(-47.27, -42.56) * mm, "end": v(-47.2, -42.83) * mm});
            skLineSegment(sketch, "E3018", {"start": v(-47.2, -42.83) * mm, "end": v(-47.25, -42.9) * mm});
            skLineSegment(sketch, "E3019", {"start": v(-47.25, -42.9) * mm, "end": v(-47.3, -42.96) * mm});
            skLineSegment(sketch, "E3020", {"start": v(-47.3, -42.96) * mm, "end": v(-47.35, -43.04) * mm});
            skLineSegment(sketch, "E3021", {"start": v(-47.35, -43.04) * mm, "end": v(-47.4, -43.11) * mm});
            skLineSegment(sketch, "E3022", {"start": v(-47.4, -43.11) * mm, "end": v(-47.45, -43.19) * mm});
            skLineSegment(sketch, "E3023", {"start": v(-47.45, -43.19) * mm, "end": v(-47.5, -43.27) * mm});
            skLineSegment(sketch, "E3024", {"start": v(-47.5, -43.27) * mm, "end": v(-47.55, -43.35) * mm});
            skLineSegment(sketch, "E3025", {"start": v(-47.55, -43.35) * mm, "end": v(-47.6, -43.43) * mm});
            skLineSegment(sketch, "E3026", {"start": v(-47.6, -43.43) * mm, "end": v(-47.66, -43.51) * mm});
            skLineSegment(sketch, "E3027", {"start": v(-47.66, -43.51) * mm, "end": v(-47.71, -43.6) * mm});
            skLineSegment(sketch, "E3028", {"start": v(-47.71, -43.6) * mm, "end": v(-47.77, -43.69) * mm});
            skLineSegment(sketch, "E3029", {"start": v(-47.77, -43.69) * mm, "end": v(-47.82, -43.78) * mm});
            skLineSegment(sketch, "E3030", {"start": v(-47.82, -43.78) * mm, "end": v(-47.88, -43.87) * mm});
            skLineSegment(sketch, "E3031", {"start": v(-47.88, -43.87) * mm, "end": v(-47.93, -43.97) * mm});
            skLineSegment(sketch, "E3032", {"start": v(-47.93, -43.97) * mm, "end": v(-47.99, -44.07) * mm});
            skLineSegment(sketch, "E3033", {"start": v(-47.99, -44.07) * mm, "end": v(-48.05, -44.16) * mm});
            skLineSegment(sketch, "E3034", {"start": v(-48.05, -44.16) * mm, "end": v(-48.1, -44.27) * mm});
            skLineSegment(sketch, "E3035", {"start": v(-48.1, -44.27) * mm, "end": v(-48.16, -44.37) * mm});
            skLineSegment(sketch, "E3036", {"start": v(-48.16, -44.37) * mm, "end": v(-48.22, -44.48) * mm});
            skLineSegment(sketch, "E3037", {"start": v(-48.22, -44.48) * mm, "end": v(-48.28, -44.59) * mm});
            skLineSegment(sketch, "E3038", {"start": v(-48.28, -44.59) * mm, "end": v(-48.34, -44.7) * mm});
            skLineSegment(sketch, "E3039", {"start": v(-48.34, -44.7) * mm, "end": v(-48.4, -44.8) * mm});
            skLineSegment(sketch, "E3040", {"start": v(-48.4, -44.8) * mm, "end": v(-48.46, -44.92) * mm});
            skLineSegment(sketch, "E3041", {"start": v(-48.46, -44.92) * mm, "end": v(-48.52, -45.04) * mm});
            skLineSegment(sketch, "E3042", {"start": v(-48.52, -45.04) * mm, "end": v(-48.58, -45.16) * mm});
            skLineSegment(sketch, "E3043", {"start": v(-48.58, -45.16) * mm, "end": v(-48.64, -45.28) * mm});
            skLineSegment(sketch, "E3044", {"start": v(-48.64, -45.28) * mm, "end": v(-48.7, -45.4) * mm});
            skLineSegment(sketch, "E3045", {"start": v(-48.7, -45.4) * mm, "end": v(-48.76, -45.53) * mm});
            skLineSegment(sketch, "E3046", {"start": v(-48.76, -45.53) * mm, "end": v(-48.82, -45.66) * mm});
            skLineSegment(sketch, "E3047", {"start": v(-48.82, -45.66) * mm, "end": v(-48.88, -45.79) * mm});
            skLineSegment(sketch, "E3048", {"start": v(-48.88, -45.79) * mm, "end": v(-48.94, -45.92) * mm});
            skLineSegment(sketch, "E3049", {"start": v(-48.94, -45.92) * mm, "end": v(-49, -46.06) * mm});
            skLineSegment(sketch, "E3050", {"start": v(-49, -46.06) * mm, "end": v(-49.07, -46.2) * mm});
            skLineSegment(sketch, "E3051", {"start": v(-49.07, -46.2) * mm, "end": v(-49.13, -46.33) * mm});
            skLineSegment(sketch, "E3052", {"start": v(-49.13, -46.33) * mm, "end": v(-49.2, -46.47) * mm});
            skLineSegment(sketch, "E3053", {"start": v(-49.2, -46.47) * mm, "end": v(-49.25, -46.62) * mm});
            skLineSegment(sketch, "E3054", {"start": v(-49.25, -46.62) * mm, "end": v(-49.31, -46.77) * mm});
            skLineSegment(sketch, "E3055", {"start": v(-49.31, -46.77) * mm, "end": v(-49.38, -46.91) * mm});
            skLineSegment(sketch, "E3056", {"start": v(-49.38, -46.91) * mm, "end": v(-49.44, -47.06) * mm});
            skLineSegment(sketch, "E3057", {"start": v(-49.44, -47.06) * mm, "end": v(-49.46, -47.18) * mm});
            skLineSegment(sketch, "E3058", {"start": v(-49.46, -47.18) * mm, "end": v(-48.32, -48.34) * mm});
            skLineSegment(sketch, "E3059", {"start": v(-48.32, -48.34) * mm, "end": v(-48.2, -48.33) * mm});
            skLineSegment(sketch, "E3060", {"start": v(-48.2, -48.33) * mm, "end": v(-48.05, -48.27) * mm});
            skLineSegment(sketch, "E3061", {"start": v(-48.05, -48.27) * mm, "end": v(-47.9, -48.2) * mm});
            skLineSegment(sketch, "E3062", {"start": v(-47.9, -48.2) * mm, "end": v(-47.75, -48.15) * mm});
            skLineSegment(sketch, "E3063", {"start": v(-47.75, -48.15) * mm, "end": v(-47.6, -48.1) * mm});
            skLineSegment(sketch, "E3064", {"start": v(-47.6, -48.1) * mm, "end": v(-47.47, -48.04) * mm});
            skLineSegment(sketch, "E3065", {"start": v(-47.47, -48.04) * mm, "end": v(-47.32, -47.98) * mm});
            skLineSegment(sketch, "E3066", {"start": v(-47.32, -47.98) * mm, "end": v(-47.19, -47.92) * mm});
            skLineSegment(sketch, "E3067", {"start": v(-47.19, -47.92) * mm, "end": v(-47.05, -47.86) * mm});
            skLineSegment(sketch, "E3068", {"start": v(-47.05, -47.86) * mm, "end": v(-46.92, -47.8) * mm});
            skLineSegment(sketch, "E3069", {"start": v(-46.92, -47.8) * mm, "end": v(-46.78, -47.74) * mm});
            skLineSegment(sketch, "E3070", {"start": v(-46.78, -47.74) * mm, "end": v(-46.65, -47.69) * mm});
            skLineSegment(sketch, "E3071", {"start": v(-46.65, -47.69) * mm, "end": v(-46.53, -47.63) * mm});
            skLineSegment(sketch, "E3072", {"start": v(-46.53, -47.63) * mm, "end": v(-46.4, -47.57) * mm});
            skLineSegment(sketch, "E3073", {"start": v(-46.4, -47.57) * mm, "end": v(-46.28, -47.51) * mm});
            skLineSegment(sketch, "E3074", {"start": v(-46.28, -47.51) * mm, "end": v(-46.16, -47.45) * mm});
            skLineSegment(sketch, "E3075", {"start": v(-46.16, -47.45) * mm, "end": v(-46.04, -47.4) * mm});
            skLineSegment(sketch, "E3076", {"start": v(-46.04, -47.4) * mm, "end": v(-45.92, -47.34) * mm});
            skLineSegment(sketch, "E3077", {"start": v(-45.92, -47.34) * mm, "end": v(-45.81, -47.28) * mm});
            skLineSegment(sketch, "E3078", {"start": v(-45.81, -47.28) * mm, "end": v(-45.7, -47.23) * mm});
            skLineSegment(sketch, "E3079", {"start": v(-45.7, -47.23) * mm, "end": v(-45.59, -47.17) * mm});
            skLineSegment(sketch, "E3080", {"start": v(-45.59, -47.17) * mm, "end": v(-45.48, -47.12) * mm});
            skLineSegment(sketch, "E3081", {"start": v(-45.48, -47.12) * mm, "end": v(-45.38, -47.06) * mm});
            skLineSegment(sketch, "E3082", {"start": v(-45.38, -47.06) * mm, "end": v(-45.27, -47) * mm});
            skLineSegment(sketch, "E3083", {"start": v(-45.27, -47) * mm, "end": v(-45.17, -46.95) * mm});
            skLineSegment(sketch, "E3084", {"start": v(-45.17, -46.95) * mm, "end": v(-45.07, -46.9) * mm});
            skLineSegment(sketch, "E3085", {"start": v(-45.07, -46.9) * mm, "end": v(-44.98, -46.84) * mm});
            skLineSegment(sketch, "E3086", {"start": v(-44.98, -46.84) * mm, "end": v(-44.88, -46.79) * mm});
            skLineSegment(sketch, "E3087", {"start": v(-44.88, -46.79) * mm, "end": v(-44.8, -46.73) * mm});
            skLineSegment(sketch, "E3088", {"start": v(-44.8, -46.73) * mm, "end": v(-44.7, -46.68) * mm});
            skLineSegment(sketch, "E3089", {"start": v(-44.7, -46.68) * mm, "end": v(-44.61, -46.63) * mm});
            skLineSegment(sketch, "E3090", {"start": v(-44.61, -46.63) * mm, "end": v(-44.53, -46.58) * mm});
            skLineSegment(sketch, "E3091", {"start": v(-44.53, -46.58) * mm, "end": v(-44.44, -46.53) * mm});
            skLineSegment(sketch, "E3092", {"start": v(-44.44, -46.53) * mm, "end": v(-44.36, -46.48) * mm});
            skLineSegment(sketch, "E3093", {"start": v(-44.36, -46.48) * mm, "end": v(-44.28, -46.43) * mm});
            skLineSegment(sketch, "E3094", {"start": v(-44.28, -46.43) * mm, "end": v(-44.2, -46.38) * mm});
            skLineSegment(sketch, "E3095", {"start": v(-44.2, -46.38) * mm, "end": v(-44.13, -46.33) * mm});
            skLineSegment(sketch, "E3096", {"start": v(-44.13, -46.33) * mm, "end": v(-44.06, -46.29) * mm});
            skLineSegment(sketch, "E3097", {"start": v(-44.06, -46.29) * mm, "end": v(-43.98, -46.24) * mm});
            skLineSegment(sketch, "E3098", {"start": v(-43.98, -46.24) * mm, "end": v(-43.92, -46.2) * mm});
            skLineSegment(sketch, "E3099", {"start": v(-43.92, -46.2) * mm, "end": v(-43.65, -46.27) * mm});
            skLineSegment(sketch, "E3100", {"start": v(-43.65, -46.27) * mm, "end": v(-42.56, -47.27) * mm});
            skLineSegment(sketch, "E3101", {"start": v(-42.56, -47.27) * mm, "end": v(-42.47, -47.53) * mm});
            skLineSegment(sketch, "E3102", {"start": v(-42.47, -47.53) * mm, "end": v(-42.5, -47.6) * mm});
            skLineSegment(sketch, "E3103", {"start": v(-42.5, -47.6) * mm, "end": v(-42.6, -47.75) * mm});
            skLineSegment(sketch, "E3104", {"start": v(-42.6, -47.75) * mm, "end": v(-42.63, -47.83) * mm});
            skLineSegment(sketch, "E3105", {"start": v(-42.63, -47.83) * mm, "end": v(-42.67, -47.91) * mm});
            skLineSegment(sketch, "E3106", {"start": v(-42.67, -47.91) * mm, "end": v(-42.72, -48) * mm});
            skLineSegment(sketch, "E3107", {"start": v(-42.72, -48) * mm, "end": v(-42.8, -48.17) * mm});
            skLineSegment(sketch, "E3108", {"start": v(-42.8, -48.17) * mm, "end": v(-42.85, -48.26) * mm});
            skLineSegment(sketch, "E3109", {"start": v(-42.85, -48.26) * mm, "end": v(-42.9, -48.35) * mm});
            skLineSegment(sketch, "E3110", {"start": v(-42.9, -48.35) * mm, "end": v(-42.94, -48.44) * mm});
            skLineSegment(sketch, "E3111", {"start": v(-42.94, -48.44) * mm, "end": v(-42.98, -48.54) * mm});
            skLineSegment(sketch, "E3112", {"start": v(-42.98, -48.54) * mm, "end": v(-43.03, -48.64) * mm});
            skLineSegment(sketch, "E3113", {"start": v(-43.03, -48.64) * mm, "end": v(-43.07, -48.74) * mm});
            skLineSegment(sketch, "E3114", {"start": v(-43.07, -48.74) * mm, "end": v(-43.12, -48.84) * mm});
            skLineSegment(sketch, "E3115", {"start": v(-43.12, -48.84) * mm, "end": v(-43.17, -48.95) * mm});
            skLineSegment(sketch, "E3116", {"start": v(-43.17, -48.95) * mm, "end": v(-43.21, -49.05) * mm});
            skLineSegment(sketch, "E3117", {"start": v(-43.21, -49.05) * mm, "end": v(-43.26, -49.16) * mm});
            skLineSegment(sketch, "E3118", {"start": v(-43.26, -49.16) * mm, "end": v(-43.3, -49.27) * mm});
            skLineSegment(sketch, "E3119", {"start": v(-43.3, -49.27) * mm, "end": v(-43.35, -49.39) * mm});
            skLineSegment(sketch, "E3120", {"start": v(-43.35, -49.39) * mm, "end": v(-43.4, -49.5) * mm});
            skLineSegment(sketch, "E3121", {"start": v(-43.4, -49.5) * mm, "end": v(-43.45, -49.62) * mm});
            skLineSegment(sketch, "E3122", {"start": v(-43.45, -49.62) * mm, "end": v(-43.5, -49.74) * mm});
            skLineSegment(sketch, "E3123", {"start": v(-43.5, -49.74) * mm, "end": v(-43.54, -49.86) * mm});
            skLineSegment(sketch, "E3124", {"start": v(-43.54, -49.86) * mm, "end": v(-43.6, -49.99) * mm});
            skLineSegment(sketch, "E3125", {"start": v(-43.6, -49.99) * mm, "end": v(-43.64, -50.12) * mm});
            skLineSegment(sketch, "E3126", {"start": v(-43.64, -50.12) * mm, "end": v(-43.69, -50.25) * mm});
            skLineSegment(sketch, "E3127", {"start": v(-43.69, -50.25) * mm, "end": v(-43.73, -50.38) * mm});
            skLineSegment(sketch, "E3128", {"start": v(-43.73, -50.38) * mm, "end": v(-43.78, -50.51) * mm});
            skLineSegment(sketch, "E3129", {"start": v(-43.78, -50.51) * mm, "end": v(-43.83, -50.65) * mm});
            skLineSegment(sketch, "E3130", {"start": v(-43.83, -50.65) * mm, "end": v(-43.88, -50.78) * mm});
            skLineSegment(sketch, "E3131", {"start": v(-43.88, -50.78) * mm, "end": v(-43.92, -50.93) * mm});
            skLineSegment(sketch, "E3132", {"start": v(-43.92, -50.93) * mm, "end": v(-43.97, -51.07) * mm});
            skLineSegment(sketch, "E3133", {"start": v(-43.97, -51.07) * mm, "end": v(-44.02, -51.21) * mm});
            skLineSegment(sketch, "E3134", {"start": v(-44.02, -51.21) * mm, "end": v(-44.06, -51.36) * mm});
            skLineSegment(sketch, "E3135", {"start": v(-44.06, -51.36) * mm, "end": v(-44.1, -51.51) * mm});
            skLineSegment(sketch, "E3136", {"start": v(-44.1, -51.51) * mm, "end": v(-44.16, -51.66) * mm});
            skLineSegment(sketch, "E3137", {"start": v(-44.16, -51.66) * mm, "end": v(-44.2, -51.82) * mm});
            skLineSegment(sketch, "E3138", {"start": v(-44.2, -51.82) * mm, "end": v(-44.25, -51.97) * mm});
            skLineSegment(sketch, "E3139", {"start": v(-44.25, -51.97) * mm, "end": v(-44.25, -52.09) * mm});
            skLineSegment(sketch, "E3140", {"start": v(-44.25, -52.09) * mm, "end": v(-43, -53.13) * mm});
            skLineSegment(sketch, "E3141", {"start": v(-43, -53.13) * mm, "end": v(-42.89, -53.1) * mm});
            skLineSegment(sketch, "E3142", {"start": v(-42.89, -53.1) * mm, "end": v(-42.74, -53.03) * mm});
            skLineSegment(sketch, "E3143", {"start": v(-42.74, -53.03) * mm, "end": v(-42.6, -52.95) * mm});
            skLineSegment(sketch, "E3144", {"start": v(-42.6, -52.95) * mm, "end": v(-42.46, -52.88) * mm});
            skLineSegment(sketch, "E3145", {"start": v(-42.46, -52.88) * mm, "end": v(-42.32, -52.8) * mm});
            skLineSegment(sketch, "E3146", {"start": v(-42.32, -52.8) * mm, "end": v(-42.18, -52.73) * mm});
            skLineSegment(sketch, "E3147", {"start": v(-42.18, -52.73) * mm, "end": v(-42.05, -52.66) * mm});
            skLineSegment(sketch, "E3148", {"start": v(-42.05, -52.66) * mm, "end": v(-41.92, -52.59) * mm});
            skLineSegment(sketch, "E3149", {"start": v(-41.92, -52.59) * mm, "end": v(-41.79, -52.52) * mm});
            skLineSegment(sketch, "E3150", {"start": v(-41.79, -52.52) * mm, "end": v(-41.66, -52.44) * mm});
            skLineSegment(sketch, "E3151", {"start": v(-41.66, -52.44) * mm, "end": v(-41.54, -52.37) * mm});
            skLineSegment(sketch, "E3152", {"start": v(-41.54, -52.37) * mm, "end": v(-41.41, -52.3) * mm});
            skLineSegment(sketch, "E3153", {"start": v(-41.41, -52.3) * mm, "end": v(-41.3, -52.23) * mm});
            skLineSegment(sketch, "E3154", {"start": v(-41.3, -52.23) * mm, "end": v(-41.17, -52.16) * mm});
            skLineSegment(sketch, "E3155", {"start": v(-41.17, -52.16) * mm, "end": v(-41.06, -52.09) * mm});
            skLineSegment(sketch, "E3156", {"start": v(-41.06, -52.09) * mm, "end": v(-40.94, -52.02) * mm});
            skLineSegment(sketch, "E3157", {"start": v(-40.94, -52.02) * mm, "end": v(-40.83, -51.95) * mm});
            skLineSegment(sketch, "E3158", {"start": v(-40.83, -51.95) * mm, "end": v(-40.72, -51.88) * mm});
            skLineSegment(sketch, "E3159", {"start": v(-40.72, -51.88) * mm, "end": v(-40.62, -51.81) * mm});
            skLineSegment(sketch, "E3160", {"start": v(-40.62, -51.81) * mm, "end": v(-40.51, -51.74) * mm});
            skLineSegment(sketch, "E3161", {"start": v(-40.51, -51.74) * mm, "end": v(-40.4, -51.68) * mm});
            skLineSegment(sketch, "E3162", {"start": v(-40.4, -51.68) * mm, "end": v(-40.3, -51.61) * mm});
            skLineSegment(sketch, "E3163", {"start": v(-40.3, -51.61) * mm, "end": v(-40.2, -51.54) * mm});
            skLineSegment(sketch, "E3164", {"start": v(-40.2, -51.54) * mm, "end": v(-40.11, -51.48) * mm});
            skLineSegment(sketch, "E3165", {"start": v(-40.11, -51.48) * mm, "end": v(-40.02, -51.41) * mm});
            skLineSegment(sketch, "E3166", {"start": v(-40.02, -51.41) * mm, "end": v(-39.92, -51.35) * mm});
            skLineSegment(sketch, "E3167", {"start": v(-39.92, -51.35) * mm, "end": v(-39.83, -51.29) * mm});
            skLineSegment(sketch, "E3168", {"start": v(-39.83, -51.29) * mm, "end": v(-39.75, -51.22) * mm});
            skLineSegment(sketch, "E3169", {"start": v(-39.75, -51.22) * mm, "end": v(-39.66, -51.16) * mm});
            skLineSegment(sketch, "E3170", {"start": v(-39.66, -51.16) * mm, "end": v(-39.58, -51.1) * mm});
            skLineSegment(sketch, "E3171", {"start": v(-39.58, -51.1) * mm, "end": v(-39.5, -51.04) * mm});
            skLineSegment(sketch, "E3172", {"start": v(-39.5, -51.04) * mm, "end": v(-39.41, -50.98) * mm});
            skLineSegment(sketch, "E3173", {"start": v(-39.41, -50.98) * mm, "end": v(-39.34, -50.92) * mm});
            skLineSegment(sketch, "E3174", {"start": v(-39.34, -50.92) * mm, "end": v(-39.26, -50.86) * mm});
            skLineSegment(sketch, "E3175", {"start": v(-39.26, -50.86) * mm, "end": v(-39.19, -50.8) * mm});
            skLineSegment(sketch, "E3176", {"start": v(-39.19, -50.8) * mm, "end": v(-39.11, -50.75) * mm});
            skLineSegment(sketch, "E3177", {"start": v(-39.11, -50.75) * mm, "end": v(-39.04, -50.7) * mm});
            skLineSegment(sketch, "E3178", {"start": v(-39.04, -50.7) * mm, "end": v(-38.98, -50.64) * mm});
            skLineSegment(sketch, "E3179", {"start": v(-38.98, -50.64) * mm, "end": v(-38.91, -50.58) * mm});
            skLineSegment(sketch, "E3180", {"start": v(-38.91, -50.58) * mm, "end": v(-38.85, -50.53) * mm});
            skLineSegment(sketch, "E3181", {"start": v(-38.85, -50.53) * mm, "end": v(-38.58, -50.58) * mm});
            skLineSegment(sketch, "E3182", {"start": v(-38.58, -50.58) * mm, "end": v(-37.39, -51.46) * mm});
            skLineSegment(sketch, "E3183", {"start": v(-37.39, -51.46) * mm, "end": v(-37.27, -51.7) * mm});
            skLineSegment(sketch, "E3184", {"start": v(-37.27, -51.7) * mm, "end": v(-37.3, -51.78) * mm});
            skLineSegment(sketch, "E3185", {"start": v(-37.3, -51.78) * mm, "end": v(-37.33, -51.86) * mm});
            skLineSegment(sketch, "E3186", {"start": v(-37.33, -51.86) * mm, "end": v(-37.37, -51.94) * mm});
            skLineSegment(sketch, "E3187", {"start": v(-37.37, -51.94) * mm, "end": v(-37.4, -52.02) * mm});
            skLineSegment(sketch, "E3188", {"start": v(-37.4, -52.02) * mm, "end": v(-37.43, -52.1) * mm});
            skLineSegment(sketch, "E3189", {"start": v(-37.43, -52.1) * mm, "end": v(-37.47, -52.2) * mm});
            skLineSegment(sketch, "E3190", {"start": v(-37.47, -52.2) * mm, "end": v(-37.5, -52.29) * mm});
            skLineSegment(sketch, "E3191", {"start": v(-37.5, -52.29) * mm, "end": v(-37.54, -52.38) * mm});
            skLineSegment(sketch, "E3192", {"start": v(-37.54, -52.38) * mm, "end": v(-37.57, -52.47) * mm});
            skLineSegment(sketch, "E3193", {"start": v(-37.57, -52.47) * mm, "end": v(-37.6, -52.57) * mm});
            skLineSegment(sketch, "E3194", {"start": v(-37.6, -52.57) * mm, "end": v(-37.64, -52.67) * mm});
            skLineSegment(sketch, "E3195", {"start": v(-37.64, -52.67) * mm, "end": v(-37.67, -52.77) * mm});
            skLineSegment(sketch, "E3196", {"start": v(-37.67, -52.77) * mm, "end": v(-37.7, -52.87) * mm});
            skLineSegment(sketch, "E3197", {"start": v(-37.7, -52.87) * mm, "end": v(-37.74, -52.97) * mm});
            skLineSegment(sketch, "E3198", {"start": v(-37.74, -52.97) * mm, "end": v(-37.78, -53.08) * mm});
            skLineSegment(sketch, "E3199", {"start": v(-37.78, -53.08) * mm, "end": v(-37.81, -53.19) * mm});
            skLineSegment(sketch, "E3200", {"start": v(-37.81, -53.19) * mm, "end": v(-37.85, -53.3) * mm});
            skLineSegment(sketch, "E3201", {"start": v(-37.85, -53.3) * mm, "end": v(-37.88, -53.41) * mm});
            skLineSegment(sketch, "E3202", {"start": v(-37.88, -53.41) * mm, "end": v(-37.92, -53.53) * mm});
            skLineSegment(sketch, "E3203", {"start": v(-37.92, -53.53) * mm, "end": v(-37.95, -53.65) * mm});
            skLineSegment(sketch, "E3204", {"start": v(-37.95, -53.65) * mm, "end": v(-37.99, -53.77) * mm});
            skLineSegment(sketch, "E3205", {"start": v(-37.99, -53.77) * mm, "end": v(-38.02, -53.9) * mm});
            skLineSegment(sketch, "E3206", {"start": v(-38.02, -53.9) * mm, "end": v(-38.06, -54.01) * mm});
            skLineSegment(sketch, "E3207", {"start": v(-38.06, -54.01) * mm, "end": v(-38.13, -54.27) * mm});
            skLineSegment(sketch, "E3208", {"start": v(-38.13, -54.27) * mm, "end": v(-38.16, -54.4) * mm});
            skLineSegment(sketch, "E3209", {"start": v(-38.16, -54.4) * mm, "end": v(-38.2, -54.54) * mm});
            skLineSegment(sketch, "E3210", {"start": v(-38.2, -54.54) * mm, "end": v(-38.23, -54.67) * mm});
            skLineSegment(sketch, "E3211", {"start": v(-38.23, -54.67) * mm, "end": v(-38.26, -54.81) * mm});
            skLineSegment(sketch, "E3212", {"start": v(-38.26, -54.81) * mm, "end": v(-38.3, -54.95) * mm});
            skLineSegment(sketch, "E3213", {"start": v(-38.3, -54.95) * mm, "end": v(-38.33, -55.1) * mm});
            skLineSegment(sketch, "E3214", {"start": v(-38.33, -55.1) * mm, "end": v(-38.36, -55.24) * mm});
            skLineSegment(sketch, "E3215", {"start": v(-38.36, -55.24) * mm, "end": v(-38.4, -55.38) * mm});
            skLineSegment(sketch, "E3216", {"start": v(-38.4, -55.38) * mm, "end": v(-38.42, -55.53) * mm});
            skLineSegment(sketch, "E3217", {"start": v(-38.42, -55.53) * mm, "end": v(-38.45, -55.69) * mm});
            skLineSegment(sketch, "E3218", {"start": v(-38.45, -55.69) * mm, "end": v(-38.48, -55.84) * mm});
            skLineSegment(sketch, "E3219", {"start": v(-38.48, -55.84) * mm, "end": v(-38.51, -56) * mm});
            skLineSegment(sketch, "E3220", {"start": v(-38.51, -56) * mm, "end": v(-38.54, -56.15) * mm});
            skLineSegment(sketch, "E3221", {"start": v(-38.54, -56.15) * mm, "end": v(-38.57, -56.31) * mm});
            skLineSegment(sketch, "E3222", {"start": v(-38.57, -56.31) * mm, "end": v(-38.57, -56.43) * mm});
            skLineSegment(sketch, "E3223", {"start": v(-38.57, -56.43) * mm, "end": v(-37.21, -57.33) * mm});
            skLineSegment(sketch, "E3224", {"start": v(-37.21, -57.33) * mm, "end": v(-37.1, -57.3) * mm});
            skLineSegment(sketch, "E3225", {"start": v(-37.1, -57.3) * mm, "end": v(-36.97, -57.2) * mm});
            skLineSegment(sketch, "E3226", {"start": v(-36.97, -57.2) * mm, "end": v(-36.83, -57.12) * mm});
            skLineSegment(sketch, "E3227", {"start": v(-36.83, -57.12) * mm, "end": v(-36.7, -57.03) * mm});
            skLineSegment(sketch, "E3228", {"start": v(-36.7, -57.03) * mm, "end": v(-36.57, -56.94) * mm});
            skLineSegment(sketch, "E3229", {"start": v(-36.57, -56.94) * mm, "end": v(-36.44, -56.85) * mm});
            skLineSegment(sketch, "E3230", {"start": v(-36.44, -56.85) * mm, "end": v(-36.32, -56.77) * mm});
            skLineSegment(sketch, "E3231", {"start": v(-36.32, -56.77) * mm, "end": v(-36.2, -56.68) * mm});
            skLineSegment(sketch, "E3232", {"start": v(-36.2, -56.68) * mm, "end": v(-36.07, -56.6) * mm});
            skLineSegment(sketch, "E3233", {"start": v(-36.07, -56.6) * mm, "end": v(-35.95, -56.51) * mm});
            skLineSegment(sketch, "E3234", {"start": v(-35.95, -56.51) * mm, "end": v(-35.83, -56.43) * mm});
            skLineSegment(sketch, "E3235", {"start": v(-35.83, -56.43) * mm, "end": v(-35.72, -56.34) * mm});
            skLineSegment(sketch, "E3236", {"start": v(-35.72, -56.34) * mm, "end": v(-35.6, -56.26) * mm});
            skLineSegment(sketch, "E3237", {"start": v(-35.6, -56.26) * mm, "end": v(-35.5, -56.18) * mm});
            skLineSegment(sketch, "E3238", {"start": v(-35.5, -56.18) * mm, "end": v(-35.39, -56.1) * mm});
            skLineSegment(sketch, "E3239", {"start": v(-35.39, -56.1) * mm, "end": v(-35.28, -56.01) * mm});
            skLineSegment(sketch, "E3240", {"start": v(-35.28, -56.01) * mm, "end": v(-35.18, -55.93) * mm});
            skLineSegment(sketch, "E3241", {"start": v(-35.18, -55.93) * mm, "end": v(-35.08, -55.85) * mm});
            skLineSegment(sketch, "E3242", {"start": v(-35.08, -55.85) * mm, "end": v(-34.98, -55.77) * mm});
            skLineSegment(sketch, "E3243", {"start": v(-34.98, -55.77) * mm, "end": v(-34.78, -55.62) * mm});
            skLineSegment(sketch, "E3244", {"start": v(-34.78, -55.62) * mm, "end": v(-34.7, -55.54) * mm});
            skLineSegment(sketch, "E3245", {"start": v(-34.7, -55.54) * mm, "end": v(-34.6, -55.46) * mm});
            skLineSegment(sketch, "E3246", {"start": v(-34.6, -55.46) * mm, "end": v(-34.51, -55.4) * mm});
            skLineSegment(sketch, "E3247", {"start": v(-34.51, -55.4) * mm, "end": v(-34.42, -55.31) * mm});
            skLineSegment(sketch, "E3248", {"start": v(-34.42, -55.31) * mm, "end": v(-34.26, -55.17) * mm});
            skLineSegment(sketch, "E3249", {"start": v(-34.26, -55.17) * mm, "end": v(-34.17, -55.1) * mm});
            skLineSegment(sketch, "E3250", {"start": v(-34.17, -55.1) * mm, "end": v(-34.1, -55.03) * mm});
            skLineSegment(sketch, "E3251", {"start": v(-34.1, -55.03) * mm, "end": v(-34.02, -54.96) * mm});
            skLineSegment(sketch, "E3252", {"start": v(-34.02, -54.96) * mm, "end": v(-33.94, -54.89) * mm});
            skLineSegment(sketch, "E3253", {"start": v(-33.94, -54.89) * mm, "end": v(-33.87, -54.82) * mm});
            skLineSegment(sketch, "E3254", {"start": v(-33.87, -54.82) * mm, "end": v(-33.8, -54.75) * mm});
            skLineSegment(sketch, "E3255", {"start": v(-33.8, -54.75) * mm, "end": v(-33.73, -54.69) * mm});
            skLineSegment(sketch, "E3256", {"start": v(-33.73, -54.69) * mm, "end": v(-33.66, -54.62) * mm});
            skLineSegment(sketch, "E3257", {"start": v(-33.66, -54.62) * mm, "end": v(-33.6, -54.56) * mm});
            skLineSegment(sketch, "E3258", {"start": v(-33.6, -54.56) * mm, "end": v(-33.53, -54.5) * mm});
            skLineSegment(sketch, "E3259", {"start": v(-33.53, -54.5) * mm, "end": v(-33.4, -54.37) * mm});
            skLineSegment(sketch, "E3260", {"start": v(-33.4, -54.37) * mm, "end": v(-33.35, -54.31) * mm});
            skLineSegment(sketch, "E3261", {"start": v(-33.35, -54.31) * mm, "end": v(-33.08, -54.33) * mm});
            skLineSegment(sketch, "E3262", {"start": v(-33.08, -54.33) * mm, "end": v(-31.8, -55.09) * mm});
            skLineSegment(sketch, "E3263", {"start": v(-31.8, -55.09) * mm, "end": v(-31.66, -55.32) * mm});
            skLineSegment(sketch, "E3264", {"start": v(-31.66, -55.32) * mm, "end": v(-31.68, -55.4) * mm});
            skLineSegment(sketch, "E3265", {"start": v(-31.68, -55.4) * mm, "end": v(-31.7, -55.48) * mm});
            skLineSegment(sketch, "E3266", {"start": v(-31.7, -55.48) * mm, "end": v(-31.73, -55.56) * mm});
            skLineSegment(sketch, "E3267", {"start": v(-31.73, -55.56) * mm, "end": v(-31.76, -55.65) * mm});
            skLineSegment(sketch, "E3268", {"start": v(-31.76, -55.65) * mm, "end": v(-31.78, -55.74) * mm});
            skLineSegment(sketch, "E3269", {"start": v(-31.78, -55.74) * mm, "end": v(-31.8, -55.83) * mm});
            skLineSegment(sketch, "E3270", {"start": v(-31.8, -55.83) * mm, "end": v(-31.83, -55.92) * mm});
            skLineSegment(sketch, "E3271", {"start": v(-31.83, -55.92) * mm, "end": v(-31.85, -56.01) * mm});
            skLineSegment(sketch, "E3272", {"start": v(-31.85, -56.01) * mm, "end": v(-31.88, -56.11) * mm});
            skLineSegment(sketch, "E3273", {"start": v(-31.88, -56.11) * mm, "end": v(-31.9, -56.21) * mm});
            skLineSegment(sketch, "E3274", {"start": v(-31.9, -56.21) * mm, "end": v(-31.93, -56.31) * mm});
            skLineSegment(sketch, "E3275", {"start": v(-31.93, -56.31) * mm, "end": v(-31.95, -56.42) * mm});
            skLineSegment(sketch, "E3276", {"start": v(-31.95, -56.42) * mm, "end": v(-31.98, -56.52) * mm});
            skLineSegment(sketch, "E3277", {"start": v(-31.98, -56.52) * mm, "end": v(-32.02, -56.74) * mm});
            skLineSegment(sketch, "E3278", {"start": v(-32.02, -56.74) * mm, "end": v(-32.05, -56.85) * mm});
            skLineSegment(sketch, "E3279", {"start": v(-32.05, -56.85) * mm, "end": v(-32.07, -56.97) * mm});
            skLineSegment(sketch, "E3280", {"start": v(-32.07, -56.97) * mm, "end": v(-32.1, -57.08) * mm});
            skLineSegment(sketch, "E3281", {"start": v(-32.1, -57.08) * mm, "end": v(-32.12, -57.2) * mm});
            skLineSegment(sketch, "E3282", {"start": v(-32.12, -57.2) * mm, "end": v(-32.14, -57.32) * mm});
            skLineSegment(sketch, "E3283", {"start": v(-32.14, -57.32) * mm, "end": v(-32.16, -57.44) * mm});
            skLineSegment(sketch, "E3284", {"start": v(-32.16, -57.44) * mm, "end": v(-32.18, -57.57) * mm});
            skLineSegment(sketch, "E3285", {"start": v(-32.18, -57.57) * mm, "end": v(-32.2, -57.7) * mm});
            skLineSegment(sketch, "E3286", {"start": v(-32.2, -57.7) * mm, "end": v(-32.22, -57.83) * mm});
            skLineSegment(sketch, "E3287", {"start": v(-32.22, -57.83) * mm, "end": v(-32.24, -57.96) * mm});
            skLineSegment(sketch, "E3288", {"start": v(-32.24, -57.96) * mm, "end": v(-32.27, -58.1) * mm});
            skLineSegment(sketch, "E3289", {"start": v(-32.27, -58.1) * mm, "end": v(-32.28, -58.23) * mm});
            skLineSegment(sketch, "E3290", {"start": v(-32.28, -58.23) * mm, "end": v(-32.3, -58.37) * mm});
            skLineSegment(sketch, "E3291", {"start": v(-32.3, -58.37) * mm, "end": v(-32.32, -58.51) * mm});
            skLineSegment(sketch, "E3292", {"start": v(-32.32, -58.51) * mm, "end": v(-32.34, -58.65) * mm});
            skLineSegment(sketch, "E3293", {"start": v(-32.34, -58.65) * mm, "end": v(-32.36, -58.8) * mm});
            skLineSegment(sketch, "E3294", {"start": v(-32.36, -58.8) * mm, "end": v(-32.37, -58.95) * mm});
            skLineSegment(sketch, "E3295", {"start": v(-32.37, -58.95) * mm, "end": v(-32.4, -59.1) * mm});
            skLineSegment(sketch, "E3296", {"start": v(-32.4, -59.1) * mm, "end": v(-32.4, -59.25) * mm});
            skLineSegment(sketch, "E3297", {"start": v(-32.4, -59.25) * mm, "end": v(-32.42, -59.4) * mm});
            skLineSegment(sketch, "E3298", {"start": v(-32.42, -59.4) * mm, "end": v(-32.43, -59.56) * mm});
            skLineSegment(sketch, "E3299", {"start": v(-32.43, -59.56) * mm, "end": v(-32.45, -59.71) * mm});
            skLineSegment(sketch, "E3300", {"start": v(-32.45, -59.71) * mm, "end": v(-32.46, -59.88) * mm});
            skLineSegment(sketch, "E3301", {"start": v(-32.46, -59.88) * mm, "end": v(-32.47, -60.04) * mm});
            skLineSegment(sketch, "E3302", {"start": v(-32.47, -60.04) * mm, "end": v(-32.46, -60.15) * mm});
            skLineSegment(sketch, "E3303", {"start": v(-32.46, -60.15) * mm, "end": v(-31.02, -60.9) * mm});
            skLineSegment(sketch, "E3304", {"start": v(-31.02, -60.9) * mm, "end": v(-30.91, -60.86) * mm});
            skLineSegment(sketch, "E3305", {"start": v(-30.91, -60.86) * mm, "end": v(-30.78, -60.75) * mm});
            skLineSegment(sketch, "E3306", {"start": v(-30.78, -60.75) * mm, "end": v(-30.66, -60.65) * mm});
            skLineSegment(sketch, "E3307", {"start": v(-30.66, -60.65) * mm, "end": v(-30.54, -60.55) * mm});
            skLineSegment(sketch, "E3308", {"start": v(-30.54, -60.55) * mm, "end": v(-30.42, -60.45) * mm});
            skLineSegment(sketch, "E3309", {"start": v(-30.42, -60.45) * mm, "end": v(-30.3, -60.35) * mm});
            skLineSegment(sketch, "E3310", {"start": v(-30.3, -60.35) * mm, "end": v(-30.18, -60.25) * mm});
            skLineSegment(sketch, "E3311", {"start": v(-30.18, -60.25) * mm, "end": v(-30.07, -60.15) * mm});
            skLineSegment(sketch, "E3312", {"start": v(-30.07, -60.15) * mm, "end": v(-29.96, -60.06) * mm});
            skLineSegment(sketch, "E3313", {"start": v(-29.96, -60.06) * mm, "end": v(-29.85, -59.96) * mm});
            skLineSegment(sketch, "E3314", {"start": v(-29.85, -59.96) * mm, "end": v(-29.74, -59.86) * mm});
            skLineSegment(sketch, "E3315", {"start": v(-29.74, -59.86) * mm, "end": v(-29.63, -59.77) * mm});
            skLineSegment(sketch, "E3316", {"start": v(-29.63, -59.77) * mm, "end": v(-29.53, -59.67) * mm});
            skLineSegment(sketch, "E3317", {"start": v(-29.53, -59.67) * mm, "end": v(-29.43, -59.58) * mm});
            skLineSegment(sketch, "E3318", {"start": v(-29.43, -59.58) * mm, "end": v(-29.33, -59.49) * mm});
            skLineSegment(sketch, "E3319", {"start": v(-29.33, -59.49) * mm, "end": v(-29.24, -59.4) * mm});
            skLineSegment(sketch, "E3320", {"start": v(-29.24, -59.4) * mm, "end": v(-29.14, -59.3) * mm});
            skLineSegment(sketch, "E3321", {"start": v(-29.14, -59.3) * mm, "end": v(-29.05, -59.21) * mm});
            skLineSegment(sketch, "E3322", {"start": v(-29.05, -59.21) * mm, "end": v(-28.96, -59.12) * mm});
            skLineSegment(sketch, "E3323", {"start": v(-28.96, -59.12) * mm, "end": v(-28.87, -59.04) * mm});
            skLineSegment(sketch, "E3324", {"start": v(-28.87, -59.04) * mm, "end": v(-28.78, -58.95) * mm});
            skLineSegment(sketch, "E3325", {"start": v(-28.78, -58.95) * mm, "end": v(-28.7, -58.86) * mm});
            skLineSegment(sketch, "E3326", {"start": v(-28.7, -58.86) * mm, "end": v(-28.61, -58.78) * mm});
            skLineSegment(sketch, "E3327", {"start": v(-28.61, -58.78) * mm, "end": v(-28.53, -58.7) * mm});
            skLineSegment(sketch, "E3328", {"start": v(-28.53, -58.7) * mm, "end": v(-28.45, -58.61) * mm});
            skLineSegment(sketch, "E3329", {"start": v(-28.45, -58.61) * mm, "end": v(-28.38, -58.53) * mm});
            skLineSegment(sketch, "E3330", {"start": v(-28.38, -58.53) * mm, "end": v(-28.3, -58.45) * mm});
            skLineSegment(sketch, "E3331", {"start": v(-28.3, -58.45) * mm, "end": v(-28.23, -58.37) * mm});
            skLineSegment(sketch, "E3332", {"start": v(-28.23, -58.37) * mm, "end": v(-28.16, -58.29) * mm});
            skLineSegment(sketch, "E3333", {"start": v(-28.16, -58.29) * mm, "end": v(-28.09, -58.21) * mm});
            skLineSegment(sketch, "E3334", {"start": v(-28.09, -58.21) * mm, "end": v(-28.02, -58.14) * mm});
            skLineSegment(sketch, "E3335", {"start": v(-28.02, -58.14) * mm, "end": v(-27.95, -58.06) * mm});
            skLineSegment(sketch, "E3336", {"start": v(-27.95, -58.06) * mm, "end": v(-27.9, -57.99) * mm});
            skLineSegment(sketch, "E3337", {"start": v(-27.9, -57.99) * mm, "end": v(-27.83, -57.91) * mm});
            skLineSegment(sketch, "E3338", {"start": v(-27.83, -57.91) * mm, "end": v(-27.77, -57.84) * mm});
            skLineSegment(sketch, "E3339", {"start": v(-27.77, -57.84) * mm, "end": v(-27.7, -57.77) * mm});
            skLineSegment(sketch, "E3340", {"start": v(-27.7, -57.77) * mm, "end": v(-27.65, -57.7) * mm});
            skLineSegment(sketch, "E3341", {"start": v(-27.65, -57.7) * mm, "end": v(-27.6, -57.63) * mm});
            skLineSegment(sketch, "E3342", {"start": v(-27.6, -57.63) * mm, "end": v(-27.54, -57.57) * mm});
            skLineSegment(sketch, "E3343", {"start": v(-27.54, -57.57) * mm, "end": v(-27.5, -57.5) * mm});
            skLineSegment(sketch, "E3344", {"start": v(-27.5, -57.5) * mm, "end": v(-27.22, -57.5) * mm});
            skLineSegment(sketch, "E3345", {"start": v(-27.22, -57.5) * mm, "end": v(-25.87, -58.11) * mm});
            skLineSegment(sketch, "E3346", {"start": v(-25.87, -58.11) * mm, "end": v(-25.7, -58.32) * mm});
            skLineSegment(sketch, "E3347", {"start": v(-25.7, -58.32) * mm, "end": v(-25.72, -58.4) * mm});
            skLineSegment(sketch, "E3348", {"start": v(-25.72, -58.4) * mm, "end": v(-25.73, -58.49) * mm});
            skLineSegment(sketch, "E3349", {"start": v(-25.73, -58.49) * mm, "end": v(-25.75, -58.57) * mm});
            skLineSegment(sketch, "E3350", {"start": v(-25.75, -58.57) * mm, "end": v(-25.77, -58.66) * mm});
            skLineSegment(sketch, "E3351", {"start": v(-25.77, -58.66) * mm, "end": v(-25.78, -58.75) * mm});
            skLineSegment(sketch, "E3352", {"start": v(-25.78, -58.75) * mm, "end": v(-25.8, -58.85) * mm});
            skLineSegment(sketch, "E3353", {"start": v(-25.8, -58.85) * mm, "end": v(-25.81, -58.94) * mm});
            skLineSegment(sketch, "E3354", {"start": v(-25.81, -58.94) * mm, "end": v(-25.82, -59.04) * mm});
            skLineSegment(sketch, "E3355", {"start": v(-25.82, -59.04) * mm, "end": v(-25.84, -59.14) * mm});
            skLineSegment(sketch, "E3356", {"start": v(-25.84, -59.14) * mm, "end": v(-25.85, -59.24) * mm});
            skLineSegment(sketch, "E3357", {"start": v(-25.85, -59.24) * mm, "end": v(-25.87, -59.34) * mm});
            skLineSegment(sketch, "E3358", {"start": v(-25.87, -59.34) * mm, "end": v(-25.88, -59.45) * mm});
            skLineSegment(sketch, "E3359", {"start": v(-25.88, -59.45) * mm, "end": v(-25.9, -59.55) * mm});
            skLineSegment(sketch, "E3360", {"start": v(-25.9, -59.55) * mm, "end": v(-25.9, -59.66) * mm});
            skLineSegment(sketch, "E3361", {"start": v(-25.9, -59.66) * mm, "end": v(-25.92, -59.78) * mm});
            skLineSegment(sketch, "E3362", {"start": v(-25.92, -59.78) * mm, "end": v(-25.93, -59.89) * mm});
            skLineSegment(sketch, "E3363", {"start": v(-25.93, -59.89) * mm, "end": v(-25.94, -60) * mm});
            skLineSegment(sketch, "E3364", {"start": v(-25.94, -60) * mm, "end": v(-25.95, -60.12) * mm});
            skLineSegment(sketch, "E3365", {"start": v(-25.95, -60.12) * mm, "end": v(-25.96, -60.24) * mm});
            skLineSegment(sketch, "E3366", {"start": v(-25.96, -60.24) * mm, "end": v(-25.97, -60.37) * mm});
            skLineSegment(sketch, "E3367", {"start": v(-25.97, -60.37) * mm, "end": v(-25.98, -60.5) * mm});
            skLineSegment(sketch, "E3368", {"start": v(-25.98, -60.5) * mm, "end": v(-25.99, -60.62) * mm});
            skLineSegment(sketch, "E3369", {"start": v(-25.99, -60.62) * mm, "end": v(-26, -60.75) * mm});
            skLineSegment(sketch, "E3370", {"start": v(-26, -60.75) * mm, "end": v(-26, -60.88) * mm});
            skLineSegment(sketch, "E3371", {"start": v(-26, -60.88) * mm, "end": v(-26.01, -61.01) * mm});
            skLineSegment(sketch, "E3372", {"start": v(-26.01, -61.01) * mm, "end": v(-26.02, -61.15) * mm});
            skLineSegment(sketch, "E3373", {"start": v(-26.02, -61.15) * mm, "end": v(-26.02, -61.29) * mm});
            skLineSegment(sketch, "E3374", {"start": v(-26.02, -61.29) * mm, "end": v(-26.03, -61.43) * mm});
            skLineSegment(sketch, "E3375", {"start": v(-26.03, -61.43) * mm, "end": v(-26.03, -61.57) * mm});
            skLineSegment(sketch, "E3376", {"start": v(-26.03, -61.57) * mm, "end": v(-26.03, -61.71) * mm});
            skLineSegment(sketch, "E3377", {"start": v(-26.03, -61.71) * mm, "end": v(-26.03, -61.86) * mm});
            skLineSegment(sketch, "E3378", {"start": v(-26.03, -61.86) * mm, "end": v(-26.04, -62) * mm});
            skLineSegment(sketch, "E3379", {"start": v(-26.04, -62) * mm, "end": v(-26.04, -62.16) * mm});
            skLineSegment(sketch, "E3380", {"start": v(-26.04, -62.16) * mm, "end": v(-26.04, -62.3) * mm});
            skLineSegment(sketch, "E3381", {"start": v(-26.04, -62.3) * mm, "end": v(-26.03, -62.46) * mm});
            skLineSegment(sketch, "E3382", {"start": v(-26.03, -62.46) * mm, "end": v(-26.03, -62.62) * mm});
            skLineSegment(sketch, "E3383", {"start": v(-26.03, -62.62) * mm, "end": v(-26.03, -62.78) * mm});
            skLineSegment(sketch, "E3384", {"start": v(-26.03, -62.78) * mm, "end": v(-26.02, -62.94) * mm});
            skLineSegment(sketch, "E3385", {"start": v(-26.02, -62.94) * mm, "end": v(-26.02, -63.1) * mm});
            skLineSegment(sketch, "E3386", {"start": v(-26.02, -63.1) * mm, "end": v(-26, -63.22) * mm});
            skLineSegment(sketch, "E3387", {"start": v(-26, -63.22) * mm, "end": v(-24.48, -63.82) * mm});
            skLineSegment(sketch, "E3388", {"start": v(-24.48, -63.82) * mm, "end": v(-24.38, -63.75) * mm});
            skLineSegment(sketch, "E3389", {"start": v(-24.38, -63.75) * mm, "end": v(-24.26, -63.64) * mm});
            skLineSegment(sketch, "E3390", {"start": v(-24.26, -63.64) * mm, "end": v(-24.15, -63.52) * mm});
            skLineSegment(sketch, "E3391", {"start": v(-24.15, -63.52) * mm, "end": v(-24.04, -63.41) * mm});
            skLineSegment(sketch, "E3392", {"start": v(-24.04, -63.41) * mm, "end": v(-23.93, -63.3) * mm});
            skLineSegment(sketch, "E3393", {"start": v(-23.93, -63.3) * mm, "end": v(-23.82, -63.19) * mm});
            skLineSegment(sketch, "E3394", {"start": v(-23.82, -63.19) * mm, "end": v(-23.72, -63.08) * mm});
            skLineSegment(sketch, "E3395", {"start": v(-23.72, -63.08) * mm, "end": v(-23.62, -62.97) * mm});
            skLineSegment(sketch, "E3396", {"start": v(-23.62, -62.97) * mm, "end": v(-23.51, -62.86) * mm});
            skLineSegment(sketch, "E3397", {"start": v(-23.51, -62.86) * mm, "end": v(-23.32, -62.64) * mm});
            skLineSegment(sketch, "E3398", {"start": v(-23.32, -62.64) * mm, "end": v(-23.23, -62.54) * mm});
            skLineSegment(sketch, "E3399", {"start": v(-23.23, -62.54) * mm, "end": v(-23.13, -62.43) * mm});
            skLineSegment(sketch, "E3400", {"start": v(-23.13, -62.43) * mm, "end": v(-22.95, -62.23) * mm});
            skLineSegment(sketch, "E3401", {"start": v(-22.95, -62.23) * mm, "end": v(-22.87, -62.13) * mm});
            skLineSegment(sketch, "E3402", {"start": v(-22.87, -62.13) * mm, "end": v(-22.78, -62.03) * mm});
            skLineSegment(sketch, "E3403", {"start": v(-22.78, -62.03) * mm, "end": v(-22.7, -61.93) * mm});
            skLineSegment(sketch, "E3404", {"start": v(-22.7, -61.93) * mm, "end": v(-22.62, -61.83) * mm});
            skLineSegment(sketch, "E3405", {"start": v(-22.62, -61.83) * mm, "end": v(-22.54, -61.73) * mm});
            skLineSegment(sketch, "E3406", {"start": v(-22.54, -61.73) * mm, "end": v(-22.46, -61.63) * mm});
            skLineSegment(sketch, "E3407", {"start": v(-22.46, -61.63) * mm, "end": v(-22.31, -61.45) * mm});
            skLineSegment(sketch, "E3408", {"start": v(-22.31, -61.45) * mm, "end": v(-22.24, -61.35) * mm});
            skLineSegment(sketch, "E3409", {"start": v(-22.24, -61.35) * mm, "end": v(-22.17, -61.26) * mm});
            skLineSegment(sketch, "E3410", {"start": v(-22.17, -61.26) * mm, "end": v(-22.1, -61.17) * mm});
            skLineSegment(sketch, "E3411", {"start": v(-22.1, -61.17) * mm, "end": v(-22.04, -61.09) * mm});
            skLineSegment(sketch, "E3412", {"start": v(-22.04, -61.09) * mm, "end": v(-21.9, -60.91) * mm});
            skLineSegment(sketch, "E3413", {"start": v(-21.9, -60.91) * mm, "end": v(-21.85, -60.83) * mm});
            skLineSegment(sketch, "E3414", {"start": v(-21.85, -60.83) * mm, "end": v(-21.79, -60.75) * mm});
            skLineSegment(sketch, "E3415", {"start": v(-21.79, -60.75) * mm, "end": v(-21.73, -60.66) * mm});
            skLineSegment(sketch, "E3416", {"start": v(-21.73, -60.66) * mm, "end": v(-21.68, -60.58) * mm});
            skLineSegment(sketch, "E3417", {"start": v(-21.68, -60.58) * mm, "end": v(-21.62, -60.5) * mm});
            skLineSegment(sketch, "E3418", {"start": v(-21.62, -60.5) * mm, "end": v(-21.57, -60.43) * mm});
            skLineSegment(sketch, "E3419", {"start": v(-21.57, -60.43) * mm, "end": v(-21.52, -60.35) * mm});
            skLineSegment(sketch, "E3420", {"start": v(-21.52, -60.35) * mm, "end": v(-21.47, -60.28) * mm});
            skLineSegment(sketch, "E3421", {"start": v(-21.47, -60.28) * mm, "end": v(-21.42, -60.2) * mm});
            skLineSegment(sketch, "E3422", {"start": v(-21.42, -60.2) * mm, "end": v(-21.37, -60.13) * mm});
            skLineSegment(sketch, "E3423", {"start": v(-21.37, -60.13) * mm, "end": v(-21.33, -60.06) * mm});
            skLineSegment(sketch, "E3424", {"start": v(-21.33, -60.06) * mm, "end": v(-21.06, -60.02) * mm});
            skLineSegment(sketch, "E3425", {"start": v(-21.06, -60.02) * mm, "end": v(-19.66, -60.5) * mm});
            skLineSegment(sketch, "E3426", {"start": v(-19.66, -60.5) * mm, "end": v(-19.47, -60.7) * mm});
            skLineSegment(sketch, "E3427", {"start": v(-19.47, -60.7) * mm, "end": v(-19.47, -60.77) * mm});
            skLineSegment(sketch, "E3428", {"start": v(-19.47, -60.77) * mm, "end": v(-19.48, -60.86) * mm});
            skLineSegment(sketch, "E3429", {"start": v(-19.48, -60.86) * mm, "end": v(-19.49, -60.95) * mm});
            skLineSegment(sketch, "E3430", {"start": v(-19.49, -60.95) * mm, "end": v(-19.5, -61.03) * mm});
            skLineSegment(sketch, "E3431", {"start": v(-19.5, -61.03) * mm, "end": v(-19.5, -61.22) * mm});
            skLineSegment(sketch, "E3432", {"start": v(-19.5, -61.22) * mm, "end": v(-19.5, -61.32) * mm});
            skLineSegment(sketch, "E3433", {"start": v(-19.5, -61.32) * mm, "end": v(-19.51, -61.41) * mm});
            skLineSegment(sketch, "E3434", {"start": v(-19.51, -61.41) * mm, "end": v(-19.52, -61.51) * mm});
            skLineSegment(sketch, "E3435", {"start": v(-19.52, -61.51) * mm, "end": v(-19.52, -61.61) * mm});
            skLineSegment(sketch, "E3436", {"start": v(-19.52, -61.61) * mm, "end": v(-19.52, -61.72) * mm});
            skLineSegment(sketch, "E3437", {"start": v(-19.52, -61.72) * mm, "end": v(-19.52, -61.83) * mm});
            skLineSegment(sketch, "E3438", {"start": v(-19.52, -61.83) * mm, "end": v(-19.53, -61.93) * mm});
            skLineSegment(sketch, "E3439", {"start": v(-19.53, -61.93) * mm, "end": v(-19.53, -62.04) * mm});
            skLineSegment(sketch, "E3440", {"start": v(-19.53, -62.04) * mm, "end": v(-19.53, -62.27) * mm});
            skLineSegment(sketch, "E3441", {"start": v(-19.53, -62.27) * mm, "end": v(-19.53, -62.39) * mm});
            skLineSegment(sketch, "E3442", {"start": v(-19.53, -62.39) * mm, "end": v(-19.52, -62.5) * mm});
            skLineSegment(sketch, "E3443", {"start": v(-19.52, -62.5) * mm, "end": v(-19.52, -62.63) * mm});
            skLineSegment(sketch, "E3444", {"start": v(-19.52, -62.63) * mm, "end": v(-19.52, -62.75) * mm});
            skLineSegment(sketch, "E3445", {"start": v(-19.52, -62.75) * mm, "end": v(-19.51, -62.88) * mm});
            skLineSegment(sketch, "E3446", {"start": v(-19.51, -62.88) * mm, "end": v(-19.5, -63.13) * mm});
            skLineSegment(sketch, "E3447", {"start": v(-19.5, -63.13) * mm, "end": v(-19.5, -63.26) * mm});
            skLineSegment(sketch, "E3448", {"start": v(-19.5, -63.26) * mm, "end": v(-19.49, -63.4) * mm});
            skLineSegment(sketch, "E3449", {"start": v(-19.49, -63.4) * mm, "end": v(-19.47, -63.67) * mm});
            skLineSegment(sketch, "E3450", {"start": v(-19.47, -63.67) * mm, "end": v(-19.45, -63.95) * mm});
            skLineSegment(sketch, "E3451", {"start": v(-19.45, -63.95) * mm, "end": v(-19.43, -64.24) * mm});
            skLineSegment(sketch, "E3452", {"start": v(-19.43, -64.24) * mm, "end": v(-19.41, -64.39) * mm});
            skLineSegment(sketch, "E3453", {"start": v(-19.41, -64.39) * mm, "end": v(-19.4, -64.54) * mm});
            skLineSegment(sketch, "E3454", {"start": v(-19.4, -64.54) * mm, "end": v(-19.38, -64.69) * mm});
            skLineSegment(sketch, "E3455", {"start": v(-19.38, -64.69) * mm, "end": v(-19.36, -64.84) * mm});
            skLineSegment(sketch, "E3456", {"start": v(-19.36, -64.84) * mm, "end": v(-19.34, -65) * mm});
            skLineSegment(sketch, "E3457", {"start": v(-19.34, -65) * mm, "end": v(-19.32, -65.16) * mm});
            skLineSegment(sketch, "E3458", {"start": v(-19.32, -65.16) * mm, "end": v(-19.3, -65.32) * mm});
            skLineSegment(sketch, "E3459", {"start": v(-19.3, -65.32) * mm, "end": v(-19.28, -65.48) * mm});
            skLineSegment(sketch, "E3460", {"start": v(-19.28, -65.48) * mm, "end": v(-19.24, -65.59) * mm});
            skLineSegment(sketch, "E3461", {"start": v(-19.24, -65.59) * mm, "end": v(-17.67, -66.03) * mm});
            skLineSegment(sketch, "E3462", {"start": v(-17.67, -66.03) * mm, "end": v(-17.58, -65.95) * mm});
            skLineSegment(sketch, "E3463", {"start": v(-17.58, -65.95) * mm, "end": v(-17.38, -65.7) * mm});
            skLineSegment(sketch, "E3464", {"start": v(-17.38, -65.7) * mm, "end": v(-17.18, -65.45) * mm});
            skLineSegment(sketch, "E3465", {"start": v(-17.18, -65.45) * mm, "end": v(-17, -65.21) * mm});
            skLineSegment(sketch, "E3466", {"start": v(-17, -65.21) * mm, "end": v(-16.9, -65.1) * mm});
            skLineSegment(sketch, "E3467", {"start": v(-16.9, -65.1) * mm, "end": v(-16.82, -64.97) * mm});
            skLineSegment(sketch, "E3468", {"start": v(-16.82, -64.97) * mm, "end": v(-16.73, -64.85) * mm});
            skLineSegment(sketch, "E3469", {"start": v(-16.73, -64.85) * mm, "end": v(-16.64, -64.74) * mm});
            skLineSegment(sketch, "E3470", {"start": v(-16.64, -64.74) * mm, "end": v(-16.56, -64.62) * mm});
            skLineSegment(sketch, "E3471", {"start": v(-16.56, -64.62) * mm, "end": v(-16.48, -64.51) * mm});
            skLineSegment(sketch, "E3472", {"start": v(-16.48, -64.51) * mm, "end": v(-16.4, -64.4) * mm});
            skLineSegment(sketch, "E3473", {"start": v(-16.4, -64.4) * mm, "end": v(-16.32, -64.29) * mm});
            skLineSegment(sketch, "E3474", {"start": v(-16.32, -64.29) * mm, "end": v(-16.25, -64.18) * mm});
            skLineSegment(sketch, "E3475", {"start": v(-16.25, -64.18) * mm, "end": v(-16.17, -64.07) * mm});
            skLineSegment(sketch, "E3476", {"start": v(-16.17, -64.07) * mm, "end": v(-16.1, -63.96) * mm});
            skLineSegment(sketch, "E3477", {"start": v(-16.1, -63.96) * mm, "end": v(-16.03, -63.85) * mm});
            skLineSegment(sketch, "E3478", {"start": v(-16.03, -63.85) * mm, "end": v(-15.96, -63.75) * mm});
            skLineSegment(sketch, "E3479", {"start": v(-15.96, -63.75) * mm, "end": v(-15.9, -63.64) * mm});
            skLineSegment(sketch, "E3480", {"start": v(-15.9, -63.64) * mm, "end": v(-15.83, -63.54) * mm});
            skLineSegment(sketch, "E3481", {"start": v(-15.83, -63.54) * mm, "end": v(-15.77, -63.44) * mm});
            skLineSegment(sketch, "E3482", {"start": v(-15.77, -63.44) * mm, "end": v(-15.7, -63.34) * mm});
            skLineSegment(sketch, "E3483", {"start": v(-15.7, -63.34) * mm, "end": v(-15.65, -63.25) * mm});
            skLineSegment(sketch, "E3484", {"start": v(-15.65, -63.25) * mm, "end": v(-15.59, -63.15) * mm});
            skLineSegment(sketch, "E3485", {"start": v(-15.59, -63.15) * mm, "end": v(-15.53, -63.05) * mm});
            skLineSegment(sketch, "E3486", {"start": v(-15.53, -63.05) * mm, "end": v(-15.48, -62.96) * mm});
            skLineSegment(sketch, "E3487", {"start": v(-15.48, -62.96) * mm, "end": v(-15.42, -62.87) * mm});
            skLineSegment(sketch, "E3488", {"start": v(-15.42, -62.87) * mm, "end": v(-15.37, -62.78) * mm});
            skLineSegment(sketch, "E3489", {"start": v(-15.37, -62.78) * mm, "end": v(-15.32, -62.69) * mm});
            skLineSegment(sketch, "E3490", {"start": v(-15.32, -62.69) * mm, "end": v(-15.27, -62.6) * mm});
            skLineSegment(sketch, "E3491", {"start": v(-15.27, -62.6) * mm, "end": v(-15.22, -62.52) * mm});
            skLineSegment(sketch, "E3492", {"start": v(-15.22, -62.52) * mm, "end": v(-15.18, -62.43) * mm});
            skLineSegment(sketch, "E3493", {"start": v(-15.18, -62.43) * mm, "end": v(-15.13, -62.35) * mm});
            skLineSegment(sketch, "E3494", {"start": v(-15.13, -62.35) * mm, "end": v(-15.1, -62.27) * mm});
            skLineSegment(sketch, "E3495", {"start": v(-15.1, -62.27) * mm, "end": v(-15.05, -62.19) * mm});
            skLineSegment(sketch, "E3496", {"start": v(-15.05, -62.19) * mm, "end": v(-15.01, -62.11) * mm});
            skLineSegment(sketch, "E3497", {"start": v(-15.01, -62.11) * mm, "end": v(-14.97, -62.04) * mm});
            skLineSegment(sketch, "E3498", {"start": v(-14.97, -62.04) * mm, "end": v(-14.94, -61.96) * mm});
            skLineSegment(sketch, "E3499", {"start": v(-14.94, -61.96) * mm, "end": v(-14.67, -61.9) * mm});
            skLineSegment(sketch, "E3500", {"start": v(-14.67, -61.9) * mm, "end": v(-13.22, -62.22) * mm});
            skLineSegment(sketch, "E3501", {"start": v(-13.22, -62.22) * mm, "end": v(-13.02, -62.4) * mm});
            skLineSegment(sketch, "E3502", {"start": v(-13.02, -62.4) * mm, "end": v(-13.01, -62.48) * mm});
            skLineSegment(sketch, "E3503", {"start": v(-13.01, -62.48) * mm, "end": v(-13.01, -62.56) * mm});
            skLineSegment(sketch, "E3504", {"start": v(-13.01, -62.56) * mm, "end": v(-13, -62.65) * mm});
            skLineSegment(sketch, "E3505", {"start": v(-13, -62.65) * mm, "end": v(-13, -62.74) * mm});
            skLineSegment(sketch, "E3506", {"start": v(-13, -62.74) * mm, "end": v(-13, -62.92) * mm});
            skLineSegment(sketch, "E3507", {"start": v(-13, -62.92) * mm, "end": v(-13, -63.02) * mm});
            skLineSegment(sketch, "E3508", {"start": v(-13, -63.02) * mm, "end": v(-12.99, -63.12) * mm});
            skLineSegment(sketch, "E3509", {"start": v(-12.99, -63.12) * mm, "end": v(-12.98, -63.22) * mm});
            skLineSegment(sketch, "E3510", {"start": v(-12.98, -63.22) * mm, "end": v(-12.97, -63.32) * mm});
            skLineSegment(sketch, "E3511", {"start": v(-12.97, -63.32) * mm, "end": v(-12.96, -63.42) * mm});
            skLineSegment(sketch, "E3512", {"start": v(-12.96, -63.42) * mm, "end": v(-12.96, -63.53) * mm});
            skLineSegment(sketch, "E3513", {"start": v(-12.96, -63.53) * mm, "end": v(-12.95, -63.64) * mm});
            skLineSegment(sketch, "E3514", {"start": v(-12.95, -63.64) * mm, "end": v(-12.93, -63.75) * mm});
            skLineSegment(sketch, "E3515", {"start": v(-12.93, -63.75) * mm, "end": v(-12.92, -63.86) * mm});
            skLineSegment(sketch, "E3516", {"start": v(-12.92, -63.86) * mm, "end": v(-12.91, -63.97) * mm});
            skLineSegment(sketch, "E3517", {"start": v(-12.91, -63.97) * mm, "end": v(-12.9, -64.09) * mm});
            skLineSegment(sketch, "E3518", {"start": v(-12.9, -64.09) * mm, "end": v(-12.88, -64.2) * mm});
            skLineSegment(sketch, "E3519", {"start": v(-12.88, -64.2) * mm, "end": v(-12.87, -64.33) * mm});
            skLineSegment(sketch, "E3520", {"start": v(-12.87, -64.33) * mm, "end": v(-12.85, -64.45) * mm});
            skLineSegment(sketch, "E3521", {"start": v(-12.85, -64.45) * mm, "end": v(-12.84, -64.57) * mm});
            skLineSegment(sketch, "E3522", {"start": v(-12.84, -64.57) * mm, "end": v(-12.82, -64.7) * mm});
            skLineSegment(sketch, "E3523", {"start": v(-12.82, -64.7) * mm, "end": v(-12.8, -64.83) * mm});
            skLineSegment(sketch, "E3524", {"start": v(-12.8, -64.83) * mm, "end": v(-12.78, -64.96) * mm});
            skLineSegment(sketch, "E3525", {"start": v(-12.78, -64.96) * mm, "end": v(-12.76, -65.09) * mm});
            skLineSegment(sketch, "E3526", {"start": v(-12.76, -65.09) * mm, "end": v(-12.73, -65.22) * mm});
            skLineSegment(sketch, "E3527", {"start": v(-12.73, -65.22) * mm, "end": v(-12.71, -65.36) * mm});
            skLineSegment(sketch, "E3528", {"start": v(-12.71, -65.36) * mm, "end": v(-12.69, -65.5) * mm});
            skLineSegment(sketch, "E3529", {"start": v(-12.69, -65.5) * mm, "end": v(-12.66, -65.63) * mm});
            skLineSegment(sketch, "E3530", {"start": v(-12.66, -65.63) * mm, "end": v(-12.63, -65.78) * mm});
            skLineSegment(sketch, "E3531", {"start": v(-12.63, -65.78) * mm, "end": v(-12.6, -65.92) * mm});
            skLineSegment(sketch, "E3532", {"start": v(-12.6, -65.92) * mm, "end": v(-12.57, -66.06) * mm});
            skLineSegment(sketch, "E3533", {"start": v(-12.57, -66.06) * mm, "end": v(-12.54, -66.21) * mm});
            skLineSegment(sketch, "E3534", {"start": v(-12.54, -66.21) * mm, "end": v(-12.51, -66.36) * mm});
            skLineSegment(sketch, "E3535", {"start": v(-12.51, -66.36) * mm, "end": v(-12.44, -66.66) * mm});
            skLineSegment(sketch, "E3536", {"start": v(-12.44, -66.66) * mm, "end": v(-12.4, -66.82) * mm});
            skLineSegment(sketch, "E3537", {"start": v(-12.4, -66.82) * mm, "end": v(-12.37, -66.98) * mm});
            skLineSegment(sketch, "E3538", {"start": v(-12.37, -66.98) * mm, "end": v(-12.33, -67.13) * mm});
            skLineSegment(sketch, "E3539", {"start": v(-12.33, -67.13) * mm, "end": v(-12.28, -67.24) * mm});
            skLineSegment(sketch, "E3540", {"start": v(-12.28, -67.24) * mm, "end": v(-10.68, -67.51) * mm});
            skLineSegment(sketch, "E3541", {"start": v(-10.68, -67.51) * mm, "end": v(-10.6, -67.43) * mm});
            skLineSegment(sketch, "E3542", {"start": v(-10.6, -67.43) * mm, "end": v(-10.5, -67.3) * mm});
            skLineSegment(sketch, "E3543", {"start": v(-10.5, -67.3) * mm, "end": v(-10.42, -67.16) * mm});
            skLineSegment(sketch, "E3544", {"start": v(-10.42, -67.16) * mm, "end": v(-10.33, -67.03) * mm});
            skLineSegment(sketch, "E3545", {"start": v(-10.33, -67.03) * mm, "end": v(-10.25, -66.9) * mm});
            skLineSegment(sketch, "E3546", {"start": v(-10.25, -66.9) * mm, "end": v(-10.17, -66.76) * mm});
            skLineSegment(sketch, "E3547", {"start": v(-10.17, -66.76) * mm, "end": v(-10.09, -66.63) * mm});
            skLineSegment(sketch, "E3548", {"start": v(-10.09, -66.63) * mm, "end": v(-10, -66.5) * mm});
            skLineSegment(sketch, "E3549", {"start": v(-10, -66.5) * mm, "end": v(-9.93, -66.37) * mm});
            skLineSegment(sketch, "E3550", {"start": v(-9.93, -66.37) * mm, "end": v(-9.86, -66.25) * mm});
            skLineSegment(sketch, "E3551", {"start": v(-9.86, -66.25) * mm, "end": v(-9.79, -66.12) * mm});
            skLineSegment(sketch, "E3552", {"start": v(-9.79, -66.12) * mm, "end": v(-9.72, -66) * mm});
            skLineSegment(sketch, "E3553", {"start": v(-9.72, -66) * mm, "end": v(-9.65, -65.88) * mm});
            skLineSegment(sketch, "E3554", {"start": v(-9.65, -65.88) * mm, "end": v(-9.58, -65.76) * mm});
            skLineSegment(sketch, "E3555", {"start": v(-9.58, -65.76) * mm, "end": v(-9.45, -65.52) * mm});
            skLineSegment(sketch, "E3556", {"start": v(-9.45, -65.52) * mm, "end": v(-9.39, -65.4) * mm});
            skLineSegment(sketch, "E3557", {"start": v(-9.39, -65.4) * mm, "end": v(-9.33, -65.3) * mm});
            skLineSegment(sketch, "E3558", {"start": v(-9.33, -65.3) * mm, "end": v(-9.27, -65.18) * mm});
            skLineSegment(sketch, "E3559", {"start": v(-9.27, -65.18) * mm, "end": v(-9.21, -65.07) * mm});
            skLineSegment(sketch, "E3560", {"start": v(-9.21, -65.07) * mm, "end": v(-9.16, -64.96) * mm});
            skLineSegment(sketch, "E3561", {"start": v(-9.16, -64.96) * mm, "end": v(-9.1, -64.85) * mm});
            skLineSegment(sketch, "E3562", {"start": v(-9.1, -64.85) * mm, "end": v(-9.05, -64.74) * mm});
            skLineSegment(sketch, "E3563", {"start": v(-9.05, -64.74) * mm, "end": v(-9, -64.64) * mm});
            skLineSegment(sketch, "E3564", {"start": v(-9, -64.64) * mm, "end": v(-8.95, -64.53) * mm});
            skLineSegment(sketch, "E3565", {"start": v(-8.95, -64.53) * mm, "end": v(-8.9, -64.43) * mm});
            skLineSegment(sketch, "E3566", {"start": v(-8.9, -64.43) * mm, "end": v(-8.86, -64.33) * mm});
            skLineSegment(sketch, "E3567", {"start": v(-8.86, -64.33) * mm, "end": v(-8.8, -64.23) * mm});
            skLineSegment(sketch, "E3568", {"start": v(-8.8, -64.23) * mm, "end": v(-8.77, -64.14) * mm});
            skLineSegment(sketch, "E3569", {"start": v(-8.77, -64.14) * mm, "end": v(-8.72, -64.04) * mm});
            skLineSegment(sketch, "E3570", {"start": v(-8.72, -64.04) * mm, "end": v(-8.68, -63.95) * mm});
            skLineSegment(sketch, "E3571", {"start": v(-8.68, -63.95) * mm, "end": v(-8.64, -63.86) * mm});
            skLineSegment(sketch, "E3572", {"start": v(-8.64, -63.86) * mm, "end": v(-8.6, -63.77) * mm});
            skLineSegment(sketch, "E3573", {"start": v(-8.6, -63.77) * mm, "end": v(-8.57, -63.68) * mm});
            skLineSegment(sketch, "E3574", {"start": v(-8.57, -63.68) * mm, "end": v(-8.53, -63.6) * mm});
            skLineSegment(sketch, "E3575", {"start": v(-8.53, -63.6) * mm, "end": v(-8.5, -63.5) * mm});
            skLineSegment(sketch, "E3576", {"start": v(-8.5, -63.5) * mm, "end": v(-8.47, -63.42) * mm});
            skLineSegment(sketch, "E3577", {"start": v(-8.47, -63.42) * mm, "end": v(-8.44, -63.34) * mm});
            skLineSegment(sketch, "E3578", {"start": v(-8.44, -63.34) * mm, "end": v(-8.4, -63.26) * mm});
            skLineSegment(sketch, "E3579", {"start": v(-8.4, -63.26) * mm, "end": v(-8.38, -63.18) * mm});
            skLineSegment(sketch, "E3580", {"start": v(-8.38, -63.18) * mm, "end": v(-8.12, -63.09) * mm});
            skLineSegment(sketch, "E3581", {"start": v(-8.12, -63.09) * mm, "end": v(-6.65, -63.26) * mm});
            skLineSegment(sketch, "E3582", {"start": v(-6.65, -63.26) * mm, "end": v(-6.42, -63.41) * mm});
            skLineSegment(sketch, "E3583", {"start": v(-6.42, -63.41) * mm, "end": v(-6.41, -63.5) * mm});
            skLineSegment(sketch, "E3584", {"start": v(-6.41, -63.5) * mm, "end": v(-6.4, -63.58) * mm});
            skLineSegment(sketch, "E3585", {"start": v(-6.4, -63.58) * mm, "end": v(-6.39, -63.67) * mm});
            skLineSegment(sketch, "E3586", {"start": v(-6.39, -63.67) * mm, "end": v(-6.38, -63.75) * mm});
            skLineSegment(sketch, "E3587", {"start": v(-6.38, -63.75) * mm, "end": v(-6.36, -63.84) * mm});
            skLineSegment(sketch, "E3588", {"start": v(-6.36, -63.84) * mm, "end": v(-6.35, -63.94) * mm});
            skLineSegment(sketch, "E3589", {"start": v(-6.35, -63.94) * mm, "end": v(-6.33, -64.03) * mm});
            skLineSegment(sketch, "E3590", {"start": v(-6.33, -64.03) * mm, "end": v(-6.32, -64.13) * mm});
            skLineSegment(sketch, "E3591", {"start": v(-6.32, -64.13) * mm, "end": v(-6.3, -64.23) * mm});
            skLineSegment(sketch, "E3592", {"start": v(-6.3, -64.23) * mm, "end": v(-6.28, -64.33) * mm});
            skLineSegment(sketch, "E3593", {"start": v(-6.28, -64.33) * mm, "end": v(-6.26, -64.43) * mm});
            skLineSegment(sketch, "E3594", {"start": v(-6.26, -64.43) * mm, "end": v(-6.24, -64.53) * mm});
            skLineSegment(sketch, "E3595", {"start": v(-6.24, -64.53) * mm, "end": v(-6.22, -64.64) * mm});
            skLineSegment(sketch, "E3596", {"start": v(-6.22, -64.64) * mm, "end": v(-6.2, -64.75) * mm});
            skLineSegment(sketch, "E3597", {"start": v(-6.2, -64.75) * mm, "end": v(-6.18, -64.86) * mm});
            skLineSegment(sketch, "E3598", {"start": v(-6.18, -64.86) * mm, "end": v(-6.15, -64.97) * mm});
            skLineSegment(sketch, "E3599", {"start": v(-6.15, -64.97) * mm, "end": v(-6.13, -65.08) * mm});
            skLineSegment(sketch, "E3600", {"start": v(-6.13, -65.08) * mm, "end": v(-6.1, -65.2) * mm});
            skLineSegment(sketch, "E3601", {"start": v(-6.1, -65.2) * mm, "end": v(-6.07, -65.32) * mm});
            skLineSegment(sketch, "E3602", {"start": v(-6.07, -65.32) * mm, "end": v(-6.05, -65.44) * mm});
            skLineSegment(sketch, "E3603", {"start": v(-6.05, -65.44) * mm, "end": v(-6.02, -65.56) * mm});
            skLineSegment(sketch, "E3604", {"start": v(-6.02, -65.56) * mm, "end": v(-5.98, -65.68) * mm});
            skLineSegment(sketch, "E3605", {"start": v(-5.98, -65.68) * mm, "end": v(-5.95, -65.8) * mm});
            skLineSegment(sketch, "E3606", {"start": v(-5.95, -65.8) * mm, "end": v(-5.92, -65.93) * mm});
            skLineSegment(sketch, "E3607", {"start": v(-5.92, -65.93) * mm, "end": v(-5.88, -66.06) * mm});
            skLineSegment(sketch, "E3608", {"start": v(-5.88, -66.06) * mm, "end": v(-5.85, -66.2) * mm});
            skLineSegment(sketch, "E3609", {"start": v(-5.85, -66.2) * mm, "end": v(-5.8, -66.33) * mm});
            skLineSegment(sketch, "E3610", {"start": v(-5.8, -66.33) * mm, "end": v(-5.77, -66.46) * mm});
            skLineSegment(sketch, "E3611", {"start": v(-5.77, -66.46) * mm, "end": v(-5.73, -66.6) * mm});
            skLineSegment(sketch, "E3612", {"start": v(-5.73, -66.6) * mm, "end": v(-5.69, -66.74) * mm});
            skLineSegment(sketch, "E3613", {"start": v(-5.69, -66.74) * mm, "end": v(-5.6, -67.02) * mm});
            skLineSegment(sketch, "E3614", {"start": v(-5.6, -67.02) * mm, "end": v(-5.55, -67.16) * mm});
            skLineSegment(sketch, "E3615", {"start": v(-5.55, -67.16) * mm, "end": v(-5.5, -67.3) * mm});
            skLineSegment(sketch, "E3616", {"start": v(-5.5, -67.3) * mm, "end": v(-5.46, -67.45) * mm});
            skLineSegment(sketch, "E3617", {"start": v(-5.46, -67.45) * mm, "end": v(-5.4, -67.6) * mm});
            skLineSegment(sketch, "E3618", {"start": v(-5.4, -67.6) * mm, "end": v(-5.36, -67.75) * mm});
            skLineSegment(sketch, "E3619", {"start": v(-5.36, -67.75) * mm, "end": v(-5.3, -67.9) * mm});
            skLineSegment(sketch, "E3620", {"start": v(-5.3, -67.9) * mm, "end": v(-5.25, -68.06) * mm});
            skLineSegment(sketch, "E3621", {"start": v(-5.25, -68.06) * mm, "end": v(-5.18, -68.15) * mm});
            skLineSegment(sketch, "E3622", {"start": v(-5.18, -68.15) * mm, "end": v(-3.56, -68.26) * mm});
            skLineSegment(sketch, "E3623", {"start": v(-3.56, -68.26) * mm, "end": v(-3.49, -68.17) * mm});
            skLineSegment(sketch, "E3624", {"start": v(-3.49, -68.17) * mm, "end": v(-3.41, -68.02) * mm});
            skLineSegment(sketch, "E3625", {"start": v(-3.41, -68.02) * mm, "end": v(-3.34, -67.88) * mm});
            skLineSegment(sketch, "E3626", {"start": v(-3.34, -67.88) * mm, "end": v(-3.27, -67.74) * mm});
            skLineSegment(sketch, "E3627", {"start": v(-3.27, -67.74) * mm, "end": v(-3.2, -67.6) * mm});
            skLineSegment(sketch, "E3628", {"start": v(-3.2, -67.6) * mm, "end": v(-3.13, -67.46) * mm});
            skLineSegment(sketch, "E3629", {"start": v(-3.13, -67.46) * mm, "end": v(-3.07, -67.32) * mm});
            skLineSegment(sketch, "E3630", {"start": v(-3.07, -67.32) * mm, "end": v(-3, -67.18) * mm});
            skLineSegment(sketch, "E3631", {"start": v(-3, -67.18) * mm, "end": v(-2.94, -67.05) * mm});
            skLineSegment(sketch, "E3632", {"start": v(-2.94, -67.05) * mm, "end": v(-2.88, -66.92) * mm});
            skLineSegment(sketch, "E3633", {"start": v(-2.88, -66.92) * mm, "end": v(-2.82, -66.78) * mm});
            skLineSegment(sketch, "E3634", {"start": v(-2.82, -66.78) * mm, "end": v(-2.76, -66.65) * mm});
            skLineSegment(sketch, "E3635", {"start": v(-2.76, -66.65) * mm, "end": v(-2.7, -66.53) * mm});
            skLineSegment(sketch, "E3636", {"start": v(-2.7, -66.53) * mm, "end": v(-2.65, -66.4) * mm});
            skLineSegment(sketch, "E3637", {"start": v(-2.65, -66.4) * mm, "end": v(-2.6, -66.27) * mm});
            skLineSegment(sketch, "E3638", {"start": v(-2.6, -66.27) * mm, "end": v(-2.55, -66.15) * mm});
            skLineSegment(sketch, "E3639", {"start": v(-2.55, -66.15) * mm, "end": v(-2.5, -66.03) * mm});
            skLineSegment(sketch, "E3640", {"start": v(-2.5, -66.03) * mm, "end": v(-2.45, -65.9) * mm});
            skLineSegment(sketch, "E3641", {"start": v(-2.45, -65.9) * mm, "end": v(-2.4, -65.8) * mm});
            skLineSegment(sketch, "E3642", {"start": v(-2.4, -65.8) * mm, "end": v(-2.36, -65.67) * mm});
            skLineSegment(sketch, "E3643", {"start": v(-2.36, -65.67) * mm, "end": v(-2.31, -65.56) * mm});
            skLineSegment(sketch, "E3644", {"start": v(-2.31, -65.56) * mm, "end": v(-2.27, -65.45) * mm});
            skLineSegment(sketch, "E3645", {"start": v(-2.27, -65.45) * mm, "end": v(-2.23, -65.33) * mm});
            skLineSegment(sketch, "E3646", {"start": v(-2.23, -65.33) * mm, "end": v(-2.2, -65.22) * mm});
            skLineSegment(sketch, "E3647", {"start": v(-2.2, -65.22) * mm, "end": v(-2.15, -65.12) * mm});
            skLineSegment(sketch, "E3648", {"start": v(-2.15, -65.12) * mm, "end": v(-2.12, -65.01) * mm});
            skLineSegment(sketch, "E3649", {"start": v(-2.12, -65.01) * mm, "end": v(-2.08, -64.9) * mm});
            skLineSegment(sketch, "E3650", {"start": v(-2.08, -64.9) * mm, "end": v(-2.05, -64.8) * mm});
            skLineSegment(sketch, "E3651", {"start": v(-2.05, -64.8) * mm, "end": v(-2.01, -64.7) * mm});
            skLineSegment(sketch, "E3652", {"start": v(-2.01, -64.7) * mm, "end": v(-1.98, -64.6) * mm});
            skLineSegment(sketch, "E3653", {"start": v(-1.98, -64.6) * mm, "end": v(-1.95, -64.5) * mm});
            skLineSegment(sketch, "E3654", {"start": v(-1.95, -64.5) * mm, "end": v(-1.92, -64.4) * mm});
            skLineSegment(sketch, "E3655", {"start": v(-1.92, -64.4) * mm, "end": v(-1.9, -64.32) * mm});
            skLineSegment(sketch, "E3656", {"start": v(-1.9, -64.32) * mm, "end": v(-1.84, -64.13) * mm});
            skLineSegment(sketch, "E3657", {"start": v(-1.84, -64.13) * mm, "end": v(-1.8, -63.96) * mm});
            skLineSegment(sketch, "E3658", {"start": v(-1.8, -63.96) * mm, "end": v(-1.77, -63.88) * mm});
            skLineSegment(sketch, "E3659", {"start": v(-1.77, -63.88) * mm, "end": v(-1.75, -63.8) * mm});
            skLineSegment(sketch, "E3660", {"start": v(-1.75, -63.8) * mm, "end": v(-1.73, -63.71) * mm});
            skLineSegment(sketch, "E3661", {"start": v(-1.73, -63.71) * mm, "end": v(-1.48, -63.6) * mm});
            skLineSegment(sketch, "E3662", {"start": v(-1.48, -63.6) * mm, "end": v(0, -63.61) * mm});
            skLineSegment(sketch, "E3663", {"start": v(0, -63.61) * mm, "end": v(0.24, -63.74) * mm});
            skLineSegment(sketch, "E3664", {"start": v(0.24, -63.74) * mm, "end": v(0.26, -63.82) * mm});
            skLineSegment(sketch, "E3665", {"start": v(0.26, -63.82) * mm, "end": v(0.28, -63.9) * mm});
            skLineSegment(sketch, "E3666", {"start": v(0.28, -63.9) * mm, "end": v(0.3, -63.99) * mm});
            skLineSegment(sketch, "E3667", {"start": v(0.3, -63.99) * mm, "end": v(0.32, -64.07) * mm});
            skLineSegment(sketch, "E3668", {"start": v(0.32, -64.07) * mm, "end": v(0.35, -64.16) * mm});
            skLineSegment(sketch, "E3669", {"start": v(0.35, -64.16) * mm, "end": v(0.37, -64.25) * mm});
            skLineSegment(sketch, "E3670", {"start": v(0.37, -64.25) * mm, "end": v(0.4, -64.34) * mm});
            skLineSegment(sketch, "E3671", {"start": v(0.4, -64.34) * mm, "end": v(0.42, -64.44) * mm});
            skLineSegment(sketch, "E3672", {"start": v(0.42, -64.44) * mm, "end": v(0.45, -64.53) * mm});
            skLineSegment(sketch, "E3673", {"start": v(0.45, -64.53) * mm, "end": v(0.48, -64.63) * mm});
            skLineSegment(sketch, "E3674", {"start": v(0.48, -64.63) * mm, "end": v(0.5, -64.73) * mm});
            skLineSegment(sketch, "E3675", {"start": v(0.5, -64.73) * mm, "end": v(0.54, -64.83) * mm});
            skLineSegment(sketch, "E3676", {"start": v(0.54, -64.83) * mm, "end": v(0.57, -64.94) * mm});
            skLineSegment(sketch, "E3677", {"start": v(0.57, -64.94) * mm, "end": v(0.64, -65.15) * mm});
            skLineSegment(sketch, "E3678", {"start": v(0.64, -65.15) * mm, "end": v(0.7, -65.37) * mm});
            skLineSegment(sketch, "E3679", {"start": v(0.7, -65.37) * mm, "end": v(0.75, -65.48) * mm});
            skLineSegment(sketch, "E3680", {"start": v(0.75, -65.48) * mm, "end": v(0.79, -65.6) * mm});
            skLineSegment(sketch, "E3681", {"start": v(0.79, -65.6) * mm, "end": v(0.83, -65.71) * mm});
            skLineSegment(sketch, "E3682", {"start": v(0.83, -65.71) * mm, "end": v(0.87, -65.83) * mm});
            skLineSegment(sketch, "E3683", {"start": v(0.87, -65.83) * mm, "end": v(0.91, -65.95) * mm});
            skLineSegment(sketch, "E3684", {"start": v(0.91, -65.95) * mm, "end": v(0.96, -66.07) * mm});
            skLineSegment(sketch, "E3685", {"start": v(0.96, -66.07) * mm, "end": v(1, -66.2) * mm});
            skLineSegment(sketch, "E3686", {"start": v(1, -66.2) * mm, "end": v(1.05, -66.32) * mm});
            skLineSegment(sketch, "E3687", {"start": v(1.05, -66.32) * mm, "end": v(1.1, -66.44) * mm});
            skLineSegment(sketch, "E3688", {"start": v(1.1, -66.44) * mm, "end": v(1.16, -66.57) * mm});
            skLineSegment(sketch, "E3689", {"start": v(1.16, -66.57) * mm, "end": v(1.2, -66.7) * mm});
            skLineSegment(sketch, "E3690", {"start": v(1.2, -66.7) * mm, "end": v(1.26, -66.83) * mm});
            skLineSegment(sketch, "E3691", {"start": v(1.26, -66.83) * mm, "end": v(1.32, -66.96) * mm});
            skLineSegment(sketch, "E3692", {"start": v(1.32, -66.96) * mm, "end": v(1.38, -67.1) * mm});
            skLineSegment(sketch, "E3693", {"start": v(1.38, -67.1) * mm, "end": v(1.44, -67.24) * mm});
            skLineSegment(sketch, "E3694", {"start": v(1.44, -67.24) * mm, "end": v(1.5, -67.37) * mm});
            skLineSegment(sketch, "E3695", {"start": v(1.5, -67.37) * mm, "end": v(1.56, -67.51) * mm});
            skLineSegment(sketch, "E3696", {"start": v(1.56, -67.51) * mm, "end": v(1.69, -67.8) * mm});
            skLineSegment(sketch, "E3697", {"start": v(1.69, -67.8) * mm, "end": v(1.76, -67.94) * mm});
            skLineSegment(sketch, "E3698", {"start": v(1.76, -67.94) * mm, "end": v(1.83, -68.08) * mm});
            skLineSegment(sketch, "E3699", {"start": v(1.83, -68.08) * mm, "end": v(1.9, -68.23) * mm});
            skLineSegment(sketch, "E3700", {"start": v(1.9, -68.23) * mm, "end": v(1.97, -68.32) * mm});
            skLineSegment(sketch, "E3701", {"start": v(1.97, -68.32) * mm, "end": v(3.6, -68.26) * mm});
            skLineSegment(sketch, "E3702", {"start": v(3.6, -68.26) * mm, "end": v(3.66, -68.16) * mm});
            skLineSegment(sketch, "E3703", {"start": v(3.66, -68.16) * mm, "end": v(3.77, -67.86) * mm});
            skLineSegment(sketch, "E3704", {"start": v(3.77, -67.86) * mm, "end": v(3.83, -67.7) * mm});
            skLineSegment(sketch, "E3705", {"start": v(3.83, -67.7) * mm, "end": v(3.88, -67.56) * mm});
            skLineSegment(sketch, "E3706", {"start": v(3.88, -67.56) * mm, "end": v(3.94, -67.42) * mm});
            skLineSegment(sketch, "E3707", {"start": v(3.94, -67.42) * mm, "end": v(3.99, -67.27) * mm});
            skLineSegment(sketch, "E3708", {"start": v(3.99, -67.27) * mm, "end": v(4.04, -67.13) * mm});
            skLineSegment(sketch, "E3709", {"start": v(4.04, -67.13) * mm, "end": v(4.08, -66.99) * mm});
            skLineSegment(sketch, "E3710", {"start": v(4.08, -66.99) * mm, "end": v(4.13, -66.85) * mm});
            skLineSegment(sketch, "E3711", {"start": v(4.13, -66.85) * mm, "end": v(4.18, -66.71) * mm});
            skLineSegment(sketch, "E3712", {"start": v(4.18, -66.71) * mm, "end": v(4.22, -66.58) * mm});
            skLineSegment(sketch, "E3713", {"start": v(4.22, -66.58) * mm, "end": v(4.26, -66.44) * mm});
            skLineSegment(sketch, "E3714", {"start": v(4.26, -66.44) * mm, "end": v(4.3, -66.31) * mm});
            skLineSegment(sketch, "E3715", {"start": v(4.3, -66.31) * mm, "end": v(4.34, -66.18) * mm});
            skLineSegment(sketch, "E3716", {"start": v(4.34, -66.18) * mm, "end": v(4.38, -66.05) * mm});
            skLineSegment(sketch, "E3717", {"start": v(4.38, -66.05) * mm, "end": v(4.42, -65.93) * mm});
            skLineSegment(sketch, "E3718", {"start": v(4.42, -65.93) * mm, "end": v(4.45, -65.8) * mm});
            skLineSegment(sketch, "E3719", {"start": v(4.45, -65.8) * mm, "end": v(4.49, -65.68) * mm});
            skLineSegment(sketch, "E3720", {"start": v(4.49, -65.68) * mm, "end": v(4.52, -65.56) * mm});
            skLineSegment(sketch, "E3721", {"start": v(4.52, -65.56) * mm, "end": v(4.55, -65.44) * mm});
            skLineSegment(sketch, "E3722", {"start": v(4.55, -65.44) * mm, "end": v(4.58, -65.32) * mm});
            skLineSegment(sketch, "E3723", {"start": v(4.58, -65.32) * mm, "end": v(4.6, -65.21) * mm});
            skLineSegment(sketch, "E3724", {"start": v(4.6, -65.21) * mm, "end": v(4.64, -65.1) * mm});
            skLineSegment(sketch, "E3725", {"start": v(4.64, -65.1) * mm, "end": v(4.66, -64.98) * mm});
            skLineSegment(sketch, "E3726", {"start": v(4.66, -64.98) * mm, "end": v(4.69, -64.88) * mm});
            skLineSegment(sketch, "E3727", {"start": v(4.69, -64.88) * mm, "end": v(4.71, -64.77) * mm});
            skLineSegment(sketch, "E3728", {"start": v(4.71, -64.77) * mm, "end": v(4.74, -64.66) * mm});
            skLineSegment(sketch, "E3729", {"start": v(4.74, -64.66) * mm, "end": v(4.76, -64.56) * mm});
            skLineSegment(sketch, "E3730", {"start": v(4.76, -64.56) * mm, "end": v(4.78, -64.46) * mm});
            skLineSegment(sketch, "E3731", {"start": v(4.78, -64.46) * mm, "end": v(4.8, -64.36) * mm});
            skLineSegment(sketch, "E3732", {"start": v(4.8, -64.36) * mm, "end": v(4.82, -64.26) * mm});
            skLineSegment(sketch, "E3733", {"start": v(4.82, -64.26) * mm, "end": v(4.84, -64.16) * mm});
            skLineSegment(sketch, "E3734", {"start": v(4.84, -64.16) * mm, "end": v(4.86, -64.07) * mm});
            skLineSegment(sketch, "E3735", {"start": v(4.86, -64.07) * mm, "end": v(4.87, -63.98) * mm});
            skLineSegment(sketch, "E3736", {"start": v(4.87, -63.98) * mm, "end": v(4.89, -63.89) * mm});
            skLineSegment(sketch, "E3737", {"start": v(4.89, -63.89) * mm, "end": v(4.9, -63.8) * mm});
            skLineSegment(sketch, "E3738", {"start": v(4.9, -63.8) * mm, "end": v(4.92, -63.71) * mm});
            skLineSegment(sketch, "E3739", {"start": v(4.92, -63.71) * mm, "end": v(4.93, -63.63) * mm});
            skLineSegment(sketch, "E3740", {"start": v(4.93, -63.63) * mm, "end": v(4.94, -63.54) * mm});
            skLineSegment(sketch, "E3741", {"start": v(4.94, -63.54) * mm, "end": v(5.17, -63.4) * mm});
            skLineSegment(sketch, "E3742", {"start": v(5.17, -63.4) * mm, "end": v(6.65, -63.26) * mm});
            skLineSegment(sketch, "E3743", {"start": v(6.65, -63.26) * mm, "end": v(6.9, -63.36) * mm});
            skLineSegment(sketch, "E3744", {"start": v(6.9, -63.36) * mm, "end": v(6.93, -63.44) * mm});
            skLineSegment(sketch, "E3745", {"start": v(6.93, -63.44) * mm, "end": v(6.96, -63.52) * mm});
            skLineSegment(sketch, "E3746", {"start": v(6.96, -63.52) * mm, "end": v(6.99, -63.6) * mm});
            skLineSegment(sketch, "E3747", {"start": v(6.99, -63.6) * mm, "end": v(7.02, -63.69) * mm});
            skLineSegment(sketch, "E3748", {"start": v(7.02, -63.69) * mm, "end": v(7.05, -63.77) * mm});
            skLineSegment(sketch, "E3749", {"start": v(7.05, -63.77) * mm, "end": v(7.08, -63.86) * mm});
            skLineSegment(sketch, "E3750", {"start": v(7.08, -63.86) * mm, "end": v(7.12, -63.95) * mm});
            skLineSegment(sketch, "E3751", {"start": v(7.12, -63.95) * mm, "end": v(7.15, -64.04) * mm});
            skLineSegment(sketch, "E3752", {"start": v(7.15, -64.04) * mm, "end": v(7.2, -64.13) * mm});
            skLineSegment(sketch, "E3753", {"start": v(7.2, -64.13) * mm, "end": v(7.23, -64.23) * mm});
            skLineSegment(sketch, "E3754", {"start": v(7.23, -64.23) * mm, "end": v(7.27, -64.32) * mm});
            skLineSegment(sketch, "E3755", {"start": v(7.27, -64.32) * mm, "end": v(7.31, -64.42) * mm});
            skLineSegment(sketch, "E3756", {"start": v(7.31, -64.42) * mm, "end": v(7.35, -64.52) * mm});
            skLineSegment(sketch, "E3757", {"start": v(7.35, -64.52) * mm, "end": v(7.4, -64.62) * mm});
            skLineSegment(sketch, "E3758", {"start": v(7.4, -64.62) * mm, "end": v(7.44, -64.73) * mm});
            skLineSegment(sketch, "E3759", {"start": v(7.44, -64.73) * mm, "end": v(7.49, -64.83) * mm});
            skLineSegment(sketch, "E3760", {"start": v(7.49, -64.83) * mm, "end": v(7.54, -64.94) * mm});
            skLineSegment(sketch, "E3761", {"start": v(7.54, -64.94) * mm, "end": v(7.59, -65.04) * mm});
            skLineSegment(sketch, "E3762", {"start": v(7.59, -65.04) * mm, "end": v(7.64, -65.15) * mm});
            skLineSegment(sketch, "E3763", {"start": v(7.64, -65.15) * mm, "end": v(7.7, -65.27) * mm});
            skLineSegment(sketch, "E3764", {"start": v(7.7, -65.27) * mm, "end": v(7.75, -65.38) * mm});
            skLineSegment(sketch, "E3765", {"start": v(7.75, -65.38) * mm, "end": v(7.8, -65.5) * mm});
            skLineSegment(sketch, "E3766", {"start": v(7.8, -65.5) * mm, "end": v(7.86, -65.6) * mm});
            skLineSegment(sketch, "E3767", {"start": v(7.86, -65.6) * mm, "end": v(7.92, -65.72) * mm});
            skLineSegment(sketch, "E3768", {"start": v(7.92, -65.72) * mm, "end": v(8.04, -65.96) * mm});
            skLineSegment(sketch, "E3769", {"start": v(8.04, -65.96) * mm, "end": v(8.1, -66.09) * mm});
            skLineSegment(sketch, "E3770", {"start": v(8.1, -66.09) * mm, "end": v(8.17, -66.2) * mm});
            skLineSegment(sketch, "E3771", {"start": v(8.17, -66.2) * mm, "end": v(8.24, -66.33) * mm});
            skLineSegment(sketch, "E3772", {"start": v(8.24, -66.33) * mm, "end": v(8.31, -66.46) * mm});
            skLineSegment(sketch, "E3773", {"start": v(8.31, -66.46) * mm, "end": v(8.38, -66.59) * mm});
            skLineSegment(sketch, "E3774", {"start": v(8.38, -66.59) * mm, "end": v(8.46, -66.72) * mm});
            skLineSegment(sketch, "E3775", {"start": v(8.46, -66.72) * mm, "end": v(8.53, -66.85) * mm});
            skLineSegment(sketch, "E3776", {"start": v(8.53, -66.85) * mm, "end": v(8.6, -66.98) * mm});
            skLineSegment(sketch, "E3777", {"start": v(8.6, -66.98) * mm, "end": v(8.69, -67.11) * mm});
            skLineSegment(sketch, "E3778", {"start": v(8.69, -67.11) * mm, "end": v(8.77, -67.25) * mm});
            skLineSegment(sketch, "E3779", {"start": v(8.77, -67.25) * mm, "end": v(8.85, -67.38) * mm});
            skLineSegment(sketch, "E3780", {"start": v(8.85, -67.38) * mm, "end": v(8.93, -67.52) * mm});
            skLineSegment(sketch, "E3781", {"start": v(8.93, -67.52) * mm, "end": v(9.02, -67.66) * mm});
            skLineSegment(sketch, "E3782", {"start": v(9.02, -67.66) * mm, "end": v(9.1, -67.74) * mm});
            skLineSegment(sketch, "E3783", {"start": v(9.1, -67.74) * mm, "end": v(10.7, -67.5) * mm});
            skLineSegment(sketch, "E3784", {"start": v(10.7, -67.5) * mm, "end": v(10.76, -67.4) * mm});
            skLineSegment(sketch, "E3785", {"start": v(10.76, -67.4) * mm, "end": v(10.8, -67.25) * mm});
            skLineSegment(sketch, "E3786", {"start": v(10.8, -67.25) * mm, "end": v(10.85, -67.09) * mm});
            skLineSegment(sketch, "E3787", {"start": v(10.85, -67.09) * mm, "end": v(10.89, -66.94) * mm});
            skLineSegment(sketch, "E3788", {"start": v(10.89, -66.94) * mm, "end": v(10.93, -66.78) * mm});
            skLineSegment(sketch, "E3789", {"start": v(10.93, -66.78) * mm, "end": v(10.96, -66.64) * mm});
            skLineSegment(sketch, "E3790", {"start": v(10.96, -66.64) * mm, "end": v(11, -66.49) * mm});
            skLineSegment(sketch, "E3791", {"start": v(11, -66.49) * mm, "end": v(11.03, -66.34) * mm});
            skLineSegment(sketch, "E3792", {"start": v(11.03, -66.34) * mm, "end": v(11.06, -66.2) * mm});
            skLineSegment(sketch, "E3793", {"start": v(11.06, -66.2) * mm, "end": v(11.1, -66.05) * mm});
            skLineSegment(sketch, "E3794", {"start": v(11.1, -66.05) * mm, "end": v(11.13, -65.91) * mm});
            skLineSegment(sketch, "E3795", {"start": v(11.13, -65.91) * mm, "end": v(11.16, -65.77) * mm});
            skLineSegment(sketch, "E3796", {"start": v(11.16, -65.77) * mm, "end": v(11.18, -65.64) * mm});
            skLineSegment(sketch, "E3797", {"start": v(11.18, -65.64) * mm, "end": v(11.21, -65.5) * mm});
            skLineSegment(sketch, "E3798", {"start": v(11.21, -65.5) * mm, "end": v(11.24, -65.37) * mm});
            skLineSegment(sketch, "E3799", {"start": v(11.24, -65.37) * mm, "end": v(11.26, -65.23) * mm});
            skLineSegment(sketch, "E3800", {"start": v(11.26, -65.23) * mm, "end": v(11.28, -65.1) * mm});
            skLineSegment(sketch, "E3801", {"start": v(11.28, -65.1) * mm, "end": v(11.3, -64.98) * mm});
            skLineSegment(sketch, "E3802", {"start": v(11.3, -64.98) * mm, "end": v(11.33, -64.85) * mm});
            skLineSegment(sketch, "E3803", {"start": v(11.33, -64.85) * mm, "end": v(11.35, -64.73) * mm});
            skLineSegment(sketch, "E3804", {"start": v(11.35, -64.73) * mm, "end": v(11.37, -64.6) * mm});
            skLineSegment(sketch, "E3805", {"start": v(11.37, -64.6) * mm, "end": v(11.38, -64.49) * mm});
            skLineSegment(sketch, "E3806", {"start": v(11.38, -64.49) * mm, "end": v(11.4, -64.37) * mm});
            skLineSegment(sketch, "E3807", {"start": v(11.4, -64.37) * mm, "end": v(11.42, -64.26) * mm});
            skLineSegment(sketch, "E3808", {"start": v(11.42, -64.26) * mm, "end": v(11.43, -64.14) * mm});
            skLineSegment(sketch, "E3809", {"start": v(11.43, -64.14) * mm, "end": v(11.44, -64.03) * mm});
            skLineSegment(sketch, "E3810", {"start": v(11.44, -64.03) * mm, "end": v(11.46, -63.92) * mm});
            skLineSegment(sketch, "E3811", {"start": v(11.46, -63.92) * mm, "end": v(11.47, -63.81) * mm});
            skLineSegment(sketch, "E3812", {"start": v(11.47, -63.81) * mm, "end": v(11.48, -63.7) * mm});
            skLineSegment(sketch, "E3813", {"start": v(11.48, -63.7) * mm, "end": v(11.5, -63.6) * mm});
            skLineSegment(sketch, "E3814", {"start": v(11.5, -63.6) * mm, "end": v(11.5, -63.5) * mm});
            skLineSegment(sketch, "E3815", {"start": v(11.5, -63.5) * mm, "end": v(11.51, -63.4) * mm});
            skLineSegment(sketch, "E3816", {"start": v(11.51, -63.4) * mm, "end": v(11.52, -63.3) * mm});
            skLineSegment(sketch, "E3817", {"start": v(11.52, -63.3) * mm, "end": v(11.53, -63.2) * mm});
            skLineSegment(sketch, "E3818", {"start": v(11.53, -63.2) * mm, "end": v(11.53, -63.12) * mm});
            skLineSegment(sketch, "E3819", {"start": v(11.53, -63.12) * mm, "end": v(11.54, -63.02) * mm});
            skLineSegment(sketch, "E3820", {"start": v(11.54, -63.02) * mm, "end": v(11.55, -62.94) * mm});
            skLineSegment(sketch, "E3821", {"start": v(11.55, -62.94) * mm, "end": v(11.55, -62.85) * mm});
            skLineSegment(sketch, "E3822", {"start": v(11.55, -62.85) * mm, "end": v(11.55, -62.76) * mm});
            skLineSegment(sketch, "E3823", {"start": v(11.55, -62.76) * mm, "end": v(11.56, -62.68) * mm});
            skLineSegment(sketch, "E3824", {"start": v(11.56, -62.68) * mm, "end": v(11.77, -62.51) * mm});
            skLineSegment(sketch, "E3825", {"start": v(11.77, -62.51) * mm, "end": v(13.22, -62.22) * mm});
            skLineSegment(sketch, "E3826", {"start": v(13.22, -62.22) * mm, "end": v(13.49, -62.3) * mm});
            skLineSegment(sketch, "E3827", {"start": v(13.49, -62.3) * mm, "end": v(13.52, -62.37) * mm});
            skLineSegment(sketch, "E3828", {"start": v(13.52, -62.37) * mm, "end": v(13.56, -62.45) * mm});
            skLineSegment(sketch, "E3829", {"start": v(13.56, -62.45) * mm, "end": v(13.6, -62.52) * mm});
            skLineSegment(sketch, "E3830", {"start": v(13.6, -62.52) * mm, "end": v(13.64, -62.6) * mm});
            skLineSegment(sketch, "E3831", {"start": v(13.64, -62.6) * mm, "end": v(13.68, -62.69) * mm});
            skLineSegment(sketch, "E3832", {"start": v(13.68, -62.69) * mm, "end": v(13.72, -62.77) * mm});
            skLineSegment(sketch, "E3833", {"start": v(13.72, -62.77) * mm, "end": v(13.76, -62.86) * mm});
            skLineSegment(sketch, "E3834", {"start": v(13.76, -62.86) * mm, "end": v(13.8, -62.94) * mm});
            skLineSegment(sketch, "E3835", {"start": v(13.8, -62.94) * mm, "end": v(13.85, -63.03) * mm});
            skLineSegment(sketch, "E3836", {"start": v(13.85, -63.03) * mm, "end": v(13.9, -63.12) * mm});
            skLineSegment(sketch, "E3837", {"start": v(13.9, -63.12) * mm, "end": v(13.95, -63.21) * mm});
            skLineSegment(sketch, "E3838", {"start": v(13.95, -63.21) * mm, "end": v(14, -63.3) * mm});
            skLineSegment(sketch, "E3839", {"start": v(14, -63.3) * mm, "end": v(14.06, -63.4) * mm});
            skLineSegment(sketch, "E3840", {"start": v(14.06, -63.4) * mm, "end": v(14.11, -63.5) * mm});
            skLineSegment(sketch, "E3841", {"start": v(14.11, -63.5) * mm, "end": v(14.17, -63.6) * mm});
            skLineSegment(sketch, "E3842", {"start": v(14.17, -63.6) * mm, "end": v(14.23, -63.7) * mm});
            skLineSegment(sketch, "E3843", {"start": v(14.23, -63.7) * mm, "end": v(14.28, -63.8) * mm});
            skLineSegment(sketch, "E3844", {"start": v(14.28, -63.8) * mm, "end": v(14.35, -63.9) * mm});
            skLineSegment(sketch, "E3845", {"start": v(14.35, -63.9) * mm, "end": v(14.4, -64) * mm});
            skLineSegment(sketch, "E3846", {"start": v(14.4, -64) * mm, "end": v(14.47, -64.1) * mm});
            skLineSegment(sketch, "E3847", {"start": v(14.47, -64.1) * mm, "end": v(14.54, -64.2) * mm});
            skLineSegment(sketch, "E3848", {"start": v(14.54, -64.2) * mm, "end": v(14.6, -64.32) * mm});
            skLineSegment(sketch, "E3849", {"start": v(14.6, -64.32) * mm, "end": v(14.67, -64.43) * mm});
            skLineSegment(sketch, "E3850", {"start": v(14.67, -64.43) * mm, "end": v(14.75, -64.54) * mm});
            skLineSegment(sketch, "E3851", {"start": v(14.75, -64.54) * mm, "end": v(14.82, -64.65) * mm});
            skLineSegment(sketch, "E3852", {"start": v(14.82, -64.65) * mm, "end": v(14.9, -64.76) * mm});
            skLineSegment(sketch, "E3853", {"start": v(14.9, -64.76) * mm, "end": v(14.97, -64.88) * mm});
            skLineSegment(sketch, "E3854", {"start": v(14.97, -64.88) * mm, "end": v(15.05, -65) * mm});
            skLineSegment(sketch, "E3855", {"start": v(15.05, -65) * mm, "end": v(15.21, -65.23) * mm});
            skLineSegment(sketch, "E3856", {"start": v(15.21, -65.23) * mm, "end": v(15.3, -65.35) * mm});
            skLineSegment(sketch, "E3857", {"start": v(15.3, -65.35) * mm, "end": v(15.38, -65.47) * mm});
            skLineSegment(sketch, "E3858", {"start": v(15.38, -65.47) * mm, "end": v(15.47, -65.59) * mm});
            skLineSegment(sketch, "E3859", {"start": v(15.47, -65.59) * mm, "end": v(15.56, -65.71) * mm});
            skLineSegment(sketch, "E3860", {"start": v(15.56, -65.71) * mm, "end": v(15.65, -65.84) * mm});
            skLineSegment(sketch, "E3861", {"start": v(15.65, -65.84) * mm, "end": v(15.75, -65.96) * mm});
            skLineSegment(sketch, "E3862", {"start": v(15.75, -65.96) * mm, "end": v(15.84, -66.09) * mm});
            skLineSegment(sketch, "E3863", {"start": v(15.84, -66.09) * mm, "end": v(15.94, -66.22) * mm});
            skLineSegment(sketch, "E3864", {"start": v(15.94, -66.22) * mm, "end": v(16.04, -66.35) * mm});
            skLineSegment(sketch, "E3865", {"start": v(16.04, -66.35) * mm, "end": v(16.13, -66.42) * mm});
            skLineSegment(sketch, "E3866", {"start": v(16.13, -66.42) * mm, "end": v(17.7, -66.02) * mm});
            skLineSegment(sketch, "E3867", {"start": v(17.7, -66.02) * mm, "end": v(17.75, -65.9) * mm});
            skLineSegment(sketch, "E3868", {"start": v(17.75, -65.9) * mm, "end": v(17.78, -65.75) * mm});
            skLineSegment(sketch, "E3869", {"start": v(17.78, -65.75) * mm, "end": v(17.8, -65.59) * mm});
            skLineSegment(sketch, "E3870", {"start": v(17.8, -65.59) * mm, "end": v(17.82, -65.43) * mm});
            skLineSegment(sketch, "E3871", {"start": v(17.82, -65.43) * mm, "end": v(17.85, -65.28) * mm});
            skLineSegment(sketch, "E3872", {"start": v(17.85, -65.28) * mm, "end": v(17.87, -65.12) * mm});
            skLineSegment(sketch, "E3873", {"start": v(17.87, -65.12) * mm, "end": v(17.89, -64.97) * mm});
            skLineSegment(sketch, "E3874", {"start": v(17.89, -64.97) * mm, "end": v(17.9, -64.82) * mm});
            skLineSegment(sketch, "E3875", {"start": v(17.9, -64.82) * mm, "end": v(17.92, -64.68) * mm});
            skLineSegment(sketch, "E3876", {"start": v(17.92, -64.68) * mm, "end": v(17.94, -64.53) * mm});
            skLineSegment(sketch, "E3877", {"start": v(17.94, -64.53) * mm, "end": v(17.96, -64.39) * mm});
            skLineSegment(sketch, "E3878", {"start": v(17.96, -64.39) * mm, "end": v(17.97, -64.25) * mm});
            skLineSegment(sketch, "E3879", {"start": v(17.97, -64.25) * mm, "end": v(17.98, -64.1) * mm});
            skLineSegment(sketch, "E3880", {"start": v(17.98, -64.1) * mm, "end": v(18, -63.97) * mm});
            skLineSegment(sketch, "E3881", {"start": v(18, -63.97) * mm, "end": v(18, -63.83) * mm});
            skLineSegment(sketch, "E3882", {"start": v(18, -63.83) * mm, "end": v(18.02, -63.7) * mm});
            skLineSegment(sketch, "E3883", {"start": v(18.02, -63.7) * mm, "end": v(18.03, -63.57) * mm});
            skLineSegment(sketch, "E3884", {"start": v(18.03, -63.57) * mm, "end": v(18.04, -63.44) * mm});
            skLineSegment(sketch, "E3885", {"start": v(18.04, -63.44) * mm, "end": v(18.04, -63.31) * mm});
            skLineSegment(sketch, "E3886", {"start": v(18.04, -63.31) * mm, "end": v(18.05, -63.19) * mm});
            skLineSegment(sketch, "E3887", {"start": v(18.05, -63.19) * mm, "end": v(18.06, -63.07) * mm});
            skLineSegment(sketch, "E3888", {"start": v(18.06, -63.07) * mm, "end": v(18.06, -62.94) * mm});
            skLineSegment(sketch, "E3889", {"start": v(18.06, -62.94) * mm, "end": v(18.07, -62.83) * mm});
            skLineSegment(sketch, "E3890", {"start": v(18.07, -62.83) * mm, "end": v(18.07, -62.7) * mm});
            skLineSegment(sketch, "E3891", {"start": v(18.07, -62.7) * mm, "end": v(18.07, -62.6) * mm});
            skLineSegment(sketch, "E3892", {"start": v(18.07, -62.6) * mm, "end": v(18.08, -62.48) * mm});
            skLineSegment(sketch, "E3893", {"start": v(18.08, -62.48) * mm, "end": v(18.08, -62.37) * mm});
            skLineSegment(sketch, "E3894", {"start": v(18.08, -62.37) * mm, "end": v(18.08, -62.26) * mm});
            skLineSegment(sketch, "E3895", {"start": v(18.08, -62.26) * mm, "end": v(18.08, -62.05) * mm});
            skLineSegment(sketch, "E3896", {"start": v(18.08, -62.05) * mm, "end": v(18.08, -61.95) * mm});
            skLineSegment(sketch, "E3897", {"start": v(18.08, -61.95) * mm, "end": v(18.08, -61.85) * mm});
            skLineSegment(sketch, "E3898", {"start": v(18.08, -61.85) * mm, "end": v(18.07, -61.75) * mm});
            skLineSegment(sketch, "E3899", {"start": v(18.07, -61.75) * mm, "end": v(18.07, -61.66) * mm});
            skLineSegment(sketch, "E3900", {"start": v(18.07, -61.66) * mm, "end": v(18.07, -61.56) * mm});
            skLineSegment(sketch, "E3901", {"start": v(18.07, -61.56) * mm, "end": v(18.06, -61.47) * mm});
            skLineSegment(sketch, "E3902", {"start": v(18.06, -61.47) * mm, "end": v(18.06, -61.38) * mm});
            skLineSegment(sketch, "E3903", {"start": v(18.06, -61.38) * mm, "end": v(18.06, -61.3) * mm});
            skLineSegment(sketch, "E3904", {"start": v(18.06, -61.3) * mm, "end": v(18.05, -61.21) * mm});
            skLineSegment(sketch, "E3905", {"start": v(18.05, -61.21) * mm, "end": v(18.05, -61.13) * mm});
            skLineSegment(sketch, "E3906", {"start": v(18.05, -61.13) * mm, "end": v(18.24, -60.94) * mm});
            skLineSegment(sketch, "E3907", {"start": v(18.24, -60.94) * mm, "end": v(19.66, -60.5) * mm});
            skLineSegment(sketch, "E3908", {"start": v(19.66, -60.5) * mm, "end": v(19.92, -60.54) * mm});
            skLineSegment(sketch, "E3909", {"start": v(19.92, -60.54) * mm, "end": v(19.97, -60.61) * mm});
            skLineSegment(sketch, "E3910", {"start": v(19.97, -60.61) * mm, "end": v(20.01, -60.69) * mm});
            skLineSegment(sketch, "E3911", {"start": v(20.01, -60.69) * mm, "end": v(20.06, -60.76) * mm});
            skLineSegment(sketch, "E3912", {"start": v(20.06, -60.76) * mm, "end": v(20.1, -60.84) * mm});
            skLineSegment(sketch, "E3913", {"start": v(20.1, -60.84) * mm, "end": v(20.16, -60.91) * mm});
            skLineSegment(sketch, "E3914", {"start": v(20.16, -60.91) * mm, "end": v(20.2, -61) * mm});
            skLineSegment(sketch, "E3915", {"start": v(20.2, -61) * mm, "end": v(20.26, -61.07) * mm});
            skLineSegment(sketch, "E3916", {"start": v(20.26, -61.07) * mm, "end": v(20.31, -61.15) * mm});
            skLineSegment(sketch, "E3917", {"start": v(20.31, -61.15) * mm, "end": v(20.37, -61.24) * mm});
            skLineSegment(sketch, "E3918", {"start": v(20.37, -61.24) * mm, "end": v(20.43, -61.32) * mm});
            skLineSegment(sketch, "E3919", {"start": v(20.43, -61.32) * mm, "end": v(20.48, -61.4) * mm});
            skLineSegment(sketch, "E3920", {"start": v(20.48, -61.4) * mm, "end": v(20.55, -61.5) * mm});
            skLineSegment(sketch, "E3921", {"start": v(20.55, -61.5) * mm, "end": v(20.6, -61.58) * mm});
            skLineSegment(sketch, "E3922", {"start": v(20.6, -61.58) * mm, "end": v(20.67, -61.67) * mm});
            skLineSegment(sketch, "E3923", {"start": v(20.67, -61.67) * mm, "end": v(20.74, -61.76) * mm});
            skLineSegment(sketch, "E3924", {"start": v(20.74, -61.76) * mm, "end": v(20.8, -61.86) * mm});
            skLineSegment(sketch, "E3925", {"start": v(20.8, -61.86) * mm, "end": v(20.87, -61.95) * mm});
            skLineSegment(sketch, "E3926", {"start": v(20.87, -61.95) * mm, "end": v(20.94, -62.04) * mm});
            skLineSegment(sketch, "E3927", {"start": v(20.94, -62.04) * mm, "end": v(21.02, -62.14) * mm});
            skLineSegment(sketch, "E3928", {"start": v(21.02, -62.14) * mm, "end": v(21.1, -62.24) * mm});
            skLineSegment(sketch, "E3929", {"start": v(21.1, -62.24) * mm, "end": v(21.17, -62.34) * mm});
            skLineSegment(sketch, "E3930", {"start": v(21.17, -62.34) * mm, "end": v(21.25, -62.44) * mm});
            skLineSegment(sketch, "E3931", {"start": v(21.25, -62.44) * mm, "end": v(21.33, -62.54) * mm});
            skLineSegment(sketch, "E3932", {"start": v(21.33, -62.54) * mm, "end": v(21.41, -62.64) * mm});
            skLineSegment(sketch, "E3933", {"start": v(21.41, -62.64) * mm, "end": v(21.5, -62.74) * mm});
            skLineSegment(sketch, "E3934", {"start": v(21.5, -62.74) * mm, "end": v(21.58, -62.85) * mm});
            skLineSegment(sketch, "E3935", {"start": v(21.58, -62.85) * mm, "end": v(21.67, -62.96) * mm});
            skLineSegment(sketch, "E3936", {"start": v(21.67, -62.96) * mm, "end": v(21.76, -63.06) * mm});
            skLineSegment(sketch, "E3937", {"start": v(21.76, -63.06) * mm, "end": v(21.85, -63.17) * mm});
            skLineSegment(sketch, "E3938", {"start": v(21.85, -63.17) * mm, "end": v(21.95, -63.28) * mm});
            skLineSegment(sketch, "E3939", {"start": v(21.95, -63.28) * mm, "end": v(22.04, -63.39) * mm});
            skLineSegment(sketch, "E3940", {"start": v(22.04, -63.39) * mm, "end": v(22.14, -63.5) * mm});
            skLineSegment(sketch, "E3941", {"start": v(22.14, -63.5) * mm, "end": v(22.24, -63.61) * mm});
            skLineSegment(sketch, "E3942", {"start": v(22.24, -63.61) * mm, "end": v(22.34, -63.73) * mm});
            skLineSegment(sketch, "E3943", {"start": v(22.34, -63.73) * mm, "end": v(22.45, -63.84) * mm});
            skLineSegment(sketch, "E3944", {"start": v(22.45, -63.84) * mm, "end": v(22.56, -63.95) * mm});
            skLineSegment(sketch, "E3945", {"start": v(22.56, -63.95) * mm, "end": v(22.66, -64.07) * mm});
            skLineSegment(sketch, "E3946", {"start": v(22.66, -64.07) * mm, "end": v(22.77, -64.19) * mm});
            skLineSegment(sketch, "E3947", {"start": v(22.77, -64.19) * mm, "end": v(22.89, -64.3) * mm});
            skLineSegment(sketch, "E3948", {"start": v(22.89, -64.3) * mm, "end": v(22.98, -64.37) * mm});
            skLineSegment(sketch, "E3949", {"start": v(22.98, -64.37) * mm, "end": v(24.51, -63.8) * mm});
            skLineSegment(sketch, "E3950", {"start": v(24.51, -63.8) * mm, "end": v(24.54, -63.7) * mm});
            skLineSegment(sketch, "E3951", {"start": v(24.54, -63.7) * mm, "end": v(24.55, -63.53) * mm});
            skLineSegment(sketch, "E3952", {"start": v(24.55, -63.53) * mm, "end": v(24.56, -63.37) * mm});
            skLineSegment(sketch, "E3953", {"start": v(24.56, -63.37) * mm, "end": v(24.56, -63.21) * mm});
            skLineSegment(sketch, "E3954", {"start": v(24.56, -63.21) * mm, "end": v(24.57, -63.05) * mm});
            skLineSegment(sketch, "E3955", {"start": v(24.57, -63.05) * mm, "end": v(24.58, -62.9) * mm});
            skLineSegment(sketch, "E3956", {"start": v(24.58, -62.9) * mm, "end": v(24.58, -62.75) * mm});
            skLineSegment(sketch, "E3957", {"start": v(24.58, -62.75) * mm, "end": v(24.58, -62.6) * mm});
            skLineSegment(sketch, "E3958", {"start": v(24.58, -62.6) * mm, "end": v(24.59, -62.45) * mm});
            skLineSegment(sketch, "E3959", {"start": v(24.59, -62.45) * mm, "end": v(24.59, -62.3) * mm});
            skLineSegment(sketch, "E3960", {"start": v(24.59, -62.3) * mm, "end": v(24.59, -62.02) * mm});
            skLineSegment(sketch, "E3961", {"start": v(24.59, -62.02) * mm, "end": v(24.59, -61.88) * mm});
            skLineSegment(sketch, "E3962", {"start": v(24.59, -61.88) * mm, "end": v(24.58, -61.74) * mm});
            skLineSegment(sketch, "E3963", {"start": v(24.58, -61.74) * mm, "end": v(24.58, -61.6) * mm});
            skLineSegment(sketch, "E3964", {"start": v(24.58, -61.6) * mm, "end": v(24.58, -61.47) * mm});
            skLineSegment(sketch, "E3965", {"start": v(24.58, -61.47) * mm, "end": v(24.57, -61.34) * mm});
            skLineSegment(sketch, "E3966", {"start": v(24.57, -61.34) * mm, "end": v(24.57, -61.2) * mm});
            skLineSegment(sketch, "E3967", {"start": v(24.57, -61.2) * mm, "end": v(24.56, -61.08) * mm});
            skLineSegment(sketch, "E3968", {"start": v(24.56, -61.08) * mm, "end": v(24.56, -60.96) * mm});
            skLineSegment(sketch, "E3969", {"start": v(24.56, -60.96) * mm, "end": v(24.55, -60.83) * mm});
            skLineSegment(sketch, "E3970", {"start": v(24.55, -60.83) * mm, "end": v(24.54, -60.71) * mm});
            skLineSegment(sketch, "E3971", {"start": v(24.54, -60.71) * mm, "end": v(24.53, -60.6) * mm});
            skLineSegment(sketch, "E3972", {"start": v(24.53, -60.6) * mm, "end": v(24.53, -60.48) * mm});
            skLineSegment(sketch, "E3973", {"start": v(24.53, -60.48) * mm, "end": v(24.5, -60.25) * mm});
            skLineSegment(sketch, "E3974", {"start": v(24.5, -60.25) * mm, "end": v(24.5, -60.14) * mm});
            skLineSegment(sketch, "E3975", {"start": v(24.5, -60.14) * mm, "end": v(24.49, -60.03) * mm});
            skLineSegment(sketch, "E3976", {"start": v(24.49, -60.03) * mm, "end": v(24.48, -59.93) * mm});
            skLineSegment(sketch, "E3977", {"start": v(24.48, -59.93) * mm, "end": v(24.47, -59.82) * mm});
            skLineSegment(sketch, "E3978", {"start": v(24.47, -59.82) * mm, "end": v(24.45, -59.72) * mm});
            skLineSegment(sketch, "E3979", {"start": v(24.45, -59.72) * mm, "end": v(24.44, -59.62) * mm});
            skLineSegment(sketch, "E3980", {"start": v(24.44, -59.62) * mm, "end": v(24.43, -59.53) * mm});
            skLineSegment(sketch, "E3981", {"start": v(24.43, -59.53) * mm, "end": v(24.42, -59.43) * mm});
            skLineSegment(sketch, "E3982", {"start": v(24.42, -59.43) * mm, "end": v(24.4, -59.34) * mm});
            skLineSegment(sketch, "E3983", {"start": v(24.4, -59.34) * mm, "end": v(24.4, -59.25) * mm});
            skLineSegment(sketch, "E3984", {"start": v(24.4, -59.25) * mm, "end": v(24.38, -59.16) * mm});
            skLineSegment(sketch, "E3985", {"start": v(24.38, -59.16) * mm, "end": v(24.37, -59.07) * mm});
            skLineSegment(sketch, "E3986", {"start": v(24.37, -59.07) * mm, "end": v(24.35, -58.99) * mm});
            skLineSegment(sketch, "E3987", {"start": v(24.35, -58.99) * mm, "end": v(24.34, -58.9) * mm});
            skLineSegment(sketch, "E3988", {"start": v(24.34, -58.9) * mm, "end": v(24.51, -58.7) * mm});
            skLineSegment(sketch, "E3989", {"start": v(24.51, -58.7) * mm, "end": v(25.87, -58.11) * mm});
            skLineSegment(sketch, "E3990", {"start": v(25.87, -58.11) * mm, "end": v(26.14, -58.13) * mm});
            skLineSegment(sketch, "E3991", {"start": v(26.14, -58.13) * mm, "end": v(26.2, -58.2) * mm});
            skLineSegment(sketch, "E3992", {"start": v(26.2, -58.2) * mm, "end": v(26.25, -58.26) * mm});
            skLineSegment(sketch, "E3993", {"start": v(26.25, -58.26) * mm, "end": v(26.3, -58.33) * mm});
            skLineSegment(sketch, "E3994", {"start": v(26.3, -58.33) * mm, "end": v(26.35, -58.4) * mm});
            skLineSegment(sketch, "E3995", {"start": v(26.35, -58.4) * mm, "end": v(26.41, -58.47) * mm});
            skLineSegment(sketch, "E3996", {"start": v(26.41, -58.47) * mm, "end": v(26.47, -58.55) * mm});
            skLineSegment(sketch, "E3997", {"start": v(26.47, -58.55) * mm, "end": v(26.53, -58.62) * mm});
            skLineSegment(sketch, "E3998", {"start": v(26.53, -58.62) * mm, "end": v(26.6, -58.7) * mm});
            skLineSegment(sketch, "E3999", {"start": v(26.6, -58.7) * mm, "end": v(26.66, -58.77) * mm});
            skLineSegment(sketch, "E4000", {"start": v(26.66, -58.77) * mm, "end": v(26.72, -58.85) * mm});
            skLineSegment(sketch, "E4001", {"start": v(26.72, -58.85) * mm, "end": v(26.8, -58.93) * mm});
            skLineSegment(sketch, "E4002", {"start": v(26.8, -58.93) * mm, "end": v(26.86, -59) * mm});
            skLineSegment(sketch, "E4003", {"start": v(26.86, -59) * mm, "end": v(26.93, -59.1) * mm});
            skLineSegment(sketch, "E4004", {"start": v(26.93, -59.1) * mm, "end": v(27, -59.17) * mm});
            skLineSegment(sketch, "E4005", {"start": v(27, -59.17) * mm, "end": v(27.08, -59.26) * mm});
            skLineSegment(sketch, "E4006", {"start": v(27.08, -59.26) * mm, "end": v(27.16, -59.34) * mm});
            skLineSegment(sketch, "E4007", {"start": v(27.16, -59.34) * mm, "end": v(27.24, -59.43) * mm});
            skLineSegment(sketch, "E4008", {"start": v(27.24, -59.43) * mm, "end": v(27.32, -59.52) * mm});
            skLineSegment(sketch, "E4009", {"start": v(27.32, -59.52) * mm, "end": v(27.4, -59.6) * mm});
            skLineSegment(sketch, "E4010", {"start": v(27.4, -59.6) * mm, "end": v(27.48, -59.7) * mm});
            skLineSegment(sketch, "E4011", {"start": v(27.48, -59.7) * mm, "end": v(27.57, -59.78) * mm});
            skLineSegment(sketch, "E4012", {"start": v(27.57, -59.78) * mm, "end": v(27.66, -59.87) * mm});
            skLineSegment(sketch, "E4013", {"start": v(27.66, -59.87) * mm, "end": v(27.75, -59.97) * mm});
            skLineSegment(sketch, "E4014", {"start": v(27.75, -59.97) * mm, "end": v(27.84, -60.06) * mm});
            skLineSegment(sketch, "E4015", {"start": v(27.84, -60.06) * mm, "end": v(27.94, -60.15) * mm});
            skLineSegment(sketch, "E4016", {"start": v(27.94, -60.15) * mm, "end": v(28.03, -60.25) * mm});
            skLineSegment(sketch, "E4017", {"start": v(28.03, -60.25) * mm, "end": v(28.13, -60.35) * mm});
            skLineSegment(sketch, "E4018", {"start": v(28.13, -60.35) * mm, "end": v(28.23, -60.44) * mm});
            skLineSegment(sketch, "E4019", {"start": v(28.23, -60.44) * mm, "end": v(28.34, -60.54) * mm});
            skLineSegment(sketch, "E4020", {"start": v(28.34, -60.54) * mm, "end": v(28.44, -60.64) * mm});
            skLineSegment(sketch, "E4021", {"start": v(28.44, -60.64) * mm, "end": v(28.55, -60.74) * mm});
            skLineSegment(sketch, "E4022", {"start": v(28.55, -60.74) * mm, "end": v(28.77, -60.94) * mm});
            skLineSegment(sketch, "E4023", {"start": v(28.77, -60.94) * mm, "end": v(28.88, -61.04) * mm});
            skLineSegment(sketch, "E4024", {"start": v(28.88, -61.04) * mm, "end": v(29, -61.14) * mm});
            skLineSegment(sketch, "E4025", {"start": v(29, -61.14) * mm, "end": v(29.12, -61.25) * mm});
            skLineSegment(sketch, "E4026", {"start": v(29.12, -61.25) * mm, "end": v(29.24, -61.35) * mm});
            skLineSegment(sketch, "E4027", {"start": v(29.24, -61.35) * mm, "end": v(29.36, -61.45) * mm});
            skLineSegment(sketch, "E4028", {"start": v(29.36, -61.45) * mm, "end": v(29.48, -61.56) * mm});
            skLineSegment(sketch, "E4029", {"start": v(29.48, -61.56) * mm, "end": v(29.59, -61.61) * mm});
            skLineSegment(sketch, "E4030", {"start": v(29.59, -61.61) * mm, "end": v(31.05, -60.9) * mm});
            skLineSegment(sketch, "E4031", {"start": v(31.05, -60.9) * mm, "end": v(31.07, -60.78) * mm});
            skLineSegment(sketch, "E4032", {"start": v(31.07, -60.78) * mm, "end": v(31.06, -60.62) * mm});
            skLineSegment(sketch, "E4033", {"start": v(31.06, -60.62) * mm, "end": v(31.05, -60.45) * mm});
            skLineSegment(sketch, "E4034", {"start": v(31.05, -60.45) * mm, "end": v(31.04, -60.3) * mm});
            skLineSegment(sketch, "E4035", {"start": v(31.04, -60.3) * mm, "end": v(31.03, -60.14) * mm});
            skLineSegment(sketch, "E4036", {"start": v(31.03, -60.14) * mm, "end": v(31.02, -59.99) * mm});
            skLineSegment(sketch, "E4037", {"start": v(31.02, -59.99) * mm, "end": v(31, -59.83) * mm});
            skLineSegment(sketch, "E4038", {"start": v(31, -59.83) * mm, "end": v(31, -59.68) * mm});
            skLineSegment(sketch, "E4039", {"start": v(31, -59.68) * mm, "end": v(30.98, -59.54) * mm});
            skLineSegment(sketch, "E4040", {"start": v(30.98, -59.54) * mm, "end": v(30.96, -59.4) * mm});
            skLineSegment(sketch, "E4041", {"start": v(30.96, -59.4) * mm, "end": v(30.95, -59.25) * mm});
            skLineSegment(sketch, "E4042", {"start": v(30.95, -59.25) * mm, "end": v(30.93, -59.1) * mm});
            skLineSegment(sketch, "E4043", {"start": v(30.93, -59.1) * mm, "end": v(30.92, -58.97) * mm});
            skLineSegment(sketch, "E4044", {"start": v(30.92, -58.97) * mm, "end": v(30.9, -58.83) * mm});
            skLineSegment(sketch, "E4045", {"start": v(30.9, -58.83) * mm, "end": v(30.89, -58.7) * mm});
            skLineSegment(sketch, "E4046", {"start": v(30.89, -58.7) * mm, "end": v(30.87, -58.56) * mm});
            skLineSegment(sketch, "E4047", {"start": v(30.87, -58.56) * mm, "end": v(30.85, -58.43) * mm});
            skLineSegment(sketch, "E4048", {"start": v(30.85, -58.43) * mm, "end": v(30.83, -58.3) * mm});
            skLineSegment(sketch, "E4049", {"start": v(30.83, -58.3) * mm, "end": v(30.81, -58.18) * mm});
            skLineSegment(sketch, "E4050", {"start": v(30.81, -58.18) * mm, "end": v(30.8, -58.06) * mm});
            skLineSegment(sketch, "E4051", {"start": v(30.8, -58.06) * mm, "end": v(30.77, -57.93) * mm});
            skLineSegment(sketch, "E4052", {"start": v(30.77, -57.93) * mm, "end": v(30.75, -57.81) * mm});
            skLineSegment(sketch, "E4053", {"start": v(30.75, -57.81) * mm, "end": v(30.73, -57.7) * mm});
            skLineSegment(sketch, "E4054", {"start": v(30.73, -57.7) * mm, "end": v(30.71, -57.58) * mm});
            skLineSegment(sketch, "E4055", {"start": v(30.71, -57.58) * mm, "end": v(30.7, -57.47) * mm});
            skLineSegment(sketch, "E4056", {"start": v(30.7, -57.47) * mm, "end": v(30.67, -57.36) * mm});
            skLineSegment(sketch, "E4057", {"start": v(30.67, -57.36) * mm, "end": v(30.65, -57.25) * mm});
            skLineSegment(sketch, "E4058", {"start": v(30.65, -57.25) * mm, "end": v(30.63, -57.14) * mm});
            skLineSegment(sketch, "E4059", {"start": v(30.63, -57.14) * mm, "end": v(30.6, -57.04) * mm});
            skLineSegment(sketch, "E4060", {"start": v(30.6, -57.04) * mm, "end": v(30.58, -56.94) * mm});
            skLineSegment(sketch, "E4061", {"start": v(30.58, -56.94) * mm, "end": v(30.56, -56.84) * mm});
            skLineSegment(sketch, "E4062", {"start": v(30.56, -56.84) * mm, "end": v(30.54, -56.74) * mm});
            skLineSegment(sketch, "E4063", {"start": v(30.54, -56.74) * mm, "end": v(30.52, -56.65) * mm});
            skLineSegment(sketch, "E4064", {"start": v(30.52, -56.65) * mm, "end": v(30.5, -56.55) * mm});
            skLineSegment(sketch, "E4065", {"start": v(30.5, -56.55) * mm, "end": v(30.47, -56.46) * mm});
            skLineSegment(sketch, "E4066", {"start": v(30.47, -56.46) * mm, "end": v(30.45, -56.37) * mm});
            skLineSegment(sketch, "E4067", {"start": v(30.45, -56.37) * mm, "end": v(30.43, -56.29) * mm});
            skLineSegment(sketch, "E4068", {"start": v(30.43, -56.29) * mm, "end": v(30.4, -56.2) * mm});
            skLineSegment(sketch, "E4069", {"start": v(30.4, -56.2) * mm, "end": v(30.38, -56.12) * mm});
            skLineSegment(sketch, "E4070", {"start": v(30.38, -56.12) * mm, "end": v(30.36, -56.04) * mm});
            skLineSegment(sketch, "E4071", {"start": v(30.36, -56.04) * mm, "end": v(30.51, -55.81) * mm});
            skLineSegment(sketch, "E4072", {"start": v(30.51, -55.81) * mm, "end": v(31.8, -55.09) * mm});
            skLineSegment(sketch, "E4073", {"start": v(31.8, -55.09) * mm, "end": v(32.08, -55.08) * mm});
            skLineSegment(sketch, "E4074", {"start": v(32.08, -55.08) * mm, "end": v(32.13, -55.14) * mm});
            skLineSegment(sketch, "E4075", {"start": v(32.13, -55.14) * mm, "end": v(32.2, -55.2) * mm});
            skLineSegment(sketch, "E4076", {"start": v(32.2, -55.2) * mm, "end": v(32.25, -55.26) * mm});
            skLineSegment(sketch, "E4077", {"start": v(32.25, -55.26) * mm, "end": v(32.32, -55.33) * mm});
            skLineSegment(sketch, "E4078", {"start": v(32.32, -55.33) * mm, "end": v(32.38, -55.4) * mm});
            skLineSegment(sketch, "E4079", {"start": v(32.38, -55.4) * mm, "end": v(32.44, -55.46) * mm});
            skLineSegment(sketch, "E4080", {"start": v(32.44, -55.46) * mm, "end": v(32.51, -55.53) * mm});
            skLineSegment(sketch, "E4081", {"start": v(32.51, -55.53) * mm, "end": v(32.58, -55.6) * mm});
            skLineSegment(sketch, "E4082", {"start": v(32.58, -55.6) * mm, "end": v(32.65, -55.66) * mm});
            skLineSegment(sketch, "E4083", {"start": v(32.65, -55.66) * mm, "end": v(32.8, -55.8) * mm});
            skLineSegment(sketch, "E4084", {"start": v(32.8, -55.8) * mm, "end": v(32.88, -55.88) * mm});
            skLineSegment(sketch, "E4085", {"start": v(32.88, -55.88) * mm, "end": v(32.96, -55.95) * mm});
            skLineSegment(sketch, "E4086", {"start": v(32.96, -55.95) * mm, "end": v(33.04, -56.03) * mm});
            skLineSegment(sketch, "E4087", {"start": v(33.04, -56.03) * mm, "end": v(33.13, -56.1) * mm});
            skLineSegment(sketch, "E4088", {"start": v(33.13, -56.1) * mm, "end": v(33.21, -56.18) * mm});
            skLineSegment(sketch, "E4089", {"start": v(33.21, -56.18) * mm, "end": v(33.3, -56.26) * mm});
            skLineSegment(sketch, "E4090", {"start": v(33.3, -56.26) * mm, "end": v(33.39, -56.33) * mm});
            skLineSegment(sketch, "E4091", {"start": v(33.39, -56.33) * mm, "end": v(33.48, -56.41) * mm});
            skLineSegment(sketch, "E4092", {"start": v(33.48, -56.41) * mm, "end": v(33.57, -56.5) * mm});
            skLineSegment(sketch, "E4093", {"start": v(33.57, -56.5) * mm, "end": v(33.67, -56.57) * mm});
            skLineSegment(sketch, "E4094", {"start": v(33.67, -56.57) * mm, "end": v(33.77, -56.66) * mm});
            skLineSegment(sketch, "E4095", {"start": v(33.77, -56.66) * mm, "end": v(33.97, -56.82) * mm});
            skLineSegment(sketch, "E4096", {"start": v(33.97, -56.82) * mm, "end": v(34.07, -56.9) * mm});
            skLineSegment(sketch, "E4097", {"start": v(34.07, -56.9) * mm, "end": v(34.18, -56.99) * mm});
            skLineSegment(sketch, "E4098", {"start": v(34.18, -56.99) * mm, "end": v(34.29, -57.07) * mm});
            skLineSegment(sketch, "E4099", {"start": v(34.29, -57.07) * mm, "end": v(34.4, -57.16) * mm});
            skLineSegment(sketch, "E4100", {"start": v(34.4, -57.16) * mm, "end": v(34.51, -57.25) * mm});
            skLineSegment(sketch, "E4101", {"start": v(34.51, -57.25) * mm, "end": v(34.62, -57.33) * mm});
            skLineSegment(sketch, "E4102", {"start": v(34.62, -57.33) * mm, "end": v(34.74, -57.42) * mm});
            skLineSegment(sketch, "E4103", {"start": v(34.74, -57.42) * mm, "end": v(34.86, -57.5) * mm});
            skLineSegment(sketch, "E4104", {"start": v(34.86, -57.5) * mm, "end": v(34.98, -57.6) * mm});
            skLineSegment(sketch, "E4105", {"start": v(34.98, -57.6) * mm, "end": v(35.1, -57.69) * mm});
            skLineSegment(sketch, "E4106", {"start": v(35.1, -57.69) * mm, "end": v(35.23, -57.78) * mm});
            skLineSegment(sketch, "E4107", {"start": v(35.23, -57.78) * mm, "end": v(35.36, -57.87) * mm});
            skLineSegment(sketch, "E4108", {"start": v(35.36, -57.87) * mm, "end": v(35.5, -57.96) * mm});
            skLineSegment(sketch, "E4109", {"start": v(35.5, -57.96) * mm, "end": v(35.62, -58.05) * mm});
            skLineSegment(sketch, "E4110", {"start": v(35.62, -58.05) * mm, "end": v(35.76, -58.14) * mm});
            skLineSegment(sketch, "E4111", {"start": v(35.76, -58.14) * mm, "end": v(35.86, -58.18) * mm});
            skLineSegment(sketch, "E4112", {"start": v(35.86, -58.18) * mm, "end": v(37.24, -57.31) * mm});
            skLineSegment(sketch, "E4113", {"start": v(37.24, -57.31) * mm, "end": v(37.25, -57.2) * mm});
            skLineSegment(sketch, "E4114", {"start": v(37.25, -57.2) * mm, "end": v(37.22, -57.04) * mm});
            skLineSegment(sketch, "E4115", {"start": v(37.22, -57.04) * mm, "end": v(37.2, -56.88) * mm});
            skLineSegment(sketch, "E4116", {"start": v(37.2, -56.88) * mm, "end": v(37.17, -56.72) * mm});
            skLineSegment(sketch, "E4117", {"start": v(37.17, -56.72) * mm, "end": v(37.14, -56.57) * mm});
            skLineSegment(sketch, "E4118", {"start": v(37.14, -56.57) * mm, "end": v(37.12, -56.42) * mm});
            skLineSegment(sketch, "E4119", {"start": v(37.12, -56.42) * mm, "end": v(37.09, -56.27) * mm});
            skLineSegment(sketch, "E4120", {"start": v(37.09, -56.27) * mm, "end": v(37.06, -56.12) * mm});
            skLineSegment(sketch, "E4121", {"start": v(37.06, -56.12) * mm, "end": v(37.03, -55.97) * mm});
            skLineSegment(sketch, "E4122", {"start": v(37.03, -55.97) * mm, "end": v(37, -55.83) * mm});
            skLineSegment(sketch, "E4123", {"start": v(37, -55.83) * mm, "end": v(36.97, -55.69) * mm});
            skLineSegment(sketch, "E4124", {"start": v(36.97, -55.69) * mm, "end": v(36.94, -55.55) * mm});
            skLineSegment(sketch, "E4125", {"start": v(36.94, -55.55) * mm, "end": v(36.91, -55.41) * mm});
            skLineSegment(sketch, "E4126", {"start": v(36.91, -55.41) * mm, "end": v(36.88, -55.28) * mm});
            skLineSegment(sketch, "E4127", {"start": v(36.88, -55.28) * mm, "end": v(36.85, -55.14) * mm});
            skLineSegment(sketch, "E4128", {"start": v(36.85, -55.14) * mm, "end": v(36.82, -55.02) * mm});
            skLineSegment(sketch, "E4129", {"start": v(36.82, -55.02) * mm, "end": v(36.79, -54.89) * mm});
            skLineSegment(sketch, "E4130", {"start": v(36.79, -54.89) * mm, "end": v(36.76, -54.76) * mm});
            skLineSegment(sketch, "E4131", {"start": v(36.76, -54.76) * mm, "end": v(36.73, -54.64) * mm});
            skLineSegment(sketch, "E4132", {"start": v(36.73, -54.64) * mm, "end": v(36.7, -54.52) * mm});
            skLineSegment(sketch, "E4133", {"start": v(36.7, -54.52) * mm, "end": v(36.66, -54.4) * mm});
            skLineSegment(sketch, "E4134", {"start": v(36.66, -54.4) * mm, "end": v(36.63, -54.28) * mm});
            skLineSegment(sketch, "E4135", {"start": v(36.63, -54.28) * mm, "end": v(36.6, -54.17) * mm});
            skLineSegment(sketch, "E4136", {"start": v(36.6, -54.17) * mm, "end": v(36.56, -54.06) * mm});
            skLineSegment(sketch, "E4137", {"start": v(36.56, -54.06) * mm, "end": v(36.53, -53.95) * mm});
            skLineSegment(sketch, "E4138", {"start": v(36.53, -53.95) * mm, "end": v(36.5, -53.84) * mm});
            skLineSegment(sketch, "E4139", {"start": v(36.5, -53.84) * mm, "end": v(36.47, -53.73) * mm});
            skLineSegment(sketch, "E4140", {"start": v(36.47, -53.73) * mm, "end": v(36.43, -53.63) * mm});
            skLineSegment(sketch, "E4141", {"start": v(36.43, -53.63) * mm, "end": v(36.4, -53.53) * mm});
            skLineSegment(sketch, "E4142", {"start": v(36.4, -53.53) * mm, "end": v(36.37, -53.43) * mm});
            skLineSegment(sketch, "E4143", {"start": v(36.37, -53.43) * mm, "end": v(36.34, -53.33) * mm});
            skLineSegment(sketch, "E4144", {"start": v(36.34, -53.33) * mm, "end": v(36.3, -53.24) * mm});
            skLineSegment(sketch, "E4145", {"start": v(36.3, -53.24) * mm, "end": v(36.27, -53.15) * mm});
            skLineSegment(sketch, "E4146", {"start": v(36.27, -53.15) * mm, "end": v(36.24, -53.06) * mm});
            skLineSegment(sketch, "E4147", {"start": v(36.24, -53.06) * mm, "end": v(36.2, -52.97) * mm});
            skLineSegment(sketch, "E4148", {"start": v(36.2, -52.97) * mm, "end": v(36.18, -52.88) * mm});
            skLineSegment(sketch, "E4149", {"start": v(36.18, -52.88) * mm, "end": v(36.15, -52.8) * mm});
            skLineSegment(sketch, "E4150", {"start": v(36.15, -52.8) * mm, "end": v(36.11, -52.72) * mm});
            skLineSegment(sketch, "E4151", {"start": v(36.11, -52.72) * mm, "end": v(36.08, -52.64) * mm});
            skLineSegment(sketch, "E4152", {"start": v(36.08, -52.64) * mm, "end": v(36.05, -52.56) * mm});
            skLineSegment(sketch, "E4153", {"start": v(36.05, -52.56) * mm, "end": v(36.18, -52.32) * mm});
            skLineSegment(sketch, "E4154", {"start": v(36.18, -52.32) * mm, "end": v(37.39, -51.46) * mm});
            skLineSegment(sketch, "E4155", {"start": v(37.39, -51.46) * mm, "end": v(37.66, -51.42) * mm});
            skLineSegment(sketch, "E4156", {"start": v(37.66, -51.42) * mm, "end": v(37.72, -51.48) * mm});
            skLineSegment(sketch, "E4157", {"start": v(37.72, -51.48) * mm, "end": v(37.79, -51.53) * mm});
            skLineSegment(sketch, "E4158", {"start": v(37.79, -51.53) * mm, "end": v(37.85, -51.59) * mm});
            skLineSegment(sketch, "E4159", {"start": v(37.85, -51.59) * mm, "end": v(37.92, -51.64) * mm});
            skLineSegment(sketch, "E4160", {"start": v(37.92, -51.64) * mm, "end": v(38, -51.7) * mm});
            skLineSegment(sketch, "E4161", {"start": v(38, -51.7) * mm, "end": v(38.06, -51.76) * mm});
            skLineSegment(sketch, "E4162", {"start": v(38.06, -51.76) * mm, "end": v(38.14, -51.82) * mm});
            skLineSegment(sketch, "E4163", {"start": v(38.14, -51.82) * mm, "end": v(38.22, -51.88) * mm});
            skLineSegment(sketch, "E4164", {"start": v(38.22, -51.88) * mm, "end": v(38.3, -51.95) * mm});
            skLineSegment(sketch, "E4165", {"start": v(38.3, -51.95) * mm, "end": v(38.37, -52) * mm});
            skLineSegment(sketch, "E4166", {"start": v(38.37, -52) * mm, "end": v(38.46, -52.07) * mm});
            skLineSegment(sketch, "E4167", {"start": v(38.46, -52.07) * mm, "end": v(38.54, -52.14) * mm});
            skLineSegment(sketch, "E4168", {"start": v(38.54, -52.14) * mm, "end": v(38.63, -52.2) * mm});
            skLineSegment(sketch, "E4169", {"start": v(38.63, -52.2) * mm, "end": v(38.72, -52.27) * mm});
            skLineSegment(sketch, "E4170", {"start": v(38.72, -52.27) * mm, "end": v(38.8, -52.33) * mm});
            skLineSegment(sketch, "E4171", {"start": v(38.8, -52.33) * mm, "end": v(38.9, -52.4) * mm});
            skLineSegment(sketch, "E4172", {"start": v(38.9, -52.4) * mm, "end": v(39, -52.47) * mm});
            skLineSegment(sketch, "E4173", {"start": v(39, -52.47) * mm, "end": v(39.1, -52.54) * mm});
            skLineSegment(sketch, "E4174", {"start": v(39.1, -52.54) * mm, "end": v(39.2, -52.6) * mm});
            skLineSegment(sketch, "E4175", {"start": v(39.2, -52.6) * mm, "end": v(39.3, -52.67) * mm});
            skLineSegment(sketch, "E4176", {"start": v(39.3, -52.67) * mm, "end": v(39.4, -52.74) * mm});
            skLineSegment(sketch, "E4177", {"start": v(39.4, -52.74) * mm, "end": v(39.5, -52.82) * mm});
            skLineSegment(sketch, "E4178", {"start": v(39.5, -52.82) * mm, "end": v(39.72, -52.96) * mm});
            skLineSegment(sketch, "E4179", {"start": v(39.72, -52.96) * mm, "end": v(39.83, -53.03) * mm});
            skLineSegment(sketch, "E4180", {"start": v(39.83, -53.03) * mm, "end": v(39.95, -53.1) * mm});
            skLineSegment(sketch, "E4181", {"start": v(39.95, -53.1) * mm, "end": v(40.07, -53.18) * mm});
            skLineSegment(sketch, "E4182", {"start": v(40.07, -53.18) * mm, "end": v(40.18, -53.25) * mm});
            skLineSegment(sketch, "E4183", {"start": v(40.18, -53.25) * mm, "end": v(40.3, -53.33) * mm});
            skLineSegment(sketch, "E4184", {"start": v(40.3, -53.33) * mm, "end": v(40.43, -53.4) * mm});
            skLineSegment(sketch, "E4185", {"start": v(40.43, -53.4) * mm, "end": v(40.55, -53.48) * mm});
            skLineSegment(sketch, "E4186", {"start": v(40.55, -53.48) * mm, "end": v(40.68, -53.55) * mm});
            skLineSegment(sketch, "E4187", {"start": v(40.68, -53.55) * mm, "end": v(40.81, -53.63) * mm});
            skLineSegment(sketch, "E4188", {"start": v(40.81, -53.63) * mm, "end": v(40.94, -53.7) * mm});
            skLineSegment(sketch, "E4189", {"start": v(40.94, -53.7) * mm, "end": v(41.08, -53.78) * mm});
            skLineSegment(sketch, "E4190", {"start": v(41.08, -53.78) * mm, "end": v(41.21, -53.86) * mm});
            skLineSegment(sketch, "E4191", {"start": v(41.21, -53.86) * mm, "end": v(41.35, -53.93) * mm});
            skLineSegment(sketch, "E4192", {"start": v(41.35, -53.93) * mm, "end": v(41.5, -54) * mm});
            skLineSegment(sketch, "E4193", {"start": v(41.5, -54) * mm, "end": v(41.64, -54.09) * mm});
            skLineSegment(sketch, "E4194", {"start": v(41.64, -54.09) * mm, "end": v(41.75, -54.12) * mm});
            skLineSegment(sketch, "E4195", {"start": v(41.75, -54.12) * mm, "end": v(43.03, -53.1) * mm});
            skLineSegment(sketch, "E4196", {"start": v(43.03, -53.1) * mm, "end": v(43.02, -53) * mm});
            skLineSegment(sketch, "E4197", {"start": v(43.02, -53) * mm, "end": v(42.98, -52.83) * mm});
            skLineSegment(sketch, "E4198", {"start": v(42.98, -52.83) * mm, "end": v(42.94, -52.68) * mm});
            skLineSegment(sketch, "E4199", {"start": v(42.94, -52.68) * mm, "end": v(42.9, -52.53) * mm});
            skLineSegment(sketch, "E4200", {"start": v(42.9, -52.53) * mm, "end": v(42.85, -52.38) * mm});
            skLineSegment(sketch, "E4201", {"start": v(42.85, -52.38) * mm, "end": v(42.81, -52.23) * mm});
            skLineSegment(sketch, "E4202", {"start": v(42.81, -52.23) * mm, "end": v(42.77, -52.08) * mm});
            skLineSegment(sketch, "E4203", {"start": v(42.77, -52.08) * mm, "end": v(42.72, -51.94) * mm});
            skLineSegment(sketch, "E4204", {"start": v(42.72, -51.94) * mm, "end": v(42.68, -51.8) * mm});
            skLineSegment(sketch, "E4205", {"start": v(42.68, -51.8) * mm, "end": v(42.64, -51.65) * mm});
            skLineSegment(sketch, "E4206", {"start": v(42.64, -51.65) * mm, "end": v(42.6, -51.52) * mm});
            skLineSegment(sketch, "E4207", {"start": v(42.6, -51.52) * mm, "end": v(42.55, -51.38) * mm});
            skLineSegment(sketch, "E4208", {"start": v(42.55, -51.38) * mm, "end": v(42.5, -51.25) * mm});
            skLineSegment(sketch, "E4209", {"start": v(42.5, -51.25) * mm, "end": v(42.46, -51.12) * mm});
            skLineSegment(sketch, "E4210", {"start": v(42.46, -51.12) * mm, "end": v(42.41, -51) * mm});
            skLineSegment(sketch, "E4211", {"start": v(42.41, -51) * mm, "end": v(42.37, -50.87) * mm});
            skLineSegment(sketch, "E4212", {"start": v(42.37, -50.87) * mm, "end": v(42.33, -50.74) * mm});
            skLineSegment(sketch, "E4213", {"start": v(42.33, -50.74) * mm, "end": v(42.28, -50.62) * mm});
            skLineSegment(sketch, "E4214", {"start": v(42.28, -50.62) * mm, "end": v(42.24, -50.5) * mm});
            skLineSegment(sketch, "E4215", {"start": v(42.24, -50.5) * mm, "end": v(42.2, -50.38) * mm});
            skLineSegment(sketch, "E4216", {"start": v(42.2, -50.38) * mm, "end": v(42.15, -50.27) * mm});
            skLineSegment(sketch, "E4217", {"start": v(42.15, -50.27) * mm, "end": v(42.1, -50.16) * mm});
            skLineSegment(sketch, "E4218", {"start": v(42.1, -50.16) * mm, "end": v(42.06, -50.05) * mm});
            skLineSegment(sketch, "E4219", {"start": v(42.06, -50.05) * mm, "end": v(42.01, -49.94) * mm});
            skLineSegment(sketch, "E4220", {"start": v(42.01, -49.94) * mm, "end": v(41.97, -49.83) * mm});
            skLineSegment(sketch, "E4221", {"start": v(41.97, -49.83) * mm, "end": v(41.93, -49.73) * mm});
            skLineSegment(sketch, "E4222", {"start": v(41.93, -49.73) * mm, "end": v(41.88, -49.63) * mm});
            skLineSegment(sketch, "E4223", {"start": v(41.88, -49.63) * mm, "end": v(41.84, -49.53) * mm});
            skLineSegment(sketch, "E4224", {"start": v(41.84, -49.53) * mm, "end": v(41.8, -49.43) * mm});
            skLineSegment(sketch, "E4225", {"start": v(41.8, -49.43) * mm, "end": v(41.75, -49.34) * mm});
            skLineSegment(sketch, "E4226", {"start": v(41.75, -49.34) * mm, "end": v(41.71, -49.24) * mm});
            skLineSegment(sketch, "E4227", {"start": v(41.71, -49.24) * mm, "end": v(41.67, -49.15) * mm});
            skLineSegment(sketch, "E4228", {"start": v(41.67, -49.15) * mm, "end": v(41.63, -49.06) * mm});
            skLineSegment(sketch, "E4229", {"start": v(41.63, -49.06) * mm, "end": v(41.59, -48.98) * mm});
            skLineSegment(sketch, "E4230", {"start": v(41.59, -48.98) * mm, "end": v(41.55, -48.9) * mm});
            skLineSegment(sketch, "E4231", {"start": v(41.55, -48.9) * mm, "end": v(41.5, -48.81) * mm});
            skLineSegment(sketch, "E4232", {"start": v(41.5, -48.81) * mm, "end": v(41.47, -48.73) * mm});
            skLineSegment(sketch, "E4233", {"start": v(41.47, -48.73) * mm, "end": v(41.43, -48.65) * mm});
            skLineSegment(sketch, "E4234", {"start": v(41.43, -48.65) * mm, "end": v(41.39, -48.58) * mm});
            skLineSegment(sketch, "E4235", {"start": v(41.39, -48.58) * mm, "end": v(41.35, -48.5) * mm});
            skLineSegment(sketch, "E4236", {"start": v(41.35, -48.5) * mm, "end": v(41.45, -48.25) * mm});
            skLineSegment(sketch, "E4237", {"start": v(41.45, -48.25) * mm, "end": v(42.56, -47.27) * mm});
            skLineSegment(sketch, "E4238", {"start": v(42.56, -47.27) * mm, "end": v(42.83, -47.2) * mm});
            skLineSegment(sketch, "E4239", {"start": v(42.83, -47.2) * mm, "end": v(42.9, -47.25) * mm});
            skLineSegment(sketch, "E4240", {"start": v(42.9, -47.25) * mm, "end": v(42.96, -47.3) * mm});
            skLineSegment(sketch, "E4241", {"start": v(42.96, -47.3) * mm, "end": v(43.04, -47.35) * mm});
            skLineSegment(sketch, "E4242", {"start": v(43.04, -47.35) * mm, "end": v(43.11, -47.4) * mm});
            skLineSegment(sketch, "E4243", {"start": v(43.11, -47.4) * mm, "end": v(43.19, -47.45) * mm});
            skLineSegment(sketch, "E4244", {"start": v(43.19, -47.45) * mm, "end": v(43.27, -47.5) * mm});
            skLineSegment(sketch, "E4245", {"start": v(43.27, -47.5) * mm, "end": v(43.35, -47.55) * mm});
            skLineSegment(sketch, "E4246", {"start": v(43.35, -47.55) * mm, "end": v(43.43, -47.6) * mm});
            skLineSegment(sketch, "E4247", {"start": v(43.43, -47.6) * mm, "end": v(43.51, -47.66) * mm});
            skLineSegment(sketch, "E4248", {"start": v(43.51, -47.66) * mm, "end": v(43.6, -47.71) * mm});
            skLineSegment(sketch, "E4249", {"start": v(43.6, -47.71) * mm, "end": v(43.69, -47.77) * mm});
            skLineSegment(sketch, "E4250", {"start": v(43.69, -47.77) * mm, "end": v(43.78, -47.82) * mm});
            skLineSegment(sketch, "E4251", {"start": v(43.78, -47.82) * mm, "end": v(43.87, -47.88) * mm});
            skLineSegment(sketch, "E4252", {"start": v(43.87, -47.88) * mm, "end": v(43.97, -47.93) * mm});
            skLineSegment(sketch, "E4253", {"start": v(43.97, -47.93) * mm, "end": v(44.07, -47.99) * mm});
            skLineSegment(sketch, "E4254", {"start": v(44.07, -47.99) * mm, "end": v(44.16, -48.05) * mm});
            skLineSegment(sketch, "E4255", {"start": v(44.16, -48.05) * mm, "end": v(44.27, -48.1) * mm});
            skLineSegment(sketch, "E4256", {"start": v(44.27, -48.1) * mm, "end": v(44.37, -48.16) * mm});
            skLineSegment(sketch, "E4257", {"start": v(44.37, -48.16) * mm, "end": v(44.48, -48.22) * mm});
            skLineSegment(sketch, "E4258", {"start": v(44.48, -48.22) * mm, "end": v(44.59, -48.28) * mm});
            skLineSegment(sketch, "E4259", {"start": v(44.59, -48.28) * mm, "end": v(44.7, -48.34) * mm});
            skLineSegment(sketch, "E4260", {"start": v(44.7, -48.34) * mm, "end": v(44.8, -48.4) * mm});
            skLineSegment(sketch, "E4261", {"start": v(44.8, -48.4) * mm, "end": v(44.92, -48.46) * mm});
            skLineSegment(sketch, "E4262", {"start": v(44.92, -48.46) * mm, "end": v(45.04, -48.52) * mm});
            skLineSegment(sketch, "E4263", {"start": v(45.04, -48.52) * mm, "end": v(45.16, -48.58) * mm});
            skLineSegment(sketch, "E4264", {"start": v(45.16, -48.58) * mm, "end": v(45.28, -48.64) * mm});
            skLineSegment(sketch, "E4265", {"start": v(45.28, -48.64) * mm, "end": v(45.4, -48.7) * mm});
            skLineSegment(sketch, "E4266", {"start": v(45.4, -48.7) * mm, "end": v(45.53, -48.76) * mm});
            skLineSegment(sketch, "E4267", {"start": v(45.53, -48.76) * mm, "end": v(45.66, -48.82) * mm});
            skLineSegment(sketch, "E4268", {"start": v(45.66, -48.82) * mm, "end": v(45.79, -48.88) * mm});
            skLineSegment(sketch, "E4269", {"start": v(45.79, -48.88) * mm, "end": v(45.92, -48.94) * mm});
            skLineSegment(sketch, "E4270", {"start": v(45.92, -48.94) * mm, "end": v(46.06, -49) * mm});
            skLineSegment(sketch, "E4271", {"start": v(46.06, -49) * mm, "end": v(46.2, -49.07) * mm});
            skLineSegment(sketch, "E4272", {"start": v(46.2, -49.07) * mm, "end": v(46.33, -49.13) * mm});
            skLineSegment(sketch, "E4273", {"start": v(46.33, -49.13) * mm, "end": v(46.47, -49.2) * mm});
            skLineSegment(sketch, "E4274", {"start": v(46.47, -49.2) * mm, "end": v(46.62, -49.25) * mm});
            skLineSegment(sketch, "E4275", {"start": v(46.62, -49.25) * mm, "end": v(46.77, -49.31) * mm});
            skLineSegment(sketch, "E4276", {"start": v(46.77, -49.31) * mm, "end": v(46.91, -49.38) * mm});
            skLineSegment(sketch, "E4277", {"start": v(46.91, -49.38) * mm, "end": v(47.06, -49.44) * mm});
            skLineSegment(sketch, "E4278", {"start": v(47.06, -49.44) * mm, "end": v(47.18, -49.46) * mm});
            skLineSegment(sketch, "E4279", {"start": v(47.18, -49.46) * mm, "end": v(48.34, -48.32) * mm});
            skLineSegment(sketch, "E4280", {"start": v(48.34, -48.32) * mm, "end": v(48.33, -48.2) * mm});
            skLineSegment(sketch, "E4281", {"start": v(48.33, -48.2) * mm, "end": v(48.27, -48.05) * mm});
            skLineSegment(sketch, "E4282", {"start": v(48.27, -48.05) * mm, "end": v(48.2, -47.9) * mm});
            skLineSegment(sketch, "E4283", {"start": v(48.2, -47.9) * mm, "end": v(48.15, -47.75) * mm});
            skLineSegment(sketch, "E4284", {"start": v(48.15, -47.75) * mm, "end": v(48.1, -47.6) * mm});
            skLineSegment(sketch, "E4285", {"start": v(48.1, -47.6) * mm, "end": v(48.04, -47.47) * mm});
            skLineSegment(sketch, "E4286", {"start": v(48.04, -47.47) * mm, "end": v(47.98, -47.32) * mm});
            skLineSegment(sketch, "E4287", {"start": v(47.98, -47.32) * mm, "end": v(47.92, -47.19) * mm});
            skLineSegment(sketch, "E4288", {"start": v(47.92, -47.19) * mm, "end": v(47.86, -47.05) * mm});
            skLineSegment(sketch, "E4289", {"start": v(47.86, -47.05) * mm, "end": v(47.8, -46.92) * mm});
            skLineSegment(sketch, "E4290", {"start": v(47.8, -46.92) * mm, "end": v(47.74, -46.78) * mm});
            skLineSegment(sketch, "E4291", {"start": v(47.74, -46.78) * mm, "end": v(47.69, -46.65) * mm});
            skLineSegment(sketch, "E4292", {"start": v(47.69, -46.65) * mm, "end": v(47.63, -46.53) * mm});
            skLineSegment(sketch, "E4293", {"start": v(47.63, -46.53) * mm, "end": v(47.57, -46.4) * mm});
            skLineSegment(sketch, "E4294", {"start": v(47.57, -46.4) * mm, "end": v(47.51, -46.28) * mm});
            skLineSegment(sketch, "E4295", {"start": v(47.51, -46.28) * mm, "end": v(47.45, -46.16) * mm});
            skLineSegment(sketch, "E4296", {"start": v(47.45, -46.16) * mm, "end": v(47.4, -46.04) * mm});
            skLineSegment(sketch, "E4297", {"start": v(47.4, -46.04) * mm, "end": v(47.34, -45.92) * mm});
            skLineSegment(sketch, "E4298", {"start": v(47.34, -45.92) * mm, "end": v(47.28, -45.81) * mm});
            skLineSegment(sketch, "E4299", {"start": v(47.28, -45.81) * mm, "end": v(47.23, -45.7) * mm});
            skLineSegment(sketch, "E4300", {"start": v(47.23, -45.7) * mm, "end": v(47.17, -45.59) * mm});
            skLineSegment(sketch, "E4301", {"start": v(47.17, -45.59) * mm, "end": v(47.12, -45.48) * mm});
            skLineSegment(sketch, "E4302", {"start": v(47.12, -45.48) * mm, "end": v(47.06, -45.38) * mm});
            skLineSegment(sketch, "E4303", {"start": v(47.06, -45.38) * mm, "end": v(47, -45.27) * mm});
            skLineSegment(sketch, "E4304", {"start": v(47, -45.27) * mm, "end": v(46.95, -45.17) * mm});
            skLineSegment(sketch, "E4305", {"start": v(46.95, -45.17) * mm, "end": v(46.9, -45.07) * mm});
            skLineSegment(sketch, "E4306", {"start": v(46.9, -45.07) * mm, "end": v(46.84, -44.98) * mm});
            skLineSegment(sketch, "E4307", {"start": v(46.84, -44.98) * mm, "end": v(46.79, -44.88) * mm});
            skLineSegment(sketch, "E4308", {"start": v(46.79, -44.88) * mm, "end": v(46.73, -44.8) * mm});
            skLineSegment(sketch, "E4309", {"start": v(46.73, -44.8) * mm, "end": v(46.68, -44.7) * mm});
            skLineSegment(sketch, "E4310", {"start": v(46.68, -44.7) * mm, "end": v(46.63, -44.61) * mm});
            skLineSegment(sketch, "E4311", {"start": v(46.63, -44.61) * mm, "end": v(46.58, -44.53) * mm});
            skLineSegment(sketch, "E4312", {"start": v(46.58, -44.53) * mm, "end": v(46.53, -44.44) * mm});
            skLineSegment(sketch, "E4313", {"start": v(46.53, -44.44) * mm, "end": v(46.48, -44.36) * mm});
            skLineSegment(sketch, "E4314", {"start": v(46.48, -44.36) * mm, "end": v(46.43, -44.28) * mm});
            skLineSegment(sketch, "E4315", {"start": v(46.43, -44.28) * mm, "end": v(46.38, -44.2) * mm});
            skLineSegment(sketch, "E4316", {"start": v(46.38, -44.2) * mm, "end": v(46.33, -44.13) * mm});
            skLineSegment(sketch, "E4317", {"start": v(46.33, -44.13) * mm, "end": v(46.29, -44.06) * mm});
            skLineSegment(sketch, "E4318", {"start": v(46.29, -44.06) * mm, "end": v(46.24, -43.98) * mm});
            skLineSegment(sketch, "E4319", {"start": v(46.24, -43.98) * mm, "end": v(46.2, -43.92) * mm});
            skLineSegment(sketch, "E4320", {"start": v(46.2, -43.92) * mm, "end": v(46.27, -43.65) * mm});
            skLineSegment(sketch, "E4321", {"start": v(46.27, -43.65) * mm, "end": v(47.27, -42.56) * mm});
            skLineSegment(sketch, "E4322", {"start": v(47.27, -42.56) * mm, "end": v(47.53, -42.47) * mm});
            skLineSegment(sketch, "E4323", {"start": v(47.53, -42.47) * mm, "end": v(47.6, -42.5) * mm});
            skLineSegment(sketch, "E4324", {"start": v(47.6, -42.5) * mm, "end": v(47.75, -42.6) * mm});
            skLineSegment(sketch, "E4325", {"start": v(47.75, -42.6) * mm, "end": v(47.83, -42.63) * mm});
            skLineSegment(sketch, "E4326", {"start": v(47.83, -42.63) * mm, "end": v(47.91, -42.67) * mm});
            skLineSegment(sketch, "E4327", {"start": v(47.91, -42.67) * mm, "end": v(48, -42.72) * mm});
            skLineSegment(sketch, "E4328", {"start": v(48, -42.72) * mm, "end": v(48.17, -42.8) * mm});
            skLineSegment(sketch, "E4329", {"start": v(48.17, -42.8) * mm, "end": v(48.26, -42.85) * mm});
            skLineSegment(sketch, "E4330", {"start": v(48.26, -42.85) * mm, "end": v(48.35, -42.9) * mm});
            skLineSegment(sketch, "E4331", {"start": v(48.35, -42.9) * mm, "end": v(48.44, -42.94) * mm});
            skLineSegment(sketch, "E4332", {"start": v(48.44, -42.94) * mm, "end": v(48.54, -42.98) * mm});
            skLineSegment(sketch, "E4333", {"start": v(48.54, -42.98) * mm, "end": v(48.64, -43.03) * mm});
            skLineSegment(sketch, "E4334", {"start": v(48.64, -43.03) * mm, "end": v(48.74, -43.07) * mm});
            skLineSegment(sketch, "E4335", {"start": v(48.74, -43.07) * mm, "end": v(48.84, -43.12) * mm});
            skLineSegment(sketch, "E4336", {"start": v(48.84, -43.12) * mm, "end": v(48.95, -43.17) * mm});
            skLineSegment(sketch, "E4337", {"start": v(48.95, -43.17) * mm, "end": v(49.05, -43.21) * mm});
            skLineSegment(sketch, "E4338", {"start": v(49.05, -43.21) * mm, "end": v(49.16, -43.26) * mm});
            skLineSegment(sketch, "E4339", {"start": v(49.16, -43.26) * mm, "end": v(49.27, -43.3) * mm});
            skLineSegment(sketch, "E4340", {"start": v(49.27, -43.3) * mm, "end": v(49.39, -43.35) * mm});
            skLineSegment(sketch, "E4341", {"start": v(49.39, -43.35) * mm, "end": v(49.5, -43.4) * mm});
            skLineSegment(sketch, "E4342", {"start": v(49.5, -43.4) * mm, "end": v(49.62, -43.45) * mm});
            skLineSegment(sketch, "E4343", {"start": v(49.62, -43.45) * mm, "end": v(49.74, -43.5) * mm});
            skLineSegment(sketch, "E4344", {"start": v(49.74, -43.5) * mm, "end": v(49.86, -43.54) * mm});
            skLineSegment(sketch, "E4345", {"start": v(49.86, -43.54) * mm, "end": v(49.99, -43.6) * mm});
            skLineSegment(sketch, "E4346", {"start": v(49.99, -43.6) * mm, "end": v(50.12, -43.64) * mm});
            skLineSegment(sketch, "E4347", {"start": v(50.12, -43.64) * mm, "end": v(50.25, -43.69) * mm});
            skLineSegment(sketch, "E4348", {"start": v(50.25, -43.69) * mm, "end": v(50.38, -43.73) * mm});
            skLineSegment(sketch, "E4349", {"start": v(50.38, -43.73) * mm, "end": v(50.51, -43.78) * mm});
            skLineSegment(sketch, "E4350", {"start": v(50.51, -43.78) * mm, "end": v(50.65, -43.83) * mm});
            skLineSegment(sketch, "E4351", {"start": v(50.65, -43.83) * mm, "end": v(50.78, -43.88) * mm});
            skLineSegment(sketch, "E4352", {"start": v(50.78, -43.88) * mm, "end": v(50.93, -43.92) * mm});
            skLineSegment(sketch, "E4353", {"start": v(50.93, -43.92) * mm, "end": v(51.07, -43.97) * mm});
            skLineSegment(sketch, "E4354", {"start": v(51.07, -43.97) * mm, "end": v(51.21, -44.02) * mm});
            skLineSegment(sketch, "E4355", {"start": v(51.21, -44.02) * mm, "end": v(51.36, -44.06) * mm});
            skLineSegment(sketch, "E4356", {"start": v(51.36, -44.06) * mm, "end": v(51.51, -44.1) * mm});
            skLineSegment(sketch, "E4357", {"start": v(51.51, -44.1) * mm, "end": v(51.66, -44.16) * mm});
            skLineSegment(sketch, "E4358", {"start": v(51.66, -44.16) * mm, "end": v(51.82, -44.2) * mm});
            skLineSegment(sketch, "E4359", {"start": v(51.82, -44.2) * mm, "end": v(51.97, -44.25) * mm});
            skLineSegment(sketch, "E4360", {"start": v(51.97, -44.25) * mm, "end": v(52.09, -44.25) * mm});
            skLineSegment(sketch, "E4361", {"start": v(52.09, -44.25) * mm, "end": v(53.13, -43) * mm});
            skLineSegment(sketch, "E4362", {"start": v(53.13, -43) * mm, "end": v(53.1, -42.89) * mm});
            skLineSegment(sketch, "E4363", {"start": v(53.1, -42.89) * mm, "end": v(53.03, -42.74) * mm});
            skLineSegment(sketch, "E4364", {"start": v(53.03, -42.74) * mm, "end": v(52.95, -42.6) * mm});
            skLineSegment(sketch, "E4365", {"start": v(52.95, -42.6) * mm, "end": v(52.88, -42.46) * mm});
            skLineSegment(sketch, "E4366", {"start": v(52.88, -42.46) * mm, "end": v(52.8, -42.32) * mm});
            skLineSegment(sketch, "E4367", {"start": v(52.8, -42.32) * mm, "end": v(52.73, -42.18) * mm});
            skLineSegment(sketch, "E4368", {"start": v(52.73, -42.18) * mm, "end": v(52.66, -42.05) * mm});
            skLineSegment(sketch, "E4369", {"start": v(52.66, -42.05) * mm, "end": v(52.59, -41.92) * mm});
            skLineSegment(sketch, "E4370", {"start": v(52.59, -41.92) * mm, "end": v(52.52, -41.79) * mm});
            skLineSegment(sketch, "E4371", {"start": v(52.52, -41.79) * mm, "end": v(52.44, -41.66) * mm});
            skLineSegment(sketch, "E4372", {"start": v(52.44, -41.66) * mm, "end": v(52.37, -41.54) * mm});
            skLineSegment(sketch, "E4373", {"start": v(52.37, -41.54) * mm, "end": v(52.3, -41.41) * mm});
            skLineSegment(sketch, "E4374", {"start": v(52.3, -41.41) * mm, "end": v(52.23, -41.3) * mm});
            skLineSegment(sketch, "E4375", {"start": v(52.23, -41.3) * mm, "end": v(52.16, -41.17) * mm});
            skLineSegment(sketch, "E4376", {"start": v(52.16, -41.17) * mm, "end": v(52.09, -41.06) * mm});
            skLineSegment(sketch, "E4377", {"start": v(52.09, -41.06) * mm, "end": v(52.02, -40.94) * mm});
            skLineSegment(sketch, "E4378", {"start": v(52.02, -40.94) * mm, "end": v(51.95, -40.83) * mm});
            skLineSegment(sketch, "E4379", {"start": v(51.95, -40.83) * mm, "end": v(51.88, -40.72) * mm});
            skLineSegment(sketch, "E4380", {"start": v(51.88, -40.72) * mm, "end": v(51.81, -40.62) * mm});
            skLineSegment(sketch, "E4381", {"start": v(51.81, -40.62) * mm, "end": v(51.74, -40.51) * mm});
            skLineSegment(sketch, "E4382", {"start": v(51.74, -40.51) * mm, "end": v(51.68, -40.4) * mm});
            skLineSegment(sketch, "E4383", {"start": v(51.68, -40.4) * mm, "end": v(51.61, -40.3) * mm});
            skLineSegment(sketch, "E4384", {"start": v(51.61, -40.3) * mm, "end": v(51.54, -40.2) * mm});
            skLineSegment(sketch, "E4385", {"start": v(51.54, -40.2) * mm, "end": v(51.48, -40.11) * mm});
            skLineSegment(sketch, "E4386", {"start": v(51.48, -40.11) * mm, "end": v(51.41, -40.02) * mm});
            skLineSegment(sketch, "E4387", {"start": v(51.41, -40.02) * mm, "end": v(51.35, -39.92) * mm});
            skLineSegment(sketch, "E4388", {"start": v(51.35, -39.92) * mm, "end": v(51.29, -39.83) * mm});
            skLineSegment(sketch, "E4389", {"start": v(51.29, -39.83) * mm, "end": v(51.22, -39.75) * mm});
            skLineSegment(sketch, "E4390", {"start": v(51.22, -39.75) * mm, "end": v(51.16, -39.66) * mm});
            skLineSegment(sketch, "E4391", {"start": v(51.16, -39.66) * mm, "end": v(51.1, -39.58) * mm});
            skLineSegment(sketch, "E4392", {"start": v(51.1, -39.58) * mm, "end": v(51.04, -39.5) * mm});
            skLineSegment(sketch, "E4393", {"start": v(51.04, -39.5) * mm, "end": v(50.98, -39.41) * mm});
            skLineSegment(sketch, "E4394", {"start": v(50.98, -39.41) * mm, "end": v(50.92, -39.34) * mm});
            skLineSegment(sketch, "E4395", {"start": v(50.92, -39.34) * mm, "end": v(50.86, -39.26) * mm});
            skLineSegment(sketch, "E4396", {"start": v(50.86, -39.26) * mm, "end": v(50.8, -39.19) * mm});
            skLineSegment(sketch, "E4397", {"start": v(50.8, -39.19) * mm, "end": v(50.75, -39.11) * mm});
            skLineSegment(sketch, "E4398", {"start": v(50.75, -39.11) * mm, "end": v(50.7, -39.04) * mm});
            skLineSegment(sketch, "E4399", {"start": v(50.7, -39.04) * mm, "end": v(50.64, -38.98) * mm});
            skLineSegment(sketch, "E4400", {"start": v(50.64, -38.98) * mm, "end": v(50.58, -38.91) * mm});
            skLineSegment(sketch, "E4401", {"start": v(50.58, -38.91) * mm, "end": v(50.53, -38.85) * mm});
            skLineSegment(sketch, "E4402", {"start": v(50.53, -38.85) * mm, "end": v(50.58, -38.58) * mm});
            skLineSegment(sketch, "E4403", {"start": v(50.58, -38.58) * mm, "end": v(51.46, -37.39) * mm});
            skLineSegment(sketch, "E4404", {"start": v(51.46, -37.39) * mm, "end": v(51.7, -37.27) * mm});
            skLineSegment(sketch, "E4405", {"start": v(51.7, -37.27) * mm, "end": v(51.78, -37.3) * mm});
            skLineSegment(sketch, "E4406", {"start": v(51.78, -37.3) * mm, "end": v(51.86, -37.33) * mm});
            skLineSegment(sketch, "E4407", {"start": v(51.86, -37.33) * mm, "end": v(51.94, -37.37) * mm});
            skLineSegment(sketch, "E4408", {"start": v(51.94, -37.37) * mm, "end": v(52.02, -37.4) * mm});
            skLineSegment(sketch, "E4409", {"start": v(52.02, -37.4) * mm, "end": v(52.1, -37.43) * mm});
            skLineSegment(sketch, "E4410", {"start": v(52.1, -37.43) * mm, "end": v(52.2, -37.47) * mm});
            skLineSegment(sketch, "E4411", {"start": v(52.2, -37.47) * mm, "end": v(52.29, -37.5) * mm});
            skLineSegment(sketch, "E4412", {"start": v(52.29, -37.5) * mm, "end": v(52.38, -37.54) * mm});
            skLineSegment(sketch, "E4413", {"start": v(52.38, -37.54) * mm, "end": v(52.47, -37.57) * mm});
            skLineSegment(sketch, "E4414", {"start": v(52.47, -37.57) * mm, "end": v(52.57, -37.6) * mm});
            skLineSegment(sketch, "E4415", {"start": v(52.57, -37.6) * mm, "end": v(52.67, -37.64) * mm});
            skLineSegment(sketch, "E4416", {"start": v(52.67, -37.64) * mm, "end": v(52.77, -37.67) * mm});
            skLineSegment(sketch, "E4417", {"start": v(52.77, -37.67) * mm, "end": v(52.87, -37.7) * mm});
            skLineSegment(sketch, "E4418", {"start": v(52.87, -37.7) * mm, "end": v(52.97, -37.74) * mm});
            skLineSegment(sketch, "E4419", {"start": v(52.97, -37.74) * mm, "end": v(53.08, -37.78) * mm});
            skLineSegment(sketch, "E4420", {"start": v(53.08, -37.78) * mm, "end": v(53.19, -37.81) * mm});
            skLineSegment(sketch, "E4421", {"start": v(53.19, -37.81) * mm, "end": v(53.3, -37.85) * mm});
            skLineSegment(sketch, "E4422", {"start": v(53.3, -37.85) * mm, "end": v(53.41, -37.88) * mm});
            skLineSegment(sketch, "E4423", {"start": v(53.41, -37.88) * mm, "end": v(53.53, -37.92) * mm});
            skLineSegment(sketch, "E4424", {"start": v(53.53, -37.92) * mm, "end": v(53.65, -37.95) * mm});
            skLineSegment(sketch, "E4425", {"start": v(53.65, -37.95) * mm, "end": v(53.77, -37.99) * mm});
            skLineSegment(sketch, "E4426", {"start": v(53.77, -37.99) * mm, "end": v(53.9, -38.02) * mm});
            skLineSegment(sketch, "E4427", {"start": v(53.9, -38.02) * mm, "end": v(54.01, -38.06) * mm});
            skLineSegment(sketch, "E4428", {"start": v(54.01, -38.06) * mm, "end": v(54.27, -38.13) * mm});
            skLineSegment(sketch, "E4429", {"start": v(54.27, -38.13) * mm, "end": v(54.4, -38.16) * mm});
            skLineSegment(sketch, "E4430", {"start": v(54.4, -38.16) * mm, "end": v(54.54, -38.2) * mm});
            skLineSegment(sketch, "E4431", {"start": v(54.54, -38.2) * mm, "end": v(54.67, -38.23) * mm});
            skLineSegment(sketch, "E4432", {"start": v(54.67, -38.23) * mm, "end": v(54.8, -38.26) * mm});
            skLineSegment(sketch, "E4433", {"start": v(54.8, -38.26) * mm, "end": v(54.95, -38.3) * mm});
            skLineSegment(sketch, "E4434", {"start": v(54.95, -38.3) * mm, "end": v(55.1, -38.33) * mm});
            skLineSegment(sketch, "E4435", {"start": v(55.1, -38.33) * mm, "end": v(55.24, -38.36) * mm});
            skLineSegment(sketch, "E4436", {"start": v(55.24, -38.36) * mm, "end": v(55.38, -38.4) * mm});
            skLineSegment(sketch, "E4437", {"start": v(55.38, -38.4) * mm, "end": v(55.53, -38.42) * mm});
            skLineSegment(sketch, "E4438", {"start": v(55.53, -38.42) * mm, "end": v(55.69, -38.45) * mm});
            skLineSegment(sketch, "E4439", {"start": v(55.69, -38.45) * mm, "end": v(55.84, -38.48) * mm});
            skLineSegment(sketch, "E4440", {"start": v(55.84, -38.48) * mm, "end": v(56, -38.51) * mm});
            skLineSegment(sketch, "E4441", {"start": v(56, -38.51) * mm, "end": v(56.15, -38.54) * mm});
            skLineSegment(sketch, "E4442", {"start": v(56.15, -38.54) * mm, "end": v(56.31, -38.57) * mm});
            skLineSegment(sketch, "E4443", {"start": v(56.31, -38.57) * mm, "end": v(56.43, -38.57) * mm});
            skLineSegment(sketch, "E4444", {"start": v(56.43, -38.57) * mm, "end": v(57.33, -37.21) * mm});
            skLineSegment(sketch, "E4445", {"start": v(57.33, -37.21) * mm, "end": v(57.3, -37.1) * mm});
            skLineSegment(sketch, "E4446", {"start": v(57.3, -37.1) * mm, "end": v(57.2, -36.97) * mm});
            skLineSegment(sketch, "E4447", {"start": v(57.2, -36.97) * mm, "end": v(57.12, -36.83) * mm});
            skLineSegment(sketch, "E4448", {"start": v(57.12, -36.83) * mm, "end": v(57.03, -36.7) * mm});
            skLineSegment(sketch, "E4449", {"start": v(57.03, -36.7) * mm, "end": v(56.94, -36.57) * mm});
            skLineSegment(sketch, "E4450", {"start": v(56.94, -36.57) * mm, "end": v(56.85, -36.44) * mm});
            skLineSegment(sketch, "E4451", {"start": v(56.85, -36.44) * mm, "end": v(56.77, -36.32) * mm});
            skLineSegment(sketch, "E4452", {"start": v(56.77, -36.32) * mm, "end": v(56.68, -36.2) * mm});
            skLineSegment(sketch, "E4453", {"start": v(56.68, -36.2) * mm, "end": v(56.6, -36.07) * mm});
            skLineSegment(sketch, "E4454", {"start": v(56.6, -36.07) * mm, "end": v(56.51, -35.95) * mm});
            skLineSegment(sketch, "E4455", {"start": v(56.51, -35.95) * mm, "end": v(56.43, -35.83) * mm});
            skLineSegment(sketch, "E4456", {"start": v(56.43, -35.83) * mm, "end": v(56.34, -35.72) * mm});
            skLineSegment(sketch, "E4457", {"start": v(56.34, -35.72) * mm, "end": v(56.26, -35.6) * mm});
            skLineSegment(sketch, "E4458", {"start": v(56.26, -35.6) * mm, "end": v(56.18, -35.5) * mm});
            skLineSegment(sketch, "E4459", {"start": v(56.18, -35.5) * mm, "end": v(56.1, -35.39) * mm});
            skLineSegment(sketch, "E4460", {"start": v(56.1, -35.39) * mm, "end": v(56.01, -35.28) * mm});
            skLineSegment(sketch, "E4461", {"start": v(56.01, -35.28) * mm, "end": v(55.93, -35.18) * mm});
            skLineSegment(sketch, "E4462", {"start": v(55.93, -35.18) * mm, "end": v(55.85, -35.08) * mm});
            skLineSegment(sketch, "E4463", {"start": v(55.85, -35.08) * mm, "end": v(55.77, -34.98) * mm});
            skLineSegment(sketch, "E4464", {"start": v(55.77, -34.98) * mm, "end": v(55.62, -34.78) * mm});
            skLineSegment(sketch, "E4465", {"start": v(55.62, -34.78) * mm, "end": v(55.54, -34.7) * mm});
            skLineSegment(sketch, "E4466", {"start": v(55.54, -34.7) * mm, "end": v(55.46, -34.6) * mm});
            skLineSegment(sketch, "E4467", {"start": v(55.46, -34.6) * mm, "end": v(55.4, -34.51) * mm});
            skLineSegment(sketch, "E4468", {"start": v(55.4, -34.51) * mm, "end": v(55.31, -34.42) * mm});
            skLineSegment(sketch, "E4469", {"start": v(55.31, -34.42) * mm, "end": v(55.17, -34.26) * mm});
            skLineSegment(sketch, "E4470", {"start": v(55.17, -34.26) * mm, "end": v(55.1, -34.17) * mm});
            skLineSegment(sketch, "E4471", {"start": v(55.1, -34.17) * mm, "end": v(55.03, -34.1) * mm});
            skLineSegment(sketch, "E4472", {"start": v(55.03, -34.1) * mm, "end": v(54.96, -34.02) * mm});
            skLineSegment(sketch, "E4473", {"start": v(54.96, -34.02) * mm, "end": v(54.89, -33.94) * mm});
            skLineSegment(sketch, "E4474", {"start": v(54.89, -33.94) * mm, "end": v(54.82, -33.87) * mm});
            skLineSegment(sketch, "E4475", {"start": v(54.82, -33.87) * mm, "end": v(54.75, -33.8) * mm});
            skLineSegment(sketch, "E4476", {"start": v(54.75, -33.8) * mm, "end": v(54.69, -33.73) * mm});
            skLineSegment(sketch, "E4477", {"start": v(54.69, -33.73) * mm, "end": v(54.62, -33.66) * mm});
            skLineSegment(sketch, "E4478", {"start": v(54.62, -33.66) * mm, "end": v(54.56, -33.6) * mm});
            skLineSegment(sketch, "E4479", {"start": v(54.56, -33.6) * mm, "end": v(54.5, -33.53) * mm});
            skLineSegment(sketch, "E4480", {"start": v(54.5, -33.53) * mm, "end": v(54.37, -33.4) * mm});
            skLineSegment(sketch, "E4481", {"start": v(54.37, -33.4) * mm, "end": v(54.31, -33.35) * mm});
            skLineSegment(sketch, "E4482", {"start": v(54.31, -33.35) * mm, "end": v(54.33, -33.08) * mm});
            skLineSegment(sketch, "E4483", {"start": v(54.33, -33.08) * mm, "end": v(55.09, -31.8) * mm});
            skLineSegment(sketch, "E4484", {"start": v(55.09, -31.8) * mm, "end": v(55.32, -31.66) * mm});
            skLineSegment(sketch, "E4485", {"start": v(55.32, -31.66) * mm, "end": v(55.4, -31.68) * mm});
            skLineSegment(sketch, "E4486", {"start": v(55.4, -31.68) * mm, "end": v(55.48, -31.7) * mm});
            skLineSegment(sketch, "E4487", {"start": v(55.48, -31.7) * mm, "end": v(55.56, -31.73) * mm});
            skLineSegment(sketch, "E4488", {"start": v(55.56, -31.73) * mm, "end": v(55.65, -31.76) * mm});
            skLineSegment(sketch, "E4489", {"start": v(55.65, -31.76) * mm, "end": v(55.74, -31.78) * mm});
            skLineSegment(sketch, "E4490", {"start": v(55.74, -31.78) * mm, "end": v(55.83, -31.8) * mm});
            skLineSegment(sketch, "E4491", {"start": v(55.83, -31.8) * mm, "end": v(55.92, -31.83) * mm});
            skLineSegment(sketch, "E4492", {"start": v(55.92, -31.83) * mm, "end": v(56.01, -31.85) * mm});
            skLineSegment(sketch, "E4493", {"start": v(56.01, -31.85) * mm, "end": v(56.11, -31.88) * mm});
            skLineSegment(sketch, "E4494", {"start": v(56.11, -31.88) * mm, "end": v(56.21, -31.9) * mm});
            skLineSegment(sketch, "E4495", {"start": v(56.21, -31.9) * mm, "end": v(56.31, -31.93) * mm});
            skLineSegment(sketch, "E4496", {"start": v(56.31, -31.93) * mm, "end": v(56.42, -31.95) * mm});
            skLineSegment(sketch, "E4497", {"start": v(56.42, -31.95) * mm, "end": v(56.52, -31.98) * mm});
            skLineSegment(sketch, "E4498", {"start": v(56.52, -31.98) * mm, "end": v(56.74, -32.02) * mm});
            skLineSegment(sketch, "E4499", {"start": v(56.74, -32.02) * mm, "end": v(56.85, -32.05) * mm});
            skLineSegment(sketch, "E4500", {"start": v(56.85, -32.05) * mm, "end": v(56.97, -32.07) * mm});
            skLineSegment(sketch, "E4501", {"start": v(56.97, -32.07) * mm, "end": v(57.08, -32.1) * mm});
            skLineSegment(sketch, "E4502", {"start": v(57.08, -32.1) * mm, "end": v(57.2, -32.12) * mm});
            skLineSegment(sketch, "E4503", {"start": v(57.2, -32.12) * mm, "end": v(57.32, -32.14) * mm});
            skLineSegment(sketch, "E4504", {"start": v(57.32, -32.14) * mm, "end": v(57.44, -32.16) * mm});
            skLineSegment(sketch, "E4505", {"start": v(57.44, -32.16) * mm, "end": v(57.57, -32.18) * mm});
            skLineSegment(sketch, "E4506", {"start": v(57.57, -32.18) * mm, "end": v(57.7, -32.2) * mm});
            skLineSegment(sketch, "E4507", {"start": v(57.7, -32.2) * mm, "end": v(57.83, -32.22) * mm});
            skLineSegment(sketch, "E4508", {"start": v(57.83, -32.22) * mm, "end": v(57.96, -32.24) * mm});
            skLineSegment(sketch, "E4509", {"start": v(57.96, -32.24) * mm, "end": v(58.1, -32.27) * mm});
            skLineSegment(sketch, "E4510", {"start": v(58.1, -32.27) * mm, "end": v(58.23, -32.28) * mm});
            skLineSegment(sketch, "E4511", {"start": v(58.23, -32.28) * mm, "end": v(58.37, -32.3) * mm});
            skLineSegment(sketch, "E4512", {"start": v(58.37, -32.3) * mm, "end": v(58.5, -32.32) * mm});
            skLineSegment(sketch, "E4513", {"start": v(58.5, -32.32) * mm, "end": v(58.65, -32.34) * mm});
            skLineSegment(sketch, "E4514", {"start": v(58.65, -32.34) * mm, "end": v(58.8, -32.36) * mm});
            skLineSegment(sketch, "E4515", {"start": v(58.8, -32.36) * mm, "end": v(58.95, -32.37) * mm});
            skLineSegment(sketch, "E4516", {"start": v(58.95, -32.37) * mm, "end": v(59.1, -32.4) * mm});
            skLineSegment(sketch, "E4517", {"start": v(59.1, -32.4) * mm, "end": v(59.25, -32.4) * mm});
            skLineSegment(sketch, "E4518", {"start": v(59.25, -32.4) * mm, "end": v(59.4, -32.42) * mm});
            skLineSegment(sketch, "E4519", {"start": v(59.4, -32.42) * mm, "end": v(59.56, -32.43) * mm});
            skLineSegment(sketch, "E4520", {"start": v(59.56, -32.43) * mm, "end": v(59.71, -32.45) * mm});
            skLineSegment(sketch, "E4521", {"start": v(59.71, -32.45) * mm, "end": v(59.88, -32.46) * mm});
            skLineSegment(sketch, "E4522", {"start": v(59.88, -32.46) * mm, "end": v(60.04, -32.47) * mm});
            skLineSegment(sketch, "E4523", {"start": v(60.04, -32.47) * mm, "end": v(60.15, -32.46) * mm});
            skLineSegment(sketch, "E4524", {"start": v(60.15, -32.46) * mm, "end": v(60.9, -31.02) * mm});
            skLineSegment(sketch, "E4525", {"start": v(60.9, -31.02) * mm, "end": v(60.86, -30.91) * mm});
            skLineSegment(sketch, "E4526", {"start": v(60.86, -30.91) * mm, "end": v(60.76, -30.78) * mm});
            skLineSegment(sketch, "E4527", {"start": v(60.76, -30.78) * mm, "end": v(60.65, -30.66) * mm});
            skLineSegment(sketch, "E4528", {"start": v(60.65, -30.66) * mm, "end": v(60.55, -30.54) * mm});
            skLineSegment(sketch, "E4529", {"start": v(60.55, -30.54) * mm, "end": v(60.45, -30.42) * mm});
            skLineSegment(sketch, "E4530", {"start": v(60.45, -30.42) * mm, "end": v(60.35, -30.3) * mm});
            skLineSegment(sketch, "E4531", {"start": v(60.35, -30.3) * mm, "end": v(60.25, -30.18) * mm});
            skLineSegment(sketch, "E4532", {"start": v(60.25, -30.18) * mm, "end": v(60.15, -30.07) * mm});
            skLineSegment(sketch, "E4533", {"start": v(60.15, -30.07) * mm, "end": v(60.06, -29.96) * mm});
            skLineSegment(sketch, "E4534", {"start": v(60.06, -29.96) * mm, "end": v(59.96, -29.85) * mm});
            skLineSegment(sketch, "E4535", {"start": v(59.96, -29.85) * mm, "end": v(59.86, -29.74) * mm});
            skLineSegment(sketch, "E4536", {"start": v(59.86, -29.74) * mm, "end": v(59.77, -29.63) * mm});
            skLineSegment(sketch, "E4537", {"start": v(59.77, -29.63) * mm, "end": v(59.67, -29.53) * mm});
            skLineSegment(sketch, "E4538", {"start": v(59.67, -29.53) * mm, "end": v(59.58, -29.43) * mm});
            skLineSegment(sketch, "E4539", {"start": v(59.58, -29.43) * mm, "end": v(59.49, -29.33) * mm});
            skLineSegment(sketch, "E4540", {"start": v(59.49, -29.33) * mm, "end": v(59.4, -29.24) * mm});
            skLineSegment(sketch, "E4541", {"start": v(59.4, -29.24) * mm, "end": v(59.3, -29.14) * mm});
            skLineSegment(sketch, "E4542", {"start": v(59.3, -29.14) * mm, "end": v(59.21, -29.05) * mm});
            skLineSegment(sketch, "E4543", {"start": v(59.21, -29.05) * mm, "end": v(59.12, -28.96) * mm});
            skLineSegment(sketch, "E4544", {"start": v(59.12, -28.96) * mm, "end": v(59.04, -28.87) * mm});
            skLineSegment(sketch, "E4545", {"start": v(59.04, -28.87) * mm, "end": v(58.95, -28.78) * mm});
            skLineSegment(sketch, "E4546", {"start": v(58.95, -28.78) * mm, "end": v(58.86, -28.7) * mm});
            skLineSegment(sketch, "E4547", {"start": v(58.86, -28.7) * mm, "end": v(58.78, -28.61) * mm});
            skLineSegment(sketch, "E4548", {"start": v(58.78, -28.61) * mm, "end": v(58.7, -28.53) * mm});
            skLineSegment(sketch, "E4549", {"start": v(58.7, -28.53) * mm, "end": v(58.61, -28.45) * mm});
            skLineSegment(sketch, "E4550", {"start": v(58.61, -28.45) * mm, "end": v(58.53, -28.38) * mm});
            skLineSegment(sketch, "E4551", {"start": v(58.53, -28.38) * mm, "end": v(58.45, -28.3) * mm});
            skLineSegment(sketch, "E4552", {"start": v(58.45, -28.3) * mm, "end": v(58.37, -28.23) * mm});
            skLineSegment(sketch, "E4553", {"start": v(58.37, -28.23) * mm, "end": v(58.29, -28.16) * mm});
            skLineSegment(sketch, "E4554", {"start": v(58.29, -28.16) * mm, "end": v(58.21, -28.09) * mm});
            skLineSegment(sketch, "E4555", {"start": v(58.21, -28.09) * mm, "end": v(58.14, -28.02) * mm});
            skLineSegment(sketch, "E4556", {"start": v(58.14, -28.02) * mm, "end": v(58.06, -27.95) * mm});
            skLineSegment(sketch, "E4557", {"start": v(58.06, -27.95) * mm, "end": v(57.98, -27.9) * mm});
            skLineSegment(sketch, "E4558", {"start": v(57.98, -27.9) * mm, "end": v(57.91, -27.83) * mm});
            skLineSegment(sketch, "E4559", {"start": v(57.91, -27.83) * mm, "end": v(57.84, -27.77) * mm});
            skLineSegment(sketch, "E4560", {"start": v(57.84, -27.77) * mm, "end": v(57.77, -27.7) * mm});
            skLineSegment(sketch, "E4561", {"start": v(57.77, -27.7) * mm, "end": v(57.7, -27.65) * mm});
            skLineSegment(sketch, "E4562", {"start": v(57.7, -27.65) * mm, "end": v(57.63, -27.6) * mm});
            skLineSegment(sketch, "E4563", {"start": v(57.63, -27.6) * mm, "end": v(57.57, -27.54) * mm});
            skLineSegment(sketch, "E4564", {"start": v(57.57, -27.54) * mm, "end": v(57.5, -27.5) * mm});
            skLineSegment(sketch, "E4565", {"start": v(57.5, -27.5) * mm, "end": v(57.5, -27.22) * mm});
            skLineSegment(sketch, "E4566", {"start": v(57.5, -27.22) * mm, "end": v(58.11, -25.87) * mm});
            skLineSegment(sketch, "E4567", {"start": v(58.11, -25.87) * mm, "end": v(58.32, -25.7) * mm});
            skLineSegment(sketch, "E4568", {"start": v(58.32, -25.7) * mm, "end": v(58.4, -25.72) * mm});
            skLineSegment(sketch, "E4569", {"start": v(58.4, -25.72) * mm, "end": v(58.49, -25.73) * mm});
            skLineSegment(sketch, "E4570", {"start": v(58.49, -25.73) * mm, "end": v(58.57, -25.75) * mm});
            skLineSegment(sketch, "E4571", {"start": v(58.57, -25.75) * mm, "end": v(58.66, -25.77) * mm});
            skLineSegment(sketch, "E4572", {"start": v(58.66, -25.77) * mm, "end": v(58.75, -25.78) * mm});
            skLineSegment(sketch, "E4573", {"start": v(58.75, -25.78) * mm, "end": v(58.85, -25.8) * mm});
            skLineSegment(sketch, "E4574", {"start": v(58.85, -25.8) * mm, "end": v(58.94, -25.81) * mm});
            skLineSegment(sketch, "E4575", {"start": v(58.94, -25.81) * mm, "end": v(59.04, -25.82) * mm});
            skLineSegment(sketch, "E4576", {"start": v(59.04, -25.82) * mm, "end": v(59.14, -25.84) * mm});
            skLineSegment(sketch, "E4577", {"start": v(59.14, -25.84) * mm, "end": v(59.24, -25.85) * mm});
            skLineSegment(sketch, "E4578", {"start": v(59.24, -25.85) * mm, "end": v(59.34, -25.87) * mm});
            skLineSegment(sketch, "E4579", {"start": v(59.34, -25.87) * mm, "end": v(59.45, -25.88) * mm});
            skLineSegment(sketch, "E4580", {"start": v(59.45, -25.88) * mm, "end": v(59.55, -25.9) * mm});
            skLineSegment(sketch, "E4581", {"start": v(59.55, -25.9) * mm, "end": v(59.66, -25.9) * mm});
            skLineSegment(sketch, "E4582", {"start": v(59.66, -25.9) * mm, "end": v(59.77, -25.92) * mm});
            skLineSegment(sketch, "E4583", {"start": v(59.77, -25.92) * mm, "end": v(59.89, -25.93) * mm});
            skLineSegment(sketch, "E4584", {"start": v(59.89, -25.93) * mm, "end": v(60, -25.94) * mm});
            skLineSegment(sketch, "E4585", {"start": v(60, -25.94) * mm, "end": v(60.12, -25.95) * mm});
            skLineSegment(sketch, "E4586", {"start": v(60.12, -25.95) * mm, "end": v(60.24, -25.96) * mm});
            skLineSegment(sketch, "E4587", {"start": v(60.24, -25.96) * mm, "end": v(60.37, -25.97) * mm});
            skLineSegment(sketch, "E4588", {"start": v(60.37, -25.97) * mm, "end": v(60.5, -25.98) * mm});
            skLineSegment(sketch, "E4589", {"start": v(60.5, -25.98) * mm, "end": v(60.62, -25.99) * mm});
            skLineSegment(sketch, "E4590", {"start": v(60.62, -25.99) * mm, "end": v(60.75, -26) * mm});
            skLineSegment(sketch, "E4591", {"start": v(60.75, -26) * mm, "end": v(60.88, -26) * mm});
            skLineSegment(sketch, "E4592", {"start": v(60.88, -26) * mm, "end": v(61.01, -26.01) * mm});
            skLineSegment(sketch, "E4593", {"start": v(61.01, -26.01) * mm, "end": v(61.15, -26.02) * mm});
            skLineSegment(sketch, "E4594", {"start": v(61.15, -26.02) * mm, "end": v(61.29, -26.02) * mm});
            skLineSegment(sketch, "E4595", {"start": v(61.29, -26.02) * mm, "end": v(61.43, -26.03) * mm});
            skLineSegment(sketch, "E4596", {"start": v(61.43, -26.03) * mm, "end": v(61.57, -26.03) * mm});
            skLineSegment(sketch, "E4597", {"start": v(61.57, -26.03) * mm, "end": v(61.71, -26.03) * mm});
            skLineSegment(sketch, "E4598", {"start": v(61.71, -26.03) * mm, "end": v(61.86, -26.03) * mm});
            skLineSegment(sketch, "E4599", {"start": v(61.86, -26.03) * mm, "end": v(62, -26.04) * mm});
            skLineSegment(sketch, "E4600", {"start": v(62, -26.04) * mm, "end": v(62.16, -26.04) * mm});
            skLineSegment(sketch, "E4601", {"start": v(62.16, -26.04) * mm, "end": v(62.3, -26.04) * mm});
            skLineSegment(sketch, "E4602", {"start": v(62.3, -26.04) * mm, "end": v(62.46, -26.03) * mm});
            skLineSegment(sketch, "E4603", {"start": v(62.46, -26.03) * mm, "end": v(62.62, -26.03) * mm});
            skLineSegment(sketch, "E4604", {"start": v(62.62, -26.03) * mm, "end": v(62.78, -26.03) * mm});
            skLineSegment(sketch, "E4605", {"start": v(62.78, -26.03) * mm, "end": v(62.94, -26.02) * mm});
            skLineSegment(sketch, "E4606", {"start": v(62.94, -26.02) * mm, "end": v(63.1, -26.02) * mm});
            skLineSegment(sketch, "E4607", {"start": v(63.1, -26.02) * mm, "end": v(63.22, -26) * mm});
            skLineSegment(sketch, "E4608", {"start": v(63.22, -26) * mm, "end": v(63.82, -24.48) * mm});
            skLineSegment(sketch, "E4609", {"start": v(63.82, -24.48) * mm, "end": v(63.76, -24.38) * mm});
            skLineSegment(sketch, "E4610", {"start": v(63.76, -24.38) * mm, "end": v(63.64, -24.26) * mm});
            skLineSegment(sketch, "E4611", {"start": v(63.64, -24.26) * mm, "end": v(63.52, -24.15) * mm});
            skLineSegment(sketch, "E4612", {"start": v(63.52, -24.15) * mm, "end": v(63.41, -24.04) * mm});
            skLineSegment(sketch, "E4613", {"start": v(63.41, -24.04) * mm, "end": v(63.3, -23.93) * mm});
            skLineSegment(sketch, "E4614", {"start": v(63.3, -23.93) * mm, "end": v(63.19, -23.82) * mm});
            skLineSegment(sketch, "E4615", {"start": v(63.19, -23.82) * mm, "end": v(63.08, -23.72) * mm});
            skLineSegment(sketch, "E4616", {"start": v(63.08, -23.72) * mm, "end": v(62.97, -23.62) * mm});
            skLineSegment(sketch, "E4617", {"start": v(62.97, -23.62) * mm, "end": v(62.86, -23.51) * mm});
            skLineSegment(sketch, "E4618", {"start": v(62.86, -23.51) * mm, "end": v(62.64, -23.32) * mm});
            skLineSegment(sketch, "E4619", {"start": v(62.64, -23.32) * mm, "end": v(62.54, -23.23) * mm});
            skLineSegment(sketch, "E4620", {"start": v(62.54, -23.23) * mm, "end": v(62.43, -23.13) * mm});
            skLineSegment(sketch, "E4621", {"start": v(62.43, -23.13) * mm, "end": v(62.23, -22.95) * mm});
            skLineSegment(sketch, "E4622", {"start": v(62.23, -22.95) * mm, "end": v(62.13, -22.87) * mm});
            skLineSegment(sketch, "E4623", {"start": v(62.13, -22.87) * mm, "end": v(62.03, -22.78) * mm});
            skLineSegment(sketch, "E4624", {"start": v(62.03, -22.78) * mm, "end": v(61.93, -22.7) * mm});
            skLineSegment(sketch, "E4625", {"start": v(61.93, -22.7) * mm, "end": v(61.83, -22.62) * mm});
            skLineSegment(sketch, "E4626", {"start": v(61.83, -22.62) * mm, "end": v(61.73, -22.54) * mm});
            skLineSegment(sketch, "E4627", {"start": v(61.73, -22.54) * mm, "end": v(61.63, -22.46) * mm});
            skLineSegment(sketch, "E4628", {"start": v(61.63, -22.46) * mm, "end": v(61.45, -22.31) * mm});
            skLineSegment(sketch, "E4629", {"start": v(61.45, -22.31) * mm, "end": v(61.35, -22.24) * mm});
            skLineSegment(sketch, "E4630", {"start": v(61.35, -22.24) * mm, "end": v(61.26, -22.17) * mm});
            skLineSegment(sketch, "E4631", {"start": v(61.26, -22.17) * mm, "end": v(61.17, -22.1) * mm});
            skLineSegment(sketch, "E4632", {"start": v(61.17, -22.1) * mm, "end": v(61.09, -22.04) * mm});
            skLineSegment(sketch, "E4633", {"start": v(61.09, -22.04) * mm, "end": v(60.91, -21.9) * mm});
            skLineSegment(sketch, "E4634", {"start": v(60.91, -21.9) * mm, "end": v(60.83, -21.85) * mm});
            skLineSegment(sketch, "E4635", {"start": v(60.83, -21.85) * mm, "end": v(60.75, -21.79) * mm});
            skLineSegment(sketch, "E4636", {"start": v(60.75, -21.79) * mm, "end": v(60.66, -21.73) * mm});
            skLineSegment(sketch, "E4637", {"start": v(60.66, -21.73) * mm, "end": v(60.58, -21.68) * mm});
            skLineSegment(sketch, "E4638", {"start": v(60.58, -21.68) * mm, "end": v(60.5, -21.62) * mm});
            skLineSegment(sketch, "E4639", {"start": v(60.5, -21.62) * mm, "end": v(60.43, -21.57) * mm});
            skLineSegment(sketch, "E4640", {"start": v(60.43, -21.57) * mm, "end": v(60.35, -21.52) * mm});
            skLineSegment(sketch, "E4641", {"start": v(60.35, -21.52) * mm, "end": v(60.28, -21.47) * mm});
            skLineSegment(sketch, "E4642", {"start": v(60.28, -21.47) * mm, "end": v(60.2, -21.42) * mm});
            skLineSegment(sketch, "E4643", {"start": v(60.2, -21.42) * mm, "end": v(60.13, -21.37) * mm});
            skLineSegment(sketch, "E4644", {"start": v(60.13, -21.37) * mm, "end": v(60.06, -21.33) * mm});
            skLineSegment(sketch, "E4645", {"start": v(60.06, -21.33) * mm, "end": v(60.02, -21.06) * mm});
            skLineSegment(sketch, "E4646", {"start": v(60.02, -21.06) * mm, "end": v(60.5, -19.66) * mm});
            skLineSegment(sketch, "E4647", {"start": v(60.5, -19.66) * mm, "end": v(60.7, -19.47) * mm});
            skLineSegment(sketch, "E4648", {"start": v(60.7, -19.47) * mm, "end": v(60.77, -19.47) * mm});
            skLineSegment(sketch, "E4649", {"start": v(60.77, -19.47) * mm, "end": v(60.86, -19.48) * mm});
            skLineSegment(sketch, "E4650", {"start": v(60.86, -19.48) * mm, "end": v(60.95, -19.49) * mm});
            skLineSegment(sketch, "E4651", {"start": v(60.95, -19.49) * mm, "end": v(61.03, -19.5) * mm});
            skLineSegment(sketch, "E4652", {"start": v(61.03, -19.5) * mm, "end": v(61.22, -19.5) * mm});
            skLineSegment(sketch, "E4653", {"start": v(61.22, -19.5) * mm, "end": v(61.32, -19.5) * mm});
            skLineSegment(sketch, "E4654", {"start": v(61.32, -19.5) * mm, "end": v(61.41, -19.51) * mm});
            skLineSegment(sketch, "E4655", {"start": v(61.41, -19.51) * mm, "end": v(61.51, -19.52) * mm});
            skLineSegment(sketch, "E4656", {"start": v(61.51, -19.52) * mm, "end": v(61.61, -19.52) * mm});
            skLineSegment(sketch, "E4657", {"start": v(61.61, -19.52) * mm, "end": v(61.72, -19.52) * mm});
            skLineSegment(sketch, "E4658", {"start": v(61.72, -19.52) * mm, "end": v(61.83, -19.52) * mm});
            skLineSegment(sketch, "E4659", {"start": v(61.83, -19.52) * mm, "end": v(61.93, -19.53) * mm});
            skLineSegment(sketch, "E4660", {"start": v(61.93, -19.53) * mm, "end": v(62.04, -19.53) * mm});
            skLineSegment(sketch, "E4661", {"start": v(62.04, -19.53) * mm, "end": v(62.27, -19.53) * mm});
            skLineSegment(sketch, "E4662", {"start": v(62.27, -19.53) * mm, "end": v(62.39, -19.53) * mm});
            skLineSegment(sketch, "E4663", {"start": v(62.39, -19.53) * mm, "end": v(62.5, -19.52) * mm});
            skLineSegment(sketch, "E4664", {"start": v(62.5, -19.52) * mm, "end": v(62.63, -19.52) * mm});
            skLineSegment(sketch, "E4665", {"start": v(62.63, -19.52) * mm, "end": v(62.75, -19.52) * mm});
            skLineSegment(sketch, "E4666", {"start": v(62.75, -19.52) * mm, "end": v(62.88, -19.51) * mm});
            skLineSegment(sketch, "E4667", {"start": v(62.88, -19.51) * mm, "end": v(63.13, -19.5) * mm});
            skLineSegment(sketch, "E4668", {"start": v(63.13, -19.5) * mm, "end": v(63.26, -19.5) * mm});
            skLineSegment(sketch, "E4669", {"start": v(63.26, -19.5) * mm, "end": v(63.4, -19.49) * mm});
            skLineSegment(sketch, "E4670", {"start": v(63.4, -19.49) * mm, "end": v(63.67, -19.47) * mm});
            skLineSegment(sketch, "E4671", {"start": v(63.67, -19.47) * mm, "end": v(63.95, -19.45) * mm});
            skLineSegment(sketch, "E4672", {"start": v(63.95, -19.45) * mm, "end": v(64.24, -19.43) * mm});
            skLineSegment(sketch, "E4673", {"start": v(64.24, -19.43) * mm, "end": v(64.39, -19.41) * mm});
            skLineSegment(sketch, "E4674", {"start": v(64.39, -19.41) * mm, "end": v(64.54, -19.4) * mm});
            skLineSegment(sketch, "E4675", {"start": v(64.54, -19.4) * mm, "end": v(64.69, -19.38) * mm});
            skLineSegment(sketch, "E4676", {"start": v(64.69, -19.38) * mm, "end": v(64.84, -19.36) * mm});
            skLineSegment(sketch, "E4677", {"start": v(64.84, -19.36) * mm, "end": v(65, -19.34) * mm});
            skLineSegment(sketch, "E4678", {"start": v(65, -19.34) * mm, "end": v(65.16, -19.32) * mm});
            skLineSegment(sketch, "E4679", {"start": v(65.16, -19.32) * mm, "end": v(65.32, -19.3) * mm});
            skLineSegment(sketch, "E4680", {"start": v(65.32, -19.3) * mm, "end": v(65.48, -19.28) * mm});
            skLineSegment(sketch, "E4681", {"start": v(65.48, -19.28) * mm, "end": v(65.59, -19.24) * mm});
            skLineSegment(sketch, "E4682", {"start": v(65.59, -19.24) * mm, "end": v(66.03, -17.67) * mm});
            skLineSegment(sketch, "E4683", {"start": v(66.03, -17.67) * mm, "end": v(65.95, -17.58) * mm});
            skLineSegment(sketch, "E4684", {"start": v(65.95, -17.58) * mm, "end": v(65.7, -17.38) * mm});
            skLineSegment(sketch, "E4685", {"start": v(65.7, -17.38) * mm, "end": v(65.45, -17.18) * mm});
            skLineSegment(sketch, "E4686", {"start": v(65.45, -17.18) * mm, "end": v(65.21, -17) * mm});
            skLineSegment(sketch, "E4687", {"start": v(65.21, -17) * mm, "end": v(65.1, -16.9) * mm});
            skLineSegment(sketch, "E4688", {"start": v(65.1, -16.9) * mm, "end": v(64.97, -16.82) * mm});
            skLineSegment(sketch, "E4689", {"start": v(64.97, -16.82) * mm, "end": v(64.85, -16.73) * mm});
            skLineSegment(sketch, "E4690", {"start": v(64.85, -16.73) * mm, "end": v(64.74, -16.64) * mm});
            skLineSegment(sketch, "E4691", {"start": v(64.74, -16.64) * mm, "end": v(64.62, -16.56) * mm});
            skLineSegment(sketch, "E4692", {"start": v(64.62, -16.56) * mm, "end": v(64.5, -16.48) * mm});
            skLineSegment(sketch, "E4693", {"start": v(64.5, -16.48) * mm, "end": v(64.4, -16.4) * mm});
            skLineSegment(sketch, "E4694", {"start": v(64.4, -16.4) * mm, "end": v(64.29, -16.32) * mm});
            skLineSegment(sketch, "E4695", {"start": v(64.29, -16.32) * mm, "end": v(64.18, -16.25) * mm});
            skLineSegment(sketch, "E4696", {"start": v(64.18, -16.25) * mm, "end": v(64.07, -16.17) * mm});
            skLineSegment(sketch, "E4697", {"start": v(64.07, -16.17) * mm, "end": v(63.96, -16.1) * mm});
            skLineSegment(sketch, "E4698", {"start": v(63.96, -16.1) * mm, "end": v(63.85, -16.03) * mm});
            skLineSegment(sketch, "E4699", {"start": v(63.85, -16.03) * mm, "end": v(63.75, -15.96) * mm});
            skLineSegment(sketch, "E4700", {"start": v(63.75, -15.96) * mm, "end": v(63.64, -15.9) * mm});
            skLineSegment(sketch, "E4701", {"start": v(63.64, -15.9) * mm, "end": v(63.54, -15.83) * mm});
            skLineSegment(sketch, "E4702", {"start": v(63.54, -15.83) * mm, "end": v(63.44, -15.77) * mm});
            skLineSegment(sketch, "E4703", {"start": v(63.44, -15.77) * mm, "end": v(63.34, -15.7) * mm});
            skLineSegment(sketch, "E4704", {"start": v(63.34, -15.7) * mm, "end": v(63.25, -15.65) * mm});
            skLineSegment(sketch, "E4705", {"start": v(63.25, -15.65) * mm, "end": v(63.15, -15.59) * mm});
            skLineSegment(sketch, "E4706", {"start": v(63.15, -15.59) * mm, "end": v(63.05, -15.53) * mm});
            skLineSegment(sketch, "E4707", {"start": v(63.05, -15.53) * mm, "end": v(62.96, -15.48) * mm});
            skLineSegment(sketch, "E4708", {"start": v(62.96, -15.48) * mm, "end": v(62.87, -15.42) * mm});
            skLineSegment(sketch, "E4709", {"start": v(62.87, -15.42) * mm, "end": v(62.78, -15.37) * mm});
            skLineSegment(sketch, "E4710", {"start": v(62.78, -15.37) * mm, "end": v(62.69, -15.32) * mm});
            skLineSegment(sketch, "E4711", {"start": v(62.69, -15.32) * mm, "end": v(62.6, -15.27) * mm});
            skLineSegment(sketch, "E4712", {"start": v(62.6, -15.27) * mm, "end": v(62.52, -15.22) * mm});
            skLineSegment(sketch, "E4713", {"start": v(62.52, -15.22) * mm, "end": v(62.43, -15.18) * mm});
            skLineSegment(sketch, "E4714", {"start": v(62.43, -15.18) * mm, "end": v(62.35, -15.13) * mm});
            skLineSegment(sketch, "E4715", {"start": v(62.35, -15.13) * mm, "end": v(62.27, -15.1) * mm});
            skLineSegment(sketch, "E4716", {"start": v(62.27, -15.1) * mm, "end": v(62.19, -15.05) * mm});
            skLineSegment(sketch, "E4717", {"start": v(62.19, -15.05) * mm, "end": v(62.11, -15.01) * mm});
            skLineSegment(sketch, "E4718", {"start": v(62.11, -15.01) * mm, "end": v(62.04, -14.97) * mm});
            skLineSegment(sketch, "E4719", {"start": v(62.04, -14.97) * mm, "end": v(61.96, -14.94) * mm});
            skLineSegment(sketch, "E4720", {"start": v(61.96, -14.94) * mm, "end": v(61.9, -14.67) * mm});
            skLineSegment(sketch, "E4721", {"start": v(61.9, -14.67) * mm, "end": v(62.22, -13.22) * mm});
            skLineSegment(sketch, "E4722", {"start": v(62.22, -13.22) * mm, "end": v(62.4, -13.02) * mm});
            skLineSegment(sketch, "E4723", {"start": v(62.4, -13.02) * mm, "end": v(62.48, -13.01) * mm});
            skLineSegment(sketch, "E4724", {"start": v(62.48, -13.01) * mm, "end": v(62.56, -13.01) * mm});
            skLineSegment(sketch, "E4725", {"start": v(62.56, -13.01) * mm, "end": v(62.65, -13) * mm});
            skLineSegment(sketch, "E4726", {"start": v(62.65, -13) * mm, "end": v(62.74, -13) * mm});
            skLineSegment(sketch, "E4727", {"start": v(62.74, -13) * mm, "end": v(62.92, -13) * mm});
            skLineSegment(sketch, "E4728", {"start": v(62.92, -13) * mm, "end": v(63.02, -13) * mm});
            skLineSegment(sketch, "E4729", {"start": v(63.02, -13) * mm, "end": v(63.12, -12.99) * mm});
            skLineSegment(sketch, "E4730", {"start": v(63.12, -12.99) * mm, "end": v(63.22, -12.98) * mm});
            skLineSegment(sketch, "E4731", {"start": v(63.22, -12.98) * mm, "end": v(63.32, -12.97) * mm});
            skLineSegment(sketch, "E4732", {"start": v(63.32, -12.97) * mm, "end": v(63.42, -12.96) * mm});
            skLineSegment(sketch, "E4733", {"start": v(63.42, -12.96) * mm, "end": v(63.53, -12.96) * mm});
            skLineSegment(sketch, "E4734", {"start": v(63.53, -12.96) * mm, "end": v(63.64, -12.95) * mm});
            skLineSegment(sketch, "E4735", {"start": v(63.64, -12.95) * mm, "end": v(63.75, -12.93) * mm});
            skLineSegment(sketch, "E4736", {"start": v(63.75, -12.93) * mm, "end": v(63.86, -12.92) * mm});
            skLineSegment(sketch, "E4737", {"start": v(63.86, -12.92) * mm, "end": v(63.97, -12.91) * mm});
            skLineSegment(sketch, "E4738", {"start": v(63.97, -12.91) * mm, "end": v(64.09, -12.9) * mm});
            skLineSegment(sketch, "E4739", {"start": v(64.09, -12.9) * mm, "end": v(64.2, -12.88) * mm});
            skLineSegment(sketch, "E4740", {"start": v(64.2, -12.88) * mm, "end": v(64.33, -12.87) * mm});
            skLineSegment(sketch, "E4741", {"start": v(64.33, -12.87) * mm, "end": v(64.45, -12.85) * mm});
            skLineSegment(sketch, "E4742", {"start": v(64.45, -12.85) * mm, "end": v(64.57, -12.84) * mm});
            skLineSegment(sketch, "E4743", {"start": v(64.57, -12.84) * mm, "end": v(64.7, -12.82) * mm});
            skLineSegment(sketch, "E4744", {"start": v(64.7, -12.82) * mm, "end": v(64.83, -12.8) * mm});
            skLineSegment(sketch, "E4745", {"start": v(64.83, -12.8) * mm, "end": v(64.96, -12.78) * mm});
            skLineSegment(sketch, "E4746", {"start": v(64.96, -12.78) * mm, "end": v(65.09, -12.76) * mm});
            skLineSegment(sketch, "E4747", {"start": v(65.09, -12.76) * mm, "end": v(65.22, -12.73) * mm});
            skLineSegment(sketch, "E4748", {"start": v(65.22, -12.73) * mm, "end": v(65.36, -12.71) * mm});
            skLineSegment(sketch, "E4749", {"start": v(65.36, -12.71) * mm, "end": v(65.5, -12.69) * mm});
            skLineSegment(sketch, "E4750", {"start": v(65.5, -12.69) * mm, "end": v(65.63, -12.66) * mm});
            skLineSegment(sketch, "E4751", {"start": v(65.63, -12.66) * mm, "end": v(65.78, -12.63) * mm});
            skLineSegment(sketch, "E4752", {"start": v(65.78, -12.63) * mm, "end": v(65.92, -12.6) * mm});
            skLineSegment(sketch, "E4753", {"start": v(65.92, -12.6) * mm, "end": v(66.06, -12.57) * mm});
            skLineSegment(sketch, "E4754", {"start": v(66.06, -12.57) * mm, "end": v(66.21, -12.54) * mm});
            skLineSegment(sketch, "E4755", {"start": v(66.21, -12.54) * mm, "end": v(66.36, -12.51) * mm});
            skLineSegment(sketch, "E4756", {"start": v(66.36, -12.51) * mm, "end": v(66.66, -12.44) * mm});
            skLineSegment(sketch, "E4757", {"start": v(66.66, -12.44) * mm, "end": v(66.82, -12.4) * mm});
            skLineSegment(sketch, "E4758", {"start": v(66.82, -12.4) * mm, "end": v(66.98, -12.37) * mm});
            skLineSegment(sketch, "E4759", {"start": v(66.98, -12.37) * mm, "end": v(67.13, -12.33) * mm});
            skLineSegment(sketch, "E4760", {"start": v(67.13, -12.33) * mm, "end": v(67.24, -12.28) * mm});
            skLineSegment(sketch, "E4761", {"start": v(67.24, -12.28) * mm, "end": v(67.51, -10.68) * mm});
            skLineSegment(sketch, "E4762", {"start": v(67.51, -10.68) * mm, "end": v(67.43, -10.6) * mm});
            skLineSegment(sketch, "E4763", {"start": v(67.43, -10.6) * mm, "end": v(67.3, -10.5) * mm});
            skLineSegment(sketch, "E4764", {"start": v(67.3, -10.5) * mm, "end": v(67.16, -10.42) * mm});
            skLineSegment(sketch, "E4765", {"start": v(67.16, -10.42) * mm, "end": v(67.02, -10.33) * mm});
            skLineSegment(sketch, "E4766", {"start": v(67.02, -10.33) * mm, "end": v(66.9, -10.25) * mm});
            skLineSegment(sketch, "E4767", {"start": v(66.9, -10.25) * mm, "end": v(66.76, -10.17) * mm});
            skLineSegment(sketch, "E4768", {"start": v(66.76, -10.17) * mm, "end": v(66.63, -10.09) * mm});
            skLineSegment(sketch, "E4769", {"start": v(66.63, -10.09) * mm, "end": v(66.5, -10) * mm});
            skLineSegment(sketch, "E4770", {"start": v(66.5, -10) * mm, "end": v(66.37, -9.93) * mm});
            skLineSegment(sketch, "E4771", {"start": v(66.37, -9.93) * mm, "end": v(66.25, -9.86) * mm});
            skLineSegment(sketch, "E4772", {"start": v(66.25, -9.86) * mm, "end": v(66.12, -9.79) * mm});
            skLineSegment(sketch, "E4773", {"start": v(66.12, -9.79) * mm, "end": v(66, -9.72) * mm});
            skLineSegment(sketch, "E4774", {"start": v(66, -9.72) * mm, "end": v(65.88, -9.65) * mm});
            skLineSegment(sketch, "E4775", {"start": v(65.88, -9.65) * mm, "end": v(65.76, -9.58) * mm});
            skLineSegment(sketch, "E4776", {"start": v(65.76, -9.58) * mm, "end": v(65.52, -9.45) * mm});
            skLineSegment(sketch, "E4777", {"start": v(65.52, -9.45) * mm, "end": v(65.4, -9.39) * mm});
            skLineSegment(sketch, "E4778", {"start": v(65.4, -9.39) * mm, "end": v(65.3, -9.33) * mm});
            skLineSegment(sketch, "E4779", {"start": v(65.3, -9.33) * mm, "end": v(65.18, -9.27) * mm});
            skLineSegment(sketch, "E4780", {"start": v(65.18, -9.27) * mm, "end": v(65.07, -9.21) * mm});
            skLineSegment(sketch, "E4781", {"start": v(65.07, -9.21) * mm, "end": v(64.96, -9.16) * mm});
            skLineSegment(sketch, "E4782", {"start": v(64.96, -9.16) * mm, "end": v(64.85, -9.1) * mm});
            skLineSegment(sketch, "E4783", {"start": v(64.85, -9.1) * mm, "end": v(64.74, -9.05) * mm});
            skLineSegment(sketch, "E4784", {"start": v(64.74, -9.05) * mm, "end": v(64.64, -9) * mm});
            skLineSegment(sketch, "E4785", {"start": v(64.64, -9) * mm, "end": v(64.54, -8.95) * mm});
            skLineSegment(sketch, "E4786", {"start": v(64.54, -8.95) * mm, "end": v(64.43, -8.9) * mm});
            skLineSegment(sketch, "E4787", {"start": v(64.43, -8.9) * mm, "end": v(64.33, -8.86) * mm});
            skLineSegment(sketch, "E4788", {"start": v(64.33, -8.86) * mm, "end": v(64.23, -8.8) * mm});
            skLineSegment(sketch, "E4789", {"start": v(64.23, -8.8) * mm, "end": v(64.14, -8.77) * mm});
            skLineSegment(sketch, "E4790", {"start": v(64.14, -8.77) * mm, "end": v(64.04, -8.72) * mm});
            skLineSegment(sketch, "E4791", {"start": v(64.04, -8.72) * mm, "end": v(63.95, -8.68) * mm});
            skLineSegment(sketch, "E4792", {"start": v(63.95, -8.68) * mm, "end": v(63.86, -8.64) * mm});
            skLineSegment(sketch, "E4793", {"start": v(63.86, -8.64) * mm, "end": v(63.77, -8.6) * mm});
            skLineSegment(sketch, "E4794", {"start": v(63.77, -8.6) * mm, "end": v(63.68, -8.57) * mm});
            skLineSegment(sketch, "E4795", {"start": v(63.68, -8.57) * mm, "end": v(63.6, -8.53) * mm});
            skLineSegment(sketch, "E4796", {"start": v(63.6, -8.53) * mm, "end": v(63.5, -8.5) * mm});
            skLineSegment(sketch, "E4797", {"start": v(63.5, -8.5) * mm, "end": v(63.42, -8.47) * mm});
            skLineSegment(sketch, "E4798", {"start": v(63.42, -8.47) * mm, "end": v(63.34, -8.44) * mm});
            skLineSegment(sketch, "E4799", {"start": v(63.34, -8.44) * mm, "end": v(63.26, -8.4) * mm});
            skLineSegment(sketch, "E4800", {"start": v(63.26, -8.4) * mm, "end": v(63.18, -8.38) * mm});
            skLineSegment(sketch, "E4801", {"start": v(63.18, -8.38) * mm, "end": v(63.09, -8.12) * mm});
            skLineSegment(sketch, "E4802", {"start": v(63.09, -8.12) * mm, "end": v(63.26, -6.65) * mm});
            skLineSegment(sketch, "E4803", {"start": v(63.26, -6.65) * mm, "end": v(63.41, -6.42) * mm});
            skLineSegment(sketch, "E4804", {"start": v(63.41, -6.42) * mm, "end": v(63.5, -6.41) * mm});
            skLineSegment(sketch, "E4805", {"start": v(63.5, -6.41) * mm, "end": v(63.58, -6.4) * mm});
            skLineSegment(sketch, "E4806", {"start": v(63.58, -6.4) * mm, "end": v(63.67, -6.39) * mm});
            skLineSegment(sketch, "E4807", {"start": v(63.67, -6.39) * mm, "end": v(63.75, -6.38) * mm});
            skLineSegment(sketch, "E4808", {"start": v(63.75, -6.38) * mm, "end": v(63.84, -6.36) * mm});
            skLineSegment(sketch, "E4809", {"start": v(63.84, -6.36) * mm, "end": v(63.94, -6.35) * mm});
            skLineSegment(sketch, "E4810", {"start": v(63.94, -6.35) * mm, "end": v(64.03, -6.33) * mm});
            skLineSegment(sketch, "E4811", {"start": v(64.03, -6.33) * mm, "end": v(64.13, -6.32) * mm});
            skLineSegment(sketch, "E4812", {"start": v(64.13, -6.32) * mm, "end": v(64.23, -6.3) * mm});
            skLineSegment(sketch, "E4813", {"start": v(64.23, -6.3) * mm, "end": v(64.33, -6.28) * mm});
            skLineSegment(sketch, "E4814", {"start": v(64.33, -6.28) * mm, "end": v(64.43, -6.26) * mm});
            skLineSegment(sketch, "E4815", {"start": v(64.43, -6.26) * mm, "end": v(64.53, -6.24) * mm});
            skLineSegment(sketch, "E4816", {"start": v(64.53, -6.24) * mm, "end": v(64.64, -6.22) * mm});
            skLineSegment(sketch, "E4817", {"start": v(64.64, -6.22) * mm, "end": v(64.75, -6.2) * mm});
            skLineSegment(sketch, "E4818", {"start": v(64.75, -6.2) * mm, "end": v(64.86, -6.18) * mm});
            skLineSegment(sketch, "E4819", {"start": v(64.86, -6.18) * mm, "end": v(64.97, -6.15) * mm});
            skLineSegment(sketch, "E4820", {"start": v(64.97, -6.15) * mm, "end": v(65.08, -6.13) * mm});
            skLineSegment(sketch, "E4821", {"start": v(65.08, -6.13) * mm, "end": v(65.2, -6.1) * mm});
            skLineSegment(sketch, "E4822", {"start": v(65.2, -6.1) * mm, "end": v(65.32, -6.07) * mm});
            skLineSegment(sketch, "E4823", {"start": v(65.32, -6.07) * mm, "end": v(65.44, -6.05) * mm});
            skLineSegment(sketch, "E4824", {"start": v(65.44, -6.05) * mm, "end": v(65.56, -6.02) * mm});
            skLineSegment(sketch, "E4825", {"start": v(65.56, -6.02) * mm, "end": v(65.68, -5.98) * mm});
            skLineSegment(sketch, "E4826", {"start": v(65.68, -5.98) * mm, "end": v(65.8, -5.95) * mm});
            skLineSegment(sketch, "E4827", {"start": v(65.8, -5.95) * mm, "end": v(65.93, -5.92) * mm});
            skLineSegment(sketch, "E4828", {"start": v(65.93, -5.92) * mm, "end": v(66.06, -5.88) * mm});
            skLineSegment(sketch, "E4829", {"start": v(66.06, -5.88) * mm, "end": v(66.2, -5.85) * mm});
            skLineSegment(sketch, "E4830", {"start": v(66.2, -5.85) * mm, "end": v(66.33, -5.8) * mm});
            skLineSegment(sketch, "E4831", {"start": v(66.33, -5.8) * mm, "end": v(66.46, -5.77) * mm});
            skLineSegment(sketch, "E4832", {"start": v(66.46, -5.77) * mm, "end": v(66.6, -5.73) * mm});
            skLineSegment(sketch, "E4833", {"start": v(66.6, -5.73) * mm, "end": v(66.74, -5.69) * mm});
            skLineSegment(sketch, "E4834", {"start": v(66.74, -5.69) * mm, "end": v(67.02, -5.6) * mm});
            skLineSegment(sketch, "E4835", {"start": v(67.02, -5.6) * mm, "end": v(67.16, -5.55) * mm});
            skLineSegment(sketch, "E4836", {"start": v(67.16, -5.55) * mm, "end": v(67.3, -5.5) * mm});
            skLineSegment(sketch, "E4837", {"start": v(67.3, -5.5) * mm, "end": v(67.45, -5.46) * mm});
            skLineSegment(sketch, "E4838", {"start": v(67.45, -5.46) * mm, "end": v(67.6, -5.4) * mm});
            skLineSegment(sketch, "E4839", {"start": v(67.6, -5.4) * mm, "end": v(67.75, -5.36) * mm});
            skLineSegment(sketch, "E4840", {"start": v(67.75, -5.36) * mm, "end": v(67.9, -5.3) * mm});
            skLineSegment(sketch, "E4841", {"start": v(67.9, -5.3) * mm, "end": v(68.06, -5.25) * mm});
            skLineSegment(sketch, "E4842", {"start": v(68.06, -5.25) * mm, "end": v(68.15, -5.18) * mm});
            skLineSegment(sketch, "E4843", {"start": v(68.15, -5.18) * mm, "end": v(68.26, -3.56) * mm});
            skLineSegment(sketch, "E4844", {"start": v(68.26, -3.56) * mm, "end": v(68.17, -3.49) * mm});
            skLineSegment(sketch, "E4845", {"start": v(68.17, -3.49) * mm, "end": v(68.02, -3.41) * mm});
            skLineSegment(sketch, "E4846", {"start": v(68.02, -3.41) * mm, "end": v(67.88, -3.34) * mm});
            skLineSegment(sketch, "E4847", {"start": v(67.88, -3.34) * mm, "end": v(67.74, -3.27) * mm});
            skLineSegment(sketch, "E4848", {"start": v(67.74, -3.27) * mm, "end": v(67.6, -3.2) * mm});
            skLineSegment(sketch, "E4849", {"start": v(67.6, -3.2) * mm, "end": v(67.46, -3.13) * mm});
            skLineSegment(sketch, "E4850", {"start": v(67.46, -3.13) * mm, "end": v(67.32, -3.07) * mm});
            skLineSegment(sketch, "E4851", {"start": v(67.32, -3.07) * mm, "end": v(67.18, -3) * mm});
            skLineSegment(sketch, "E4852", {"start": v(67.18, -3) * mm, "end": v(67.05, -2.94) * mm});
            skLineSegment(sketch, "E4853", {"start": v(67.05, -2.94) * mm, "end": v(66.92, -2.88) * mm});
            skLineSegment(sketch, "E4854", {"start": v(66.92, -2.88) * mm, "end": v(66.78, -2.82) * mm});
            skLineSegment(sketch, "E4855", {"start": v(66.78, -2.82) * mm, "end": v(66.65, -2.76) * mm});
            skLineSegment(sketch, "E4856", {"start": v(66.65, -2.76) * mm, "end": v(66.53, -2.7) * mm});
            skLineSegment(sketch, "E4857", {"start": v(66.53, -2.7) * mm, "end": v(66.4, -2.65) * mm});
            skLineSegment(sketch, "E4858", {"start": v(66.4, -2.65) * mm, "end": v(66.27, -2.6) * mm});
            skLineSegment(sketch, "E4859", {"start": v(66.27, -2.6) * mm, "end": v(66.15, -2.55) * mm});
            skLineSegment(sketch, "E4860", {"start": v(66.15, -2.55) * mm, "end": v(66.03, -2.5) * mm});
            skLineSegment(sketch, "E4861", {"start": v(66.03, -2.5) * mm, "end": v(65.9, -2.45) * mm});
            skLineSegment(sketch, "E4862", {"start": v(65.9, -2.45) * mm, "end": v(65.8, -2.4) * mm});
            skLineSegment(sketch, "E4863", {"start": v(65.8, -2.4) * mm, "end": v(65.67, -2.36) * mm});
            skLineSegment(sketch, "E4864", {"start": v(65.67, -2.36) * mm, "end": v(65.56, -2.31) * mm});
            skLineSegment(sketch, "E4865", {"start": v(65.56, -2.31) * mm, "end": v(65.45, -2.27) * mm});
            skLineSegment(sketch, "E4866", {"start": v(65.45, -2.27) * mm, "end": v(65.33, -2.23) * mm});
            skLineSegment(sketch, "E4867", {"start": v(65.33, -2.23) * mm, "end": v(65.22, -2.2) * mm});
            skLineSegment(sketch, "E4868", {"start": v(65.22, -2.2) * mm, "end": v(65.12, -2.15) * mm});
            skLineSegment(sketch, "E4869", {"start": v(65.12, -2.15) * mm, "end": v(65.01, -2.12) * mm});
            skLineSegment(sketch, "E4870", {"start": v(65.01, -2.12) * mm, "end": v(64.9, -2.08) * mm});
            skLineSegment(sketch, "E4871", {"start": v(64.9, -2.08) * mm, "end": v(64.8, -2.05) * mm});
            skLineSegment(sketch, "E4872", {"start": v(64.8, -2.05) * mm, "end": v(64.7, -2.01) * mm});
            skLineSegment(sketch, "E4873", {"start": v(64.7, -2.01) * mm, "end": v(64.6, -1.98) * mm});
            skLineSegment(sketch, "E4874", {"start": v(64.6, -1.98) * mm, "end": v(64.5, -1.95) * mm});
            skLineSegment(sketch, "E4875", {"start": v(64.5, -1.95) * mm, "end": v(64.4, -1.92) * mm});
            skLineSegment(sketch, "E4876", {"start": v(64.4, -1.92) * mm, "end": v(64.32, -1.9) * mm});
            skLineSegment(sketch, "E4877", {"start": v(64.32, -1.9) * mm, "end": v(64.13, -1.84) * mm});
            skLineSegment(sketch, "E4878", {"start": v(64.13, -1.84) * mm, "end": v(63.96, -1.8) * mm});
            skLineSegment(sketch, "E4879", {"start": v(63.96, -1.8) * mm, "end": v(63.88, -1.77) * mm});
            skLineSegment(sketch, "E4880", {"start": v(63.88, -1.77) * mm, "end": v(63.8, -1.75) * mm});
            skLineSegment(sketch, "E4881", {"start": v(63.8, -1.75) * mm, "end": v(63.71, -1.73) * mm});
            skLineSegment(sketch, "E4882", {"start": v(63.71, -1.73) * mm, "end": v(63.6, -1.48) * mm});
            skLineSegment(sketch, "E4883", {"start": v(63.6, -1.48) * mm, "end": v(63.61, 0) * mm});
            skLineSegment(sketch, "E4884", {"start": v(2.65, 0) * mm, "end": v(-2.65, 0) * mm});
            skLineSegment(sketch, "E4885", {"start": v(0, -2.65) * mm, "end": v(0, 2.65) * mm});
            skCircle(sketch, "E4886", {"center": v(0, 0) * mm, "radius": 2.04 * mm});
            skSolve(sketch);
        }
        {
            var Q0;
            Q0=makeQuery(id+"F0.imprint","IMPRINT",FACE,{"disambiguationData":[TD([[makeQuery(id+"F0.imprint","IMPRINT",EDGE,{"derivedFrom":sQuery(id+"F0.wireOp",EDGE,"E0")}),1.0]])]});
            extrude(context, id + "F1", {"entities" : qUnion([Q0]), "depth" : 6.5 * mm, "offsetDistance" : 25 * mm});
        }
    });
